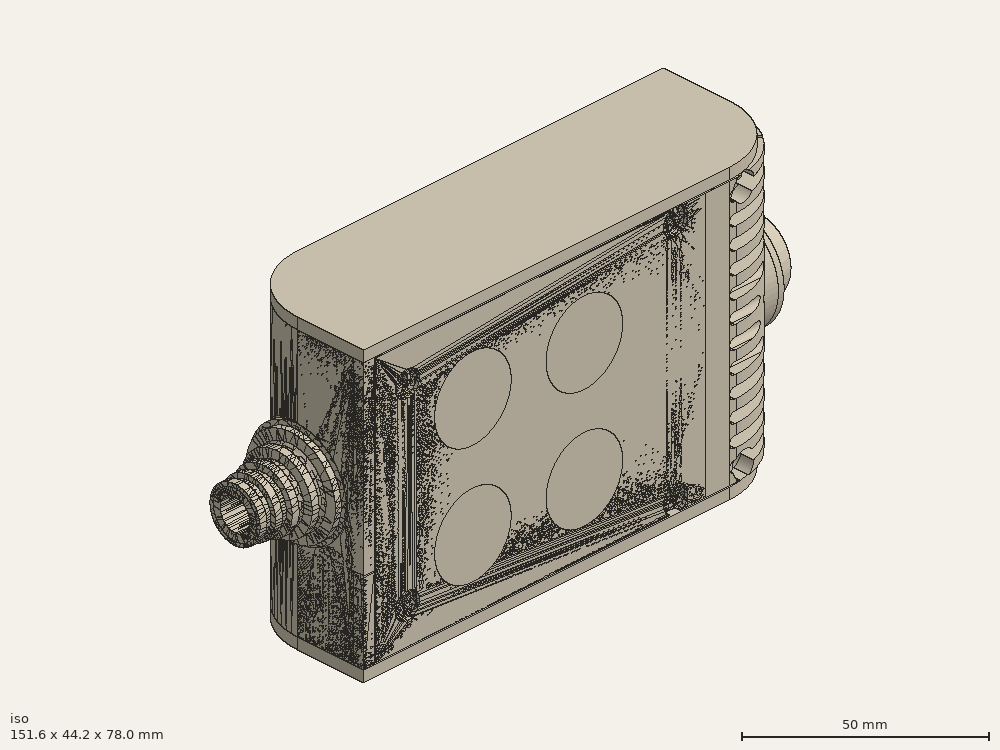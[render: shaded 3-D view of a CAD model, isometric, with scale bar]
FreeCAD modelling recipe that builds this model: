
FCSTD DOCUMENT  (FreeCAD 0.19R0.19.2)
Label: enclosure_170FCStd
License: All rights reserved
LicenseURL: http://en.wikipedia.org/wiki/All_rights_reserved
objects: Part::Revolution×146, Part::Feature×140, Part::MultiFuse×135, Sketcher::SketchObject×76, Part::Cut×63, Part::Cylinder×62, Part::Extrusion×61, Part::Fillet×54, Part::Box×36, App::MeasureDistance×4
note: 773 computed .brp shape members not serialized (recipe doc carries the construction recipe); baked Part::Feature solids carry a one-line shape summary decoded from their .brp

FEATURE [Sketcher::SketchObject] Sketch  label="topSketch"
  FullyConstrained = true
  sketch-geometry (20):
    g0: LineSegment StartX=5.21097e-06 StartY=3 StartZ=0 EndX=5.21097e-06 EndY=19 EndZ=0
    g1: ArcOfCircle CenterX=19 CenterY=19 CenterZ=0 NormalX=0 NormalY=0 NormalZ=1 AngleXU=0 Radius=19 StartAngle=1.5708 EndAngle=3.14159
    g2: ArcOfCircle CenterX=19 CenterY=19 CenterZ=0 NormalX=0 NormalY=0 NormalZ=1 AngleXU=0 Radius=16 StartAngle=1.5708 EndAngle=3.14159
    g3: LineSegment StartX=114 StartY=35 StartZ=0 EndX=19 EndY=35 EndZ=0
    g4: LineSegment StartX=5.21097e-06 StartY=3 StartZ=0 EndX=5.21097e-06 EndY=0 EndZ=0
    g5: LineSegment StartX=3 StartY=0 StartZ=0 EndX=5.21097e-06 EndY=0 EndZ=0
    g6: LineSegment StartX=3 StartY=19 StartZ=0 EndX=3 EndY=0 EndZ=0
    g7: LineSegment StartX=19 StartY=38 StartZ=0 EndX=124 EndY=38 EndZ=0
    g8: Circle CenterX=119 CenterY=35 CenterZ=0 NormalX=0 NormalY=0 NormalZ=1 AngleXU=0 Radius=1
    g9: Circle CenterX=121 CenterY=35 CenterZ=0 NormalX=0 NormalY=0 NormalZ=1 AngleXU=0 Radius=1
    g10: Circle CenterX=121 CenterY=33 CenterZ=0 NormalX=0 NormalY=0 NormalZ=1 AngleXU=0 Radius=1
    g11: BSplineCurve PolesCount=3 KnotsCount=2 Degree=2 IsPeriodic=0
    g12: GeomPoint X=119 Y=35 Z=0
    g13: GeomPoint X=121 Y=33 Z=0
    g14: LineSegment StartX=119 StartY=35 StartZ=0 EndX=114 EndY=35 EndZ=0
    g15: ArcOfCircle CenterX=105 CenterY=19 CenterZ=0 NormalX=0 NormalY=0 NormalZ=1 AngleXU=0 Radius=19 StartAngle=5.7297 EndAngle=6.28319
    g16: ArcOfCircle CenterX=105 CenterY=19 CenterZ=0 NormalX=0 NormalY=0 NormalZ=1 AngleXU=0 Radius=16 StartAngle=5.60905 EndAngle=6.28319
    g17: LineSegment StartX=121 StartY=33 StartZ=0 EndX=121 EndY=19 EndZ=0
    g18: LineSegment StartX=124 StartY=38 StartZ=0 EndX=124 EndY=19 EndZ=0
    g19: LineSegment StartX=117.5 StartY=9.01251 StartZ=0 EndX=121.163 EndY=9.0125 EndZ=0
  constraints (46):
    c: Vertical(g0)
    c: Block(g0)
    c: Coincident(g1,g0)
    c: Block(g1)
    c: Coincident(g2,g1)
    c: Block(g2)
    c: Coincident(g3,g2)
    c: Horizontal(g3)
    c: Tangent(g3,g2)
    c: Coincident(g4,g0)
    c: Distance(g4) = 3
    c: Vertical(g4)
    c: Coincident(g5,g4)
    c: Horizontal(g5)
    c: Coincident(g6,g2)
    c: Coincident(g6,g5)
    c: Vertical(g6)
    c: Horizontal(g7)
    c: Distance(g7) = 105
    c: Coincident(g7,g1)
    c: Block(g3)
    c: Weight(g8) = 1
    c: Equal(g8,g9)
    c: Equal(g8,g10)
    c: InternalAlignment(g8,g11)
    c: InternalAlignment(g9,g11)
    c: InternalAlignment(g10,g11)
    c: InternalAlignment(g12,g11)
    c: InternalAlignment(g13,g11)
    c: Block(g11)
    c: Coincident(g14,g11)
    c: Coincident(g14,g3)
    c: Horizontal(g14)
    c: Block(g15)
    c: Coincident(g16,g15)
    c: Block(g16)
    c: Coincident(g17,g11)
    c: Coincident(g17,g16)
    c: Vertical(g17)
    c: Distance(g17) = 14
    c: Coincident(g18,g7)
    c: Coincident(g18,g15)
    c: Vertical(g18)
    c: Distance(g18) = 19
    c: Coincident(g19,g16)
    c: Coincident(g19,g15)
FEATURE [Sketcher::SketchObject] Sketch001  label="bottomSketch"
  FullyConstrained = true
  sketch-geometry (32):
    g0: LineSegment StartX=3.3 StartY=-6.03275e-07 StartZ=0 EndX=98 EndY=-6.03275e-07 EndZ=0
    g1: ArcOfCircle CenterX=98 CenterY=19 CenterZ=0 NormalX=0 NormalY=0 NormalZ=1 AngleXU=0 Radius=19 StartAngle=4.71239 EndAngle=5.71103
    g2: LineSegment StartX=6.3 StartY=8 StartZ=0 EndX=3.3 EndY=8 EndZ=0
    g3: LineSegment StartX=3.3 StartY=8 StartZ=0 EndX=3.3 EndY=-6.03275e-07 EndZ=0
    g4: ArcOfCircle CenterX=8.3 CenterY=5 CenterZ=0 NormalX=0 NormalY=0 NormalZ=1 AngleXU=0 Radius=2 StartAngle=3.14159 EndAngle=4.71239
    g5: LineSegment StartX=6.3 StartY=8 StartZ=0 EndX=6.3 EndY=5 EndZ=0
    g6: ArcOfCircle CenterX=98 CenterY=19 CenterZ=0 NormalX=0 NormalY=0 NormalZ=1 AngleXU=0 Radius=12.7 StartAngle=4.71239 EndAngle=6.28319
    g7: LineSegment StartX=94.7 StartY=3 StartZ=0 EndX=8.3 EndY=3 EndZ=0
    g8-g12: Circle x5 (B-spline internal-alignment scaffolding for g13; pole/knot coordinates omitted)
    g13: BSplineCurve PolesCount=5 KnotsCount=3 Degree=3 IsPeriodic=0
    g14: GeomPoint X=98 Y=6.3 Z=0
    g15: GeomPoint X=96.3938 Y=4.71946 Z=0
    g16: GeomPoint X=94.7 Y=3 Z=0
    g17-g23: Circle x7 (B-spline internal-alignment scaffolding for g24; pole/knot coordinates omitted)
    g24: BSplineCurve PolesCount=7 KnotsCount=5 Degree=3 IsPeriodic=0
    g25-g29: GeomPoint x5 (B-spline internal-alignment scaffolding for g24; pole/knot coordinates omitted)
    g30: ArcOfCircle CenterX=98 CenterY=19 CenterZ=0 NormalX=0 NormalY=0 NormalZ=1 AngleXU=0 Radius=15.7 StartAngle=5.81226 EndAngle=6.28319
    g31: LineSegment StartX=110.7 StartY=19 StartZ=0 EndX=113.7 EndY=19 EndZ=0
  constraints (41):
    c: Horizontal(g0)
    c: Coincident(g1,g0)
    c: Block(g1)
    c: Horizontal(g2)
    c: Distance(g2) = 3
    c: Coincident(g3,g2)
    c: Vertical(g3)
    c: Coincident(g3,g0)
    c: Block(g4)
    c: Block(g2)
    c: Coincident(g5,g2)
    c: Coincident(g5,g4)
    c: Vertical(g5)
    c: Coincident(g6,g1)
    c: Block(g6)
    c: Coincident(g7,g4)
    c: Horizontal(g7)
    c: Block(g0)
    c: Block(g7)
    c: Block(g3)
    c: Coincident(g13,g6)
    c: Weight(g8) = 1
    c: Equal(g8, g9-g12) x4
    c: Coincident(g13,g7)
    c: InternalAlignment(g8-g12 -> g13) x5
    c: InternalAlignment(g14,g13)
    c: InternalAlignment(g15,g13)
    c: InternalAlignment(g16,g13)
    c: Block(g13)
    c: Weight(g17) = 1
    c: Equal(g17, g18-g23) x6
    c: Coincident(g24,g1)
    c: InternalAlignment(g17-g23 -> g24) x7
    c: InternalAlignment(g25-g29 -> g24) x5
    c: Block(g24)
    c: Coincident(g30,g24)
    c: Coincident(g31,g6)
    c: Coincident(g31,g30)
    c: Horizontal(g31)
    c: Block(g31)
    c: Block(g30)
FEATURE [Part::Extrusion] Extrude  label="top"
  Base = -> Sketch
  Dir = (0,0,1)
  DirMode = 2
  FaceMakerClass = Part::FaceMakerBullseye
  LengthFwd = 72
  LengthRev = 0
  Solid = true
  Symmetric = false
FEATURE [Part::Extrusion] Extrude001  label="bottom"
  Base = -> Sketch001
  Dir = (0,0,1)
  DirMode = 2
  FaceMakerClass = Part::FaceMakerBullseye
  LengthFwd = 71.4
  LengthRev = 0
  Placement = pos=(0,0,0.3) rot=(0,0,1;0rad)
  Solid = true
  Symmetric = false
FEATURE [Sketcher::SketchObject] Sketch002  label="topSketch001"
  FullyConstrained = true
  sketch-geometry (6):
    g0: ArcOfCircle CenterX=19 CenterY=19 CenterZ=0 NormalX=0 NormalY=0 NormalZ=1 AngleXU=0 Radius=19 StartAngle=1.5708 EndAngle=3.14159
    g1: LineSegment StartX=5.22862e-06 StartY=19 StartZ=0 EndX=5.22862e-06 EndY=1.19904e-11 EndZ=0
    g2: LineSegment StartX=19 StartY=38 StartZ=0 EndX=124 EndY=38 EndZ=0
    g3: LineSegment StartX=5.22862e-06 StartY=1.19904e-11 StartZ=0 EndX=105 EndY=1.19904e-11 EndZ=0
    g4: ArcOfCircle CenterX=105 CenterY=19 CenterZ=0 NormalX=0 NormalY=0 NormalZ=1 AngleXU=0 Radius=19 StartAngle=4.71239 EndAngle=6.28319
    g5: LineSegment StartX=124 StartY=38 StartZ=0 EndX=124 EndY=19 EndZ=0
  constraints (16):
    c: Block(g0)
    c: Coincident(g1,g0)
    c: Vertical(g1)
    c: Horizontal(g2)
    c: Distance(g2) = 105
    c: Coincident(g2,g0)
    c: Distance(g1) = 19
    c: Coincident(g3,g1)
    c: Horizontal(g3)
    c: Distance(g3) = 105
    c: Block(g4)
    c: Coincident(g4,g3)
    c: Coincident(g5,g2)
    c: Coincident(g5,g4)
    c: Vertical(g5)
    c: Distance(g5) = 19
FEATURE [Part::Extrusion] Extrude002  label="sideA"
  Base = -> Sketch002
  Dir = (0,0,1)
  DirMode = 2
  FaceMakerClass = Part::FaceMakerBullseye
  LengthFwd = 3
  LengthRev = 0
  Placement = pos=(0,0,-3) rot=(0,0,1;0rad)
  Solid = true
  Symmetric = false
FEATURE [Sketcher::SketchObject] Sketch003  label="topSketch002"
  FullyConstrained = true
  sketch-geometry (6):
    g0: LineSegment StartX=19 StartY=38 StartZ=0 EndX=117 EndY=38 EndZ=0
    g1: ArcOfCircle CenterX=19 CenterY=19 CenterZ=0 NormalX=0 NormalY=0 NormalZ=1 AngleXU=0 Radius=19 StartAngle=1.5708 EndAngle=3.14159
    g2: LineSegment StartX=117 StartY=38 StartZ=0 EndX=117 EndY=19 EndZ=0
    g3: LineSegment StartX=98 StartY=1.0161e-12 StartZ=0 EndX=5.22862e-06 EndY=1.0161e-12 EndZ=0
    g4: LineSegment StartX=5.22862e-06 StartY=19 StartZ=0 EndX=5.22862e-06 EndY=1.0161e-12 EndZ=0
    g5: ArcOfCircle CenterX=98 CenterY=19 CenterZ=0 NormalX=0 NormalY=0 NormalZ=1 AngleXU=0 Radius=19 StartAngle=4.71239 EndAngle=6.28319
  constraints (16):
    c: Horizontal(g0)
    c: Distance(g0) = 98
    c: Coincident(g1,g0)
    c: Block(g1)
    c: Coincident(g2,g0)
    c: Vertical(g2)
    c: Distance(g2) = 19
    c: Horizontal(g3)
    c: Coincident(g4,g1)
    c: Vertical(g4)
    c: Coincident(g3,g4)
    c: Block(g3)
    c: Coincident(g5,g2)
    c: Coincident(g5,g3)
    c: Block(g0)
    c: Block(g5)
FEATURE [Sketcher::SketchObject] Sketch004
  FullyConstrained = true
  MapMode = 3
  Placement = pos=(0,0,0) rot=(1,0,0;1.5708rad)
  Support = -> [Extrude]
  sketch-geometry (8):
    g0: Circle CenterX=80.351 CenterY=-67.6202 CenterZ=0 NormalX=0 NormalY=0 NormalZ=1 AngleXU=0 Radius=2
    g1: Circle CenterX=80.351 CenterY=-67.6202 CenterZ=0 NormalX=0 NormalY=0 NormalZ=1 AngleXU=0 Radius=3
    g2: Circle CenterX=80.351 CenterY=-4.92017 CenterZ=0 NormalX=0 NormalY=0 NormalZ=1 AngleXU=0 Radius=2
    g3: Circle CenterX=80.351 CenterY=-4.92017 CenterZ=0 NormalX=0 NormalY=0 NormalZ=1 AngleXU=0 Radius=3
    g4: Circle CenterX=23.851 CenterY=-4.92017 CenterZ=0 NormalX=0 NormalY=0 NormalZ=1 AngleXU=0 Radius=2
    g5: Circle CenterX=23.851 CenterY=-4.92017 CenterZ=0 NormalX=0 NormalY=0 NormalZ=1 AngleXU=0 Radius=3
    g6: Circle CenterX=23.851 CenterY=-67.6202 CenterZ=0 NormalX=0 NormalY=0 NormalZ=1 AngleXU=0 Radius=2
    g7: Circle CenterX=23.851 CenterY=-67.6202 CenterZ=0 NormalX=0 NormalY=0 NormalZ=1 AngleXU=0 Radius=3
  constraints (8):
    c: Block(g3)
    c: Block(g2)
    c: Block(g1)
    c: Block(g0)
    c: Block(g6)
    c: Block(g7)
    c: Block(g4)
    c: Block(g5)
FEATURE [Part::Extrusion] Extrude004
  Base = -> Sketch004
  Dir = (0,-1,2e-16)
  DirMode = 2
  FaceMakerClass = Part::FaceMakerBullseye
  LengthFwd = 6
  LengthRev = 0
  Placement = pos=(0,9,0) rot=(0,0,1;0rad)
  Solid = true
  Symmetric = false
FEATURE [Sketcher::SketchObject] Sketch005
  FullyConstrained = true
  MapMode = 3
  Placement = pos=(0,0,0) rot=(1,0,0;1.5708rad)
  Support = -> [Extrude]
  sketch-geometry (8):
    g0: Circle CenterX=80.351 CenterY=-67.6202 CenterZ=0 NormalX=0 NormalY=0 NormalZ=1 AngleXU=0 Radius=3
    g1: Circle CenterX=80.351 CenterY=-4.92017 CenterZ=0 NormalX=0 NormalY=0 NormalZ=1 AngleXU=0 Radius=3
    g2: Circle CenterX=23.851 CenterY=-4.92017 CenterZ=0 NormalX=0 NormalY=0 NormalZ=1 AngleXU=0 Radius=3
    g3: Circle CenterX=23.851 CenterY=-67.6202 CenterZ=0 NormalX=0 NormalY=0 NormalZ=1 AngleXU=0 Radius=3
    g4: Circle CenterX=23.851 CenterY=-67.6202 CenterZ=0 NormalX=0 NormalY=0 NormalZ=1 AngleXU=0 Radius=5
    g5: Circle CenterX=80.351 CenterY=-67.6202 CenterZ=0 NormalX=0 NormalY=0 NormalZ=1 AngleXU=0 Radius=5
    g6: Circle CenterX=23.851 CenterY=-4.92017 CenterZ=0 NormalX=0 NormalY=0 NormalZ=1 AngleXU=0 Radius=5
    g7: Circle CenterX=80.351 CenterY=-4.92017 CenterZ=0 NormalX=0 NormalY=0 NormalZ=1 AngleXU=0 Radius=5
  constraints (8):
    c: Block(g1)
    c: Block(g0)
    c: Block(g3)
    c: Block(g2)
    c: Block(g5)
    c: Block(g4)
    c: Block(g6)
    c: Block(g7)
FEATURE [Part::Extrusion] Extrude005
  Base = -> Sketch005
  Dir = (0,-1,2e-16)
  DirMode = 2
  FaceMakerClass = Part::FaceMakerBullseye
  LengthFwd = 2
  LengthRev = 0
  Solid = true
  Symmetric = false
FEATURE [Sketcher::SketchObject] Sketch006
  FullyConstrained = true
  MapMode = 3
  Placement = pos=(0,0,0) rot=(1,0,0;1.5708rad)
  sketch-geometry (8):
    g0: Circle CenterX=80.351 CenterY=-67.6202 CenterZ=0 NormalX=0 NormalY=0 NormalZ=1 AngleXU=0 Radius=3
    g1: Circle CenterX=80.351 CenterY=-4.92017 CenterZ=0 NormalX=0 NormalY=0 NormalZ=1 AngleXU=0 Radius=3
    g2: Circle CenterX=23.851 CenterY=-4.92017 CenterZ=0 NormalX=0 NormalY=0 NormalZ=1 AngleXU=0 Radius=3
    g3: Circle CenterX=23.851 CenterY=-67.6202 CenterZ=0 NormalX=0 NormalY=0 NormalZ=1 AngleXU=0 Radius=3
    g4: Circle CenterX=23.851 CenterY=-67.6202 CenterZ=0 NormalX=0 NormalY=0 NormalZ=1 AngleXU=0 Radius=5
    g5: Circle CenterX=80.351 CenterY=-67.6202 CenterZ=0 NormalX=0 NormalY=0 NormalZ=1 AngleXU=0 Radius=5
    g6: Circle CenterX=23.851 CenterY=-4.92017 CenterZ=0 NormalX=0 NormalY=0 NormalZ=1 AngleXU=0 Radius=5
    g7: Circle CenterX=80.351 CenterY=-4.92017 CenterZ=0 NormalX=0 NormalY=0 NormalZ=1 AngleXU=0 Radius=5
  constraints (8):
    c: Block(g1)
    c: Block(g0)
    c: Block(g3)
    c: Block(g2)
    c: Block(g5)
    c: Block(g4)
    c: Block(g6)
    c: Block(g7)
FEATURE [Part::Extrusion] Extrude007
  Base = -> Sketch006
  Dir = (0,-1,2e-16)
  DirMode = 2
  FaceMakerClass = Part::FaceMakerBullseye
  LengthFwd = 2
  LengthRev = 0
  Solid = true
  Symmetric = false
FEATURE [Part::Fillet] Fillet
  Base = -> Extrude007
  Edges = 4 edges r=1.99: [Edge6,Edge12,Edge18,Edge24]
FEATURE [Part::Cut] Cut
  Base = -> Extrude005
  Placement = pos=(0,5,0) rot=(0,0,1;0rad)
  Tool = -> Fillet
FEATURE [Part::MultiFuse] Fusion  label="pCBScrews"
  Placement = pos=(-2.5,0,72.3) rot=(0,0,1;0rad)
  Shapes = -> [Extrude004,Cut]
FEATURE [App::MeasureDistance] Distance  label="Distance: 0.69 mm"
  Distance = 0.685967
  P1 = (24.0138,2.9647,0.3)
  P2 = (23.8901,3,-0.373787)
FEATURE [App::MeasureDistance] Distance001  label="Distance: 0.53 mm"
  Distance = 0.533607
  P1 = (80.2939,3,72.2334)
  P2 = (80.281,2.99661,71.7)
FEATURE [Part::Fillet] Fillet001
  Base = -> Extrude001
  Edges = 1 edges r=2.4: [Edge17]
FEATURE [Part::Fillet] Fillet002  label="bottom001"
  Base = -> Fillet001
  Edges = 1 edges r=2.4: [Edge36]
FEATURE [Part::Fillet] Fillet003  label="top001"
  Base = -> Extrude
  Edges = 1 edges r=2: [Edge1]
FEATURE [Sketcher::SketchObject] Sketch007
  FullyConstrained = true
  sketch-geometry (16):
    g0: LineSegment StartX=4 StartY=0 StartZ=0 EndX=4 EndY=2.4 EndZ=0
    g1: LineSegment StartX=4 StartY=2.4 StartZ=0 EndX=7 EndY=2.4 EndZ=0
    g2: LineSegment StartX=4 StartY=0 StartZ=0 EndX=5.7 EndY=0 EndZ=0
    g3: LineSegment StartX=5.7 StartY=0 StartZ=0 EndX=5.7 EndY=-5.6 EndZ=0
    g4-g8: Circle x5 (B-spline internal-alignment scaffolding for g9; pole/knot coordinates omitted)
    g9: BSplineCurve PolesCount=5 KnotsCount=3 Degree=3 IsPeriodic=0
    g10: GeomPoint X=7 Y=2.4 Z=0
    g11: GeomPoint X=10.4582 Y=-1.55472 Z=0
    g12: GeomPoint X=14 Y=-5.6 Z=0
    g13: LineSegment StartX=14 StartY=-5.6 StartZ=0 EndX=14 EndY=-14.1 EndZ=0
    g14: LineSegment StartX=14 StartY=-14.1 StartZ=0 EndX=6.5 EndY=-14.1 EndZ=0
    g15: LineSegment StartX=5.7 StartY=-5.6 StartZ=0 EndX=6.5 EndY=-14.1 EndZ=0
  constraints (28):
    c: Distance(g0) = 2.4
    c: Vertical(g0)
    c: Block(g0)
    c: Coincident(g1,g0)
    c: Horizontal(g1)
    c: Distance(g1) = 3
    c: Coincident(g2,g0)
    c: Horizontal(g2)
    c: Distance(g2) = 1.7
    c: Coincident(g3,g2)
    c: Vertical(g3)
    c: Distance(g3) = 5.6
    c: Coincident(g9,g1)
    c: Weight(g4) = 1
    c: Equal(g4, g5-g8) x4
    c: InternalAlignment(g4-g8 -> g9) x5
    c: InternalAlignment(g10,g9)
    c: InternalAlignment(g11,g9)
    c: InternalAlignment(g12,g9)
    c: Block(g9)
    c: Coincident(g13,g9)
    c: Vertical(g13)
    c: Distance(g13) = 8.5
    c: Coincident(g14,g13)
    c: Horizontal(g14)
    c: Distance(g14) = 7.5
    c: Coincident(g15,g3)
    c: Coincident(g15,g14)
FEATURE [Part::Feature] Face
  shape: bbox 10 x 16.5 x 2e-07 mm, 1 faces, 0 solids (baked)
FEATURE [Part::Revolution] Revolve  label="plugHousing"
  Angle = 360
  Axis = (0,1,0)
  Base = (0,0,0)
  FaceMakerClass = Part::FaceMakerBullseye
  Placement = pos=(0,0,36.15) rot=(0,0,1;0rad)
  Solid = false
  Source = -> Face
  Symmetric = false
FEATURE [Part::Feature] Face001
  shape: bbox 10 x 16.5 x 2e-07 mm, 1 faces, 0 solids (baked)
FEATURE [Part::Revolution] Revolve001  label="plugHousing001"
  Angle = 360
  Axis = (0,1,0)
  Base = (0,0,0)
  FaceMakerClass = Part::FaceMakerBullseye
  Placement = pos=(0,0,36.15) rot=(0,0,1;0rad)
  Solid = false
  Source = -> Face001
  Symmetric = false
FEATURE [Part::MultiFuse] Fusion001  label="plugHousing002"
  Placement = pos=(0,0,0) rot=(0,0,1;1.5708rad)
  Shapes = -> [Revolve001,Revolve]
FEATURE [Part::Feature] Face002
  shape: bbox 10 x 16.5 x 2e-07 mm, 1 faces, 0 solids (baked)
FEATURE [Part::Revolution] Revolve003  label="plugHousing005"
  Angle = 360
  Axis = (0,1,0)
  Base = (0,0,0)
  FaceMakerClass = Part::FaceMakerBullseye
  Placement = pos=(0,0,36.15) rot=(0,0,1;0rad)
  Solid = false
  Source = -> Face002
  Symmetric = false
FEATURE [Part::Feature] Face003
  shape: bbox 10 x 16.5 x 2e-07 mm, 1 faces, 0 solids (baked)
FEATURE [Part::Revolution] Revolve002  label="plugHousing003"
  Angle = 360
  Axis = (0,1,0)
  Base = (0,0,0)
  FaceMakerClass = Part::FaceMakerBullseye
  Placement = pos=(0,0,36.15) rot=(0,0,1;0rad)
  Solid = false
  Source = -> Face003
  Symmetric = false
FEATURE [Part::MultiFuse] Fusion002  label="plugHousing004"
  Placement = pos=(0,0,0) rot=(0,0,1;1.5708rad)
  Shapes = -> [Revolve002,Revolve003]
FEATURE [Part::MultiFuse] Fusion003  label="plugHousing006"
  Placement = pos=(0,19,0) rot=(0,0,1;3.14159rad)
  Shapes = -> [Fusion002,Fusion001]
FEATURE [Part::Feature] Face004
  shape: bbox 10 x 16.5 x 2e-07 mm, 1 faces, 0 solids (baked)
FEATURE [Part::Revolution] Revolve006  label="plugHousing010"
  Angle = 360
  Axis = (0,1,0)
  Base = (0,0,0)
  FaceMakerClass = Part::FaceMakerBullseye
  Placement = pos=(0,0,36.15) rot=(0,0,1;0rad)
  Solid = false
  Source = -> Face004
  Symmetric = false
FEATURE [Part::Feature] Face005
  shape: bbox 10 x 16.5 x 2e-07 mm, 1 faces, 0 solids (baked)
FEATURE [Part::Revolution] Revolve007  label="plugHousing011"
  Angle = 360
  Axis = (0,1,0)
  Base = (0,0,0)
  FaceMakerClass = Part::FaceMakerBullseye
  Placement = pos=(0,0,36.15) rot=(0,0,1;0rad)
  Solid = false
  Source = -> Face005
  Symmetric = false
FEATURE [Part::Feature] Face006
  shape: bbox 10 x 16.5 x 2e-07 mm, 1 faces, 0 solids (baked)
FEATURE [Part::Revolution] Revolve004  label="plugHousing007"
  Angle = 360
  Axis = (0,1,0)
  Base = (0,0,0)
  FaceMakerClass = Part::FaceMakerBullseye
  Placement = pos=(0,0,36.15) rot=(0,0,1;0rad)
  Solid = false
  Source = -> Face006
  Symmetric = false
FEATURE [Part::MultiFuse] Fusion004  label="plugHousing009"
  Placement = pos=(0,0,0) rot=(0,0,1;1.5708rad)
  Shapes = -> [Revolve004,Revolve007]
FEATURE [Part::Feature] Face007
  shape: bbox 10 x 16.5 x 2e-07 mm, 1 faces, 0 solids (baked)
FEATURE [Part::Revolution] Revolve005  label="plugHousing008"
  Angle = 360
  Axis = (0,1,0)
  Base = (0,0,0)
  FaceMakerClass = Part::FaceMakerBullseye
  Placement = pos=(0,0,36.15) rot=(0,0,1;0rad)
  Solid = false
  Source = -> Face007
  Symmetric = false
FEATURE [Part::MultiFuse] Fusion005  label="plugHousing012"
  Placement = pos=(0,0,0) rot=(0,0,1;1.5708rad)
  Shapes = -> [Revolve006,Revolve005]
FEATURE [Part::MultiFuse] Fusion006  label="plugHousing013"
  Placement = pos=(0,19,0) rot=(0,0,1;3.14159rad)
  Shapes = -> [Fusion005,Fusion004]
FEATURE [Part::MultiFuse] Fusion007  label="plugHousing014"
  Placement = pos=(122.621,0,-0.15) rot=(0,0,1;0rad)
  Shapes = -> [Fusion003,Fusion006]
FEATURE [Part::Cylinder] Cylinder002
  Angle = 360
  AttacherType = Attacher::AttachEngine3D
  Height = 20
  Placement = pos=(0,0,36.15) rot=(0,0,1;0rad)
  Radius = 4
FEATURE [Part::Cylinder] Cylinder003
  Angle = 360
  AttacherType = Attacher::AttachEngine3D
  Height = 10
  Placement = pos=(0,0,36.15) rot=(0,0,1;0rad)
  Radius = 4
FEATURE [Part::MultiFuse] Fusion009  label="removeToCreateHoleForPlugHousing"
  Placement = pos=(70,19,36.15) rot=(0,1,0;1.5708rad)
  Shapes = -> [Cylinder002,Cylinder003]
FEATURE [Part::Cylinder] Cylinder004
  Angle = 360
  AttacherType = Attacher::AttachEngine3D
  Height = 20
  Placement = pos=(0,0,36.15) rot=(0,0,1;0rad)
  Radius = 4
FEATURE [Part::Cylinder] Cylinder005
  Angle = 360
  AttacherType = Attacher::AttachEngine3D
  Height = 10
  Placement = pos=(0,0,36.15) rot=(0,0,1;0rad)
  Radius = 4
FEATURE [Part::MultiFuse] Fusion010  label="removeToCreateHoleForPlugHousing001"
  Placement = pos=(70,19,36.15) rot=(0,1,0;1.5708rad)
  Shapes = -> [Cylinder004,Cylinder005]
FEATURE [Part::Cut] Cut001
  Base = -> Fillet003
  Tool = -> Fusion010
FEATURE [Part::Cut] Cut002  label="Bottom"
  Base = -> Fillet002
  Tool = -> Fusion009
FEATURE [Part::Feature] Face008
  shape: bbox 10 x 16.5 x 2e-07 mm, 1 faces, 0 solids (baked)
FEATURE [Part::Revolution] Revolve011  label="plugHousing021"
  Angle = 360
  Axis = (0,1,0)
  Base = (0,0,0)
  FaceMakerClass = Part::FaceMakerBullseye
  Placement = pos=(0,0,36.15) rot=(0,0,1;0rad)
  Solid = false
  Source = -> Face008
  Symmetric = false
FEATURE [Part::Feature] Face009
  shape: bbox 10 x 16.5 x 2e-07 mm, 1 faces, 0 solids (baked)
FEATURE [Part::Revolution] Revolve012  label="plugHousing022"
  Angle = 360
  Axis = (0,1,0)
  Base = (0,0,0)
  FaceMakerClass = Part::FaceMakerBullseye
  Placement = pos=(0,0,36.15) rot=(0,0,1;0rad)
  Solid = false
  Source = -> Face009
  Symmetric = false
FEATURE [Part::Feature] Face010 .. Face013  x4 (patterned run collapsed; names and placements below)
  shape: bbox 10 x 16.5 x 2e-07 mm, 1 faces, 0 solids (baked)
FEATURE [Part::Revolution] Revolve015  label="plugHousing027"
  Angle = 360
  Axis = (0,1,0)
  Base = (0,0,0)
  FaceMakerClass = Part::FaceMakerBullseye
  Placement = pos=(0,0,36.15) rot=(0,0,1;0rad)
  Solid = false
  Source = -> Face013
  Symmetric = false
FEATURE [Part::Feature] Face014
  shape: bbox 10 x 16.5 x 2e-07 mm, 1 faces, 0 solids (baked)
FEATURE [Part::Feature] Face015
  shape: bbox 10 x 16.5 x 2e-07 mm, 1 faces, 0 solids (baked)
FEATURE [Part::Feature] Face016
  shape: bbox 10 x 16.5 x 2e-07 mm, 1 faces, 0 solids (baked)
FEATURE [Part::Revolution] Revolve019  label="plugHousing033"
  Angle = 360
  Axis = (0,1,0)
  Base = (0,0,0)
  FaceMakerClass = Part::FaceMakerBullseye
  Placement = pos=(0,0,36.15) rot=(0,0,1;0rad)
  Solid = false
  Source = -> Face016
  Symmetric = false
FEATURE [Part::Feature] Face017
  shape: bbox 10 x 16.5 x 2e-07 mm, 1 faces, 0 solids (baked)
FEATURE [Part::Revolution] Revolve020  label="plugHousing034"
  Angle = 360
  Axis = (0,1,0)
  Base = (0,0,0)
  FaceMakerClass = Part::FaceMakerBullseye
  Placement = pos=(0,0,36.15) rot=(0,0,1;0rad)
  Solid = false
  Source = -> Face017
  Symmetric = false
FEATURE [Part::Feature] Face018
  shape: bbox 10 x 16.5 x 2e-07 mm, 1 faces, 0 solids (baked)
FEATURE [Part::Revolution] Revolve016  label="plugHousing030"
  Angle = 360
  Axis = (0,1,0)
  Base = (0,0,0)
  FaceMakerClass = Part::FaceMakerBullseye
  Placement = pos=(0,0,36.15) rot=(0,0,1;0rad)
  Solid = false
  Source = -> Face018
  Symmetric = false
FEATURE [Part::MultiFuse] Fusion020  label="plugHousing038"
  Placement = pos=(0,0,0) rot=(0,0,1;1.5708rad)
  Shapes = -> [Revolve016,Revolve020]
FEATURE [Part::Feature] Face019
  shape: bbox 10 x 16.5 x 2e-07 mm, 1 faces, 0 solids (baked)
FEATURE [Part::Feature] Face020
  shape: bbox 10 x 16.5 x 2e-07 mm, 1 faces, 0 solids (baked)
FEATURE [Part::Revolution] Revolve017  label="plugHousing031"
  Angle = 360
  Axis = (0,1,0)
  Base = (0,0,0)
  FaceMakerClass = Part::FaceMakerBullseye
  Placement = pos=(0,0,36.15) rot=(0,0,1;0rad)
  Solid = false
  Source = -> Face020
  Symmetric = false
FEATURE [Part::MultiFuse] Fusion021  label="plugHousing039"
  Placement = pos=(0,0,0) rot=(0,0,1;1.5708rad)
  Shapes = -> [Revolve019,Revolve017]
FEATURE [Part::MultiFuse] Fusion023  label="plugHousing041"
  Placement = pos=(0,19,0) rot=(0,0,1;3.14159rad)
  Shapes = -> [Fusion021,Fusion020]
FEATURE [Part::Revolution] Revolve022  label="plugHousing043"
  Angle = 360
  Axis = (0,1,0)
  Base = (0,0,0)
  FaceMakerClass = Part::FaceMakerBullseye
  Placement = pos=(0,0,36.15) rot=(0,0,1;0rad)
  Solid = false
  Source = -> Face019
  Symmetric = false
FEATURE [Part::Feature] Face021
  shape: bbox 10 x 16.5 x 2e-07 mm, 1 faces, 0 solids (baked)
FEATURE [Part::Revolution] Revolve023  label="plugHousing044"
  Angle = 360
  Axis = (0,1,0)
  Base = (0,0,0)
  FaceMakerClass = Part::FaceMakerBullseye
  Placement = pos=(0,0,36.15) rot=(0,0,1;0rad)
  Solid = false
  Source = -> Face021
  Symmetric = false
FEATURE [Part::Feature] Face022
  shape: bbox 10 x 16.5 x 2e-07 mm, 1 faces, 0 solids (baked)
FEATURE [Part::Revolution] Revolve018  label="plugHousing032"
  Angle = 360
  Axis = (0,1,0)
  Base = (0,0,0)
  FaceMakerClass = Part::FaceMakerBullseye
  Placement = pos=(0,0,36.15) rot=(0,0,1;0rad)
  Solid = false
  Source = -> Face022
  Symmetric = false
FEATURE [Part::MultiFuse] Fusion022  label="plugHousing040"
  Placement = pos=(0,0,0) rot=(0,0,1;1.5708rad)
  Shapes = -> [Revolve018,Revolve023]
FEATURE [Part::Feature] Face023
  shape: bbox 10 x 16.5 x 2e-07 mm, 1 faces, 0 solids (baked)
FEATURE [Part::Revolution] Revolve021  label="plugHousing035"
  Angle = 360
  Axis = (0,1,0)
  Base = (0,0,0)
  FaceMakerClass = Part::FaceMakerBullseye
  Placement = pos=(0,0,36.15) rot=(0,0,1;0rad)
  Solid = false
  Source = -> Face023
  Symmetric = false
FEATURE [Part::MultiFuse] Fusion018  label="plugHousing036"
  Placement = pos=(0,0,0) rot=(0,0,1;1.5708rad)
  Shapes = -> [Revolve022,Revolve021]
FEATURE [Part::MultiFuse] Fusion019  label="plugHousing037"
  Placement = pos=(0,19,0) rot=(0,0,1;3.14159rad)
  Shapes = -> [Fusion018,Fusion022]
FEATURE [Part::MultiFuse] Fusion024  label="plugHousing042"
  Placement = pos=(122.621,0,-0.15) rot=(0,0,1;0rad)
  Shapes = -> [Fusion023,Fusion019]
FEATURE [Part::Cylinder] Cylinder006
  Angle = 360
  AttacherType = Attacher::AttachEngine3D
  Height = 20
  Placement = pos=(0,0,36.15) rot=(0,0,1;0rad)
  Radius = 14.3
FEATURE [Part::Cylinder] Cylinder007
  Angle = 360
  AttacherType = Attacher::AttachEngine3D
  Height = 10
  Placement = pos=(0,0,36.15) rot=(0,0,1;0rad)
  Radius = 4
FEATURE [Part::MultiFuse] Fusion026  label="removeToCreteHoleForPlugHousing"
  Placement = pos=(70,19,36) rot=(0,1,0;1.5708rad)
  Shapes = -> [Cylinder006,Cylinder007]
FEATURE [Part::Box] Box001  label="Cube001"
  AttacherType = Attacher::AttachEngine3D
  Height = 28
  Length = 3
  Placement = pos=(110.7,19,22) rot=(0,0,1;0rad)
  Width = 15.7
FEATURE [Part::Cut] Cut003  label="top002"
  Base = -> Cut001
  Tool = -> Fusion007
FEATURE [Part::Revolution] Revolve008  label="plugHousing015"
  Angle = 360
  Axis = (0,1,0)
  Base = (0,0,0)
  FaceMakerClass = Part::FaceMakerBullseye
  Placement = pos=(0,0,36.15) rot=(0,0,1;0rad)
  Solid = false
  Source = -> Face010
  Symmetric = false
FEATURE [Part::MultiFuse] Fusion013  label="plugHousing020"
  Placement = pos=(0,0,0) rot=(0,0,1;1.5708rad)
  Shapes = -> [Revolve008,Revolve012]
FEATURE [Part::Cut] Cut004  label="top003"
  Base = -> Cut003
  Placement = pos=(1,0,0) rot=(0,0,1;0rad)
  Tool = -> Fusion026
FEATURE [Part::Cylinder] Cylinder008
  Angle = 360
  AttacherType = Attacher::AttachEngine3D
  Height = 20
  Placement = pos=(0,0,36.15) rot=(0,0,1;0rad)
  Radius = 10.3
FEATURE [Part::Cylinder] Cylinder009
  Angle = 360
  AttacherType = Attacher::AttachEngine3D
  Height = 10
  Placement = pos=(0,0,36.15) rot=(0,0,1;0rad)
  Radius = 4
FEATURE [Part::MultiFuse] Fusion027  label="removeToCreteHoleForPlugHousing001"
  Placement = pos=(70,19,36) rot=(0,1,0;1.5708rad)
  Shapes = -> [Cylinder008,Cylinder009]
FEATURE [Part::Cut] Cut005  label="plugHousingTab"
  Base = -> Box001
  Tool = -> Fusion027
FEATURE [Part::MultiFuse] Fusion028  label="plugHousing045"
  Shapes = -> [Fusion024,Cut005]
FEATURE [Part::Box] Box002  label="Cube002"
  AttacherType = Attacher::AttachEngine3D
  Height = 28.8
  Length = 3
  Placement = pos=(107.3,28,21.6) rot=(0,0,1;0rad)
  Width = 7
FEATURE [Part::Box] Box003  label="Cube003"
  AttacherType = Attacher::AttachEngine3D
  Height = 3
  Length = 6.4
  Placement = pos=(107.3,28,18.6) rot=(0,0,1;0rad)
  Width = 7
FEATURE [Part::Box] Box004  label="Cube004"
  AttacherType = Attacher::AttachEngine3D
  Height = 3
  Length = 6.4
  Placement = pos=(107.3,28,50.4) rot=(0,0,1;0rad)
  Width = 7
FEATURE [Part::MultiFuse] Fusion029  label="plugHousingBracketHolder"
  Shapes = -> [Box004,Box002,Box003]
FEATURE [Part::Cylinder] Cylinder010
  Angle = 360
  AttacherType = Attacher::AttachEngine3D
  Height = 20
  Placement = pos=(0,0,36.15) rot=(0,0,1;0rad)
  Radius = 14.3
FEATURE [Part::Cylinder] Cylinder011
  Angle = 360
  AttacherType = Attacher::AttachEngine3D
  Height = 10
  Placement = pos=(0,0,36.15) rot=(0,0,1;0rad)
  Radius = 4
FEATURE [Part::MultiFuse] Fusion030  label="removeToCreteHoleForPlugHousing002"
  Placement = pos=(70,19,36) rot=(0,1,0;1.5708rad)
  Shapes = -> [Cylinder010,Cylinder011]
FEATURE [Part::Cut] Cut006  label="plugHousingBracketHolder001"
  Base = -> Fusion029
  Tool = -> Fusion030
FEATURE [Part::Cylinder] Cylinder012
  Angle = 360
  AttacherType = Attacher::AttachEngine3D
  Height = 20
  Placement = pos=(0,0,36.15) rot=(0,0,1;0rad)
  Radius = 7
FEATURE [Part::Cylinder] Cylinder013
  Angle = 360
  AttacherType = Attacher::AttachEngine3D
  Height = 10
  Placement = pos=(0,0,36.15) rot=(0,0,1;0rad)
  Radius = 4
FEATURE [Part::MultiFuse] Fusion032  label="removeToCreteHoleForPlugHousing003"
  Placement = pos=(70,19,36) rot=(0,1,0;1.5708rad)
  Shapes = -> [Cylinder012,Cylinder013]
FEATURE [Part::Cut] Cut007  label="bottom002"
  Base = -> Cut002
  Tool = -> Fusion032
FEATURE [Sketcher::SketchObject] Sketch008
  FullyConstrained = true
  sketch-geometry (54):
    g0: LineSegment StartX=-4.2 StartY=0 StartZ=0 EndX=-6.2 EndY=0 EndZ=0
    g1: LineSegment StartX=-14 StartY=-18 StartZ=0 EndX=-14 EndY=-26.5 EndZ=0
    g2: LineSegment StartX=-4.2 StartY=0 StartZ=0 EndX=-4.2 EndY=-13.4877 EndZ=0
    g3: Circle CenterX=-4.2 CenterY=-13.4877 CenterZ=0 NormalX=0 NormalY=0 NormalZ=1 AngleXU=0 Radius=1
    g4: Circle CenterX=-4.2 CenterY=-26.5 CenterZ=0 NormalX=0 NormalY=0 NormalZ=1 AngleXU=0 Radius=1
    g5: Circle CenterX=-8.2 CenterY=-26.5 CenterZ=0 NormalX=0 NormalY=0 NormalZ=1 AngleXU=0 Radius=1
    g6: BSplineCurve PolesCount=3 KnotsCount=2 Degree=2 IsPeriodic=0
    g7: GeomPoint X=-4.2 Y=-13.4877 Z=0
    g8: GeomPoint X=-8.2 Y=-26.5 Z=0
    g9: LineSegment StartX=-14 StartY=-26.5 StartZ=0 EndX=-8.2 EndY=-26.5 EndZ=0
    g10: LineSegment StartX=-10.15 StartY=-12 StartZ=0 EndX=-10.15 EndY=-14 EndZ=0
    g11: LineSegment StartX=-12.8401 StartY=-16 StartZ=0 EndX=-10.1571 EndY=-16 EndZ=0
    g12: LineSegment StartX=-10.15 StartY=-14 StartZ=0 EndX=-8.70761 EndY=-14 EndZ=0
    g13: LineSegment StartX=-12.8401 StartY=-16 StartZ=0 EndX=-12.8401 EndY=-17.6958 EndZ=0
    g14: LineSegment StartX=-10.15 StartY=-12 StartZ=0 EndX=-7.79258 EndY=-12 EndZ=0
    g15: Circle CenterX=-6.2215 CenterY=-2 CenterZ=0 NormalX=0 NormalY=0 NormalZ=1 AngleXU=0 Radius=1
    g16: Circle CenterX=-6.22762 CenterY=-2.58724 CenterZ=0 NormalX=0 NormalY=0 NormalZ=1 AngleXU=0 Radius=1
    g17: Circle CenterX=-6.32538 CenterY=-4 CenterZ=0 NormalX=0 NormalY=0 NormalZ=1 AngleXU=0 Radius=1
    g18: BSplineCurve PolesCount=3 KnotsCount=2 Degree=2 IsPeriodic=0
    g19: GeomPoint X=-6.2215 Y=-2 Z=0
    g20: GeomPoint X=-6.32538 Y=-4 Z=0
    g21: Circle CenterX=-6.48644 CenterY=-5.99526 CenterZ=0 NormalX=0 NormalY=0 NormalZ=1 AngleXU=0 Radius=1
    g22: Circle CenterX=-6.58486 CenterY=-6.99526 CenterZ=0 NormalX=0 NormalY=0 NormalZ=1 AngleXU=0 Radius=1
    g23: Circle CenterX=-6.77343 CenterY=-8 CenterZ=0 NormalX=0 NormalY=0 NormalZ=1 AngleXU=0 Radius=1
    g24: BSplineCurve PolesCount=3 KnotsCount=2 Degree=2 IsPeriodic=0
    g25: GeomPoint X=-6.48644 Y=-5.99526 Z=0
    g26: GeomPoint X=-6.77343 Y=-8 Z=0
    g27: Circle CenterX=-7.19003 CenterY=-10 CenterZ=0 NormalX=0 NormalY=0 NormalZ=1 AngleXU=0 Radius=1
    g28: Circle CenterX=-7.44407 CenterY=-11.0915 CenterZ=0 NormalX=0 NormalY=0 NormalZ=1 AngleXU=0 Radius=1
    g29: Circle CenterX=-7.79258 CenterY=-12 CenterZ=0 NormalX=0 NormalY=0 NormalZ=1 AngleXU=0 Radius=1
    g30: BSplineCurve PolesCount=3 KnotsCount=2 Degree=2 IsPeriodic=0
    g31: GeomPoint X=-7.19003 Y=-10 Z=0
    g32: GeomPoint X=-7.79258 Y=-12 Z=0
    g33: Circle CenterX=-8.70761 CenterY=-14 CenterZ=0 NormalX=0 NormalY=0 NormalZ=1 AngleXU=0 Radius=1
    g34: Circle CenterX=-9.33087 CenterY=-15.1837 CenterZ=0 NormalX=0 NormalY=0 NormalZ=1 AngleXU=0 Radius=1
    g35: Circle CenterX=-10.1571 CenterY=-16 CenterZ=0 NormalX=0 NormalY=0 NormalZ=1 AngleXU=0 Radius=1
    g36: BSplineCurve PolesCount=3 KnotsCount=2 Degree=2 IsPeriodic=0
    g37: GeomPoint X=-8.70761 Y=-14 Z=0
    g38: GeomPoint X=-10.1571 Y=-16 Z=0
    g39: Circle CenterX=-12.8401 CenterY=-17.6958 CenterZ=0 NormalX=0 NormalY=0 NormalZ=1 AngleXU=0 Radius=1
    g40: Circle CenterX=-13.3521 CenterY=-17.9027 CenterZ=0 NormalX=0 NormalY=0 NormalZ=1 AngleXU=0 Radius=1
    g41: Circle CenterX=-14 CenterY=-18 CenterZ=0 NormalX=0 NormalY=0 NormalZ=1 AngleXU=0 Radius=1
    g42: BSplineCurve PolesCount=3 KnotsCount=2 Degree=2 IsPeriodic=0
    g43: GeomPoint X=-12.8401 Y=-17.6958 Z=0
    g44: GeomPoint X=-14 Y=-18 Z=0
    g45: LineSegment StartX=-6.2 StartY=0 StartZ=0 EndX=-7.2 EndY=0 EndZ=0
    g46: LineSegment StartX=-7.2 StartY=0 StartZ=0 EndX=-7.2 EndY=-2 EndZ=0
    g47: LineSegment StartX=-7.2 StartY=-2 StartZ=0 EndX=-6.2215 EndY=-2 EndZ=0
    g48: LineSegment StartX=-6.32538 StartY=-4 StartZ=0 EndX=-7.65538 EndY=-4 EndZ=0
    g49: LineSegment StartX=-7.65538 StartY=-4 StartZ=0 EndX=-7.65538 EndY=-5.99526 EndZ=0
    g50: LineSegment StartX=-7.65538 StartY=-5.99526 StartZ=0 EndX=-6.48644 EndY=-5.99526 EndZ=0
    g51: LineSegment StartX=-6.77343 StartY=-8 StartZ=0 EndX=-8.43343 EndY=-8 EndZ=0
    g52: LineSegment StartX=-8.43343 StartY=-8 StartZ=0 EndX=-8.43343 EndY=-10 EndZ=0
    g53: LineSegment StartX=-8.43343 StartY=-10 StartZ=0 EndX=-7.19003 EndY=-10 EndZ=0
  constraints (112):
    c: Horizontal(g0)
    c: Distance(g0) = 2
    c: Block(g0)
    c: Vertical(g1)
    c: Coincident(g2,g0)
    c: Vertical(g2)
    c: Block(g2)
    c: Coincident(g6,g2)
    c: Weight(g3) = 1
    c: Equal(g3,g4)
    c: Equal(g3,g5)
    c: InternalAlignment(g3,g6)
    c: InternalAlignment(g4,g6)
    c: InternalAlignment(g5,g6)
    c: InternalAlignment(g7,g6)
    c: InternalAlignment(g8,g6)
    c: Block(g6)
    c: Coincident(g9,g1)
    c: Coincident(g9,g6)
    c: Horizontal(g9)
    c: Vertical(g10)
    c: Block(g10)
    c: Horizontal(g11)
    c: Block(g11)
    c: Coincident(g12,g10)
    c: Horizontal(g12)
    c: Block(g12)
    c: Coincident(g13,g11)
    c: Vertical(g13)
    c: Block(g13)
    c: Coincident(g14,g10)
    c: Horizontal(g14)
    c: Block(g14)
    c: Block(g9)
    c: Block(g1)
    c: Weight(g15) = 1
    c: Equal(g15,g16)
    c: Equal(g15,g17)
    c: InternalAlignment(g15,g18)
    c: InternalAlignment(g16,g18)
    c: InternalAlignment(g17,g18)
    c: InternalAlignment(g19,g18)
    c: InternalAlignment(g20,g18)
    c: Weight(g21) = 1
    c: Equal(g21,g22)
    c: Equal(g21,g23)
    c: InternalAlignment(g21,g24)
    c: InternalAlignment(g22,g24)
    c: InternalAlignment(g23,g24)
    c: InternalAlignment(g25,g24)
    c: InternalAlignment(g26,g24)
    c: Weight(g27) = 1
    c: Equal(g27,g28)
    c: Equal(g27,g29)
    c: Coincident(g30,g14)
    c: InternalAlignment(g27,g30)
    c: InternalAlignment(g28,g30)
    c: InternalAlignment(g29,g30)
    c: InternalAlignment(g31,g30)
    c: InternalAlignment(g32,g30)
    c: Coincident(g36,g12)
    c: Weight(g33) = 1
    c: Equal(g33,g34)
    c: Equal(g33,g35)
    c: Coincident(g36,g11)
    c: InternalAlignment(g33,g36)
    c: InternalAlignment(g34,g36)
    c: InternalAlignment(g35,g36)
    c: InternalAlignment(g37,g36)
    c: InternalAlignment(g38,g36)
    c: Coincident(g42,g13)
    c: Weight(g39) = 1
    c: Equal(g39,g40)
    c: Equal(g39,g41)
    c: Coincident(g42,g1)
    c: InternalAlignment(g39,g42)
    c: InternalAlignment(g40,g42)
    c: InternalAlignment(g41,g42)
    c: InternalAlignment(g43,g42)
    c: InternalAlignment(g44,g42)
    c: Block(g18)
    c: Block(g24)
    c: Block(g30)
    c: Block(g36)
    c: Block(g42)
    c: Horizontal(g45)
    c: Coincident(g45,g0)
    c: Vertical(g46)
    c: Coincident(g46,g45)
    c: Coincident(g47,g46)
    c: Coincident(g47,g18)
    c: Horizontal(g47)
    c: Block(g46)
    c: Coincident(g48,g18)
    c: Horizontal(g48)
    c: Distance(g48) = 1.33
    c: Vertical(g49)
    c: Coincident(g49,g48)
    c: Coincident(g50,g49)
    c: Coincident(g50,g24)
    c: Horizontal(g50)
    c: Tangent(g50,g22)
    c: Horizontal(g51)
    c: Coincident(g51,g24)
    c: Block(g51)
    c: Vertical(g52)
    c: Block(g52)
    c: Coincident(g52,g51)
    c: Coincident(g53,g52)
    c: Coincident(g53,g30)
    c: Horizontal(g53)
    c: Distance(g1) = 8.5
FEATURE [Part::Feature] Face024
  shape: bbox 9.8 x 26.5 x 2e-07 mm, 1 faces, 0 solids (baked)
FEATURE [Part::Revolution] Revolve024
  Angle = 360
  Axis = (0,1,0)
  Base = (0,0,0)
  FaceMakerClass = Part::FaceMakerBullseye
  Placement = pos=(0,0,0) rot=(0,0,1;1.5708rad)
  Solid = false
  Source = -> Face024
  Symmetric = false
FEATURE [Part::Feature] Face025
  shape: bbox 9.8 x 26.5 x 2e-07 mm, 1 faces, 0 solids (baked)
FEATURE [Part::Revolution] Revolve025
  Angle = 360
  Axis = (0,1,0)
  Base = (0,0,0)
  FaceMakerClass = Part::FaceMakerBullseye
  Placement = pos=(0,0,0) rot=(0,0,1;1.5708rad)
  Solid = false
  Source = -> Face025
  Symmetric = false
FEATURE [Part::MultiFuse] Fusion033
  Placement = pos=(-18,19,36) rot=(0,0,1;0rad)
  Shapes = -> [Revolve025,Revolve024]
FEATURE [Part::Cylinder] Cylinder014
  Angle = 360
  AttacherType = Attacher::AttachEngine3D
  Height = 20
  Placement = pos=(0,0,36.15) rot=(0,0,1;0rad)
  Radius = 14.3
FEATURE [Part::Cylinder] Cylinder015
  Angle = 360
  AttacherType = Attacher::AttachEngine3D
  Height = 10
  Placement = pos=(0,0,36.15) rot=(0,0,1;0rad)
  Radius = 4
FEATURE [Part::MultiFuse] Fusion034  label="removeToCreteHoleForPlugHousing004"
  Placement = pos=(-42,19,36) rot=(0,1,0;1.5708rad)
  Shapes = -> [Cylinder014,Cylinder015]
FEATURE [Part::Cut] Cut008  label="top004"
  Base = -> Cut004
  Placement = pos=(-1,0,0) rot=(0,0,1;0rad)
  Tool = -> Fusion034
FEATURE [Part::Box] Box005  label="Cube005"
  AttacherType = Attacher::AttachEngine3D
  Height = 28
  Length = 3
  Placement = pos=(110.7,19,22) rot=(0,0,1;0rad)
  Width = 15.7
FEATURE [Part::Cylinder] Cylinder016
  Angle = 360
  AttacherType = Attacher::AttachEngine3D
  Height = 10
  Placement = pos=(0,0,36.15) rot=(0,0,1;0rad)
  Radius = 4
FEATURE [Part::Cylinder] Cylinder017
  Angle = 360
  AttacherType = Attacher::AttachEngine3D
  Height = 20
  Placement = pos=(0,0,36.15) rot=(0,0,1;0rad)
  Radius = 10.3
FEATURE [Part::MultiFuse] Fusion035  label="removeToCreteHoleForPlugHousing005"
  Placement = pos=(70,19,36) rot=(0,1,0;1.5708rad)
  Shapes = -> [Cylinder017,Cylinder016]
FEATURE [Part::Cut] Cut009  label="plugHousingTab001"
  Base = -> Box005
  Placement = pos=(-107.4,-14,0) rot=(0,0,1;0rad)
  Tool = -> Fusion035
FEATURE [Part::Box] Box006  label="Cube006"
  AttacherType = Attacher::AttachEngine3D
  Height = 28
  Length = 3
  Placement = pos=(110.7,19,22) rot=(0,0,1;0rad)
  Width = 15.7
FEATURE [Part::Cylinder] Cylinder018
  Angle = 360
  AttacherType = Attacher::AttachEngine3D
  Height = 10
  Placement = pos=(0,0,36.15) rot=(0,0,1;0rad)
  Radius = 4
FEATURE [Part::Cylinder] Cylinder019
  Angle = 360
  AttacherType = Attacher::AttachEngine3D
  Height = 20
  Placement = pos=(0,0,36.15) rot=(0,0,1;0rad)
  Radius = 10.3
FEATURE [Part::MultiFuse] Fusion036  label="removeToCreteHoleForPlugHousing006"
  Placement = pos=(70,19,36) rot=(0,1,0;1.5708rad)
  Shapes = -> [Cylinder019,Cylinder018]
FEATURE [Part::Cut] Cut010  label="plugHousingTab002"
  Base = -> Box006
  Placement = pos=(-107.4,-14,0) rot=(0,0,1;0rad)
  Tool = -> Fusion036
FEATURE [Part::MultiFuse] Fusion037
  Placement = pos=(9.6,23,0) rot=(0,0,1;3.14159rad)
  Shapes = -> [Cut009,Cut010]
FEATURE [Part::Box] Box  label="Cube"
  AttacherType = Attacher::AttachEngine3D
  Height = 10
  Length = 3
  Placement = pos=(3.3,4,12) rot=(0,0,1;0rad)
  Width = 10
FEATURE [Part::Fillet] Fillet004
  Base = -> Fusion028
  Edges = 1 edges r=2: [Edge25]
FEATURE [Part::Fillet] Fillet005  label="plugHousing046"
  Base = -> Fillet004
  Edges = 1 edges r=2: [Edge8]
FEATURE [Part::Fillet] Fillet006
  Base = -> Box
  Edges = 1 edges r=2: [Edge11]
FEATURE [Part::Box] Box007  label="Cube007"
  AttacherType = Attacher::AttachEngine3D
  Height = 10
  Length = 3
  Placement = pos=(3.3,4,50) rot=(0,0,1;0rad)
  Width = 10
FEATURE [Part::Fillet] Fillet007
  Base = -> Box007
  Edges = 1 edges r=2: [Edge12]
FEATURE [Part::Box] Box008  label="Cube008"
  AttacherType = Attacher::AttachEngine3D
  Height = 28
  Length = 4
  Placement = pos=(5,0,22) rot=(0,0,1;0rad)
  Width = 10
FEATURE [Part::Fillet] Fillet008
  Base = -> Box008
  Edges = 1 edges r=1: [Edge7]
FEATURE [Part::Fillet] Fillet009
  Base = -> Fillet008
  Edges = 1 edges r=2: [Edge5]
FEATURE [Part::Fillet] Fillet010
  Base = -> Fillet009
  Edges = 1 edges r=2: [Edge2]
FEATURE [Sketcher::SketchObject] Sketch009  label="topSketch003"
  FullyConstrained = true
  sketch-geometry (4):
    g0: LineSegment StartX=16.8446 StartY=31.512 StartZ=0 EndX=16.3251 EndY=34.4666 EndZ=0
    g1: ArcOfCircle CenterX=19 CenterY=19.2524 CenterZ=0 NormalX=0 NormalY=0 NormalZ=1 AngleXU=0 Radius=15.4476 StartAngle=1.74483 EndAngle=2.72717
    g2: ArcOfCircle CenterX=19 CenterY=19.2524 CenterZ=0 NormalX=0 NormalY=0 NormalZ=1 AngleXU=0 Radius=12.4476 StartAngle=1.74483 EndAngle=2.73189
    g3: LineSegment StartX=4.86004 StartY=25.4725 StartZ=0 EndX=7.58253 EndY=24.2107 EndZ=0
  constraints (7):
    c: Block(g0)
    c: Coincident(g1,g0)
    c: Coincident(g2,g0)
    c: Coincident(g3,g1)
    c: Coincident(g3,g2)
    c: Block(g1)
    c: Block(g2)
FEATURE [Part::Extrusion] Extrude008
  Base = -> Sketch009
  Dir = (0,0,1)
  DirMode = 2
  FaceMakerClass = Part::FaceMakerBullseye
  LengthFwd = 10
  LengthRev = 0
  Placement = pos=(0,0,31) rot=(0,0,1;0rad)
  Solid = true
  Symmetric = false
FEATURE [Part::Cylinder] Cylinder020
  Angle = 360
  AttacherType = Attacher::AttachEngine3D
  Height = 20
  Placement = pos=(0,0,36.15) rot=(0,0,1;0rad)
  Radius = 8.2
FEATURE [Part::Cylinder] Cylinder021
  Angle = 360
  AttacherType = Attacher::AttachEngine3D
  Height = 10
  Placement = pos=(0,0,36.15) rot=(0,0,1;0rad)
  Radius = 4
FEATURE [Part::MultiFuse] Fusion038  label="removeToCreteHoleForPlugHousing007"
  Placement = pos=(-42,19,36) rot=(0,1,0;1.5708rad)
  Shapes = -> [Cylinder020,Cylinder021]
FEATURE [Part::Cut] Cut011
  Base = -> Extrude008
  Tool = -> Fusion038
FEATURE [Part::Fillet] Fillet011
  Base = -> Cut011
  Edges = 1 edges r=2: [Edge1]
FEATURE [Part::Fillet] Fillet012
  Base = -> Fillet011
  Edges = 1 edges r=2.5: [Edge1]
FEATURE [Part::Fillet] Fillet013
  Base = -> Fillet012
  Edges = 1 edges r=2.5: [Edge2]
FEATURE [Part::Box] Box010  label="Cube010"
  AttacherType = Attacher::AttachEngine3D
  Height = 16
  Length = 8
  Placement = pos=(12.7,31.52,28) rot=(0,0,1;0rad)
  Width = 4
FEATURE [Sketcher::SketchObject] Sketch010  label="topSketch004"
  FullyConstrained = true
  sketch-geometry (4):
    g0: LineSegment StartX=16.8446 StartY=31.512 StartZ=0 EndX=16.3251 EndY=34.4666 EndZ=0
    g1: ArcOfCircle CenterX=19 CenterY=19.2524 CenterZ=0 NormalX=0 NormalY=0 NormalZ=1 AngleXU=0 Radius=15.4476 StartAngle=1.74483 EndAngle=2.72717
    g2: ArcOfCircle CenterX=19 CenterY=19.2524 CenterZ=0 NormalX=0 NormalY=0 NormalZ=1 AngleXU=0 Radius=12.4476 StartAngle=1.74483 EndAngle=2.73189
    g3: LineSegment StartX=4.86004 StartY=25.4725 StartZ=0 EndX=7.58253 EndY=24.2107 EndZ=0
  constraints (7):
    c: Block(g0)
    c: Coincident(g1,g0)
    c: Coincident(g2,g0)
    c: Coincident(g3,g1)
    c: Coincident(g3,g2)
    c: Block(g1)
    c: Block(g2)
FEATURE [Part::Cylinder] Cylinder022
  Angle = 360
  AttacherType = Attacher::AttachEngine3D
  Height = 10
  Placement = pos=(0,0,36.15) rot=(0,0,1;0rad)
  Radius = 4
FEATURE [Sketcher::SketchObject] Sketch011  label="topSketch005"
  FullyConstrained = true
  sketch-geometry (4):
    g0: LineSegment StartX=16.8446 StartY=31.512 StartZ=0 EndX=16.3251 EndY=34.4666 EndZ=0
    g1: ArcOfCircle CenterX=19 CenterY=19.2524 CenterZ=0 NormalX=0 NormalY=0 NormalZ=1 AngleXU=0 Radius=15.4476 StartAngle=1.74483 EndAngle=2.72717
    g2: ArcOfCircle CenterX=19 CenterY=19.2524 CenterZ=0 NormalX=0 NormalY=0 NormalZ=1 AngleXU=0 Radius=12.4476 StartAngle=1.74483 EndAngle=2.73189
    g3: LineSegment StartX=4.86004 StartY=25.4725 StartZ=0 EndX=7.58253 EndY=24.2107 EndZ=0
  constraints (7):
    c: Block(g0)
    c: Coincident(g1,g0)
    c: Coincident(g2,g0)
    c: Coincident(g3,g1)
    c: Coincident(g3,g2)
    c: Block(g1)
    c: Block(g2)
FEATURE [Part::Extrusion] Extrude010
  Base = -> Sketch011
  Dir = (0,0,1)
  DirMode = 2
  FaceMakerClass = Part::FaceMakerBullseye
  LengthFwd = 10.6
  LengthRev = 0
  Placement = pos=(0,0,31) rot=(0,0,1;0rad)
  Solid = true
  Symmetric = false
FEATURE [Part::Cylinder] Cylinder023
  Angle = 360
  AttacherType = Attacher::AttachEngine3D
  Height = 20
  Placement = pos=(0,0,36.15) rot=(0,0,1;0rad)
  Radius = 8.2
FEATURE [Part::MultiFuse] Fusion039  label="removeToCreteHoleForPlugHousing008"
  Placement = pos=(-42,19,36) rot=(0,1,0;1.5708rad)
  Shapes = -> [Cylinder023,Cylinder022]
FEATURE [Part::Cut] Cut012
  Base = -> Extrude010
  Placement = pos=(0,0,-0.3) rot=(0,0,1;0rad)
  Tool = -> Fusion039
FEATURE [Part::Cut] Cut013
  Base = -> Box010
  Tool = -> Cut012
FEATURE [Part::Fillet] Fillet014
  Base = -> Cut013
  Edges = 1 edges r=0.7: [Edge13]
FEATURE [Part::Fillet] Fillet015
  Base = -> Fillet014
  Edges = 1 edges r=0.7: [Edge13]
FEATURE [Part::Fillet] Fillet016
  Base = -> Fillet015
  Edges = 1 edges r=0.7: [Edge16]
FEATURE [Part::Fillet] Fillet017
  Base = -> Fillet016
  Edges = 1 edges r=0.7: [Edge11]
FEATURE [Part::Fillet] Fillet018
  Base = -> Fillet017
  Edges = 1 edges r=0.7: [Edge10]
FEATURE [Part::Fillet] Fillet019
  Base = -> Fillet018
  Edges = 1 edges r=1.2: [Edge5]
FEATURE [Part::Fillet] Fillet020
  Base = -> Fillet019
  Edges = 1 edges r=1.2: [Edge12]
FEATURE [Part::Fillet] Fillet021
  Base = -> Fillet020
  Edges = 1 edges r=2: [Edge1]
  Placement = pos=(0.3,0,0) rot=(0,0,1;0rad)
FEATURE [Part::MultiFuse] Fusion040  label="top005"
  Shapes = -> [Cut008,Fillet021]
FEATURE [Part::MultiFuse] Fusion041  label="wireHolder"
  Shapes = -> [Fusion033,Fillet013]
FEATURE [Part::MultiFuse] Fusion042
  Shapes = -> [Fillet007,Fusion041]
FEATURE [Part::MultiFuse] Fusion043  label="wireHolder001"
  Shapes = -> [Fusion042,Fillet010]
FEATURE [Part::MultiFuse] Fusion044  label="wireHolder002"
  Shapes = -> [Fillet006,Fusion037,Fusion043]
FEATURE [Part::Feature] Face026
  shape: bbox 11 x 6 x 2e-07 mm, 1 faces, 0 solids (baked)
FEATURE [Part::Revolution] Revolve026
  Angle = 360
  Axis = (0,1,0)
  Base = (0,0,0)
  FaceMakerClass = Part::FaceMakerBullseye
  Placement = pos=(30.3,-1,19.7) rot=(0,0,1;0rad)
  Solid = false
  Source = -> Face026
  Symmetric = false
FEATURE [Sketcher::SketchObject] Sketch013  label="topSketch006"
  FullyConstrained = true
  sketch-geometry (13):
    g0: LineSegment StartX=117 StartY=19 StartZ=0 EndX=117 EndY=38 EndZ=0
    g1: ArcOfCircle CenterX=98 CenterY=19 CenterZ=0 NormalX=0 NormalY=0 NormalZ=1 AngleXU=0 Radius=19 StartAngle=5.7297 EndAngle=6.28319
    g2: LineSegment StartX=0 StartY=3 StartZ=0 EndX=0 EndY=19 EndZ=0
    g3: LineSegment StartX=19 StartY=38 StartZ=0 EndX=117 EndY=38 EndZ=0
    g4: ArcOfCircle CenterX=19 CenterY=19 CenterZ=0 NormalX=0 NormalY=0 NormalZ=1 AngleXU=0 Radius=19 StartAngle=1.5708 EndAngle=3.14159
    g5: ArcOfCircle CenterX=19 CenterY=19 CenterZ=0 NormalX=0 NormalY=0 NormalZ=1 AngleXU=0 Radius=16 StartAngle=1.5708 EndAngle=3.14159
    g6: ArcOfCircle CenterX=98 CenterY=19 CenterZ=0 NormalX=0 NormalY=0 NormalZ=1 AngleXU=0 Radius=16 StartAngle=5.60905 EndAngle=6.28319
    g7: LineSegment StartX=114 StartY=19 StartZ=0 EndX=114 EndY=35 EndZ=0
    g8: LineSegment StartX=110.5 StartY=9.01251 StartZ=0 EndX=114.163 EndY=9.01251 EndZ=0
    g9: LineSegment StartX=114 StartY=35 StartZ=0 EndX=19 EndY=35 EndZ=0
    g10: LineSegment StartX=0 StartY=3 StartZ=0 EndX=0 EndY=0 EndZ=0
    g11: LineSegment StartX=3 StartY=0 StartZ=0 EndX=0 EndY=0 EndZ=0
    g12: LineSegment StartX=3 StartY=19 StartZ=0 EndX=3 EndY=0 EndZ=0
  constraints (33):
    c: Vertical(g0)
    c: Distance(g0) = 19
    c: Block(g0)
    c: Coincident(g1,g0)
    c: Block(g1)
    c: Vertical(g2)
    c: Block(g2)
    c: Coincident(g3,g0)
    c: Horizontal(g3)
    c: Distance(g3) = 98
    c: Coincident(g4,g3)
    c: Coincident(g4,g2)
    c: Block(g4)
    c: Coincident(g5,g4)
    c: Coincident(g6,g1)
    c: Block(g6)
    c: Block(g5)
    c: Coincident(g7,g6)
    c: Vertical(g7)
    c: Coincident(g8,g6)
    c: Coincident(g8,g1)
    c: Coincident(g9,g7)
    c: Coincident(g9,g5)
    c: Horizontal(g9)
    c: Tangent(g9,g5)
    c: Coincident(g10,g2)
    c: Distance(g10) = 3
    c: Vertical(g10)
    c: Coincident(g11,g10)
    c: Horizontal(g11)
    c: Coincident(g12,g5)
    c: Coincident(g12,g11)
    c: Vertical(g12)
FEATURE [Part::Extrusion] Extrude011  label="top006"
  Base = -> Sketch013
  Dir = (0,0,1)
  DirMode = 2
  FaceMakerClass = Part::FaceMakerBullseye
  LengthFwd = 72
  LengthRev = 0
  Solid = true
  Symmetric = false
FEATURE [Sketcher::SketchObject] Sketch014
  FullyConstrained = true
  MapMode = 3
  Placement = pos=(0,0,0) rot=(1,0,0;1.5708rad)
  Support = -> [Extrude011]
  sketch-geometry (8):
    g0: Circle CenterX=80.351 CenterY=-67.6202 CenterZ=0 NormalX=0 NormalY=0 NormalZ=1 AngleXU=0 Radius=2
    g1: Circle CenterX=80.351 CenterY=-67.6202 CenterZ=0 NormalX=0 NormalY=0 NormalZ=1 AngleXU=0 Radius=3
    g2: Circle CenterX=80.351 CenterY=-4.92017 CenterZ=0 NormalX=0 NormalY=0 NormalZ=1 AngleXU=0 Radius=2
    g3: Circle CenterX=80.351 CenterY=-4.92017 CenterZ=0 NormalX=0 NormalY=0 NormalZ=1 AngleXU=0 Radius=3
    g4: Circle CenterX=23.851 CenterY=-4.92017 CenterZ=0 NormalX=0 NormalY=0 NormalZ=1 AngleXU=0 Radius=2
    g5: Circle CenterX=23.851 CenterY=-4.92017 CenterZ=0 NormalX=0 NormalY=0 NormalZ=1 AngleXU=0 Radius=3
    g6: Circle CenterX=23.851 CenterY=-67.6202 CenterZ=0 NormalX=0 NormalY=0 NormalZ=1 AngleXU=0 Radius=2
    g7: Circle CenterX=23.851 CenterY=-67.6202 CenterZ=0 NormalX=0 NormalY=0 NormalZ=1 AngleXU=0 Radius=3
  constraints (8):
    c: Block(g3)
    c: Block(g2)
    c: Block(g1)
    c: Block(g0)
    c: Block(g6)
    c: Block(g7)
    c: Block(g4)
    c: Block(g5)
FEATURE [Part::Feature] Face027
  shape: bbox 11 x 6 x 2e-07 mm, 1 faces, 0 solids (baked)
FEATURE [Part::Revolution] Revolve027
  Angle = 360
  Axis = (0,1,0)
  Base = (0,0,0)
  FaceMakerClass = Part::FaceMakerBullseye
  Placement = pos=(30.3,-1,51.7) rot=(0,0,1;0rad)
  Solid = false
  Source = -> Face027
  Symmetric = false
FEATURE [Part::Feature] Face028
  shape: bbox 11 x 6 x 2e-07 mm, 1 faces, 0 solids (baked)
FEATURE [Part::Revolution] Revolve028
  Angle = 360
  Axis = (0,1,0)
  Base = (0,0,0)
  FaceMakerClass = Part::FaceMakerBullseye
  Placement = pos=(62.3,-1,19.7) rot=(0,0,1;0rad)
  Solid = false
  Source = -> Face028
  Symmetric = false
FEATURE [Part::Feature] Face029
  shape: bbox 11 x 6 x 2e-07 mm, 1 faces, 0 solids (baked)
FEATURE [Part::Revolution] Revolve029
  Angle = 360
  Axis = (0,1,0)
  Base = (0,0,0)
  FaceMakerClass = Part::FaceMakerBullseye
  Placement = pos=(62.3,-1,51.7) rot=(0,0,1;0rad)
  Solid = false
  Source = -> Face029
  Symmetric = false
FEATURE [Part::Feature] Wire
  shape: bbox 11 x 5.2 x 2e-07 mm, 0 faces, 0 solids (baked)
FEATURE [Part::Revolution] Revolve030
  Angle = 360
  Axis = (0,1,0)
  Base = (0,0,0)
  FaceMakerClass = Part::FaceMakerBullseye
  Placement = pos=(30.3,38,19.7) rot=(0,0,1;0rad)
  Solid = true
  Source = -> Wire
  Symmetric = false
FEATURE [Part::Feature] Wire001
  shape: bbox 11 x 5.2 x 2e-07 mm, 0 faces, 0 solids (baked)
FEATURE [Part::Revolution] Revolve031
  Angle = 360
  Axis = (0,1,0)
  Base = (0,0,0)
  FaceMakerClass = Part::FaceMakerBullseye
  Placement = pos=(30.3,38,51.7) rot=(0,0,1;0rad)
  Solid = true
  Source = -> Wire001
  Symmetric = false
FEATURE [Part::Feature] Wire002
  shape: bbox 11 x 5.2 x 2e-07 mm, 0 faces, 0 solids (baked)
FEATURE [Part::Revolution] Revolve032
  Angle = 360
  Axis = (0,1,0)
  Base = (0,0,0)
  FaceMakerClass = Part::FaceMakerBullseye
  Placement = pos=(62.3,38,51.7) rot=(0,0,1;0rad)
  Solid = true
  Source = -> Wire002
  Symmetric = false
FEATURE [Part::Feature] Wire003
  shape: bbox 11 x 5.2 x 2e-07 mm, 0 faces, 0 solids (baked)
FEATURE [Part::Revolution] Revolve033
  Angle = 360
  Axis = (0,1,0)
  Base = (0,0,0)
  FaceMakerClass = Part::FaceMakerBullseye
  Placement = pos=(62.3,38,19.7) rot=(0,0,1;0rad)
  Solid = true
  Source = -> Wire003
  Symmetric = false
FEATURE [Part::MultiFuse] Fusion045  label="altRandScrewHousing"
  Shapes = -> [Revolve029,Revolve027,Revolve028,Revolve026]
FEATURE [Part::MultiFuse] Fusion046  label="fanScrewHousing"
  Shapes = -> [Revolve033,Revolve032,Revolve031,Revolve030]
FEATURE [Sketcher::SketchObject] Sketch015
  FullyConstrained = true
  sketch-geometry (17):
    g0: Circle CenterX=-3.5 CenterY=23.5 CenterZ=0 NormalX=0 NormalY=0 NormalZ=1 AngleXU=0 Radius=1
    g1: Circle CenterX=-1 CenterY=15.25 CenterZ=0 NormalX=0 NormalY=0 NormalZ=1 AngleXU=0 Radius=1
    g2: Circle CenterX=-3.5 CenterY=7 CenterZ=0 NormalX=0 NormalY=0 NormalZ=1 AngleXU=0 Radius=1
    g3: BSplineCurve PolesCount=3 KnotsCount=2 Degree=2 IsPeriodic=0
    g4: GeomPoint X=-3.5 Y=23.5 Z=0
    g5: GeomPoint X=-3.5 Y=7 Z=0
    g6: Circle CenterX=-4.8 CenterY=30.5 CenterZ=0 NormalX=0 NormalY=0 NormalZ=1 AngleXU=0 Radius=1
    g7: Circle CenterX=-3.5 CenterY=30.5 CenterZ=0 NormalX=0 NormalY=0 NormalZ=1 AngleXU=0 Radius=1
    g8: Circle CenterX=-3.5 CenterY=29.2 CenterZ=0 NormalX=0 NormalY=0 NormalZ=1 AngleXU=0 Radius=1
    g9: BSplineCurve PolesCount=3 KnotsCount=2 Degree=2 IsPeriodic=0
    g10: GeomPoint X=-4.8 Y=30.5 Z=0
    g11: GeomPoint X=-3.5 Y=29.2 Z=0
    g12: LineSegment StartX=-3.5 StartY=29.2 StartZ=0 EndX=-3.5 EndY=23.5 EndZ=0
    g13: LineSegment StartX=-4.8 StartY=30.5 StartZ=0 EndX=0 EndY=30.5 EndZ=0
    g14: LineSegment StartX=-3.5 StartY=0.3 StartZ=0 EndX=0 EndY=0.3 EndZ=0
    g15: LineSegment StartX=-3.5 StartY=0.3 StartZ=0 EndX=-3.5 EndY=7 EndZ=0
    g16: LineSegment StartX=0 StartY=0.3 StartZ=0 EndX=0 EndY=30.5 EndZ=0
  constraints (33):
    c: Weight(g0) = 1
    c: Equal(g0,g1)
    c: Equal(g0,g2)
    c: InternalAlignment(g0,g3)
    c: InternalAlignment(g1,g3)
    c: InternalAlignment(g2,g3)
    c: InternalAlignment(g4,g3)
    c: InternalAlignment(g5,g3)
    c: Block(g3)
    c: Weight(g6) = 1
    c: Equal(g6,g7)
    c: Equal(g6,g8)
    c: InternalAlignment(g6,g9)
    c: InternalAlignment(g7,g9)
    c: InternalAlignment(g8,g9)
    c: InternalAlignment(g10,g9)
    c: InternalAlignment(g11,g9)
    c: Block(g9)
    c: Coincident(g12,g9)
    c: Coincident(g12,g3)
    c: Vertical(g12)
    c: Coincident(g13,g9)
    c: Horizontal(g13)
    c: Distance(g13) = 4.8
    c: Horizontal(g14)
    c: Block(g14)
    c: Coincident(g15,g14)
    c: Coincident(g15,g3)
    c: Vertical(g15)
    c: Coincident(g16,g14)
    c: Coincident(g16,g13)
    c: Vertical(g16)
    c: Tangent(g16,g1)
FEATURE [Sketcher::SketchObject] Sketch016
  FullyConstrained = true
  sketch-geometry (16):
    g0: Circle CenterX=-3.5 CenterY=23.5 CenterZ=0 NormalX=0 NormalY=0 NormalZ=1 AngleXU=0 Radius=1
    g1: Circle CenterX=-1 CenterY=15.25 CenterZ=0 NormalX=0 NormalY=0 NormalZ=1 AngleXU=0 Radius=1
    g2: Circle CenterX=-3.5 CenterY=7 CenterZ=0 NormalX=0 NormalY=0 NormalZ=1 AngleXU=0 Radius=1
    g3: BSplineCurve PolesCount=3 KnotsCount=2 Degree=2 IsPeriodic=0
    g4: GeomPoint X=-3.5 Y=23.5 Z=0
    g5: GeomPoint X=-3.5 Y=7 Z=0
    g6: LineSegment StartX=-3.5 StartY=28.2 StartZ=0 EndX=-3.5 EndY=23.5 EndZ=0
    g7: LineSegment StartX=0 StartY=29.5 StartZ=0 EndX=0 EndY=30 EndZ=0
    g8: LineSegment StartX=-3.5 StartY=28.2 StartZ=0 EndX=-3.5 EndY=30 EndZ=0
    g9: LineSegment StartX=0 StartY=30 StartZ=0 EndX=0 EndY=30.5 EndZ=0
    g10: LineSegment StartX=0 StartY=30.5 StartZ=0 EndX=-3.5 EndY=30.5 EndZ=0
    g11: LineSegment StartX=-3.5 StartY=30.5 StartZ=0 EndX=-3.5 EndY=30 EndZ=0
    g12: LineSegment StartX=0 StartY=29.5 StartZ=0 EndX=0 EndY=5 EndZ=0
    g13: LineSegment StartX=-3.5 StartY=0.3 StartZ=0 EndX=-3.5 EndY=7 EndZ=0
    g14: LineSegment StartX=-3.5 StartY=0.3 StartZ=0 EndX=0 EndY=0.3 EndZ=0
    g15: LineSegment StartX=0 StartY=5 StartZ=0 EndX=0 EndY=0.3 EndZ=0
  constraints (39):
    c: Weight(g0) = 1
    c: Equal(g0,g1)
    c: Equal(g0,g2)
    c: InternalAlignment(g0,g3)
    c: InternalAlignment(g1,g3)
    c: InternalAlignment(g2,g3)
    c: InternalAlignment(g4,g3)
    c: InternalAlignment(g5,g3)
    c: Block(g3)
    c: Coincident(g6,g3)
    c: Vertical(g6)
    c: Vertical(g7)
    c: Distance(g7) = 0.5
    c: Coincident(g8,g6)
    c: Vertical(g8)
    c: Block(g6)
    c: Block(g7)
    c: Vertical(g9)
    c: Equal(g7,g9) = 0.5
    c: Block(g9)
    c: Coincident(g9,g7)
    c: Horizontal(g10)
    c: Coincident(g10,g9)
    c: Coincident(g11,g10)
    c: Coincident(g11,g8)
    c: Vertical(g11)
    c: Block(g11)
    c: Coincident(g12,g7)
    c: Vertical(g12)
    c: Coincident(g13,g3)
    c: Vertical(g13)
    c: Distance(g13) = 6.7
    c: Coincident(g14,g13)
    c: Horizontal(g14)
    c: Block(g14)
    c: Coincident(g15,g12)
    c: Coincident(g15,g14)
    c: Vertical(g15)
    c: Block(g15)
FEATURE [Sketcher::SketchObject] Sketch017
  FullyConstrained = true
  sketch-geometry (11):
    g0: LineSegment StartX=-3.5 StartY=1e-16 StartZ=0 EndX=-1.6 EndY=1e-16 EndZ=0
    g1: LineSegment StartX=-1.6 StartY=1e-16 StartZ=0 EndX=-1.6 EndY=1.5 EndZ=0
    g2: LineSegment StartX=-3.5 StartY=1.5 StartZ=0 EndX=-1.6 EndY=1.5 EndZ=0
    g3: LineSegment StartX=-3.5 StartY=1e-16 StartZ=0 EndX=-4.8 EndY=1e-16 EndZ=0
    g4: Circle CenterX=-3.5 CenterY=1.3 CenterZ=0 NormalX=0 NormalY=0 NormalZ=1 AngleXU=0 Radius=1
    g5: Circle CenterX=-3.5 CenterY=1e-16 CenterZ=0 NormalX=0 NormalY=0 NormalZ=1 AngleXU=0 Radius=1
    g6: Circle CenterX=-4.8 CenterY=1e-16 CenterZ=0 NormalX=0 NormalY=0 NormalZ=1 AngleXU=0 Radius=1
    g7: BSplineCurve PolesCount=3 KnotsCount=2 Degree=2 IsPeriodic=0
    g8: GeomPoint X=-3.5 Y=1.3 Z=0
    g9: GeomPoint X=-4.8 Y=1e-16 Z=0
    g10: LineSegment StartX=-3.5 StartY=1.3 StartZ=0 EndX=-3.5 EndY=1.5 EndZ=0
  constraints (24):
    c: Horizontal(g0)
    c: Distance(g0) = 1.9
    c: Block(g0)
    c: Coincident(g1,g0)
    c: Vertical(g1)
    c: Coincident(g2,g1)
    c: Horizontal(g2)
    c: Coincident(g3,g0)
    c: Horizontal(g3)
    c: Distance(g3) = 1.3
    c: Weight(g4) = 1
    c: Equal(g4,g5)
    c: Coincident(g5,g0)
    c: Equal(g4,g6)
    c: Coincident(g7,g3)
    c: InternalAlignment(g4,g7)
    c: InternalAlignment(g5,g7)
    c: InternalAlignment(g6,g7)
    c: InternalAlignment(g8,g7)
    c: InternalAlignment(g9,g7)
    c: Coincident(g10,g7)
    c: Coincident(g10,g2)
    c: Vertical(g10)
    c: Block(g10)
FEATURE [Part::Feature] Face035
  shape: bbox 3.2 x 1.5 x 2e-07 mm, 1 faces, 0 solids (baked)
FEATURE [Part::Revolution] Revolve039  label="backCaseScrewRetainer"
  Angle = 360
  Axis = (0,1,0)
  Base = (0,0,0)
  FaceMakerClass = Part::FaceMakerBullseye
  Placement = pos=(12.5,3,62) rot=(0,0,1;0rad)
  Solid = false
  Source = -> Face035
  Symmetric = false
FEATURE [Part::Feature] Face036
  shape: bbox 3.2 x 1.5 x 2e-07 mm, 1 faces, 0 solids (baked)
FEATURE [Part::Feature] Face039
  shape: bbox 4.8 x 30.2 x 2e-07 mm, 1 faces, 0 solids (baked)
FEATURE [Part::Revolution] Revolve043  label="frontCaseScrewPost002"
  Angle = 360
  Axis = (0,1,0)
  Base = (0,0,0)
  FaceMakerClass = Part::FaceMakerBullseye
  Placement = pos=(89.5,4.5,3.5) rot=(0,0,1;0rad)
  Solid = false
  Source = -> Face039
  Symmetric = false
FEATURE [Part::Feature] Face042
  shape: bbox 4.8 x 30.2 x 2e-07 mm, 1 faces, 0 solids (baked)
FEATURE [Part::Revolution] Revolve046  label="frontCaseScrewPost003"
  Angle = 360
  Axis = (0,1,0)
  Base = (0,0,0)
  FaceMakerClass = Part::FaceMakerBullseye
  Placement = pos=(89.5,4.5,68.5) rot=(0,0,1;0rad)
  Solid = false
  Source = -> Face042
  Symmetric = false
FEATURE [Part::Feature] Face043
  shape: bbox 3.2 x 1.5 x 2e-07 mm, 1 faces, 0 solids (baked)
FEATURE [Part::Revolution] Revolve047  label="frontCaseScrewRetainer002"
  Angle = 360
  Axis = (0,1,0)
  Base = (0,0,0)
  FaceMakerClass = Part::FaceMakerBullseye
  Placement = pos=(89.5,3,68.5) rot=(0,0,1;0rad)
  Solid = false
  Source = -> Face043
  Symmetric = false
FEATURE [Part::Feature] Face044
  shape: bbox 3.2 x 1.5 x 2e-07 mm, 1 faces, 0 solids (baked)
FEATURE [Part::Revolution] Revolve048  label="frontCaseScrewRetainer003"
  Angle = 360
  Axis = (0,1,0)
  Base = (0,0,0)
  FaceMakerClass = Part::FaceMakerBullseye
  Placement = pos=(89.5,3,3.5) rot=(0,0,1;0rad)
  Solid = false
  Source = -> Face044
  Symmetric = false
FEATURE [App::MeasureDistance] Distance002  label="Distance: 1.67 mm"
  Distance = 1.66921
  P1 = (99.2361,4.7524,71.7)
  P2 = (99.2347,6.42161,71.7)
FEATURE [Sketcher::SketchObject] Sketch018
  FullyConstrained = true
  sketch-geometry (7):
    g0: LineSegment StartX=0 StartY=0 StartZ=0 EndX=0 EndY=6 EndZ=0
    g1: Circle CenterX=0 CenterY=0 CenterZ=0 NormalX=0 NormalY=0 NormalZ=1 AngleXU=0 Radius=1
    g2: Circle CenterX=8 CenterY=6 CenterZ=0 NormalX=0 NormalY=0 NormalZ=1 AngleXU=0 Radius=1
    g3: BSplineCurve PolesCount=3 KnotsCount=2 Degree=2 IsPeriodic=0
    g4: GeomPoint X=0 Y=0 Z=0
    g5: GeomPoint X=8 Y=6 Z=0
    g6: LineSegment StartX=0 StartY=6 StartZ=0 EndX=8 EndY=6 EndZ=0
  constraints (14):
    c: Coincident(g0,g-1)
    c: Distance(g0) = 6
    c: Vertical(g0)
    c: Coincident(g3,g0)
    c: Weight(g1) = 1
    c: Equal(g1,g2)
    c: InternalAlignment(g1,g3)
    c: InternalAlignment(g2,g3)
    c: InternalAlignment(g4,g3)
    c: InternalAlignment(g5,g3)
    c: Block(g3)
    c: Coincident(g6,g0)
    c: Coincident(g6,g3)
    c: Horizontal(g6)
FEATURE [Part::Extrusion] Extrude012  label="caseScrewPillarBracket"
  Base = -> Sketch018
  Dir = (0,0,1)
  DirMode = 2
  FaceMakerClass = Part::FaceMakerBullseye
  LengthFwd = 2.4
  LengthRev = 0
  Placement = pos=(15.76,29,8.8) rot=(0,1,0;0rad)
  Solid = true
  Symmetric = false
FEATURE [Sketcher::SketchObject] Sketch019
  FullyConstrained = true
  sketch-geometry (7):
    g0: LineSegment StartX=0 StartY=0 StartZ=0 EndX=0 EndY=6 EndZ=0
    g1: Circle CenterX=0 CenterY=0 CenterZ=0 NormalX=0 NormalY=0 NormalZ=1 AngleXU=0 Radius=1
    g2: Circle CenterX=8 CenterY=6 CenterZ=0 NormalX=0 NormalY=0 NormalZ=1 AngleXU=0 Radius=1
    g3: BSplineCurve PolesCount=3 KnotsCount=2 Degree=2 IsPeriodic=0
    g4: GeomPoint X=0 Y=0 Z=0
    g5: GeomPoint X=8 Y=6 Z=0
    g6: LineSegment StartX=0 StartY=6 StartZ=0 EndX=8 EndY=6 EndZ=0
  constraints (14):
    c: Coincident(g0,g-1)
    c: Distance(g0) = 6
    c: Vertical(g0)
    c: Coincident(g3,g0)
    c: Weight(g1) = 1
    c: Equal(g1,g2)
    c: InternalAlignment(g1,g3)
    c: InternalAlignment(g2,g3)
    c: InternalAlignment(g4,g3)
    c: InternalAlignment(g5,g3)
    c: Block(g3)
    c: Coincident(g6,g0)
    c: Coincident(g6,g3)
    c: Horizontal(g6)
FEATURE [Part::Extrusion] Extrude013  label="caseScrewPillarBracket001"
  Base = -> Sketch019
  Dir = (0,0,1)
  DirMode = 2
  FaceMakerClass = Part::FaceMakerBullseye
  LengthFwd = 2.4
  LengthRev = 0
  Placement = pos=(15.76,29,60.8) rot=(0,0,1;0rad)
  Solid = true
  Symmetric = false
FEATURE [Sketcher::SketchObject] Sketch020
  FullyConstrained = true
  sketch-geometry (7):
    g0: LineSegment StartX=0 StartY=0 StartZ=0 EndX=0 EndY=6 EndZ=0
    g1: Circle CenterX=0 CenterY=0 CenterZ=0 NormalX=0 NormalY=0 NormalZ=1 AngleXU=0 Radius=1
    g2: Circle CenterX=8 CenterY=6 CenterZ=0 NormalX=0 NormalY=0 NormalZ=1 AngleXU=0 Radius=1
    g3: BSplineCurve PolesCount=3 KnotsCount=2 Degree=2 IsPeriodic=0
    g4: GeomPoint X=0 Y=0 Z=0
    g5: GeomPoint X=8 Y=6 Z=0
    g6: LineSegment StartX=0 StartY=6 StartZ=0 EndX=8 EndY=6 EndZ=0
  constraints (14):
    c: Coincident(g0,g-1)
    c: Distance(g0) = 6
    c: Vertical(g0)
    c: Coincident(g3,g0)
    c: Weight(g1) = 1
    c: Equal(g1,g2)
    c: InternalAlignment(g1,g3)
    c: InternalAlignment(g2,g3)
    c: InternalAlignment(g4,g3)
    c: InternalAlignment(g5,g3)
    c: Block(g3)
    c: Coincident(g6,g0)
    c: Coincident(g6,g3)
    c: Horizontal(g6)
FEATURE [Part::Extrusion] Extrude014  label="caseScrewPillarBracket002"
  Base = -> Sketch020
  Dir = (0,0,1)
  DirMode = 2
  FaceMakerClass = Part::FaceMakerBullseye
  LengthFwd = 2.4
  LengthRev = 0
  Placement = pos=(13.7,29,13.26) rot=(0,-1,0;1.5708rad)
  Solid = true
  Symmetric = false
FEATURE [Sketcher::SketchObject] Sketch021
  FullyConstrained = true
  sketch-geometry (7):
    g0: LineSegment StartX=0 StartY=0 StartZ=0 EndX=0 EndY=6 EndZ=0
    g1: Circle CenterX=0 CenterY=0 CenterZ=0 NormalX=0 NormalY=0 NormalZ=1 AngleXU=0 Radius=1
    g2: Circle CenterX=8 CenterY=6 CenterZ=0 NormalX=0 NormalY=0 NormalZ=1 AngleXU=0 Radius=1
    g3: BSplineCurve PolesCount=3 KnotsCount=2 Degree=2 IsPeriodic=0
    g4: GeomPoint X=0 Y=0 Z=0
    g5: GeomPoint X=8 Y=6 Z=0
    g6: LineSegment StartX=0 StartY=6 StartZ=0 EndX=8 EndY=6 EndZ=0
  constraints (14):
    c: Coincident(g0,g-1)
    c: Distance(g0) = 6
    c: Vertical(g0)
    c: Coincident(g3,g0)
    c: Weight(g1) = 1
    c: Equal(g1,g2)
    c: InternalAlignment(g1,g3)
    c: InternalAlignment(g2,g3)
    c: InternalAlignment(g4,g3)
    c: InternalAlignment(g5,g3)
    c: Block(g3)
    c: Coincident(g6,g0)
    c: Coincident(g6,g3)
    c: Horizontal(g6)
FEATURE [Part::Extrusion] Extrude015  label="caseScrewPillarBracket003"
  Base = -> Sketch021
  Dir = (0,0,1)
  DirMode = 2
  FaceMakerClass = Part::FaceMakerBullseye
  LengthFwd = 2.4
  LengthRev = 0
  Placement = pos=(11.3,29,58.74) rot=(0,1,0;1.5708rad)
  Solid = true
  Symmetric = false
FEATURE [Sketcher::SketchObject] Sketch022
  FullyConstrained = true
  sketch-geometry (7):
    g0: LineSegment StartX=0 StartY=0 StartZ=0 EndX=0 EndY=6 EndZ=0
    g1: Circle CenterX=0 CenterY=0 CenterZ=0 NormalX=0 NormalY=0 NormalZ=1 AngleXU=0 Radius=1
    g2: Circle CenterX=8 CenterY=6 CenterZ=0 NormalX=0 NormalY=0 NormalZ=1 AngleXU=0 Radius=1
    g3: BSplineCurve PolesCount=3 KnotsCount=2 Degree=2 IsPeriodic=0
    g4: GeomPoint X=0 Y=0 Z=0
    g5: GeomPoint X=8 Y=6 Z=0
    g6: LineSegment StartX=0 StartY=6 StartZ=0 EndX=8 EndY=6 EndZ=0
  constraints (14):
    c: Coincident(g0,g-1)
    c: Distance(g0) = 6
    c: Vertical(g0)
    c: Coincident(g3,g0)
    c: Weight(g1) = 1
    c: Equal(g1,g2)
    c: InternalAlignment(g1,g3)
    c: InternalAlignment(g2,g3)
    c: InternalAlignment(g4,g3)
    c: InternalAlignment(g5,g3)
    c: Block(g3)
    c: Coincident(g6,g0)
    c: Coincident(g6,g3)
    c: Horizontal(g6)
FEATURE [Part::Extrusion] Extrude016  label="caseScrewPillarBracket004"
  Base = -> Sketch022
  Dir = (0,0,1)
  DirMode = 2
  FaceMakerClass = Part::FaceMakerBullseye
  LengthFwd = 2.4
  LengthRev = 0
  Placement = pos=(88.3,29,65.23) rot=(0,1,0;1.5708rad)
  Solid = true
  Symmetric = false
FEATURE [Sketcher::SketchObject] Sketch023
  FullyConstrained = true
  sketch-geometry (7):
    g0: LineSegment StartX=0 StartY=0 StartZ=0 EndX=0 EndY=6 EndZ=0
    g1: Circle CenterX=0 CenterY=0 CenterZ=0 NormalX=0 NormalY=0 NormalZ=1 AngleXU=0 Radius=1
    g2: Circle CenterX=8 CenterY=6 CenterZ=0 NormalX=0 NormalY=0 NormalZ=1 AngleXU=0 Radius=1
    g3: BSplineCurve PolesCount=3 KnotsCount=2 Degree=2 IsPeriodic=0
    g4: GeomPoint X=0 Y=0 Z=0
    g5: GeomPoint X=8 Y=6 Z=0
    g6: LineSegment StartX=0 StartY=6 StartZ=0 EndX=8 EndY=6 EndZ=0
  constraints (14):
    c: Coincident(g0,g-1)
    c: Distance(g0) = 6
    c: Vertical(g0)
    c: Coincident(g3,g0)
    c: Weight(g1) = 1
    c: Equal(g1,g2)
    c: InternalAlignment(g1,g3)
    c: InternalAlignment(g2,g3)
    c: InternalAlignment(g4,g3)
    c: InternalAlignment(g5,g3)
    c: Block(g3)
    c: Coincident(g6,g0)
    c: Coincident(g6,g3)
    c: Horizontal(g6)
FEATURE [Part::Extrusion] Extrude017  label="caseScrewPillarBracket005"
  Base = -> Sketch023
  Dir = (0,0,1)
  DirMode = 2
  FaceMakerClass = Part::FaceMakerBullseye
  LengthFwd = 2.4
  LengthRev = 0
  Placement = pos=(90.7,29,6.77) rot=(0,-1,0;1.5708rad)
  Solid = true
  Symmetric = false
FEATURE [Sketcher::SketchObject] Sketch024
  FullyConstrained = true
  sketch-geometry (7):
    g0: LineSegment StartX=0 StartY=0 StartZ=0 EndX=0 EndY=6 EndZ=0
    g1: Circle CenterX=0 CenterY=0 CenterZ=0 NormalX=0 NormalY=0 NormalZ=1 AngleXU=0 Radius=1
    g2: Circle CenterX=8 CenterY=6 CenterZ=0 NormalX=0 NormalY=0 NormalZ=1 AngleXU=0 Radius=1
    g3: BSplineCurve PolesCount=3 KnotsCount=2 Degree=2 IsPeriodic=0
    g4: GeomPoint X=0 Y=0 Z=0
    g5: GeomPoint X=8 Y=6 Z=0
    g6: LineSegment StartX=0 StartY=6 StartZ=0 EndX=8 EndY=6 EndZ=0
  constraints (14):
    c: Coincident(g0,g-1)
    c: Distance(g0) = 6
    c: Vertical(g0)
    c: Coincident(g3,g0)
    c: Weight(g1) = 1
    c: Equal(g1,g2)
    c: InternalAlignment(g1,g3)
    c: InternalAlignment(g2,g3)
    c: InternalAlignment(g4,g3)
    c: InternalAlignment(g5,g3)
    c: Block(g3)
    c: Coincident(g6,g0)
    c: Coincident(g6,g3)
    c: Horizontal(g6)
FEATURE [Part::Extrusion] Extrude018  label="caseScrewPillarBracket006"
  Base = -> Sketch024
  Dir = (0,0,1)
  DirMode = 2
  FaceMakerClass = Part::FaceMakerBullseye
  LengthFwd = 2.4
  LengthRev = 0
  Placement = pos=(103.7,29,6.77) rot=(0,-1,0;1.5708rad)
  Solid = true
  Symmetric = false
FEATURE [Sketcher::SketchObject] Sketch025
  FullyConstrained = true
  sketch-geometry (7):
    g0: LineSegment StartX=0 StartY=0 StartZ=0 EndX=0 EndY=6 EndZ=0
    g1: Circle CenterX=0 CenterY=0 CenterZ=0 NormalX=0 NormalY=0 NormalZ=1 AngleXU=0 Radius=1
    g2: Circle CenterX=8 CenterY=6 CenterZ=0 NormalX=0 NormalY=0 NormalZ=1 AngleXU=0 Radius=1
    g3: BSplineCurve PolesCount=3 KnotsCount=2 Degree=2 IsPeriodic=0
    g4: GeomPoint X=0 Y=0 Z=0
    g5: GeomPoint X=8 Y=6 Z=0
    g6: LineSegment StartX=0 StartY=6 StartZ=0 EndX=8 EndY=6 EndZ=0
  constraints (14):
    c: Coincident(g0,g-1)
    c: Distance(g0) = 6
    c: Vertical(g0)
    c: Coincident(g3,g0)
    c: Weight(g1) = 1
    c: Equal(g1,g2)
    c: InternalAlignment(g1,g3)
    c: InternalAlignment(g2,g3)
    c: InternalAlignment(g4,g3)
    c: InternalAlignment(g5,g3)
    c: Block(g3)
    c: Coincident(g6,g0)
    c: Coincident(g6,g3)
    c: Horizontal(g6)
FEATURE [Part::Extrusion] Extrude019  label="caseScrewPillarBracket007"
  Base = -> Sketch025
  Dir = (0,0,1)
  DirMode = 2
  FaceMakerClass = Part::FaceMakerBullseye
  LengthFwd = 2.4
  LengthRev = 0
  Placement = pos=(101.3,29,65.23) rot=(0,1,0;1.5708rad)
  Solid = true
  Symmetric = false
FEATURE [Part::Box] Box011  label="frontCaseScrewPillarBracket"
  AttacherType = Attacher::AttachEngine3D
  Height = 2.4
  Length = 16
  Placement = pos=(87,28,2.3) rot=(0,0,1;0rad)
  Width = 7
FEATURE [Part::Box] Box012  label="frontCaseScrewPillarBracket001"
  AttacherType = Attacher::AttachEngine3D
  Height = 2.4
  Length = 16
  Placement = pos=(87,28,67.3) rot=(0,0,1;0rad)
  Width = 7
FEATURE [Sketcher::SketchObject] Sketch026
  FullyConstrained = true
  sketch-geometry (17):
    g0: Circle CenterX=-3.5 CenterY=23.5 CenterZ=0 NormalX=0 NormalY=0 NormalZ=1 AngleXU=0 Radius=1
    g1: Circle CenterX=-1 CenterY=15.25 CenterZ=0 NormalX=0 NormalY=0 NormalZ=1 AngleXU=0 Radius=1
    g2: Circle CenterX=-3.5 CenterY=7 CenterZ=0 NormalX=0 NormalY=0 NormalZ=1 AngleXU=0 Radius=1
    g3: BSplineCurve PolesCount=3 KnotsCount=2 Degree=2 IsPeriodic=0
    g4: GeomPoint X=-3.5 Y=23.5 Z=0
    g5: GeomPoint X=-3.5 Y=7 Z=0
    g6: Circle CenterX=-4.8 CenterY=30.5 CenterZ=0 NormalX=0 NormalY=0 NormalZ=1 AngleXU=0 Radius=1
    g7: Circle CenterX=-3.5 CenterY=30.5 CenterZ=0 NormalX=0 NormalY=0 NormalZ=1 AngleXU=0 Radius=1
    g8: Circle CenterX=-3.5 CenterY=29.2 CenterZ=0 NormalX=0 NormalY=0 NormalZ=1 AngleXU=0 Radius=1
    g9: BSplineCurve PolesCount=3 KnotsCount=2 Degree=2 IsPeriodic=0
    g10: GeomPoint X=-4.8 Y=30.5 Z=0
    g11: GeomPoint X=-3.5 Y=29.2 Z=0
    g12: LineSegment StartX=-3.5 StartY=29.2 StartZ=0 EndX=-3.5 EndY=23.5 EndZ=0
    g13: LineSegment StartX=-4.8 StartY=30.5 StartZ=0 EndX=0 EndY=30.5 EndZ=0
    g14: LineSegment StartX=-3.5 StartY=5 StartZ=0 EndX=-3.5 EndY=7 EndZ=0
    g15: LineSegment StartX=0 StartY=5 StartZ=0 EndX=0 EndY=30.5 EndZ=0
    g16: LineSegment StartX=-3.5 StartY=5 StartZ=0 EndX=0 EndY=5 EndZ=0
  constraints (33):
    c: Weight(g0) = 1
    c: Equal(g0,g1)
    c: Equal(g0,g2)
    c: InternalAlignment(g0,g3)
    c: InternalAlignment(g1,g3)
    c: InternalAlignment(g2,g3)
    c: InternalAlignment(g4,g3)
    c: InternalAlignment(g5,g3)
    c: Block(g3)
    c: Weight(g6) = 1
    c: Equal(g6,g7)
    c: Equal(g6,g8)
    c: InternalAlignment(g6,g9)
    c: InternalAlignment(g7,g9)
    c: InternalAlignment(g8,g9)
    c: InternalAlignment(g10,g9)
    c: InternalAlignment(g11,g9)
    c: Block(g9)
    c: Coincident(g12,g9)
    c: Coincident(g12,g3)
    c: Vertical(g12)
    c: Coincident(g13,g9)
    c: Horizontal(g13)
    c: Distance(g13) = 4.8
    c: Coincident(g14,g3)
    c: Vertical(g14)
    c: Coincident(g15,g13)
    c: Vertical(g15)
    c: Tangent(g15,g1)
    c: Distance(g14) = 2
    c: Coincident(g16,g14)
    c: Horizontal(g16)
    c: Coincident(g15,g16)
FEATURE [Part::Feature] Face050
  shape: bbox 4.8 x 25.5 x 2e-07 mm, 1 faces, 0 solids (baked)
FEATURE [Part::Revolution] Revolve054  label="moreFrontCaseScrewPost001"
  Angle = 360
  Axis = (0,1,0)
  Base = (0,0,0)
  FaceMakerClass = Part::FaceMakerBullseye
  Placement = pos=(102.5,4.5,3.5) rot=(0,0,1;0rad)
  Solid = false
  Source = -> Face050
  Symmetric = false
FEATURE [Part::Feature] Face051
  shape: bbox 4.8 x 25.5 x 2e-07 mm, 1 faces, 0 solids (baked)
FEATURE [Part::Revolution] Revolve055  label="moreFrontCaseScrewPost002"
  Angle = 360
  Axis = (0,1,0)
  Base = (0,0,0)
  FaceMakerClass = Part::FaceMakerBullseye
  Placement = pos=(102.5,4.5,68.5) rot=(0,0,1;0rad)
  Solid = false
  Source = -> Face051
  Symmetric = false
FEATURE [Sketcher::SketchObject] Sketch027
  FullyConstrained = true
  sketch-geometry (10):
    g0: LineSegment StartX=-1.6 StartY=4.7 StartZ=0 EndX=-1.6 EndY=1.7 EndZ=0
    g1: LineSegment StartX=-3.5 StartY=4.7 StartZ=0 EndX=-1.6 EndY=4.7 EndZ=0
    g2: LineSegment StartX=-1.6 StartY=1.7 StartZ=0 EndX=-1.6 EndY=1.5 EndZ=0
    g3: LineSegment StartX=-1.6 StartY=1.5 StartZ=0 EndX=-5.2 EndY=1.5 EndZ=0
    g4: Circle CenterX=-3.5 CenterY=4.7 CenterZ=0 NormalX=0 NormalY=0 NormalZ=1 AngleXU=0 Radius=1
    g5: Circle CenterX=-3.59627 CenterY=2.99743 CenterZ=0 NormalX=0 NormalY=0 NormalZ=1 AngleXU=0 Radius=1
    g6: Circle CenterX=-5.2 CenterY=1.5 CenterZ=0 NormalX=0 NormalY=0 NormalZ=1 AngleXU=0 Radius=1
    g7: BSplineCurve PolesCount=3 KnotsCount=2 Degree=2 IsPeriodic=0
    g8: GeomPoint X=-3.5 Y=4.7 Z=0
    g9: GeomPoint X=-5.2 Y=1.5 Z=0
  constraints (23):
    c: Vertical(g0)
    c: Distance(g0) = 3
    c: Coincident(g1,g0)
    c: Horizontal(g1)
    c: Block(g0)
    c: Block(g1)
    c: Coincident(g2,g0)
    c: Vertical(g2)
    c: Distance(g2) = 0.2
    c: Coincident(g3,g2)
    c: Horizontal(g3)
    c: Block(g3)
    c: Coincident(g7,g1)
    c: Weight(g4) = 1
    c: Equal(g4,g5)
    c: Equal(g4,g6)
    c: Coincident(g7,g3)
    c: InternalAlignment(g4,g7)
    c: InternalAlignment(g5,g7)
    c: InternalAlignment(g6,g7)
    c: InternalAlignment(g8,g7)
    c: InternalAlignment(g9,g7)
    c: Block(g7)
FEATURE [Sketcher::SketchObject] Sketch028
  FullyConstrained = true
  sketch-geometry (18):
    g0: LineSegment StartX=0 StartY=3e-16 StartZ=0 EndX=0 EndY=1.7 EndZ=0
    g1: LineSegment StartX=-3.5 StartY=0 StartZ=0 EndX=-3.5 EndY=0.9 EndZ=0
    g2: Circle CenterX=-2.7 CenterY=1.7 CenterZ=0 NormalX=0 NormalY=0 NormalZ=1 AngleXU=0 Radius=1
    g3: Circle CenterX=-3.5 CenterY=1.7 CenterZ=0 NormalX=0 NormalY=0 NormalZ=1 AngleXU=0 Radius=1
    g4: Circle CenterX=-3.5 CenterY=0.9 CenterZ=0 NormalX=0 NormalY=0 NormalZ=1 AngleXU=0 Radius=1
    g5: BSplineCurve PolesCount=3 KnotsCount=2 Degree=2 IsPeriodic=0
    g6: GeomPoint X=-2.7 Y=1.7 Z=0
    g7: GeomPoint X=-3.5 Y=0.9 Z=0
    g8: LineSegment StartX=-3.5 StartY=0 StartZ=0 EndX=-3.5 EndY=-7 EndZ=0
    g9: LineSegment StartX=0 StartY=3e-16 StartZ=0 EndX=0 EndY=-7 EndZ=0
    g10: LineSegment StartX=-3.5 StartY=-7 StartZ=0 EndX=0 EndY=-7 EndZ=0
    g11: LineSegment StartX=-2.7 StartY=1.7 StartZ=0 EndX=-1.6 EndY=1.7 EndZ=0
    g12: LineSegment StartX=0 StartY=1.7 StartZ=0 EndX=0 EndY=4.5 EndZ=0
    g13: LineSegment StartX=0 StartY=4.5 StartZ=0 EndX=0 EndY=10.8 EndZ=0
    g14: LineSegment StartX=0 StartY=10.8 StartZ=0 EndX=-2 EndY=10.8 EndZ=0
    g15: LineSegment StartX=-1.6 StartY=4.7 StartZ=0 EndX=-1.6 EndY=1.7 EndZ=0
    g16: LineSegment StartX=-1.6 StartY=4.7 StartZ=0 EndX=-2 EndY=4.7 EndZ=0
    g17: LineSegment StartX=-2 StartY=4.7 StartZ=0 EndX=-2 EndY=10.8 EndZ=0
  constraints (44):
    c: Vertical(g0)
    c: Vertical(g1)
    c: Distance(g1) = 0.9
    c: Block(g0)
    c: Distance(g0) = 1.7
    c: Weight(g2) = 1
    c: Equal(g2,g3)
    c: Equal(g2,g4)
    c: Coincident(g5,g1)
    c: InternalAlignment(g2,g5)
    c: InternalAlignment(g3,g5)
    c: InternalAlignment(g4,g5)
    c: InternalAlignment(g6,g5)
    c: InternalAlignment(g7,g5)
    c: Block(g5)
    c: Coincident(g8,g1)
    c: Vertical(g8)
    c: Distance(g8) = 7
    c: Vertical(g9)
    c: Equal(g8,g9) = 7
    c: Coincident(g9,g0)
    c: Coincident(g10,g8)
    c: Coincident(g10,g9)
    c: Horizontal(g10)
    c: Coincident(g11,g5)
    c: Horizontal(g11)
    c: Coincident(g12,g0)
    c: Vertical(g12)
    c: Distance(g12) = 2.8
    c: Coincident(g13,g12)
    c: Vertical(g13)
    c: Distance(g13) = 6.3
    c: Coincident(g14,g13)
    c: Horizontal(g14)
    c: Distance(g14) = 2
    c: Vertical(g15)
    c: Distance(g15) = 3
    c: Block(g11)
    c: Coincident(g15,g11)
    c: Coincident(g16,g15)
    c: Horizontal(g16)
    c: Coincident(g17,g16)
    c: Coincident(g17,g14)
    c: Vertical(g17)
FEATURE [Part::Revolution] Revolve040  label="backCaseScrewRetainer001"
  Angle = 360
  Axis = (0,1,0)
  Base = (0,0,0)
  FaceMakerClass = Part::FaceMakerBullseye
  Placement = pos=(12.5,3,10) rot=(0,0,1;0rad)
  Solid = false
  Source = -> Face036
  Symmetric = false
FEATURE [Part::Feature] Face055
  shape: bbox 3.5 x 30.2 x 2e-07 mm, 1 faces, 0 solids (baked)
FEATURE [Part::Revolution] Revolve059  label="backCaseScrewPost"
  Angle = 360
  Axis = (0,1,0)
  Base = (0,0,0)
  FaceMakerClass = Part::FaceMakerBullseye
  Placement = pos=(12.5,4.5,10) rot=(0,0,1;0rad)
  Solid = false
  Source = -> Face055
  Symmetric = false
FEATURE [Part::Feature] Face056
  shape: bbox 3.5 x 30.2 x 2e-07 mm, 1 faces, 0 solids (baked)
FEATURE [Part::Revolution] Revolve060  label="backCaseScrewPost001"
  Angle = 360
  Axis = (0,1,0)
  Base = (0,0,0)
  FaceMakerClass = Part::FaceMakerBullseye
  Placement = pos=(12.5,4.5,62) rot=(0,0,1;0rad)
  Solid = false
  Source = -> Face056
  Symmetric = false
FEATURE [Part::Feature] Face057
  shape: bbox 3.5 x 17.8 x 2e-07 mm, 1 faces, 0 solids (baked)
FEATURE [Part::Revolution] Revolve061  label="removeToCreateScrewAndThreadedInsertHole"
  Angle = 360
  Axis = (0,1,0)
  Base = (0,0,0)
  FaceMakerClass = Part::FaceMakerBullseye
  Placement = pos=(12.5,0,10) rot=(0,0,1;0rad)
  Solid = false
  Source = -> Face057
  Symmetric = false
FEATURE [Part::Feature] Face058
  shape: bbox 3.5 x 17.8 x 2e-07 mm, 1 faces, 0 solids (baked)
FEATURE [Part::Revolution] Revolve062  label="removeToCreateScrewAndThreadedInsertHole001"
  Angle = 360
  Axis = (0,1,0)
  Base = (0,0,0)
  FaceMakerClass = Part::FaceMakerBullseye
  Placement = pos=(12.5,0,62) rot=(0,0,1;0rad)
  Solid = false
  Source = -> Face058
  Symmetric = false
FEATURE [Part::Feature] Face059
  shape: bbox 3.5 x 17.8 x 2e-07 mm, 1 faces, 0 solids (baked)
FEATURE [Part::Revolution] Revolve063  label="removeToCreateScrewAndThreadedInsertHole002"
  Angle = 360
  Axis = (0,1,0)
  Base = (0,0,0)
  FaceMakerClass = Part::FaceMakerBullseye
  Placement = pos=(89.5,0,68.5) rot=(0,0,1;0rad)
  Solid = false
  Source = -> Face059
  Symmetric = false
FEATURE [Part::Feature] Face060
  shape: bbox 3.5 x 17.8 x 2e-07 mm, 1 faces, 0 solids (baked)
FEATURE [Part::Revolution] Revolve064  label="removeToCreateScrewAndThreadedInsertHole003"
  Angle = 360
  Axis = (0,1,0)
  Base = (0,0,0)
  FaceMakerClass = Part::FaceMakerBullseye
  Placement = pos=(89.5,0,3.5) rot=(0,0,1;0rad)
  Solid = false
  Source = -> Face060
  Symmetric = false
FEATURE [Part::Feature] Face061
  shape: bbox 3.5 x 17.8 x 2e-07 mm, 1 faces, 0 solids (baked)
FEATURE [Part::Revolution] Revolve065  label="removeToCreateScrewAndThreadedInsertHole004"
  Angle = 360
  Axis = (0,1,0)
  Base = (0,0,0)
  FaceMakerClass = Part::FaceMakerBullseye
  Placement = pos=(102.5,4.7,3.5) rot=(0,0,1;0rad)
  Solid = false
  Source = -> Face061
  Symmetric = false
FEATURE [Part::Feature] Face062
  shape: bbox 3.5 x 17.8 x 2e-07 mm, 1 faces, 0 solids (baked)
FEATURE [Part::Revolution] Revolve066  label="removeToCreateScrewAndThreadedInsertHole005"
  Angle = 360
  Axis = (0,1,0)
  Base = (0,0,0)
  FaceMakerClass = Part::FaceMakerBullseye
  Placement = pos=(102.5,4.7,68.5) rot=(0,0,1;0rad)
  Solid = false
  Source = -> Face062
  Symmetric = false
FEATURE [Part::MultiFuse] Fusion047  label="makeHoles"
  Shapes = -> [Revolve066,Revolve065,Revolve064,Revolve063,Revolve062,Revolve061]
FEATURE [Part::Feature] Face063
  shape: bbox 3.6 x 3.2 x 2e-07 mm, 1 faces, 0 solids (baked)
FEATURE [Part::Revolution] Revolve067  label="moreFrontCaseScrewRetainer002"
  Angle = 360
  Axis = (0,1,0)
  Base = (0,0,0)
  FaceMakerClass = Part::FaceMakerBullseye
  Placement = pos=(102.5,4.5,68.5) rot=(0,0,1;0rad)
  Solid = false
  Source = -> Face063
  Symmetric = false
FEATURE [Part::Feature] Face064
  shape: bbox 3.6 x 3.2 x 2e-07 mm, 1 faces, 0 solids (baked)
FEATURE [Part::Revolution] Revolve068  label="moreFrontCaseScrewRetainer003"
  Angle = 360
  Axis = (0,1,0)
  Base = (0,0,0)
  FaceMakerClass = Part::FaceMakerBullseye
  Placement = pos=(102.5,4.5,3.5) rot=(0,0,1;0rad)
  Solid = false
  Source = -> Face064
  Symmetric = false
FEATURE [Part::Feature] Face065
  shape: bbox 3.5 x 17.8 x 2e-07 mm, 1 faces, 0 solids (baked)
FEATURE [Part::Revolution] Revolve069  label="removeToCreateScrewAndThreadedInsertHole006"
  Angle = 360
  Axis = (0,1,0)
  Base = (0,0,0)
  FaceMakerClass = Part::FaceMakerBullseye
  Placement = pos=(12.5,0,10) rot=(0,0,1;0rad)
  Solid = false
  Source = -> Face065
  Symmetric = false
FEATURE [Part::Feature] Face066
  shape: bbox 3.5 x 17.8 x 2e-07 mm, 1 faces, 0 solids (baked)
FEATURE [Part::Revolution] Revolve070  label="removeToCreateScrewAndThreadedInsertHole007"
  Angle = 360
  Axis = (0,1,0)
  Base = (0,0,0)
  FaceMakerClass = Part::FaceMakerBullseye
  Placement = pos=(12.5,0,62) rot=(0,0,1;0rad)
  Solid = false
  Source = -> Face066
  Symmetric = false
FEATURE [Part::Feature] Face067
  shape: bbox 3.5 x 17.8 x 2e-07 mm, 1 faces, 0 solids (baked)
FEATURE [Part::Revolution] Revolve071  label="removeToCreateScrewAndThreadedInsertHole008"
  Angle = 360
  Axis = (0,1,0)
  Base = (0,0,0)
  FaceMakerClass = Part::FaceMakerBullseye
  Placement = pos=(89.5,0,68.5) rot=(0,0,1;0rad)
  Solid = false
  Source = -> Face067
  Symmetric = false
FEATURE [Part::Feature] Face068
  shape: bbox 3.5 x 17.8 x 2e-07 mm, 1 faces, 0 solids (baked)
FEATURE [Part::Revolution] Revolve072  label="removeToCreateScrewAndThreadedInsertHole009"
  Angle = 360
  Axis = (0,1,0)
  Base = (0,0,0)
  FaceMakerClass = Part::FaceMakerBullseye
  Placement = pos=(89.5,0,3.5) rot=(0,0,1;0rad)
  Solid = false
  Source = -> Face068
  Symmetric = false
FEATURE [Part::Feature] Face069
  shape: bbox 3.5 x 17.8 x 2e-07 mm, 1 faces, 0 solids (baked)
FEATURE [Part::Feature] Face070
  shape: bbox 3.5 x 17.8 x 2e-07 mm, 1 faces, 0 solids (baked)
FEATURE [Part::Revolution] Revolve073  label="removeToCreateScrewAndThreadedInsertHole010"
  Angle = 360
  Axis = (0,1,0)
  Base = (0,0,0)
  FaceMakerClass = Part::FaceMakerBullseye
  Placement = pos=(102.5,4.7,3.5) rot=(0,0,1;0rad)
  Solid = false
  Source = -> Face069
  Symmetric = false
FEATURE [Part::Revolution] Revolve074  label="removeToCreateScrewAndThreadedInsertHole011"
  Angle = 360
  Axis = (0,1,0)
  Base = (0,0,0)
  FaceMakerClass = Part::FaceMakerBullseye
  Placement = pos=(102.5,4.7,68.5) rot=(0,0,1;0rad)
  Solid = false
  Source = -> Face070
  Symmetric = false
FEATURE [Part::MultiFuse] Fusion048  label="makeHoles001"
  Shapes = -> [Revolve074,Revolve073,Revolve072,Revolve071,Revolve070,Revolve069]
FEATURE [Part::MultiFuse] Fusion049  label="caseScrewRetainers"
  Shapes = -> [Revolve067,Revolve068,Revolve048,Revolve047,Revolve039,Revolve040]
FEATURE [Part::Cut] Cut015  label="caseScrewRetainers001"
  Base = -> Fusion049
  Tool = -> Fusion048
FEATURE [Part::MultiFuse] Fusion050  label="casePillars"
  Shapes = -> [Revolve055,Revolve054,Revolve043,Revolve046,Revolve059,Revolve060]
FEATURE [Part::Feature] Face071 .. Face076  x6 (patterned run collapsed; names and placements below)
  shape: bbox 3.5 x 17.8 x 2e-07 mm, 1 faces, 0 solids (baked)
FEATURE [Part::Revolution] Revolve075  label="removeToCreateScrewAndThreadedInsertHole012"
  Angle = 360
  Axis = (0,1,0)
  Base = (0,0,0)
  FaceMakerClass = Part::FaceMakerBullseye
  Placement = pos=(12.5,0,10) rot=(0,0,1;0rad)
  Solid = false
  Source = -> Face071
  Symmetric = false
FEATURE [Part::Revolution] Revolve076  label="removeToCreateScrewAndThreadedInsertHole013"
  Angle = 360
  Axis = (0,1,0)
  Base = (0,0,0)
  FaceMakerClass = Part::FaceMakerBullseye
  Placement = pos=(12.5,0,62) rot=(0,0,1;0rad)
  Solid = false
  Source = -> Face072
  Symmetric = false
FEATURE [Part::Revolution] Revolve077  label="removeToCreateScrewAndThreadedInsertHole014"
  Angle = 360
  Axis = (0,1,0)
  Base = (0,0,0)
  FaceMakerClass = Part::FaceMakerBullseye
  Placement = pos=(89.5,0,68.5) rot=(0,0,1;0rad)
  Solid = false
  Source = -> Face073
  Symmetric = false
FEATURE [Part::Revolution] Revolve078  label="removeToCreateScrewAndThreadedInsertHole015"
  Angle = 360
  Axis = (0,1,0)
  Base = (0,0,0)
  FaceMakerClass = Part::FaceMakerBullseye
  Placement = pos=(89.5,0,3.5) rot=(0,0,1;0rad)
  Solid = false
  Source = -> Face074
  Symmetric = false
FEATURE [Part::Revolution] Revolve079  label="removeToCreateScrewAndThreadedInsertHole016"
  Angle = 360
  Axis = (0,1,0)
  Base = (0,0,0)
  FaceMakerClass = Part::FaceMakerBullseye
  Placement = pos=(102.5,4.7,3.5) rot=(0,0,1;0rad)
  Solid = false
  Source = -> Face075
  Symmetric = false
FEATURE [Part::Revolution] Revolve080  label="removeToCreateScrewAndThreadedInsertHole017"
  Angle = 360
  Axis = (0,1,0)
  Base = (0,0,0)
  FaceMakerClass = Part::FaceMakerBullseye
  Placement = pos=(102.5,4.7,68.5) rot=(0,0,1;0rad)
  Solid = false
  Source = -> Face076
  Symmetric = false
FEATURE [Part::MultiFuse] Fusion051  label="makeHoles002"
  Shapes = -> [Revolve080,Revolve079,Revolve078,Revolve077,Revolve076,Revolve075]
FEATURE [Part::Cut] Cut016  label="caesPillars"
  Base = -> Fusion050
  Tool = -> Fusion051
FEATURE [Part::Revolution] Revolve009  label="plugHousing016"
  Angle = 360
  Axis = (0,1,0)
  Base = (0,0,0)
  FaceMakerClass = Part::FaceMakerBullseye
  Placement = pos=(0,0,36.15) rot=(0,0,1;0rad)
  Solid = false
  Source = -> Face012
  Symmetric = false
FEATURE [Part::MultiFuse] Fusion014  label="plugHousing023"
  Placement = pos=(0,0,0) rot=(0,0,1;1.5708rad)
  Shapes = -> [Revolve011,Revolve009]
FEATURE [Part::Revolution] Revolve010  label="plugHousing017"
  Angle = 360
  Axis = (0,1,0)
  Base = (0,0,0)
  FaceMakerClass = Part::FaceMakerBullseye
  Placement = pos=(0,0,36.15) rot=(0,0,1;0rad)
  Solid = false
  Source = -> Face014
  Symmetric = false
FEATURE [Part::MultiFuse] Fusion015  label="plugHousing024"
  Placement = pos=(0,0,0) rot=(0,0,1;1.5708rad)
  Shapes = -> [Revolve010,Revolve015]
FEATURE [Part::Revolution] Revolve014  label="plugHousing026"
  Angle = 360
  Axis = (0,1,0)
  Base = (0,0,0)
  FaceMakerClass = Part::FaceMakerBullseye
  Placement = pos=(0,0,36.15) rot=(0,0,1;0rad)
  Solid = false
  Source = -> Face011
  Symmetric = false
FEATURE [Part::Revolution] Revolve013  label="plugHousing025"
  Angle = 360
  Axis = (0,1,0)
  Base = (0,0,0)
  FaceMakerClass = Part::FaceMakerBullseye
  Placement = pos=(0,0,36.15) rot=(0,0,1;0rad)
  Solid = false
  Source = -> Face015
  Symmetric = false
FEATURE [Part::MultiFuse] Fusion016  label="plugHousing028"
  Placement = pos=(0,19,0) rot=(0,0,1;3.14159rad)
  Shapes = -> [Fusion014,Fusion013]
FEATURE [Part::MultiFuse] Fusion011  label="plugHousing018"
  Placement = pos=(0,0,0) rot=(0,0,1;1.5708rad)
  Shapes = -> [Revolve014,Revolve013]
FEATURE [Part::MultiFuse] Fusion012  label="plugHousing019"
  Placement = pos=(0,19,0) rot=(0,0,1;3.14159rad)
  Shapes = -> [Fusion011,Fusion015]
FEATURE [Part::MultiFuse] Fusion017  label="plugHousing029"
  Placement = pos=(122.621,0,-0.15) rot=(0,0,1;0rad)
  Shapes = -> [Fusion016,Fusion012]
FEATURE [Part::MultiFuse] Fusion052  label="casePillarRetainers"
  Shapes = -> [Extrude012,Extrude013,Extrude014,Extrude015,Extrude016,Extrude017,Extrude018,Extrude019,Box011,Box012]
FEATURE [Part::Feature] Face077
  shape: bbox 3.5 x 17.8 x 2e-07 mm, 1 faces, 0 solids (baked)
FEATURE [Part::Revolution] Revolve081  label="removeToCreateScrewAndThreadedInsertHole018"
  Angle = 360
  Axis = (0,1,0)
  Base = (0,0,0)
  FaceMakerClass = Part::FaceMakerBullseye
  Placement = pos=(62.3,30.3,19.7) rot=(0,0,1;0rad)
  Solid = false
  Source = -> Face077
  Symmetric = false
FEATURE [Part::Feature] Face078
  shape: bbox 3.5 x 17.8 x 2e-07 mm, 1 faces, 0 solids (baked)
FEATURE [Part::Revolution] Revolve082  label="removeToCreateScrewAndThreadedInsertHole019"
  Angle = 360
  Axis = (0,1,0)
  Base = (0,0,0)
  FaceMakerClass = Part::FaceMakerBullseye
  Placement = pos=(62.3,30.3,51.7) rot=(0,0,1;0rad)
  Solid = false
  Source = -> Face078
  Symmetric = false
FEATURE [Part::Feature] Face079
  shape: bbox 3.5 x 17.8 x 2e-07 mm, 1 faces, 0 solids (baked)
FEATURE [Part::Revolution] Revolve083  label="removeToCreateScrewAndThreadedInsertHole020"
  Angle = 360
  Axis = (0,1,0)
  Base = (0,0,0)
  FaceMakerClass = Part::FaceMakerBullseye
  Placement = pos=(30.3,30.3,19.7) rot=(0,0,1;0rad)
  Solid = false
  Source = -> Face079
  Symmetric = false
FEATURE [Part::Feature] Face080
  shape: bbox 3.5 x 17.8 x 2e-07 mm, 1 faces, 0 solids (baked)
FEATURE [Part::Revolution] Revolve084  label="removeToCreateScrewAndThreadedInsertHole021"
  Angle = 360
  Axis = (0,1,0)
  Base = (0,0,0)
  FaceMakerClass = Part::FaceMakerBullseye
  Placement = pos=(30.3,30.3,51.7) rot=(0,0,1;0rad)
  Solid = false
  Source = -> Face080
  Symmetric = false
FEATURE [Part::MultiFuse] Fusion053  label="createThreadedInsertHolesForFan"
  Shapes = -> [Revolve081,Revolve082,Revolve083,Revolve084]
FEATURE [Part::Cut] Cut017  label="fanScrewHousing001"
  Base = -> Fusion046
  Tool = -> Fusion053
FEATURE [Part::Feature] Face081
  shape: bbox 3.5 x 17.8 x 2e-07 mm, 1 faces, 0 solids (baked)
FEATURE [Part::Revolution] Revolve085  label="removeToCreateScrewAndThreadedInsertHole022"
  Angle = 360
  Axis = (0,1,0)
  Base = (0,0,0)
  FaceMakerClass = Part::FaceMakerBullseye
  Placement = pos=(62.3,30.3,19.7) rot=(0,0,1;0rad)
  Solid = false
  Source = -> Face081
  Symmetric = false
FEATURE [Part::Feature] Face082
  shape: bbox 3.5 x 17.8 x 2e-07 mm, 1 faces, 0 solids (baked)
FEATURE [Part::Revolution] Revolve086  label="removeToCreateScrewAndThreadedInsertHole023"
  Angle = 360
  Axis = (0,1,0)
  Base = (0,0,0)
  FaceMakerClass = Part::FaceMakerBullseye
  Placement = pos=(62.3,30.3,51.7) rot=(0,0,1;0rad)
  Solid = false
  Source = -> Face082
  Symmetric = false
FEATURE [Part::Feature] Face083
  shape: bbox 3.5 x 17.8 x 2e-07 mm, 1 faces, 0 solids (baked)
FEATURE [Part::Revolution] Revolve087  label="removeToCreateScrewAndThreadedInsertHole024"
  Angle = 360
  Axis = (0,1,0)
  Base = (0,0,0)
  FaceMakerClass = Part::FaceMakerBullseye
  Placement = pos=(30.3,30.3,19.7) rot=(0,0,1;0rad)
  Solid = false
  Source = -> Face083
  Symmetric = false
FEATURE [Part::Feature] Face084
  shape: bbox 3.5 x 17.8 x 2e-07 mm, 1 faces, 0 solids (baked)
FEATURE [Part::Revolution] Revolve088  label="removeToCreateScrewAndThreadedInsertHole025"
  Angle = 360
  Axis = (0,1,0)
  Base = (0,0,0)
  FaceMakerClass = Part::FaceMakerBullseye
  Placement = pos=(30.3,30.3,51.7) rot=(0,0,1;0rad)
  Solid = false
  Source = -> Face084
  Symmetric = false
FEATURE [Part::MultiFuse] Fusion054  label="createThreadedInsertHolesForFan001"
  Shapes = -> [Revolve085,Revolve086,Revolve087,Revolve088]
FEATURE [Part::Cut] Cut018  label="top007"
  Base = -> Fusion040
  Tool = -> Fusion054
FEATURE [Sketcher::SketchObject] Sketch029
  FullyConstrained = false
  Placement = pos=(0,0,0) rot=(1,0,0;1.5708rad)
  sketch-geometry (24):
    g0: ArcOfCircle CenterX=-4 CenterY=-10.5 CenterZ=0 NormalX=0 NormalY=0 NormalZ=1 AngleXU=0 Radius=1.5 StartAngle=6e-16 EndAngle=3.14159
    g1: ArcOfCircle CenterX=-34.2 CenterY=-10.5 CenterZ=0 NormalX=0 NormalY=0 NormalZ=1 AngleXU=0 Radius=1.5 StartAngle=0 EndAngle=3.14159
    g2: ArcOfCircle CenterX=-34.2 CenterY=-27.7 CenterZ=0 NormalX=0 NormalY=0 NormalZ=1 AngleXU=0 Radius=1.5 StartAngle=3.14159 EndAngle=6.28319
    g3: ArcOfCircle CenterX=-4 CenterY=-27.7 CenterZ=0 NormalX=0 NormalY=0 NormalZ=1 AngleXU=0 Radius=1.5 StartAngle=3.1416 EndAngle=6.28319
    g4: ArcOfCircle CenterX=-10 CenterY=-4.3 CenterZ=0 NormalX=0 NormalY=0 NormalZ=1 AngleXU=0 Radius=1.5 StartAngle=2e-16 EndAngle=3.14159
    g5: ArcOfCircle CenterX=-16.1 CenterY=-1.8 CenterZ=0 NormalX=0 NormalY=0 NormalZ=1 AngleXU=0 Radius=1.5 StartAngle=5e-16 EndAngle=3.14159
    g6: ArcOfCircle CenterX=-22.1 CenterY=-1.8 CenterZ=0 NormalX=0 NormalY=0 NormalZ=1 AngleXU=0 Radius=1.5 StartAngle=5e-16 EndAngle=3.14159
    g7: ArcOfCircle CenterX=-28.2 CenterY=-4.3 CenterZ=0 NormalX=0 NormalY=0 NormalZ=1 AngleXU=0 Radius=1.5 StartAngle=2e-16 EndAngle=3.14159
    g8: ArcOfCircle CenterX=-10 CenterY=-33.9 CenterZ=0 NormalX=0 NormalY=0 NormalZ=1 AngleXU=0 Radius=1.5 StartAngle=3.14159 EndAngle=6.28319
    g9: ArcOfCircle CenterX=-16.1 CenterY=-36.4 CenterZ=0 NormalX=0 NormalY=0 NormalZ=1 AngleXU=0 Radius=1.5 StartAngle=3.14159 EndAngle=6.28319
    g10: ArcOfCircle CenterX=-22.1 CenterY=-36.4 CenterZ=0 NormalX=0 NormalY=0 NormalZ=1 AngleXU=0 Radius=1.5 StartAngle=3.14159 EndAngle=6.28319
    g11: ArcOfCircle CenterX=-28.2 CenterY=-33.9 CenterZ=0 NormalX=0 NormalY=0 NormalZ=1 AngleXU=0 Radius=1.5 StartAngle=3.14159 EndAngle=6.28319
    g12: LineSegment StartX=-35.7 StartY=-10.5 StartZ=0 EndX=-35.7 EndY=-27.7 EndZ=0
    g13: LineSegment StartX=-32.7 StartY=-10.5 StartZ=0 EndX=-32.7 EndY=-27.7 EndZ=0
    g14: LineSegment StartX=-29.7 StartY=-33.9 StartZ=0 EndX=-29.7 EndY=-4.3 EndZ=0
    g15: LineSegment StartX=-26.7 StartY=-33.9 StartZ=0 EndX=-26.7 EndY=-4.3 EndZ=0
    g16: LineSegment StartX=-2.5 StartY=-10.5 StartZ=0 EndX=-2.5 EndY=-27.7 EndZ=0
    g17: LineSegment StartX=-8.5 StartY=-4.3 StartZ=0 EndX=-8.5 EndY=-33.9 EndZ=0
    g18: LineSegment StartX=-5.5 StartY=-10.5 StartZ=0 EndX=-5.5 EndY=-27.7 EndZ=0
    g19: LineSegment StartX=-11.5 StartY=-4.3 StartZ=0 EndX=-11.5 EndY=-33.9 EndZ=0
    g20: LineSegment StartX=-14.6 StartY=-1.8 StartZ=0 EndX=-14.6 EndY=-36.4 EndZ=0
    g21: LineSegment StartX=-17.6 StartY=-1.8 StartZ=0 EndX=-17.6 EndY=-36.4 EndZ=0
    g22: LineSegment StartX=-20.6 StartY=-36.4 StartZ=0 EndX=-20.6 EndY=-1.8 EndZ=0
    g23: LineSegment StartX=-23.6 StartY=-1.8 StartZ=0 EndX=-23.6 EndY=-36.4 EndZ=0
  constraints (48):
    c: Block(g0)
    c: Block(g1)
    c: Block(g2)
    c: Block(g3)
    c: Block(g4)
    c: Block(g5)
    c: Block(g6)
    c: Block(g7)
    c: Block(g8)
    c: Block(g9)
    c: Block(g10)
    c: Block(g11)
    c: Coincident(g12,g1)
    c: Coincident(g12,g2)
    c: Vertical(g12)
    c: Coincident(g13,g1)
    c: Coincident(g13,g2)
    c: Vertical(g13)
    c: Coincident(g14,g11)
    c: Coincident(g14,g7)
    c: Vertical(g14)
    c: Coincident(g15,g11)
    c: Coincident(g15,g7)
    c: Vertical(g15)
    c: Coincident(g16,g0)
    c: Coincident(g16,g3)
    c: Vertical(g16)
    c: Coincident(g17,g4)
    c: Coincident(g17,g8)
    c: Vertical(g17)
    c: Coincident(g18,g0)
    c: Coincident(g18,g3)
    c: Vertical(g18)
    c: Coincident(g19,g4)
    c: Coincident(g19,g8)
    c: Vertical(g19)
    c: Coincident(g20,g5)
    c: Coincident(g20,g9)
    c: Vertical(g20)
    c: Coincident(g21,g5)
    c: Coincident(g21,g9)
    c: Vertical(g21)
    c: Coincident(g22,g10)
    c: Coincident(g22,g6)
    c: Vertical(g22)
    c: Coincident(g23,g6)
    c: Coincident(g23,g10)
    c: Vertical(g23)
FEATURE [Part::Extrusion] Extrude020  label="removeToCreateFanGrillHoles"
  Base = -> Sketch029
  Dir = (0,-1,6e-16)
  DirMode = 2
  FaceMakerClass = Part::FaceMakerBullseye
  LengthFwd = 10
  LengthRev = 0
  Placement = pos=(65.4,44,54.82) rot=(0,0,1;0rad)
  Solid = true
  Symmetric = false
FEATURE [Part::MultiFuse] Fusion055  label="top008"
  Shapes = -> [Cut017,Cut018]
FEATURE [Part::Cut] Cut019  label="top009"
  Base = -> Fusion055
  Tool = -> Extrude020
FEATURE [App::MeasureDistance] Distance003  label="Distance: 71.95 mm"
  Distance = 71.9513
  P1 = (117,38,72)
  P2 = (117,38,0.0487319)
FEATURE [Sketcher::SketchObject] Sketch030
  FullyConstrained = true
  Placement = pos=(117,19,0) rot=(0.57735,0.57735,0.57735;2.0944rad)
  sketch-geometry (48):
    g0: LineSegment StartX=-49.19 StartY=69.25 StartZ=0 EndX=-49.19 EndY=66.25 EndZ=0
    g1: LineSegment StartX=-49.19 StartY=63.5 StartZ=0 EndX=-49.19 EndY=60.5 EndZ=0
    g2: LineSegment StartX=-49.19 StartY=57.75 StartZ=0 EndX=-49.19 EndY=54.75 EndZ=0
    g3: LineSegment StartX=-49.19 StartY=52 StartZ=0 EndX=-49.19 EndY=49 EndZ=0
    g4: LineSegment StartX=-49.19 StartY=46.25 StartZ=0 EndX=-49.19 EndY=43.25 EndZ=0
    g5: LineSegment StartX=-49.19 StartY=40.5 StartZ=0 EndX=-49.19 EndY=37.5 EndZ=0
    g6: LineSegment StartX=-49.19 StartY=34.5 StartZ=0 EndX=-49.19 EndY=31.5 EndZ=0
    g7: LineSegment StartX=-49.19 StartY=28.75 StartZ=0 EndX=-49.19 EndY=25.75 EndZ=0
    g8: LineSegment StartX=-49.19 StartY=23 StartZ=0 EndX=-49.19 EndY=20 EndZ=0
    g9: LineSegment StartX=-49.19 StartY=17.25 StartZ=0 EndX=-49.19 EndY=14.25 EndZ=0
    g10: LineSegment StartX=-49.19 StartY=11.5 StartZ=0 EndX=-49.19 EndY=8.5 EndZ=0
    g11: LineSegment StartX=-49.19 StartY=5.75 StartZ=0 EndX=-49.19 EndY=2.75 EndZ=0
    g12: ArcOfCircle CenterX=-1.5 CenterY=67.75 CenterZ=0 NormalX=0 NormalY=0 NormalZ=1 AngleXU=0 Radius=1.5 StartAngle=4.71239 EndAngle=7.85398
    g13: ArcOfCircle CenterX=-1.5 CenterY=62 CenterZ=0 NormalX=0 NormalY=0 NormalZ=1 AngleXU=0 Radius=1.5 StartAngle=4.71239 EndAngle=7.85398
    g14: ArcOfCircle CenterX=-1.5 CenterY=56.25 CenterZ=0 NormalX=0 NormalY=0 NormalZ=1 AngleXU=0 Radius=1.5 StartAngle=4.71239 EndAngle=7.85398
    g15: ArcOfCircle CenterX=-11.49 CenterY=50.5 CenterZ=0 NormalX=0 NormalY=0 NormalZ=1 AngleXU=0 Radius=1.5 StartAngle=4.71239 EndAngle=7.85398
    g16: ArcOfCircle CenterX=-16.28 CenterY=44.75 CenterZ=0 NormalX=0 NormalY=0 NormalZ=1 AngleXU=0 Radius=1.5 StartAngle=4.71239 EndAngle=7.85398
    g17: ArcOfCircle CenterX=-18.2337 CenterY=39 CenterZ=0 NormalX=0 NormalY=0 NormalZ=1 AngleXU=0 Radius=1.5 StartAngle=4.71485 EndAngle=7.85398
    g18: ArcOfCircle CenterX=-16.2837 CenterY=27.25 CenterZ=0 NormalX=0 NormalY=0 NormalZ=1 AngleXU=0 Radius=1.5 StartAngle=4.71485 EndAngle=7.85398
    g19: ArcOfCircle CenterX=-18.2337 CenterY=33 CenterZ=0 NormalX=0 NormalY=0 NormalZ=1 AngleXU=0 Radius=1.5 StartAngle=4.71485 EndAngle=7.85398
    g20: ArcOfCircle CenterX=-11.49 CenterY=21.5 CenterZ=0 NormalX=0 NormalY=0 NormalZ=1 AngleXU=0 Radius=1.5 StartAngle=4.71239 EndAngle=7.85398
    g21: ArcOfCircle CenterX=-1.5 CenterY=4.25 CenterZ=0 NormalX=0 NormalY=0 NormalZ=1 AngleXU=0 Radius=1.5 StartAngle=4.71239 EndAngle=7.85398
    g22: ArcOfCircle CenterX=-1.5 CenterY=10 CenterZ=0 NormalX=0 NormalY=0 NormalZ=1 AngleXU=0 Radius=1.5 StartAngle=4.71239 EndAngle=7.85398
    g23: ArcOfCircle CenterX=-1.5 CenterY=15.75 CenterZ=0 NormalX=0 NormalY=0 NormalZ=1 AngleXU=0 Radius=1.5 StartAngle=4.71239 EndAngle=7.85398
    g24: LineSegment StartX=-49.19 StartY=69.25 StartZ=0 EndX=-1.5 EndY=69.25 EndZ=0
    g25: LineSegment StartX=-49.19 StartY=66.25 StartZ=0 EndX=-1.5 EndY=66.25 EndZ=0
    g26: LineSegment StartX=-49.19 StartY=63.5 StartZ=0 EndX=-1.5 EndY=63.5 EndZ=0
    g27: LineSegment StartX=-49.19 StartY=60.5 StartZ=0 EndX=-1.5 EndY=60.5 EndZ=0
    g28: LineSegment StartX=-49.19 StartY=57.75 StartZ=0 EndX=-1.5 EndY=57.75 EndZ=0
    g29: LineSegment StartX=-49.19 StartY=54.75 StartZ=0 EndX=-1.5 EndY=54.75 EndZ=0
    g30: LineSegment StartX=-49.19 StartY=52 StartZ=0 EndX=-11.49 EndY=52 EndZ=0
    g31: LineSegment StartX=-49.19 StartY=49 StartZ=0 EndX=-11.49 EndY=49 EndZ=0
    g32: LineSegment StartX=-49.19 StartY=46.25 StartZ=0 EndX=-16.28 EndY=46.25 EndZ=0
    g33: LineSegment StartX=-49.19 StartY=43.25 StartZ=0 EndX=-16.28 EndY=43.25 EndZ=0
    g34: LineSegment StartX=-49.19 StartY=40.5 StartZ=0 EndX=-18.2337 EndY=40.5 EndZ=0
    g35: LineSegment StartX=-49.19 StartY=37.5 StartZ=0 EndX=-18.23 EndY=37.5 EndZ=0
    g36: LineSegment StartX=-49.19 StartY=34.5 StartZ=0 EndX=-18.2337 EndY=34.5 EndZ=0
    g37: LineSegment StartX=-49.19 StartY=31.5 StartZ=0 EndX=-18.23 EndY=31.5 EndZ=0
    g38: LineSegment StartX=-49.19 StartY=28.75 StartZ=0 EndX=-16.2837 EndY=28.75 EndZ=0
    g39: LineSegment StartX=-49.19 StartY=25.75 StartZ=0 EndX=-16.28 EndY=25.75 EndZ=0
    g40: LineSegment StartX=-49.19 StartY=23 StartZ=0 EndX=-11.49 EndY=23 EndZ=0
    g41: LineSegment StartX=-49.19 StartY=20 StartZ=0 EndX=-11.49 EndY=20 EndZ=0
    g42: LineSegment StartX=-49.19 StartY=17.25 StartZ=0 EndX=-1.5 EndY=17.25 EndZ=0
    g43: LineSegment StartX=-49.19 StartY=14.25 StartZ=0 EndX=-1.5 EndY=14.25 EndZ=0
    g44: LineSegment StartX=-49.19 StartY=11.5 StartZ=0 EndX=-1.5 EndY=11.5 EndZ=0
    g45: LineSegment StartX=-49.19 StartY=8.5 StartZ=0 EndX=-1.5 EndY=8.5 EndZ=0
    g46: LineSegment StartX=-49.19 StartY=5.75 StartZ=0 EndX=-1.5 EndY=5.75 EndZ=0
    g47: LineSegment StartX=-49.19 StartY=2.75 StartZ=0 EndX=-1.5 EndY=2.75 EndZ=0
  constraints (120):
    c: Vertical(g0)
    c: Distance(g0) = 3
    c: Block(g0)
    c: Vertical(g1)
    c: Distance(g1) = 3
    c: Vertical(g2)
    c: Equal(g0,g2) = 3
    c: Block(g2)
    c: Vertical(g3)
    c: Equal(g1,g3) = 3
    c: Vertical(g4)
    c: Equal(g0,g4) = 3
    c: Block(g4)
    c: Vertical(g5)
    c: Equal(g1,g5) = 3
    c: Vertical(g6)
    c: Equal(g0,g6) = 3
    c: Block(g6)
    c: Vertical(g7)
    c: Equal(g1,g7) = 3
    c: Vertical(g8)
    c: Equal(g0,g8) = 3
    c: Block(g8)
    c: Vertical(g9)
    c: Equal(g1,g9) = 3
    c: Vertical(g10)
    c: Equal(g0,g10) = 3
    c: Block(g10)
    c: Vertical(g11)
    c: Equal(g1,g11) = 3
    c: Block(g12)
    c: Block(g13)
    c: Block(g14)
    c: Block(g15)
    c: Block(g16)
    c: Block(g17)
    c: Block(g18)
    c: Block(g19)
    c: Block(g20)
    c: Block(g21)
    c: Block(g22)
    c: Block(g23)
    c: Block(g11)
    c: Block(g9)
    c: Block(g7)
    c: Block(g5)
    c: Block(g3)
    c: Block(g1)
    c: Coincident(g24,g0)
    c: Coincident(g24,g12)
    c: Horizontal(g24)
    c: Coincident(g25,g0)
    c: Coincident(g25,g12)
    c: Horizontal(g25)
    c: Coincident(g26,g1)
    c: Coincident(g26,g13)
    c: Horizontal(g26)
    c: Coincident(g27,g1)
    c: Coincident(g27,g13)
    c: Horizontal(g27)
    c: Coincident(g28,g2)
    c: Coincident(g28,g14)
    c: Horizontal(g28)
    c: Coincident(g29,g2)
    c: Coincident(g29,g14)
    c: Horizontal(g29)
    c: Coincident(g30,g3)
    c: Coincident(g30,g15)
    c: Horizontal(g30)
    c: Coincident(g31,g3)
    c: Coincident(g31,g15)
    c: Horizontal(g31)
    c: Coincident(g32,g4)
    c: Coincident(g32,g16)
    c: Horizontal(g32)
    c: Coincident(g33,g4)
    c: Coincident(g33,g16)
    c: Horizontal(g33)
    c: Coincident(g34,g5)
    c: Coincident(g34,g17)
    c: Horizontal(g34)
    c: Coincident(g35,g5)
    c: Coincident(g35,g17)
    c: Horizontal(g35)
    c: Coincident(g36,g6)
    c: Coincident(g36,g19)
    c: Horizontal(g36)
    c: Coincident(g37,g6)
    c: Coincident(g37,g19)
    c: Horizontal(g37)
    c: Coincident(g38,g7)
    c: Coincident(g38,g18)
    c: Horizontal(g38)
    c: Coincident(g39,g7)
    c: Coincident(g39,g18)
    c: Horizontal(g39)
    c: Coincident(g40,g8)
    c: Coincident(g40,g20)
    c: Horizontal(g40)
    c: Coincident(g41,g8)
    c: Coincident(g41,g20)
    c: Horizontal(g41)
    c: Coincident(g42,g9)
    c: Coincident(g42,g23)
    c: Horizontal(g42)
    c: Coincident(g43,g9)
    c: Coincident(g43,g23)
    c: Horizontal(g43)
    c: Coincident(g44,g10)
    c: Coincident(g44,g22)
    c: Horizontal(g44)
    c: Coincident(g45,g10)
    c: Coincident(g45,g22)
    c: Horizontal(g45)
    c: Coincident(g46,g11)
    c: Coincident(g46,g21)
    c: Horizontal(g46)
    c: Coincident(g47,g11)
    c: Coincident(g47,g21)
    c: Horizontal(g47)
FEATURE [Sketcher::SketchObject] Sketch031
  FullyConstrained = true
  Placement = pos=(117,19,0) rot=(0.57735,0.57735,0.57735;2.0944rad)
  sketch-geometry (24):
    g0: ArcOfCircle CenterX=-49.19 CenterY=67.75 CenterZ=0 NormalX=0 NormalY=0 NormalZ=1 AngleXU=0 Radius=1.5 StartAngle=1.5708 EndAngle=4.71239
    g1: ArcOfCircle CenterX=-49.19 CenterY=62 CenterZ=0 NormalX=0 NormalY=0 NormalZ=1 AngleXU=0 Radius=1.5 StartAngle=1.5708 EndAngle=4.71239
    g2: ArcOfCircle CenterX=-49.19 CenterY=56.25 CenterZ=0 NormalX=0 NormalY=0 NormalZ=1 AngleXU=0 Radius=1.5 StartAngle=1.5708 EndAngle=4.71239
    g3: ArcOfCircle CenterX=-49.19 CenterY=50.5 CenterZ=0 NormalX=0 NormalY=0 NormalZ=1 AngleXU=0 Radius=1.5 StartAngle=1.5708 EndAngle=4.71239
    g4: ArcOfCircle CenterX=-49.19 CenterY=44.75 CenterZ=0 NormalX=0 NormalY=0 NormalZ=1 AngleXU=0 Radius=1.5 StartAngle=1.5708 EndAngle=4.71239
    g5: ArcOfCircle CenterX=-49.19 CenterY=39 CenterZ=0 NormalX=0 NormalY=0 NormalZ=1 AngleXU=0 Radius=1.5 StartAngle=1.5708 EndAngle=4.71239
    g6: ArcOfCircle CenterX=-49.19 CenterY=33 CenterZ=0 NormalX=0 NormalY=0 NormalZ=1 AngleXU=0 Radius=1.5 StartAngle=1.5708 EndAngle=4.71239
    g7: ArcOfCircle CenterX=-49.19 CenterY=27.25 CenterZ=0 NormalX=0 NormalY=0 NormalZ=1 AngleXU=0 Radius=1.5 StartAngle=1.5708 EndAngle=4.71239
    g8: ArcOfCircle CenterX=-49.19 CenterY=21.5 CenterZ=0 NormalX=0 NormalY=0 NormalZ=1 AngleXU=0 Radius=1.5 StartAngle=1.5708 EndAngle=4.71239
    g9: ArcOfCircle CenterX=-49.19 CenterY=15.75 CenterZ=0 NormalX=0 NormalY=0 NormalZ=1 AngleXU=0 Radius=1.5 StartAngle=1.5708 EndAngle=4.71239
    g10: ArcOfCircle CenterX=-49.19 CenterY=10 CenterZ=0 NormalX=0 NormalY=0 NormalZ=1 AngleXU=0 Radius=1.5 StartAngle=1.5708 EndAngle=4.71239
    g11: ArcOfCircle CenterX=-49.19 CenterY=4.25 CenterZ=0 NormalX=0 NormalY=0 NormalZ=1 AngleXU=0 Radius=1.5 StartAngle=1.5708 EndAngle=4.71239
    g12: LineSegment StartX=-49.19 StartY=69.25 StartZ=0 EndX=-49.19 EndY=66.25 EndZ=0
    g13: LineSegment StartX=-49.19 StartY=63.5 StartZ=0 EndX=-49.19 EndY=60.5 EndZ=0
    g14: LineSegment StartX=-49.19 StartY=57.75 StartZ=0 EndX=-49.19 EndY=54.75 EndZ=0
    g15: LineSegment StartX=-49.19 StartY=52 StartZ=0 EndX=-49.19 EndY=49 EndZ=0
    g16: LineSegment StartX=-49.19 StartY=46.25 StartZ=0 EndX=-49.19 EndY=43.25 EndZ=0
    g17: LineSegment StartX=-49.19 StartY=40.5 StartZ=0 EndX=-49.19 EndY=37.5 EndZ=0
    g18: LineSegment StartX=-49.19 StartY=34.5 StartZ=0 EndX=-49.19 EndY=31.5 EndZ=0
    g19: LineSegment StartX=-49.19 StartY=28.75 StartZ=0 EndX=-49.19 EndY=25.75 EndZ=0
    g20: LineSegment StartX=-49.19 StartY=23 StartZ=0 EndX=-49.19 EndY=20 EndZ=0
    g21: LineSegment StartX=-49.19 StartY=17.25 StartZ=0 EndX=-49.19 EndY=14.25 EndZ=0
    g22: LineSegment StartX=-49.19 StartY=11.5 StartZ=0 EndX=-49.19 EndY=8.5 EndZ=0
    g23: LineSegment StartX=-49.19 StartY=5.75 StartZ=0 EndX=-49.19 EndY=2.75 EndZ=0
  constraints (48):
    c: Block(g0)
    c: Block(g1)
    c: Block(g2)
    c: Block(g3)
    c: Block(g4)
    c: Block(g5)
    c: Block(g6)
    c: Block(g7)
    c: Block(g8)
    c: Block(g9)
    c: Block(g10)
    c: Block(g11)
    c: Coincident(g12,g0)
    c: Coincident(g12,g0)
    c: Vertical(g12)
    c: Vertical(g13)
    c: Coincident(g13,g1)
    c: Vertical(g14)
    c: Coincident(g14,g2)
    c: Vertical(g15)
    c: Coincident(g15,g3)
    c: Vertical(g16)
    c: Coincident(g16,g4)
    c: Vertical(g17)
    c: Coincident(g17,g5)
    c: Vertical(g18)
    c: Coincident(g18,g6)
    c: Vertical(g19)
    c: Coincident(g19,g7)
    c: Vertical(g20)
    c: Coincident(g20,g8)
    c: Vertical(g21)
    c: Coincident(g21,g9)
    c: Vertical(g22)
    c: Coincident(g22,g10)
    c: Vertical(g23)
    c: Coincident(g23,g11)
    c: Block(g23)
    c: Block(g22)
    c: Block(g21)
    c: Block(g20)
    c: Block(g13)
    c: Block(g14)
    c: Block(g15)
    c: Block(g16)
    c: Block(g17)
    c: Block(g18)
    c: Block(g19)
FEATURE [Part::Extrusion] Extrude022
  Base = -> Sketch030
  Dir = (1,-2e-16,2e-16)
  DirMode = 2
  FaceMakerClass = Part::FaceMakerBullseye
  LengthFwd = 19
  LengthRev = 0
  Placement = pos=(-19,0,0) rot=(0,0,1;0rad)
  Solid = true
  Symmetric = false
FEATURE [Part::Fillet] Fillet022
  Base = -> Extrude022
  Edges = 24 edges r=1.49: [Edge6,Edge11,Edge18,Edge23,Edge30,Edge35,Edge42,Edge47,Edge54,Edge59,Edge66,Edge71,Edge78,Edge83,Edge90,Edge95,Edge102,Edge107,Edge114,Edge119,Edge126,Edge131,Edge138,Edge143]
FEATURE [Part::Cut] Cut020  label="top010"
  Base = -> Cut019
  Tool = -> Fillet022
FEATURE [Sketcher::SketchObject] Sketch032
  FullyConstrained = true
  Placement = pos=(117,19,0) rot=(0.57735,0.57735,0.57735;2.0944rad)
  sketch-geometry (48):
    g0: LineSegment StartX=-49.19 StartY=69.25 StartZ=0 EndX=-49.19 EndY=66.25 EndZ=0
    g1: LineSegment StartX=-49.19 StartY=63.5 StartZ=0 EndX=-49.19 EndY=60.5 EndZ=0
    g2: LineSegment StartX=-49.19 StartY=57.75 StartZ=0 EndX=-49.19 EndY=54.75 EndZ=0
    g3: LineSegment StartX=-49.19 StartY=52 StartZ=0 EndX=-49.19 EndY=49 EndZ=0
    g4: LineSegment StartX=-49.19 StartY=46.25 StartZ=0 EndX=-49.19 EndY=43.25 EndZ=0
    g5: LineSegment StartX=-49.19 StartY=40.5 StartZ=0 EndX=-49.19 EndY=37.5 EndZ=0
    g6: LineSegment StartX=-49.19 StartY=34.5 StartZ=0 EndX=-49.19 EndY=31.5 EndZ=0
    g7: LineSegment StartX=-49.19 StartY=28.75 StartZ=0 EndX=-49.19 EndY=25.75 EndZ=0
    g8: LineSegment StartX=-49.19 StartY=23 StartZ=0 EndX=-49.19 EndY=20 EndZ=0
    g9: LineSegment StartX=-49.19 StartY=17.25 StartZ=0 EndX=-49.19 EndY=14.25 EndZ=0
    g10: LineSegment StartX=-49.19 StartY=11.5 StartZ=0 EndX=-49.19 EndY=8.5 EndZ=0
    g11: LineSegment StartX=-49.19 StartY=5.75 StartZ=0 EndX=-49.19 EndY=2.75 EndZ=0
    g12: ArcOfCircle CenterX=-1.5 CenterY=67.75 CenterZ=0 NormalX=0 NormalY=0 NormalZ=1 AngleXU=0 Radius=1.5 StartAngle=4.71239 EndAngle=7.85398
    g13: ArcOfCircle CenterX=-1.5 CenterY=62 CenterZ=0 NormalX=0 NormalY=0 NormalZ=1 AngleXU=0 Radius=1.5 StartAngle=4.71239 EndAngle=7.85398
    g14: ArcOfCircle CenterX=-1.5 CenterY=56.25 CenterZ=0 NormalX=0 NormalY=0 NormalZ=1 AngleXU=0 Radius=1.5 StartAngle=4.71239 EndAngle=7.85398
    g15: ArcOfCircle CenterX=-11.49 CenterY=50.5 CenterZ=0 NormalX=0 NormalY=0 NormalZ=1 AngleXU=0 Radius=1.5 StartAngle=4.71239 EndAngle=7.85398
    g16: ArcOfCircle CenterX=-16.28 CenterY=44.75 CenterZ=0 NormalX=0 NormalY=0 NormalZ=1 AngleXU=0 Radius=1.5 StartAngle=4.71239 EndAngle=7.85398
    g17: ArcOfCircle CenterX=-18.2337 CenterY=39 CenterZ=0 NormalX=0 NormalY=0 NormalZ=1 AngleXU=0 Radius=1.5 StartAngle=4.71485 EndAngle=7.85398
    g18: ArcOfCircle CenterX=-16.2837 CenterY=27.25 CenterZ=0 NormalX=0 NormalY=0 NormalZ=1 AngleXU=0 Radius=1.5 StartAngle=4.71485 EndAngle=7.85398
    g19: ArcOfCircle CenterX=-18.2337 CenterY=33 CenterZ=0 NormalX=0 NormalY=0 NormalZ=1 AngleXU=0 Radius=1.5 StartAngle=4.71485 EndAngle=7.85398
    g20: ArcOfCircle CenterX=-11.49 CenterY=21.5 CenterZ=0 NormalX=0 NormalY=0 NormalZ=1 AngleXU=0 Radius=1.5 StartAngle=4.71239 EndAngle=7.85398
    g21: ArcOfCircle CenterX=-1.5 CenterY=4.25 CenterZ=0 NormalX=0 NormalY=0 NormalZ=1 AngleXU=0 Radius=1.5 StartAngle=4.71239 EndAngle=7.85398
    g22: ArcOfCircle CenterX=-1.5 CenterY=10 CenterZ=0 NormalX=0 NormalY=0 NormalZ=1 AngleXU=0 Radius=1.5 StartAngle=4.71239 EndAngle=7.85398
    g23: ArcOfCircle CenterX=-1.5 CenterY=15.75 CenterZ=0 NormalX=0 NormalY=0 NormalZ=1 AngleXU=0 Radius=1.5 StartAngle=4.71239 EndAngle=7.85398
    g24: LineSegment StartX=-49.19 StartY=69.25 StartZ=0 EndX=-1.5 EndY=69.25 EndZ=0
    g25: LineSegment StartX=-49.19 StartY=66.25 StartZ=0 EndX=-1.5 EndY=66.25 EndZ=0
    g26: LineSegment StartX=-49.19 StartY=63.5 StartZ=0 EndX=-1.5 EndY=63.5 EndZ=0
    g27: LineSegment StartX=-49.19 StartY=60.5 StartZ=0 EndX=-1.5 EndY=60.5 EndZ=0
    g28: LineSegment StartX=-49.19 StartY=57.75 StartZ=0 EndX=-1.5 EndY=57.75 EndZ=0
    g29: LineSegment StartX=-49.19 StartY=54.75 StartZ=0 EndX=-1.5 EndY=54.75 EndZ=0
    g30: LineSegment StartX=-49.19 StartY=52 StartZ=0 EndX=-11.49 EndY=52 EndZ=0
    g31: LineSegment StartX=-49.19 StartY=49 StartZ=0 EndX=-11.49 EndY=49 EndZ=0
    g32: LineSegment StartX=-49.19 StartY=46.25 StartZ=0 EndX=-16.28 EndY=46.25 EndZ=0
    g33: LineSegment StartX=-49.19 StartY=43.25 StartZ=0 EndX=-16.28 EndY=43.25 EndZ=0
    g34: LineSegment StartX=-49.19 StartY=40.5 StartZ=0 EndX=-18.2337 EndY=40.5 EndZ=0
    g35: LineSegment StartX=-49.19 StartY=37.5 StartZ=0 EndX=-18.23 EndY=37.5 EndZ=0
    g36: LineSegment StartX=-49.19 StartY=34.5 StartZ=0 EndX=-18.2337 EndY=34.5 EndZ=0
    g37: LineSegment StartX=-49.19 StartY=31.5 StartZ=0 EndX=-18.23 EndY=31.5 EndZ=0
    g38: LineSegment StartX=-49.19 StartY=28.75 StartZ=0 EndX=-16.2837 EndY=28.75 EndZ=0
    g39: LineSegment StartX=-49.19 StartY=25.75 StartZ=0 EndX=-16.28 EndY=25.75 EndZ=0
    g40: LineSegment StartX=-49.19 StartY=23 StartZ=0 EndX=-11.49 EndY=23 EndZ=0
    g41: LineSegment StartX=-49.19 StartY=20 StartZ=0 EndX=-11.49 EndY=20 EndZ=0
    g42: LineSegment StartX=-49.19 StartY=17.25 StartZ=0 EndX=-1.5 EndY=17.25 EndZ=0
    g43: LineSegment StartX=-49.19 StartY=14.25 StartZ=0 EndX=-1.5 EndY=14.25 EndZ=0
    g44: LineSegment StartX=-49.19 StartY=11.5 StartZ=0 EndX=-1.5 EndY=11.5 EndZ=0
    g45: LineSegment StartX=-49.19 StartY=8.5 StartZ=0 EndX=-1.5 EndY=8.5 EndZ=0
    g46: LineSegment StartX=-49.19 StartY=5.75 StartZ=0 EndX=-1.5 EndY=5.75 EndZ=0
    g47: LineSegment StartX=-49.19 StartY=2.75 StartZ=0 EndX=-1.5 EndY=2.75 EndZ=0
  constraints (120):
    c: Vertical(g0)
    c: Distance(g0) = 3
    c: Block(g0)
    c: Vertical(g1)
    c: Distance(g1) = 3
    c: Vertical(g2)
    c: Equal(g0,g2) = 3
    c: Block(g2)
    c: Vertical(g3)
    c: Equal(g1,g3) = 3
    c: Vertical(g4)
    c: Equal(g0,g4) = 3
    c: Block(g4)
    c: Vertical(g5)
    c: Equal(g1,g5) = 3
    c: Vertical(g6)
    c: Equal(g0,g6) = 3
    c: Block(g6)
    c: Vertical(g7)
    c: Equal(g1,g7) = 3
    c: Vertical(g8)
    c: Equal(g0,g8) = 3
    c: Block(g8)
    c: Vertical(g9)
    c: Equal(g1,g9) = 3
    c: Vertical(g10)
    c: Equal(g0,g10) = 3
    c: Block(g10)
    c: Vertical(g11)
    c: Equal(g1,g11) = 3
    c: Block(g12)
    c: Block(g13)
    c: Block(g14)
    c: Block(g15)
    c: Block(g16)
    c: Block(g17)
    c: Block(g18)
    c: Block(g19)
    c: Block(g20)
    c: Block(g21)
    c: Block(g22)
    c: Block(g23)
    c: Block(g11)
    c: Block(g9)
    c: Block(g7)
    c: Block(g5)
    c: Block(g3)
    c: Block(g1)
    c: Coincident(g24,g0)
    c: Coincident(g24,g12)
    c: Horizontal(g24)
    c: Coincident(g25,g0)
    c: Coincident(g25,g12)
    c: Horizontal(g25)
    c: Coincident(g26,g1)
    c: Coincident(g26,g13)
    c: Horizontal(g26)
    c: Coincident(g27,g1)
    c: Coincident(g27,g13)
    c: Horizontal(g27)
    c: Coincident(g28,g2)
    c: Coincident(g28,g14)
    c: Horizontal(g28)
    c: Coincident(g29,g2)
    c: Coincident(g29,g14)
    c: Horizontal(g29)
    c: Coincident(g30,g3)
    c: Coincident(g30,g15)
    c: Horizontal(g30)
    c: Coincident(g31,g3)
    c: Coincident(g31,g15)
    c: Horizontal(g31)
    c: Coincident(g32,g4)
    c: Coincident(g32,g16)
    c: Horizontal(g32)
    c: Coincident(g33,g4)
    c: Coincident(g33,g16)
    c: Horizontal(g33)
    c: Coincident(g34,g5)
    c: Coincident(g34,g17)
    c: Horizontal(g34)
    c: Coincident(g35,g5)
    c: Coincident(g35,g17)
    c: Horizontal(g35)
    c: Coincident(g36,g6)
    c: Coincident(g36,g19)
    c: Horizontal(g36)
    c: Coincident(g37,g6)
    c: Coincident(g37,g19)
    c: Horizontal(g37)
    c: Coincident(g38,g7)
    c: Coincident(g38,g18)
    c: Horizontal(g38)
    c: Coincident(g39,g7)
    c: Coincident(g39,g18)
    c: Horizontal(g39)
    c: Coincident(g40,g8)
    c: Coincident(g40,g20)
    c: Horizontal(g40)
    c: Coincident(g41,g8)
    c: Coincident(g41,g20)
    c: Horizontal(g41)
    c: Coincident(g42,g9)
    c: Coincident(g42,g23)
    c: Horizontal(g42)
    c: Coincident(g43,g9)
    c: Coincident(g43,g23)
    c: Horizontal(g43)
    c: Coincident(g44,g10)
    c: Coincident(g44,g22)
    c: Horizontal(g44)
    c: Coincident(g45,g10)
    c: Coincident(g45,g22)
    c: Horizontal(g45)
    c: Coincident(g46,g11)
    c: Coincident(g46,g21)
    c: Horizontal(g46)
    c: Coincident(g47,g11)
    c: Coincident(g47,g21)
    c: Horizontal(g47)
FEATURE [Part::Extrusion] Extrude023
  Base = -> Sketch032
  Dir = (1,-2e-16,2e-16)
  DirMode = 2
  FaceMakerClass = Part::FaceMakerBullseye
  LengthFwd = 19
  LengthRev = 0
  Placement = pos=(-19,0,0) rot=(0,0,1;0rad)
  Solid = true
  Symmetric = false
FEATURE [Part::Fillet] Fillet023
  Base = -> Extrude023
  Edges = <same value as first occurrence — deduplicated (x6 in doc)>
  Placement = pos=(0,0.05,0) rot=(0,0,1;0rad)
FEATURE [Part::Cut] Cut014  label="bottom003"
  Base = -> Cut007
  Tool = -> Fusion047
FEATURE [Part::Cut] Cut021  label="bottom004"
  Base = -> Cut014
  Tool = -> Fillet023
FEATURE [Sketcher::SketchObject] Sketch033
  FullyConstrained = true
  Placement = pos=(117,19,0) rot=(0.57735,0.57735,0.57735;2.0944rad)
  sketch-geometry (8):
    g0: LineSegment StartX=-49.19 StartY=69.25 StartZ=0 EndX=-49.19 EndY=66.25 EndZ=0
    g1: LineSegment StartX=-49.19 StartY=5.75 StartZ=0 EndX=-49.19 EndY=2.75 EndZ=0
    g2: ArcOfCircle CenterX=-1.5 CenterY=67.75 CenterZ=0 NormalX=0 NormalY=0 NormalZ=1 AngleXU=0 Radius=1.5 StartAngle=4.71239 EndAngle=7.85398
    g3: ArcOfCircle CenterX=-1.5 CenterY=4.25 CenterZ=0 NormalX=0 NormalY=0 NormalZ=1 AngleXU=0 Radius=1.5 StartAngle=4.71239 EndAngle=7.85398
    g4: LineSegment StartX=-49.19 StartY=69.25 StartZ=0 EndX=-1.5 EndY=69.25 EndZ=0
    g5: LineSegment StartX=-49.19 StartY=66.25 StartZ=0 EndX=-1.5 EndY=66.25 EndZ=0
    g6: LineSegment StartX=-49.19 StartY=5.75 StartZ=0 EndX=-1.5 EndY=5.75 EndZ=0
    g7: LineSegment StartX=-49.19 StartY=2.75 StartZ=0 EndX=-1.5 EndY=2.75 EndZ=0
  constraints (19):
    c: Vertical(g0)
    c: Distance(g0) = 3
    c: Block(g0)
    c: Vertical(g1)
    c: Block(g2)
    c: Block(g3)
    c: Block(g1)
    c: Coincident(g4,g0)
    c: Coincident(g4,g2)
    c: Horizontal(g4)
    c: Coincident(g5,g0)
    c: Coincident(g5,g2)
    c: Horizontal(g5)
    c: Coincident(g6,g1)
    c: Coincident(g6,g3)
    c: Horizontal(g6)
    c: Coincident(g7,g1)
    c: Coincident(g7,g3)
    c: Horizontal(g7)
FEATURE [Sketcher::SketchObject] Sketch034
  FullyConstrained = true
  Placement = pos=(117,19,0) rot=(0.57735,0.57735,0.57735;2.0944rad)
  sketch-geometry (8):
    g0: LineSegment StartX=-49.19 StartY=63.5 StartZ=0 EndX=-49.19 EndY=60.5 EndZ=0
    g1: LineSegment StartX=-49.19 StartY=11.5 StartZ=0 EndX=-49.19 EndY=8.5 EndZ=0
    g2: ArcOfCircle CenterX=-1.5 CenterY=62 CenterZ=0 NormalX=0 NormalY=0 NormalZ=1 AngleXU=0 Radius=1.5 StartAngle=4.71239 EndAngle=7.85398
    g3: ArcOfCircle CenterX=-1.5 CenterY=10 CenterZ=0 NormalX=0 NormalY=0 NormalZ=1 AngleXU=0 Radius=1.5 StartAngle=4.71239 EndAngle=7.85398
    g4: LineSegment StartX=-49.19 StartY=63.5 StartZ=0 EndX=-1.5 EndY=63.5 EndZ=0
    g5: LineSegment StartX=-49.19 StartY=60.5 StartZ=0 EndX=-1.5 EndY=60.5 EndZ=0
    g6: LineSegment StartX=-49.19 StartY=11.5 StartZ=0 EndX=-1.5 EndY=11.5 EndZ=0
    g7: LineSegment StartX=-49.19 StartY=8.5 StartZ=0 EndX=-1.5 EndY=8.5 EndZ=0
  constraints (19):
    c: Vertical(g0)
    c: Distance(g0) = 3
    c: Vertical(g1)
    c: Block(g1)
    c: Block(g2)
    c: Block(g3)
    c: Block(g0)
    c: Coincident(g4,g0)
    c: Coincident(g4,g2)
    c: Horizontal(g4)
    c: Coincident(g5,g0)
    c: Coincident(g5,g2)
    c: Horizontal(g5)
    c: Coincident(g6,g1)
    c: Coincident(g6,g3)
    c: Horizontal(g6)
    c: Coincident(g7,g1)
    c: Coincident(g7,g3)
    c: Horizontal(g7)
FEATURE [Part::Extrusion] Extrude024
  Base = -> Sketch033
  Dir = (1,0,0)
  DirMode = 2
  FaceMakerClass = Part::FaceMakerBullseye
  LengthFwd = 10
  LengthRev = 0
  Solid = true
  Symmetric = false
FEATURE [Part::Extrusion] Extrude025
  Base = -> Sketch034
  Dir = (1,0,0)
  DirMode = 2
  FaceMakerClass = Part::FaceMakerBullseye
  LengthFwd = 10
  LengthRev = 0
  Solid = true
  Symmetric = false
FEATURE [Part::Fillet] Fillet024  label="removeFromtMoreFrontCaseScrewRetainers"
  Base = -> Extrude024
  Edges = 4 edges r=1.49: [Edge6,Edge11,Edge18,Edge23]
  Placement = pos=(-11,0,0) rot=(0,0,1;0rad)
FEATURE [Part::Fillet] Fillet025  label="removeFromtMoreFrontCaseScrewRetainers001"
  Base = -> Extrude025
  Edges = 4 edges r=1.49: [Edge6,Edge11,Edge18,Edge23]
  Placement = pos=(-19,0,0) rot=(0,0,1;0rad)
FEATURE [Part::Cut] Cut022
  Base = -> Cut015
  Tool = -> Fillet025
FEATURE [Part::Cut] Cut023  label="screwRetainers"
  Base = -> Cut022
  Tool = -> Fillet024
FEATURE [Part::MultiFuse] Fusion056  label="bottom005"
  Shapes = -> [Fusion044,Cut021]
FEATURE [Part::MultiFuse] Fusion057  label="casePillars001"
  Shapes = -> [Cut016,Fusion052]
FEATURE [Part::MultiFuse] Fusion058  label="bottom006"
  Shapes = -> [Fusion056,Cut023]
FEATURE [Part::MultiFuse] Fusion059  label="bottom007"
  Shapes = -> [Fusion058,Fillet005]
FEATURE [Part::MultiFuse] Fusion060  label="bottom008"
  Shapes = -> [Fusion059,Fusion]
FEATURE [Part::MultiFuse] Fusion061  label="top011"
  Shapes = -> [Cut006,Cut020]
FEATURE [Part::MultiFuse] Fusion062  label="top012"
  Shapes = -> [Fusion057,Fusion061]
FEATURE [Sketcher::SketchObject] Sketch035  label="topSketch007"
  FullyConstrained = true
  sketch-geometry (6):
    g0: LineSegment StartX=19 StartY=38 StartZ=0 EndX=117 EndY=38 EndZ=0
    g1: ArcOfCircle CenterX=19 CenterY=19 CenterZ=0 NormalX=0 NormalY=0 NormalZ=1 AngleXU=0 Radius=19 StartAngle=1.5708 EndAngle=3.14159
    g2: LineSegment StartX=117 StartY=38 StartZ=0 EndX=117 EndY=19 EndZ=0
    g3: LineSegment StartX=98 StartY=1.0161e-12 StartZ=0 EndX=5.22862e-06 EndY=1.0161e-12 EndZ=0
    g4: LineSegment StartX=5.22862e-06 StartY=19 StartZ=0 EndX=5.22862e-06 EndY=1.0161e-12 EndZ=0
    g5: ArcOfCircle CenterX=98 CenterY=19 CenterZ=0 NormalX=0 NormalY=0 NormalZ=1 AngleXU=0 Radius=19 StartAngle=4.71239 EndAngle=6.28319
  constraints (16):
    c: Horizontal(g0)
    c: Distance(g0) = 98
    c: Coincident(g1,g0)
    c: Block(g1)
    c: Coincident(g2,g0)
    c: Vertical(g2)
    c: Distance(g2) = 19
    c: Horizontal(g3)
    c: Coincident(g4,g1)
    c: Vertical(g4)
    c: Coincident(g3,g4)
    c: Block(g3)
    c: Coincident(g5,g2)
    c: Coincident(g5,g3)
    c: Block(g0)
    c: Block(g5)
FEATURE [Part::Extrusion] Extrude026  label="sideA001"
  Base = -> Sketch035
  Dir = (0,0,1)
  DirMode = 2
  FaceMakerClass = Part::FaceMakerBullseye
  LengthFwd = 3
  LengthRev = 0
  Placement = pos=(0,0,-2.7) rot=(0,0,1;0rad)
  Solid = true
  Symmetric = false
FEATURE [Sketcher::SketchObject] Sketch036  label="topSketch008"
  FullyConstrained = true
  sketch-geometry (6):
    g0: LineSegment StartX=19 StartY=38 StartZ=0 EndX=117 EndY=38 EndZ=0
    g1: ArcOfCircle CenterX=19 CenterY=19 CenterZ=0 NormalX=0 NormalY=0 NormalZ=1 AngleXU=0 Radius=19 StartAngle=1.5708 EndAngle=3.14159
    g2: LineSegment StartX=117 StartY=38 StartZ=0 EndX=117 EndY=19 EndZ=0
    g3: LineSegment StartX=98 StartY=1.0161e-12 StartZ=0 EndX=5.22862e-06 EndY=1.0161e-12 EndZ=0
    g4: LineSegment StartX=5.22862e-06 StartY=19 StartZ=0 EndX=5.22862e-06 EndY=1.0161e-12 EndZ=0
    g5: ArcOfCircle CenterX=98 CenterY=19 CenterZ=0 NormalX=0 NormalY=0 NormalZ=1 AngleXU=0 Radius=19 StartAngle=4.71239 EndAngle=6.28319
  constraints (16):
    c: Horizontal(g0)
    c: Distance(g0) = 98
    c: Coincident(g1,g0)
    c: Block(g1)
    c: Coincident(g2,g0)
    c: Vertical(g2)
    c: Distance(g2) = 19
    c: Horizontal(g3)
    c: Coincident(g4,g1)
    c: Vertical(g4)
    c: Coincident(g3,g4)
    c: Block(g3)
    c: Coincident(g5,g2)
    c: Coincident(g5,g3)
    c: Block(g0)
    c: Block(g5)
FEATURE [Part::Extrusion] Extrude027  label="sideB001"
  Base = -> Sketch036
  Dir = (0,0,1)
  DirMode = 2
  FaceMakerClass = Part::FaceMakerBullseye
  LengthFwd = 3
  LengthRev = 0
  Placement = pos=(0,0,71.7) rot=(0,0,1;0rad)
  Solid = true
  Symmetric = false
FEATURE [Part::MultiFuse] Fusion064  label="removeFromBottom"
  Shapes = -> [Extrude026,Extrude027]
FEATURE [Part::Cut] Cut024  label="bottom009"
  Base = -> Fusion060
  Tool = -> Fusion064
FEATURE [Sketcher::SketchObject] Sketch037  label="topSketch009"
  FullyConstrained = true
  sketch-geometry (6):
    g0: ArcOfCircle CenterX=19 CenterY=19 CenterZ=0 NormalX=0 NormalY=0 NormalZ=1 AngleXU=0 Radius=19 StartAngle=1.5708 EndAngle=3.14159
    g1: LineSegment StartX=5.22862e-06 StartY=19 StartZ=0 EndX=5.22862e-06 EndY=1.19904e-11 EndZ=0
    g2: LineSegment StartX=19 StartY=38 StartZ=0 EndX=124 EndY=38 EndZ=0
    g3: LineSegment StartX=5.22862e-06 StartY=1.19904e-11 StartZ=0 EndX=105 EndY=1.19904e-11 EndZ=0
    g4: ArcOfCircle CenterX=105 CenterY=19 CenterZ=0 NormalX=0 NormalY=0 NormalZ=1 AngleXU=0 Radius=19 StartAngle=4.71239 EndAngle=6.28319
    g5: LineSegment StartX=124 StartY=38 StartZ=0 EndX=124 EndY=19 EndZ=0
  constraints (16):
    c: Block(g0)
    c: Coincident(g1,g0)
    c: Vertical(g1)
    c: Horizontal(g2)
    c: Distance(g2) = 105
    c: Coincident(g2,g0)
    c: Distance(g1) = 19
    c: Coincident(g3,g1)
    c: Horizontal(g3)
    c: Distance(g3) = 105
    c: Block(g4)
    c: Coincident(g4,g3)
    c: Coincident(g5,g2)
    c: Coincident(g5,g4)
    c: Vertical(g5)
    c: Distance(g5) = 19
FEATURE [Part::Extrusion] Extrude028  label="sideB"
  Base = -> Sketch037
  Dir = (0,0,1)
  DirMode = 2
  FaceMakerClass = Part::FaceMakerBullseye
  LengthFwd = 3
  LengthRev = 0
  Placement = pos=(0,0,72) rot=(0,0,1;0rad)
  Solid = true
  Symmetric = false
FEATURE [Sketcher::SketchObject] Sketch038  label="topSketch010"
  FullyConstrained = true
  sketch-geometry (22):
    g0: LineSegment StartX=5.21097e-06 StartY=3 StartZ=0 EndX=5.21097e-06 EndY=19 EndZ=0
    g1: ArcOfCircle CenterX=19 CenterY=19 CenterZ=0 NormalX=0 NormalY=0 NormalZ=1 AngleXU=0 Radius=19 StartAngle=1.5708 EndAngle=3.14159
    g2: ArcOfCircle CenterX=19 CenterY=19 CenterZ=0 NormalX=0 NormalY=0 NormalZ=1 AngleXU=0 Radius=16 StartAngle=1.5708 EndAngle=3.14159
    g3: LineSegment StartX=114 StartY=35 StartZ=0 EndX=19 EndY=35 EndZ=0
    g4: LineSegment StartX=5.21097e-06 StartY=3 StartZ=0 EndX=5.21097e-06 EndY=0 EndZ=0
    g5: LineSegment StartX=3 StartY=0 StartZ=0 EndX=5.21097e-06 EndY=0 EndZ=0
    g6: LineSegment StartX=3 StartY=19 StartZ=0 EndX=3 EndY=0 EndZ=0
    g7: LineSegment StartX=19 StartY=38 StartZ=0 EndX=124 EndY=38 EndZ=0
    g8: Circle CenterX=119 CenterY=35 CenterZ=0 NormalX=0 NormalY=0 NormalZ=1 AngleXU=0 Radius=1
    g9: Circle CenterX=121 CenterY=35 CenterZ=0 NormalX=0 NormalY=0 NormalZ=1 AngleXU=0 Radius=1
    g10: Circle CenterX=121 CenterY=33 CenterZ=0 NormalX=0 NormalY=0 NormalZ=1 AngleXU=0 Radius=1
    g11: BSplineCurve PolesCount=3 KnotsCount=2 Degree=2 IsPeriodic=0
    g12: GeomPoint X=119 Y=35 Z=0
    g13: GeomPoint X=121 Y=33 Z=0
    g14: LineSegment StartX=119 StartY=35 StartZ=0 EndX=114 EndY=35 EndZ=0
    g15: ArcOfCircle CenterX=105 CenterY=19 CenterZ=0 NormalX=0 NormalY=0 NormalZ=1 AngleXU=0 Radius=16 StartAngle=5.60905 EndAngle=6.28319
    g16: LineSegment StartX=121 StartY=33 StartZ=0 EndX=121 EndY=19 EndZ=0
    g17: LineSegment StartX=117.5 StartY=9.01251 StartZ=0 EndX=121.163 EndY=9.0125 EndZ=0
    g18: ArcOfCircle CenterX=105 CenterY=19 CenterZ=0 NormalX=0 NormalY=0 NormalZ=1 AngleXU=0 Radius=20.6155 StartAngle=5.7297 EndAngle=6.28319
    g19: LineSegment StartX=121.163 StartY=9.0125 StartZ=0 EndX=122.538 EndY=8.16329 EndZ=0
    g20: LineSegment StartX=124 StartY=38 StartZ=0 EndX=125.616 EndY=38 EndZ=0
    g21: LineSegment StartX=125.616 StartY=19 StartZ=0 EndX=125.616 EndY=38 EndZ=0
  constraints (49):
    c: Vertical(g0)
    c: Block(g0)
    c: Coincident(g1,g0)
    c: Block(g1)
    c: Coincident(g2,g1)
    c: Block(g2)
    c: Coincident(g3,g2)
    c: Horizontal(g3)
    c: Tangent(g3,g2)
    c: Coincident(g4,g0)
    c: Distance(g4) = 3
    c: Vertical(g4)
    c: Coincident(g5,g4)
    c: Horizontal(g5)
    c: Coincident(g6,g2)
    c: Coincident(g6,g5)
    c: Vertical(g6)
    c: Horizontal(g7)
    c: Distance(g7) = 105
    c: Coincident(g7,g1)
    c: Block(g3)
    c: Weight(g8) = 1
    c: Equal(g8,g9)
    c: Equal(g8,g10)
    c: InternalAlignment(g8,g11)
    c: InternalAlignment(g9,g11)
    c: InternalAlignment(g10,g11)
    c: InternalAlignment(g12,g11)
    c: InternalAlignment(g13,g11)
    c: Block(g11)
    c: Coincident(g14,g11)
    c: Coincident(g14,g3)
    c: Horizontal(g14)
    c: Block(g15)
    c: Coincident(g16,g11)
    c: Coincident(g16,g15)
    c: Vertical(g16)
    c: Distance(g16) = 14
    c: Coincident(g17,g15)
    c: Block(g18)
    c: Coincident(g19,g18)
    c: Coincident(g20,g7)
    c: Horizontal(g20)
    c: Vertical(g21)
    c: Coincident(g20,g21)
    c: Block(g20)
    c: Block(g21)
    c: Block(g19)
    c: Block(g17)
FEATURE [Part::Extrusion] Extrude029
  Base = -> Sketch038
  Dir = (0,0,1)
  DirMode = 2
  FaceMakerClass = Part::FaceMakerBullseye
  LengthFwd = 72
  LengthRev = 0
  Solid = true
  Symmetric = false
FEATURE [Part::Feature] Face085
  shape: bbox 4.8 x 25.5 x 2e-07 mm, 1 faces, 0 solids (baked)
FEATURE [Part::Revolution] Revolve089  label="moreFrontCaseScrewPost003"
  Angle = 360
  Axis = (0,1,0)
  Base = (0,0,0)
  FaceMakerClass = Part::FaceMakerBullseye
  Placement = pos=(109.5,4.5,3.5) rot=(0,0,1;0rad)
  Solid = false
  Source = -> Face085
  Symmetric = false
FEATURE [Part::Feature] Face086
  shape: bbox 4.8 x 25.5 x 2e-07 mm, 1 faces, 0 solids (baked)
FEATURE [Part::Revolution] Revolve090  label="moreFrontCaseScrewPost004"
  Angle = 360
  Axis = (0,1,0)
  Base = (0,0,0)
  FaceMakerClass = Part::FaceMakerBullseye
  Placement = pos=(109.5,4.5,68.5) rot=(0,0,1;0rad)
  Solid = false
  Source = -> Face086
  Symmetric = false
FEATURE [Part::Fillet] Fillet026  label="top013"
  Base = -> Extrude029
  Edges = 1 edges r=2: [Edge35]
FEATURE [Sketcher::SketchObject] Sketch039
  FullyConstrained = true
  sketch-geometry (7):
    g0: LineSegment StartX=0 StartY=0 StartZ=0 EndX=0 EndY=6 EndZ=0
    g1: Circle CenterX=0 CenterY=0 CenterZ=0 NormalX=0 NormalY=0 NormalZ=1 AngleXU=0 Radius=1
    g2: Circle CenterX=8 CenterY=6 CenterZ=0 NormalX=0 NormalY=0 NormalZ=1 AngleXU=0 Radius=1
    g3: BSplineCurve PolesCount=3 KnotsCount=2 Degree=2 IsPeriodic=0
    g4: GeomPoint X=0 Y=0 Z=0
    g5: GeomPoint X=8 Y=6 Z=0
    g6: LineSegment StartX=0 StartY=6 StartZ=0 EndX=8 EndY=6 EndZ=0
  constraints (14):
    c: Coincident(g0,g-1)
    c: Distance(g0) = 6
    c: Vertical(g0)
    c: Coincident(g3,g0)
    c: Weight(g1) = 1
    c: Equal(g1,g2)
    c: InternalAlignment(g1,g3)
    c: InternalAlignment(g2,g3)
    c: InternalAlignment(g4,g3)
    c: InternalAlignment(g5,g3)
    c: Block(g3)
    c: Coincident(g6,g0)
    c: Coincident(g6,g3)
    c: Horizontal(g6)
FEATURE [Sketcher::SketchObject] Sketch040
  FullyConstrained = true
  sketch-geometry (7):
    g0: LineSegment StartX=0 StartY=0 StartZ=0 EndX=0 EndY=6 EndZ=0
    g1: Circle CenterX=0 CenterY=0 CenterZ=0 NormalX=0 NormalY=0 NormalZ=1 AngleXU=0 Radius=1
    g2: Circle CenterX=8 CenterY=6 CenterZ=0 NormalX=0 NormalY=0 NormalZ=1 AngleXU=0 Radius=1
    g3: BSplineCurve PolesCount=3 KnotsCount=2 Degree=2 IsPeriodic=0
    g4: GeomPoint X=0 Y=0 Z=0
    g5: GeomPoint X=8 Y=6 Z=0
    g6: LineSegment StartX=0 StartY=6 StartZ=0 EndX=8 EndY=6 EndZ=0
  constraints (14):
    c: Coincident(g0,g-1)
    c: Distance(g0) = 6
    c: Vertical(g0)
    c: Coincident(g3,g0)
    c: Weight(g1) = 1
    c: Equal(g1,g2)
    c: InternalAlignment(g1,g3)
    c: InternalAlignment(g2,g3)
    c: InternalAlignment(g4,g3)
    c: InternalAlignment(g5,g3)
    c: Block(g3)
    c: Coincident(g6,g0)
    c: Coincident(g6,g3)
    c: Horizontal(g6)
FEATURE [Sketcher::SketchObject] Sketch041
  FullyConstrained = true
  sketch-geometry (7):
    g0: LineSegment StartX=0 StartY=0 StartZ=0 EndX=0 EndY=6 EndZ=0
    g1: Circle CenterX=0 CenterY=0 CenterZ=0 NormalX=0 NormalY=0 NormalZ=1 AngleXU=0 Radius=1
    g2: Circle CenterX=8 CenterY=6 CenterZ=0 NormalX=0 NormalY=0 NormalZ=1 AngleXU=0 Radius=1
    g3: BSplineCurve PolesCount=3 KnotsCount=2 Degree=2 IsPeriodic=0
    g4: GeomPoint X=0 Y=0 Z=0
    g5: GeomPoint X=8 Y=6 Z=0
    g6: LineSegment StartX=0 StartY=6 StartZ=0 EndX=8 EndY=6 EndZ=0
  constraints (14):
    c: Coincident(g0,g-1)
    c: Distance(g0) = 6
    c: Vertical(g0)
    c: Coincident(g3,g0)
    c: Weight(g1) = 1
    c: Equal(g1,g2)
    c: InternalAlignment(g1,g3)
    c: InternalAlignment(g2,g3)
    c: InternalAlignment(g4,g3)
    c: InternalAlignment(g5,g3)
    c: Block(g3)
    c: Coincident(g6,g0)
    c: Coincident(g6,g3)
    c: Horizontal(g6)
FEATURE [Sketcher::SketchObject] Sketch042
  FullyConstrained = true
  sketch-geometry (7):
    g0: LineSegment StartX=0 StartY=0 StartZ=0 EndX=0 EndY=6 EndZ=0
    g1: Circle CenterX=0 CenterY=0 CenterZ=0 NormalX=0 NormalY=0 NormalZ=1 AngleXU=0 Radius=1
    g2: Circle CenterX=8 CenterY=6 CenterZ=0 NormalX=0 NormalY=0 NormalZ=1 AngleXU=0 Radius=1
    g3: BSplineCurve PolesCount=3 KnotsCount=2 Degree=2 IsPeriodic=0
    g4: GeomPoint X=0 Y=0 Z=0
    g5: GeomPoint X=8 Y=6 Z=0
    g6: LineSegment StartX=0 StartY=6 StartZ=0 EndX=8 EndY=6 EndZ=0
  constraints (14):
    c: Coincident(g0,g-1)
    c: Distance(g0) = 6
    c: Vertical(g0)
    c: Coincident(g3,g0)
    c: Weight(g1) = 1
    c: Equal(g1,g2)
    c: InternalAlignment(g1,g3)
    c: InternalAlignment(g2,g3)
    c: InternalAlignment(g4,g3)
    c: InternalAlignment(g5,g3)
    c: Block(g3)
    c: Coincident(g6,g0)
    c: Coincident(g6,g3)
    c: Horizontal(g6)
FEATURE [Part::Extrusion] Extrude030  label="caseScrewPillarBracket008"
  Base = -> Sketch039
  Dir = (0,0,1)
  DirMode = 2
  FaceMakerClass = Part::FaceMakerBullseye
  LengthFwd = 2.4
  LengthRev = 0
  Placement = pos=(15.76,29,8.8) rot=(0,1,0;0rad)
  Solid = true
  Symmetric = false
FEATURE [Part::Extrusion] Extrude031  label="caseScrewPillarBracket009"
  Base = -> Sketch040
  Dir = (0,0,1)
  DirMode = 2
  FaceMakerClass = Part::FaceMakerBullseye
  LengthFwd = 2.4
  LengthRev = 0
  Placement = pos=(15.76,29,60.8) rot=(0,0,1;0rad)
  Solid = true
  Symmetric = false
FEATURE [Part::Extrusion] Extrude032  label="caseScrewPillarBracket010"
  Base = -> Sketch041
  Dir = (0,0,1)
  DirMode = 2
  FaceMakerClass = Part::FaceMakerBullseye
  LengthFwd = 2.4
  LengthRev = 0
  Placement = pos=(13.7,29,13.26) rot=(0,-1,0;1.5708rad)
  Solid = true
  Symmetric = false
FEATURE [Part::Extrusion] Extrude033  label="caseScrewPillarBracket011"
  Base = -> Sketch042
  Dir = (0,0,1)
  DirMode = 2
  FaceMakerClass = Part::FaceMakerBullseye
  LengthFwd = 2.4
  LengthRev = 0
  Placement = pos=(11.3,29,58.74) rot=(0,1,0;1.5708rad)
  Solid = true
  Symmetric = false
FEATURE [Sketcher::SketchObject] Sketch043
  FullyConstrained = true
  sketch-geometry (7):
    g0: LineSegment StartX=0 StartY=0 StartZ=0 EndX=0 EndY=6 EndZ=0
    g1: Circle CenterX=0 CenterY=0 CenterZ=0 NormalX=0 NormalY=0 NormalZ=1 AngleXU=0 Radius=1
    g2: Circle CenterX=8 CenterY=6 CenterZ=0 NormalX=0 NormalY=0 NormalZ=1 AngleXU=0 Radius=1
    g3: BSplineCurve PolesCount=3 KnotsCount=2 Degree=2 IsPeriodic=0
    g4: GeomPoint X=0 Y=0 Z=0
    g5: GeomPoint X=8 Y=6 Z=0
    g6: LineSegment StartX=0 StartY=6 StartZ=0 EndX=8 EndY=6 EndZ=0
  constraints (14):
    c: Coincident(g0,g-1)
    c: Distance(g0) = 6
    c: Vertical(g0)
    c: Coincident(g3,g0)
    c: Weight(g1) = 1
    c: Equal(g1,g2)
    c: InternalAlignment(g1,g3)
    c: InternalAlignment(g2,g3)
    c: InternalAlignment(g4,g3)
    c: InternalAlignment(g5,g3)
    c: Block(g3)
    c: Coincident(g6,g0)
    c: Coincident(g6,g3)
    c: Horizontal(g6)
FEATURE [Part::Extrusion] Extrude034  label="caseScrewPillarBracket012"
  Base = -> Sketch043
  Dir = (0,0,1)
  DirMode = 2
  FaceMakerClass = Part::FaceMakerBullseye
  LengthFwd = 2.4
  LengthRev = 0
  Placement = pos=(88.3,29,65.23) rot=(0,1,0;1.5708rad)
  Solid = true
  Symmetric = false
FEATURE [Sketcher::SketchObject] Sketch044
  FullyConstrained = true
  sketch-geometry (7):
    g0: LineSegment StartX=0 StartY=0 StartZ=0 EndX=0 EndY=6 EndZ=0
    g1: Circle CenterX=0 CenterY=0 CenterZ=0 NormalX=0 NormalY=0 NormalZ=1 AngleXU=0 Radius=1
    g2: Circle CenterX=8 CenterY=6 CenterZ=0 NormalX=0 NormalY=0 NormalZ=1 AngleXU=0 Radius=1
    g3: BSplineCurve PolesCount=3 KnotsCount=2 Degree=2 IsPeriodic=0
    g4: GeomPoint X=0 Y=0 Z=0
    g5: GeomPoint X=8 Y=6 Z=0
    g6: LineSegment StartX=0 StartY=6 StartZ=0 EndX=8 EndY=6 EndZ=0
  constraints (14):
    c: Coincident(g0,g-1)
    c: Distance(g0) = 6
    c: Vertical(g0)
    c: Coincident(g3,g0)
    c: Weight(g1) = 1
    c: Equal(g1,g2)
    c: InternalAlignment(g1,g3)
    c: InternalAlignment(g2,g3)
    c: InternalAlignment(g4,g3)
    c: InternalAlignment(g5,g3)
    c: Block(g3)
    c: Coincident(g6,g0)
    c: Coincident(g6,g3)
    c: Horizontal(g6)
FEATURE [Part::Extrusion] Extrude035  label="caseScrewPillarBracket013"
  Base = -> Sketch044
  Dir = (0,0,1)
  DirMode = 2
  FaceMakerClass = Part::FaceMakerBullseye
  LengthFwd = 2.4
  LengthRev = 0
  Placement = pos=(90.7,29,6.77) rot=(0,-1,0;1.5708rad)
  Solid = true
  Symmetric = false
FEATURE [Sketcher::SketchObject] Sketch045
  FullyConstrained = true
  sketch-geometry (7):
    g0: LineSegment StartX=0 StartY=0 StartZ=0 EndX=0 EndY=6 EndZ=0
    g1: Circle CenterX=0 CenterY=0 CenterZ=0 NormalX=0 NormalY=0 NormalZ=1 AngleXU=0 Radius=1
    g2: Circle CenterX=8 CenterY=6 CenterZ=0 NormalX=0 NormalY=0 NormalZ=1 AngleXU=0 Radius=1
    g3: BSplineCurve PolesCount=3 KnotsCount=2 Degree=2 IsPeriodic=0
    g4: GeomPoint X=0 Y=0 Z=0
    g5: GeomPoint X=8 Y=6 Z=0
    g6: LineSegment StartX=0 StartY=6 StartZ=0 EndX=8 EndY=6 EndZ=0
  constraints (14):
    c: Coincident(g0,g-1)
    c: Distance(g0) = 6
    c: Vertical(g0)
    c: Coincident(g3,g0)
    c: Weight(g1) = 1
    c: Equal(g1,g2)
    c: InternalAlignment(g1,g3)
    c: InternalAlignment(g2,g3)
    c: InternalAlignment(g4,g3)
    c: InternalAlignment(g5,g3)
    c: Block(g3)
    c: Coincident(g6,g0)
    c: Coincident(g6,g3)
    c: Horizontal(g6)
FEATURE [Sketcher::SketchObject] Sketch046
  FullyConstrained = true
  sketch-geometry (7):
    g0: LineSegment StartX=0 StartY=0 StartZ=0 EndX=0 EndY=6 EndZ=0
    g1: Circle CenterX=0 CenterY=0 CenterZ=0 NormalX=0 NormalY=0 NormalZ=1 AngleXU=0 Radius=1
    g2: Circle CenterX=8 CenterY=6 CenterZ=0 NormalX=0 NormalY=0 NormalZ=1 AngleXU=0 Radius=1
    g3: BSplineCurve PolesCount=3 KnotsCount=2 Degree=2 IsPeriodic=0
    g4: GeomPoint X=0 Y=0 Z=0
    g5: GeomPoint X=8 Y=6 Z=0
    g6: LineSegment StartX=0 StartY=6 StartZ=0 EndX=8 EndY=6 EndZ=0
  constraints (14):
    c: Coincident(g0,g-1)
    c: Distance(g0) = 6
    c: Vertical(g0)
    c: Coincident(g3,g0)
    c: Weight(g1) = 1
    c: Equal(g1,g2)
    c: InternalAlignment(g1,g3)
    c: InternalAlignment(g2,g3)
    c: InternalAlignment(g4,g3)
    c: InternalAlignment(g5,g3)
    c: Block(g3)
    c: Coincident(g6,g0)
    c: Coincident(g6,g3)
    c: Horizontal(g6)
FEATURE [Part::Extrusion] Extrude036  label="caseScrewPillarBracket014"
  Base = -> Sketch045
  Dir = (0,0,1)
  DirMode = 2
  FaceMakerClass = Part::FaceMakerBullseye
  LengthFwd = 2.4
  LengthRev = 0
  Placement = pos=(110.7,29,6.77) rot=(0,-1,0;1.5708rad)
  Solid = true
  Symmetric = false
FEATURE [Part::Extrusion] Extrude037  label="caseScrewPillarBracket015"
  Base = -> Sketch046
  Dir = (0,0,1)
  DirMode = 2
  FaceMakerClass = Part::FaceMakerBullseye
  LengthFwd = 2.4
  LengthRev = 0
  Placement = pos=(108.3,29,65.23) rot=(0,1,0;1.5708rad)
  Solid = true
  Symmetric = false
FEATURE [Part::Box] Box013  label="frontCaseScrewPillarBracket002"
  AttacherType = Attacher::AttachEngine3D
  Height = 2.4
  Length = 22
  Placement = pos=(87,28,2.3) rot=(0,0,1;0rad)
  Width = 7
FEATURE [Part::Box] Box014  label="frontCaseScrewPillarBracket003"
  AttacherType = Attacher::AttachEngine3D
  Height = 2.4
  Length = 22
  Placement = pos=(87,28,67.3) rot=(0,0,1;0rad)
  Width = 7
FEATURE [Part::Feature] Face087
  shape: bbox 4.8 x 30.2 x 2e-07 mm, 1 faces, 0 solids (baked)
FEATURE [Part::Revolution] Revolve091  label="frontCaseScrewPost004"
  Angle = 360
  Axis = (0,1,0)
  Base = (0,0,0)
  FaceMakerClass = Part::FaceMakerBullseye
  Placement = pos=(89.5,4.5,3.5) rot=(0,0,1;0rad)
  Solid = false
  Source = -> Face087
  Symmetric = false
FEATURE [Part::Feature] Face088
  shape: bbox 4.8 x 30.2 x 2e-07 mm, 1 faces, 0 solids (baked)
FEATURE [Part::Revolution] Revolve092  label="frontCaseScrewPost005"
  Angle = 360
  Axis = (0,1,0)
  Base = (0,0,0)
  FaceMakerClass = Part::FaceMakerBullseye
  Placement = pos=(89.5,4.5,68.5) rot=(0,0,1;0rad)
  Solid = false
  Source = -> Face088
  Symmetric = false
FEATURE [Part::Feature] Face089
  shape: bbox 3.5 x 30.2 x 2e-07 mm, 1 faces, 0 solids (baked)
FEATURE [Part::Revolution] Revolve093  label="backCaseScrewPost002"
  Angle = 360
  Axis = (0,1,0)
  Base = (0,0,0)
  FaceMakerClass = Part::FaceMakerBullseye
  Placement = pos=(12.5,4.5,10) rot=(0,0,1;0rad)
  Solid = false
  Source = -> Face089
  Symmetric = false
FEATURE [Part::Feature] Face090
  shape: bbox 3.5 x 30.2 x 2e-07 mm, 1 faces, 0 solids (baked)
FEATURE [Part::Revolution] Revolve094  label="backCaseScrewPost003"
  Angle = 360
  Axis = (0,1,0)
  Base = (0,0,0)
  FaceMakerClass = Part::FaceMakerBullseye
  Placement = pos=(12.5,4.5,62) rot=(0,0,1;0rad)
  Solid = false
  Source = -> Face090
  Symmetric = false
FEATURE [Part::Box] Box015  label="Cube011"
  AttacherType = Attacher::AttachEngine3D
  Height = 28.8
  Length = 3
  Placement = pos=(107.3,28,21.6) rot=(0,0,1;0rad)
  Width = 7
FEATURE [Part::Box] Box016  label="Cube012"
  AttacherType = Attacher::AttachEngine3D
  Height = 3
  Length = 7.4
  Placement = pos=(107.3,28,18.6) rot=(0,0,1;0rad)
  Width = 7
FEATURE [Part::Box] Box017  label="Cube013"
  AttacherType = Attacher::AttachEngine3D
  Height = 3
  Length = 7.4
  Placement = pos=(107.3,28,50.4) rot=(0,0,1;0rad)
  Width = 7
FEATURE [Part::Cylinder] Cylinder024
  Angle = 360
  AttacherType = Attacher::AttachEngine3D
  Height = 20
  Placement = pos=(0,0,36.15) rot=(0,0,1;0rad)
  Radius = 14.3
FEATURE [Part::Cylinder] Cylinder025
  Angle = 360
  AttacherType = Attacher::AttachEngine3D
  Height = 10
  Placement = pos=(0,0,36.15) rot=(0,0,1;0rad)
  Radius = 4
FEATURE [Part::MultiFuse] Fusion066  label="removeToCreteHoleForPlugHousing009"
  Placement = pos=(70,19,36) rot=(0,1,0;1.5708rad)
  Shapes = -> [Cylinder024,Cylinder025]
FEATURE [Part::MultiFuse] Fusion065  label="plugHousingBracketHolder002"
  Shapes = -> [Box017,Box015,Box016]
FEATURE [Part::Cut] Cut025  label="plugHousingBracketHolder003"
  Base = -> Fusion065
  Placement = pos=(7,0,0) rot=(0,0,1;0rad)
  Tool = -> Fusion066
FEATURE [Sketcher::SketchObject] Sketch047
  FullyConstrained = false
  Placement = pos=(0,0,0) rot=(1,0,0;1.5708rad)
  sketch-geometry (24):
    g0: ArcOfCircle CenterX=-4 CenterY=-10.5 CenterZ=0 NormalX=0 NormalY=0 NormalZ=1 AngleXU=0 Radius=1.5 StartAngle=6e-16 EndAngle=3.14159
    g1: ArcOfCircle CenterX=-34.2 CenterY=-10.5 CenterZ=0 NormalX=0 NormalY=0 NormalZ=1 AngleXU=0 Radius=1.5 StartAngle=0 EndAngle=3.14159
    g2: ArcOfCircle CenterX=-34.2 CenterY=-27.7 CenterZ=0 NormalX=0 NormalY=0 NormalZ=1 AngleXU=0 Radius=1.5 StartAngle=3.14159 EndAngle=6.28319
    g3: ArcOfCircle CenterX=-4 CenterY=-27.7 CenterZ=0 NormalX=0 NormalY=0 NormalZ=1 AngleXU=0 Radius=1.5 StartAngle=3.1416 EndAngle=6.28319
    g4: ArcOfCircle CenterX=-10 CenterY=-4.3 CenterZ=0 NormalX=0 NormalY=0 NormalZ=1 AngleXU=0 Radius=1.5 StartAngle=2e-16 EndAngle=3.14159
    g5: ArcOfCircle CenterX=-16.1 CenterY=-1.8 CenterZ=0 NormalX=0 NormalY=0 NormalZ=1 AngleXU=0 Radius=1.5 StartAngle=5e-16 EndAngle=3.14159
    g6: ArcOfCircle CenterX=-22.1 CenterY=-1.8 CenterZ=0 NormalX=0 NormalY=0 NormalZ=1 AngleXU=0 Radius=1.5 StartAngle=5e-16 EndAngle=3.14159
    g7: ArcOfCircle CenterX=-28.2 CenterY=-4.3 CenterZ=0 NormalX=0 NormalY=0 NormalZ=1 AngleXU=0 Radius=1.5 StartAngle=2e-16 EndAngle=3.14159
    g8: ArcOfCircle CenterX=-10 CenterY=-33.9 CenterZ=0 NormalX=0 NormalY=0 NormalZ=1 AngleXU=0 Radius=1.5 StartAngle=3.14159 EndAngle=6.28319
    g9: ArcOfCircle CenterX=-16.1 CenterY=-36.4 CenterZ=0 NormalX=0 NormalY=0 NormalZ=1 AngleXU=0 Radius=1.5 StartAngle=3.14159 EndAngle=6.28319
    g10: ArcOfCircle CenterX=-22.1 CenterY=-36.4 CenterZ=0 NormalX=0 NormalY=0 NormalZ=1 AngleXU=0 Radius=1.5 StartAngle=3.14159 EndAngle=6.28319
    g11: ArcOfCircle CenterX=-28.2 CenterY=-33.9 CenterZ=0 NormalX=0 NormalY=0 NormalZ=1 AngleXU=0 Radius=1.5 StartAngle=3.14159 EndAngle=6.28319
    g12: LineSegment StartX=-35.7 StartY=-10.5 StartZ=0 EndX=-35.7 EndY=-27.7 EndZ=0
    g13: LineSegment StartX=-32.7 StartY=-10.5 StartZ=0 EndX=-32.7 EndY=-27.7 EndZ=0
    g14: LineSegment StartX=-29.7 StartY=-33.9 StartZ=0 EndX=-29.7 EndY=-4.3 EndZ=0
    g15: LineSegment StartX=-26.7 StartY=-33.9 StartZ=0 EndX=-26.7 EndY=-4.3 EndZ=0
    g16: LineSegment StartX=-2.5 StartY=-10.5 StartZ=0 EndX=-2.5 EndY=-27.7 EndZ=0
    g17: LineSegment StartX=-8.5 StartY=-4.3 StartZ=0 EndX=-8.5 EndY=-33.9 EndZ=0
    g18: LineSegment StartX=-5.5 StartY=-10.5 StartZ=0 EndX=-5.5 EndY=-27.7 EndZ=0
    g19: LineSegment StartX=-11.5 StartY=-4.3 StartZ=0 EndX=-11.5 EndY=-33.9 EndZ=0
    g20: LineSegment StartX=-14.6 StartY=-1.8 StartZ=0 EndX=-14.6 EndY=-36.4 EndZ=0
    g21: LineSegment StartX=-17.6 StartY=-1.8 StartZ=0 EndX=-17.6 EndY=-36.4 EndZ=0
    g22: LineSegment StartX=-20.6 StartY=-36.4 StartZ=0 EndX=-20.6 EndY=-1.8 EndZ=0
    g23: LineSegment StartX=-23.6 StartY=-1.8 StartZ=0 EndX=-23.6 EndY=-36.4 EndZ=0
  constraints (48):
    c: Block(g0)
    c: Block(g1)
    c: Block(g2)
    c: Block(g3)
    c: Block(g4)
    c: Block(g5)
    c: Block(g6)
    c: Block(g7)
    c: Block(g8)
    c: Block(g9)
    c: Block(g10)
    c: Block(g11)
    c: Coincident(g12,g1)
    c: Coincident(g12,g2)
    c: Vertical(g12)
    c: Coincident(g13,g1)
    c: Coincident(g13,g2)
    c: Vertical(g13)
    c: Coincident(g14,g11)
    c: Coincident(g14,g7)
    c: Vertical(g14)
    c: Coincident(g15,g11)
    c: Coincident(g15,g7)
    c: Vertical(g15)
    c: Coincident(g16,g0)
    c: Coincident(g16,g3)
    c: Vertical(g16)
    c: Coincident(g17,g4)
    c: Coincident(g17,g8)
    c: Vertical(g17)
    c: Coincident(g18,g0)
    c: Coincident(g18,g3)
    c: Vertical(g18)
    c: Coincident(g19,g4)
    c: Coincident(g19,g8)
    c: Vertical(g19)
    c: Coincident(g20,g5)
    c: Coincident(g20,g9)
    c: Vertical(g20)
    c: Coincident(g21,g5)
    c: Coincident(g21,g9)
    c: Vertical(g21)
    c: Coincident(g22,g10)
    c: Coincident(g22,g6)
    c: Vertical(g22)
    c: Coincident(g23,g6)
    c: Coincident(g23,g10)
    c: Vertical(g23)
FEATURE [Part::Extrusion] Extrude038  label="removeToCreateFanGrillHoles001"
  Base = -> Sketch047
  Dir = (0,-1,6e-16)
  DirMode = 2
  FaceMakerClass = Part::FaceMakerBullseye
  LengthFwd = 10
  LengthRev = 0
  Placement = pos=(65.4,44,54.82) rot=(0,0,1;0rad)
  Solid = true
  Symmetric = false
FEATURE [Part::Feature] Wire004
  shape: bbox 11 x 5.2 x 2e-07 mm, 0 faces, 0 solids (baked)
FEATURE [Part::Revolution] Revolve095
  Angle = 360
  Axis = (0,1,0)
  Base = (0,0,0)
  FaceMakerClass = Part::FaceMakerBullseye
  Placement = pos=(30.3,38,19.7) rot=(0,0,1;0rad)
  Solid = true
  Source = -> Wire004
  Symmetric = false
FEATURE [Part::Feature] Wire005
  shape: bbox 11 x 5.2 x 2e-07 mm, 0 faces, 0 solids (baked)
FEATURE [Part::Revolution] Revolve096
  Angle = 360
  Axis = (0,1,0)
  Base = (0,0,0)
  FaceMakerClass = Part::FaceMakerBullseye
  Placement = pos=(30.3,38,51.7) rot=(0,0,1;0rad)
  Solid = true
  Source = -> Wire005
  Symmetric = false
FEATURE [Part::Feature] Wire006
  shape: bbox 11 x 5.2 x 2e-07 mm, 0 faces, 0 solids (baked)
FEATURE [Part::Revolution] Revolve097
  Angle = 360
  Axis = (0,1,0)
  Base = (0,0,0)
  FaceMakerClass = Part::FaceMakerBullseye
  Placement = pos=(62.3,38,51.7) rot=(0,0,1;0rad)
  Solid = true
  Source = -> Wire006
  Symmetric = false
FEATURE [Part::Feature] Wire007
  shape: bbox 11 x 5.2 x 2e-07 mm, 0 faces, 0 solids (baked)
FEATURE [Part::Revolution] Revolve098
  Angle = 360
  Axis = (0,1,0)
  Base = (0,0,0)
  FaceMakerClass = Part::FaceMakerBullseye
  Placement = pos=(62.3,38,19.7) rot=(0,0,1;0rad)
  Solid = true
  Source = -> Wire007
  Symmetric = false
FEATURE [Part::MultiFuse] Fusion067  label="fanScrewHousing002"
  Shapes = -> [Revolve098,Revolve097,Revolve096,Revolve095]
FEATURE [Part::Feature] Face091 .. Face094  x4 (patterned run collapsed; names and placements below)
  shape: bbox 3.5 x 17.8 x 2e-07 mm, 1 faces, 0 solids (baked)
FEATURE [Part::Revolution] Revolve099  label="removeToCreateScrewAndThreadedInsertHole026"
  Angle = 360
  Axis = (0,1,0)
  Base = (0,0,0)
  FaceMakerClass = Part::FaceMakerBullseye
  Placement = pos=(62.3,30.3,19.7) rot=(0,0,1;0rad)
  Solid = false
  Source = -> Face091
  Symmetric = false
FEATURE [Part::Revolution] Revolve100  label="removeToCreateScrewAndThreadedInsertHole027"
  Angle = 360
  Axis = (0,1,0)
  Base = (0,0,0)
  FaceMakerClass = Part::FaceMakerBullseye
  Placement = pos=(62.3,30.3,51.7) rot=(0,0,1;0rad)
  Solid = false
  Source = -> Face092
  Symmetric = false
FEATURE [Part::Revolution] Revolve101  label="removeToCreateScrewAndThreadedInsertHole028"
  Angle = 360
  Axis = (0,1,0)
  Base = (0,0,0)
  FaceMakerClass = Part::FaceMakerBullseye
  Placement = pos=(30.3,30.3,19.7) rot=(0,0,1;0rad)
  Solid = false
  Source = -> Face093
  Symmetric = false
FEATURE [Part::Revolution] Revolve102  label="removeToCreateScrewAndThreadedInsertHole029"
  Angle = 360
  Axis = (0,1,0)
  Base = (0,0,0)
  FaceMakerClass = Part::FaceMakerBullseye
  Placement = pos=(30.3,30.3,51.7) rot=(0,0,1;0rad)
  Solid = false
  Source = -> Face094
  Symmetric = false
FEATURE [Part::MultiFuse] Fusion068  label="createThreadedInsertHolesForFan002"
  Shapes = -> [Revolve099,Revolve100,Revolve101,Revolve102]
FEATURE [Part::Cut] Cut026  label="fanScrewHousing003"
  Base = -> Fusion067
  Tool = -> Fusion068
FEATURE [Sketcher::SketchObject] Sketch048
  FullyConstrained = false
  Placement = pos=(0,0,0) rot=(1,0,0;1.5708rad)
  sketch-geometry (24):
    g0: ArcOfCircle CenterX=-4 CenterY=-10.5 CenterZ=0 NormalX=0 NormalY=0 NormalZ=1 AngleXU=0 Radius=1.5 StartAngle=6e-16 EndAngle=3.14159
    g1: ArcOfCircle CenterX=-34.2 CenterY=-10.5 CenterZ=0 NormalX=0 NormalY=0 NormalZ=1 AngleXU=0 Radius=1.5 StartAngle=0 EndAngle=3.14159
    g2: ArcOfCircle CenterX=-34.2 CenterY=-27.7 CenterZ=0 NormalX=0 NormalY=0 NormalZ=1 AngleXU=0 Radius=1.5 StartAngle=3.14159 EndAngle=6.28319
    g3: ArcOfCircle CenterX=-4 CenterY=-27.7 CenterZ=0 NormalX=0 NormalY=0 NormalZ=1 AngleXU=0 Radius=1.5 StartAngle=3.1416 EndAngle=6.28319
    g4: ArcOfCircle CenterX=-10 CenterY=-4.3 CenterZ=0 NormalX=0 NormalY=0 NormalZ=1 AngleXU=0 Radius=1.5 StartAngle=2e-16 EndAngle=3.14159
    g5: ArcOfCircle CenterX=-16.1 CenterY=-1.8 CenterZ=0 NormalX=0 NormalY=0 NormalZ=1 AngleXU=0 Radius=1.5 StartAngle=5e-16 EndAngle=3.14159
    g6: ArcOfCircle CenterX=-22.1 CenterY=-1.8 CenterZ=0 NormalX=0 NormalY=0 NormalZ=1 AngleXU=0 Radius=1.5 StartAngle=5e-16 EndAngle=3.14159
    g7: ArcOfCircle CenterX=-28.2 CenterY=-4.3 CenterZ=0 NormalX=0 NormalY=0 NormalZ=1 AngleXU=0 Radius=1.5 StartAngle=2e-16 EndAngle=3.14159
    g8: ArcOfCircle CenterX=-10 CenterY=-33.9 CenterZ=0 NormalX=0 NormalY=0 NormalZ=1 AngleXU=0 Radius=1.5 StartAngle=3.14159 EndAngle=6.28319
    g9: ArcOfCircle CenterX=-16.1 CenterY=-36.4 CenterZ=0 NormalX=0 NormalY=0 NormalZ=1 AngleXU=0 Radius=1.5 StartAngle=3.14159 EndAngle=6.28319
    g10: ArcOfCircle CenterX=-22.1 CenterY=-36.4 CenterZ=0 NormalX=0 NormalY=0 NormalZ=1 AngleXU=0 Radius=1.5 StartAngle=3.14159 EndAngle=6.28319
    g11: ArcOfCircle CenterX=-28.2 CenterY=-33.9 CenterZ=0 NormalX=0 NormalY=0 NormalZ=1 AngleXU=0 Radius=1.5 StartAngle=3.14159 EndAngle=6.28319
    g12: LineSegment StartX=-35.7 StartY=-10.5 StartZ=0 EndX=-35.7 EndY=-27.7 EndZ=0
    g13: LineSegment StartX=-32.7 StartY=-10.5 StartZ=0 EndX=-32.7 EndY=-27.7 EndZ=0
    g14: LineSegment StartX=-29.7 StartY=-33.9 StartZ=0 EndX=-29.7 EndY=-4.3 EndZ=0
    g15: LineSegment StartX=-26.7 StartY=-33.9 StartZ=0 EndX=-26.7 EndY=-4.3 EndZ=0
    g16: LineSegment StartX=-2.5 StartY=-10.5 StartZ=0 EndX=-2.5 EndY=-27.7 EndZ=0
    g17: LineSegment StartX=-8.5 StartY=-4.3 StartZ=0 EndX=-8.5 EndY=-33.9 EndZ=0
    g18: LineSegment StartX=-5.5 StartY=-10.5 StartZ=0 EndX=-5.5 EndY=-27.7 EndZ=0
    g19: LineSegment StartX=-11.5 StartY=-4.3 StartZ=0 EndX=-11.5 EndY=-33.9 EndZ=0
    g20: LineSegment StartX=-14.6 StartY=-1.8 StartZ=0 EndX=-14.6 EndY=-36.4 EndZ=0
    g21: LineSegment StartX=-17.6 StartY=-1.8 StartZ=0 EndX=-17.6 EndY=-36.4 EndZ=0
    g22: LineSegment StartX=-20.6 StartY=-36.4 StartZ=0 EndX=-20.6 EndY=-1.8 EndZ=0
    g23: LineSegment StartX=-23.6 StartY=-1.8 StartZ=0 EndX=-23.6 EndY=-36.4 EndZ=0
  constraints (48):
    c: Block(g0)
    c: Block(g1)
    c: Block(g2)
    c: Block(g3)
    c: Block(g4)
    c: Block(g5)
    c: Block(g6)
    c: Block(g7)
    c: Block(g8)
    c: Block(g9)
    c: Block(g10)
    c: Block(g11)
    c: Coincident(g12,g1)
    c: Coincident(g12,g2)
    c: Vertical(g12)
    c: Coincident(g13,g1)
    c: Coincident(g13,g2)
    c: Vertical(g13)
    c: Coincident(g14,g11)
    c: Coincident(g14,g7)
    c: Vertical(g14)
    c: Coincident(g15,g11)
    c: Coincident(g15,g7)
    c: Vertical(g15)
    c: Coincident(g16,g0)
    c: Coincident(g16,g3)
    c: Vertical(g16)
    c: Coincident(g17,g4)
    c: Coincident(g17,g8)
    c: Vertical(g17)
    c: Coincident(g18,g0)
    c: Coincident(g18,g3)
    c: Vertical(g18)
    c: Coincident(g19,g4)
    c: Coincident(g19,g8)
    c: Vertical(g19)
    c: Coincident(g20,g5)
    c: Coincident(g20,g9)
    c: Vertical(g20)
    c: Coincident(g21,g5)
    c: Coincident(g21,g9)
    c: Vertical(g21)
    c: Coincident(g22,g10)
    c: Coincident(g22,g6)
    c: Vertical(g22)
    c: Coincident(g23,g6)
    c: Coincident(g23,g10)
    c: Vertical(g23)
FEATURE [Part::Extrusion] Extrude039  label="removeToCreateFanGrillHoles002"
  Base = -> Sketch048
  Dir = (0,-1,6e-16)
  DirMode = 2
  FaceMakerClass = Part::FaceMakerBullseye
  LengthFwd = 10
  LengthRev = 0
  Placement = pos=(65.4,44,54.82) rot=(0,0,1;0rad)
  Solid = true
  Symmetric = false
FEATURE [Part::Cut] Cut027  label="fanScrewHousing004"
  Base = -> Cut026
  Tool = -> Extrude038
FEATURE [Part::Cut] Cut028  label="top014"
  Base = -> Fillet026
  Tool = -> Extrude039
FEATURE [Part::Feature] Face095 .. Face098  x4 (patterned run collapsed; names and placements below)
  shape: bbox 3.5 x 17.8 x 2e-07 mm, 1 faces, 0 solids (baked)
FEATURE [Part::Revolution] Revolve103  label="removeToCreateScrewAndThreadedInsertHole030"
  Angle = 360
  Axis = (0,1,0)
  Base = (0,0,0)
  FaceMakerClass = Part::FaceMakerBullseye
  Placement = pos=(62.3,30.3,19.7) rot=(0,0,1;0rad)
  Solid = false
  Source = -> Face095
  Symmetric = false
FEATURE [Part::Revolution] Revolve104  label="removeToCreateScrewAndThreadedInsertHole031"
  Angle = 360
  Axis = (0,1,0)
  Base = (0,0,0)
  FaceMakerClass = Part::FaceMakerBullseye
  Placement = pos=(62.3,30.3,51.7) rot=(0,0,1;0rad)
  Solid = false
  Source = -> Face096
  Symmetric = false
FEATURE [Part::Revolution] Revolve105  label="removeToCreateScrewAndThreadedInsertHole032"
  Angle = 360
  Axis = (0,1,0)
  Base = (0,0,0)
  FaceMakerClass = Part::FaceMakerBullseye
  Placement = pos=(30.3,30.3,19.7) rot=(0,0,1;0rad)
  Solid = false
  Source = -> Face097
  Symmetric = false
FEATURE [Part::Revolution] Revolve106  label="removeToCreateScrewAndThreadedInsertHole033"
  Angle = 360
  Axis = (0,1,0)
  Base = (0,0,0)
  FaceMakerClass = Part::FaceMakerBullseye
  Placement = pos=(30.3,30.3,51.7) rot=(0,0,1;0rad)
  Solid = false
  Source = -> Face098
  Symmetric = false
FEATURE [Part::MultiFuse] Fusion069  label="createThreadedInsertHolesForFan003"
  Shapes = -> [Revolve103,Revolve104,Revolve105,Revolve106]
FEATURE [Part::Cut] Cut029  label="top015"
  Base = -> Cut028
  Tool = -> Fusion054
FEATURE [Part::Cut] Cut030  label="fanScrewHousing005"
  Base = -> Cut027
  Tool = -> Fusion069
FEATURE [Part::Cylinder] Cylinder026  label="removeToCreteHoleForPlugHousing010"
  Angle = 360
  AttacherType = Attacher::AttachEngine3D
  Height = 20
  Placement = pos=(-2,19,36) rot=(0,1,0;1.5708rad)
  Radius = 14.3
FEATURE [Part::Box] Box018  label="removeToCreteHoleForPlugHousing011"
  AttacherType = Attacher::AttachEngine3D
  Height = 28.6
  Length = 10
  Placement = pos=(-2,0,21.7) rot=(0,0,1;0rad)
  Width = 19
FEATURE [Part::Box] Box019  label="wireHolderBottomCaseBit"
  AttacherType = Attacher::AttachEngine3D
  Height = 28
  Length = 3
  Placement = pos=(0,0,22) rot=(0,0,1;0rad)
  Width = 21
FEATURE [Part::Cylinder] Cylinder027  label="removeToCreteHoleForPlugHousing012"
  Angle = 360
  AttacherType = Attacher::AttachEngine3D
  Height = 20
  Placement = pos=(-2,19,36) rot=(0,1,0;1.5708rad)
  Radius = 14.3
FEATURE [Part::Cut] Cut031  label="wireHolderBottomCaseBit001"
  Base = -> Box019
  Tool = -> Cylinder027
FEATURE [Part::MultiFuse] Fusion070  label="removeToCreteHoleForPlugHousing013"
  Shapes = -> [Box018,Cylinder026]
FEATURE [Part::Cut] Cut032  label="top016"
  Base = -> Cut029
  Tool = -> Fusion070
FEATURE [Part::Cylinder] Cylinder028
  Angle = 360
  AttacherType = Attacher::AttachEngine3D
  Height = 20
  Placement = pos=(0,0,36.15) rot=(0,0,1;0rad)
  Radius = 14.3
FEATURE [Part::Cylinder] Cylinder029
  Angle = 360
  AttacherType = Attacher::AttachEngine3D
  Height = 10
  Placement = pos=(0,0,36.15) rot=(0,0,1;0rad)
  Radius = 4
FEATURE [Part::MultiFuse] Fusion071  label="removeToCreteHoleForPlugHousing014"
  Placement = pos=(70,19,36) rot=(0,1,0;1.5708rad)
  Shapes = -> [Cylinder028,Cylinder029]
FEATURE [Sketcher::SketchObject] Sketch049  label="topSketch011"
  FullyConstrained = true
  sketch-geometry (4):
    g0: ArcOfCircle CenterX=105 CenterY=19 CenterZ=0 NormalX=0 NormalY=0 NormalZ=1 AngleXU=0 Radius=20.6155 StartAngle=5.54125 EndAngle=6.28319
    g1: ArcOfCircle CenterX=105 CenterY=19 CenterZ=0 NormalX=0 NormalY=0 NormalZ=1 AngleXU=0 Radius=13 StartAngle=5.54125 EndAngle=6.28319
    g2: LineSegment StartX=118 StartY=19 StartZ=0 EndX=125.616 EndY=19 EndZ=0
    g3: LineSegment StartX=114.583 StartY=10.2157 StartZ=0 EndX=120.197 EndY=5.06982 EndZ=0
  constraints (7):
    c: Block(g0)
    c: Block(g1)
    c: Coincident(g2,g1)
    c: Coincident(g2,g0)
    c: Horizontal(g2)
    c: Coincident(g3,g1)
    c: Coincident(g3,g0)
FEATURE [Part::Box] Box020  label="removeToCreteHoleForPlugHousing015"
  AttacherType = Attacher::AttachEngine3D
  Height = 28.6
  Length = 20
  Placement = pos=(106.15,0,21.7) rot=(0,0,1;0rad)
  Width = 19
FEATURE [Part::MultiFuse] Fusion072  label="removeToCreteHoleForPlugHousing016"
  Shapes = -> [Box020,Fusion071]
FEATURE [Part::Cut] Cut033  label="removeToCreteHoleForPlugHousing017"
  Base = -> Cut032
  Tool = -> Fusion072
FEATURE [Part::Cylinder] Cylinder030
  Angle = 360
  AttacherType = Attacher::AttachEngine3D
  Height = 20
  Placement = pos=(0,0,36.15) rot=(0,0,1;0rad)
  Radius = 14.3
FEATURE [Part::Cylinder] Cylinder031
  Angle = 360
  AttacherType = Attacher::AttachEngine3D
  Height = 10
  Placement = pos=(0,0,36.15) rot=(0,0,1;0rad)
  Radius = 4
FEATURE [Part::Box] Box021  label="removeToCreteHoleForPlugHousing019"
  AttacherType = Attacher::AttachEngine3D
  Height = 28.6
  Length = 20
  Placement = pos=(106.15,0,21.7) rot=(0,0,1;0rad)
  Width = 19
FEATURE [Part::MultiFuse] Fusion074  label="removeToCreteHoleForPlugHousing020"
  Placement = pos=(70,19,36) rot=(0,1,0;1.5708rad)
  Shapes = -> [Cylinder030,Cylinder031]
FEATURE [Part::MultiFuse] Fusion073  label="removeToCreteHoleForPlugHousing018"
  Placement = pos=(0,0,28.3) rot=(0,0,1;0rad)
  Shapes = -> [Box021,Fusion074]
FEATURE [Part::Cylinder] Cylinder032
  Angle = 360
  AttacherType = Attacher::AttachEngine3D
  Height = 20
  Placement = pos=(0,0,36.15) rot=(0,0,1;0rad)
  Radius = 14.3
FEATURE [Part::Cylinder] Cylinder033
  Angle = 360
  AttacherType = Attacher::AttachEngine3D
  Height = 10
  Placement = pos=(0,0,36.15) rot=(0,0,1;0rad)
  Radius = 4
FEATURE [Part::Box] Box022  label="removeToCreteHoleForPlugHousing021"
  AttacherType = Attacher::AttachEngine3D
  Height = 28.6
  Length = 20
  Placement = pos=(106.15,0,21.7) rot=(0,0,1;0rad)
  Width = 19
FEATURE [Part::MultiFuse] Fusion076  label="removeToCreteHoleForPlugHousing023"
  Placement = pos=(70,19,36) rot=(0,1,0;1.5708rad)
  Shapes = -> [Cylinder032,Cylinder033]
FEATURE [Part::MultiFuse] Fusion075  label="removeToCreteHoleForPlugHousing022"
  Placement = pos=(0,0,-28.3) rot=(0,0,1;0rad)
  Shapes = -> [Box022,Fusion076]
FEATURE [Part::MultiFuse] Fusion077  label="removeToCreatePlugHousingBottomBit"
  Shapes = -> [Fusion075,Fusion073]
FEATURE [Part::Cylinder] Cylinder034
  Angle = 360
  AttacherType = Attacher::AttachEngine3D
  Height = 20
  Placement = pos=(0,0,36.15) rot=(0,0,1;0rad)
  Radius = 14
FEATURE [Part::Cylinder] Cylinder035
  Angle = 360
  AttacherType = Attacher::AttachEngine3D
  Height = 10
  Placement = pos=(0,0,36.15) rot=(0,0,1;0rad)
  Radius = 4
FEATURE [Part::MultiFuse] Fusion078  label="removeToCreteHoleForPlugHousing024"
  Placement = pos=(70,19,36) rot=(0,1,0;1.5708rad)
  Shapes = -> [Cylinder034,Cylinder035]
FEATURE [Part::MultiFuse] Fusion079  label="removeToCreatePlugHousingBottomBit001"
  Shapes = -> [Fusion078,Fusion077]
FEATURE [Part::Extrusion] Extrude040  label="bottomPlugHousingBit"
  Base = -> Sketch049
  Dir = (0,0,1)
  DirMode = 2
  FaceMakerClass = Part::FaceMakerBullseye
  LengthFwd = 72
  LengthRev = 0
  Solid = true
  Symmetric = false
FEATURE [Part::Cut] Cut034  label="bottomPlugHousingBit001"
  Base = -> Extrude040
  Placement = pos=(-0.09,0,0) rot=(0,0,1;0rad)
  Tool = -> Fusion079
FEATURE [Part::Box] Box023  label="Cube014"
  AttacherType = Attacher::AttachEngine3D
  Height = 16
  Length = 8
  Placement = pos=(12.7,31.52,28) rot=(0,0,1;0rad)
  Width = 4
FEATURE [Part::Cylinder] Cylinder036
  Angle = 360
  AttacherType = Attacher::AttachEngine3D
  Height = 10
  Placement = pos=(0,0,36.15) rot=(0,0,1;0rad)
  Radius = 4
FEATURE [Part::Cylinder] Cylinder037
  Angle = 360
  AttacherType = Attacher::AttachEngine3D
  Height = 20
  Placement = pos=(0,0,36.15) rot=(0,0,1;0rad)
  Radius = 8.2
FEATURE [Part::MultiFuse] Fusion080  label="removeToCreteHoleForPlugHousing025"
  Placement = pos=(-42,19,36) rot=(0,1,0;1.5708rad)
  Shapes = -> [Cylinder037,Cylinder036]
FEATURE [Sketcher::SketchObject] Sketch050  label="topSketch012"
  FullyConstrained = true
  sketch-geometry (4):
    g0: LineSegment StartX=16.8446 StartY=31.512 StartZ=0 EndX=16.3251 EndY=34.4666 EndZ=0
    g1: ArcOfCircle CenterX=19 CenterY=19.2524 CenterZ=0 NormalX=0 NormalY=0 NormalZ=1 AngleXU=0 Radius=15.4476 StartAngle=1.74483 EndAngle=2.72717
    g2: ArcOfCircle CenterX=19 CenterY=19.2524 CenterZ=0 NormalX=0 NormalY=0 NormalZ=1 AngleXU=0 Radius=12.4476 StartAngle=1.74483 EndAngle=2.73189
    g3: LineSegment StartX=4.86004 StartY=25.4725 StartZ=0 EndX=7.58253 EndY=24.2107 EndZ=0
  constraints (7):
    c: Block(g0)
    c: Coincident(g1,g0)
    c: Coincident(g2,g0)
    c: Coincident(g3,g1)
    c: Coincident(g3,g2)
    c: Block(g1)
    c: Block(g2)
FEATURE [Part::Extrusion] Extrude041
  Base = -> Sketch050
  Dir = (0,0,1)
  DirMode = 2
  FaceMakerClass = Part::FaceMakerBullseye
  LengthFwd = 10.6
  LengthRev = 0
  Placement = pos=(0,0,31) rot=(0,0,1;0rad)
  Solid = true
  Symmetric = false
FEATURE [Part::Cut] Cut035
  Base = -> Extrude041
  Placement = pos=(0,0,-0.3) rot=(0,0,1;0rad)
  Tool = -> Fusion080
FEATURE [Part::Cut] Cut036
  Base = -> Box023
  Tool = -> Cut035
FEATURE [Part::Fillet] Fillet027
  Base = -> Cut036
  Edges = 1 edges r=0.7: [Edge13]
FEATURE [Part::Fillet] Fillet028
  Base = -> Fillet027
  Edges = 1 edges r=0.7: [Edge13]
FEATURE [Part::Fillet] Fillet029
  Base = -> Fillet028
  Edges = 1 edges r=0.7: [Edge16]
FEATURE [Part::Fillet] Fillet030
  Base = -> Fillet029
  Edges = 1 edges r=0.7: [Edge11]
FEATURE [Part::Fillet] Fillet031
  Base = -> Fillet030
  Edges = 1 edges r=0.7: [Edge10]
FEATURE [Part::Fillet] Fillet032
  Base = -> Fillet031
  Edges = 1 edges r=1.2: [Edge5]
FEATURE [Part::Fillet] Fillet033
  Base = -> Fillet032
  Edges = 1 edges r=1.2: [Edge12]
FEATURE [Part::Fillet] Fillet034  label="wireHousingRetainer"
  Base = -> Fillet033
  Edges = 1 edges r=2: [Edge1]
  Placement = pos=(0.3,0,0) rot=(0,0,1;0rad)
FEATURE [Part::Feature] Face099
  shape: bbox 3.5 x 17.8 x 2e-07 mm, 1 faces, 0 solids (baked)
FEATURE [Part::Revolution] Revolve107  label="removeToCreateScrewAndThreadedInsertHole034"
  Angle = 360
  Axis = (0,1,0)
  Base = (0,0,0)
  FaceMakerClass = Part::FaceMakerBullseye
  Placement = pos=(12.5,0,10) rot=(0,0,1;0rad)
  Solid = false
  Source = -> Face099
  Symmetric = false
FEATURE [Part::Feature] Face100
  shape: bbox 3.5 x 17.8 x 2e-07 mm, 1 faces, 0 solids (baked)
FEATURE [Part::Revolution] Revolve108  label="removeToCreateScrewAndThreadedInsertHole035"
  Angle = 360
  Axis = (0,1,0)
  Base = (0,0,0)
  FaceMakerClass = Part::FaceMakerBullseye
  Placement = pos=(12.5,0,62) rot=(0,0,1;0rad)
  Solid = false
  Source = -> Face100
  Symmetric = false
FEATURE [Part::Feature] Face101
  shape: bbox 3.5 x 17.8 x 2e-07 mm, 1 faces, 0 solids (baked)
FEATURE [Part::Revolution] Revolve109  label="removeToCreateScrewAndThreadedInsertHole036"
  Angle = 360
  Axis = (0,1,0)
  Base = (0,0,0)
  FaceMakerClass = Part::FaceMakerBullseye
  Placement = pos=(89.5,0,68.5) rot=(0,0,1;0rad)
  Solid = false
  Source = -> Face101
  Symmetric = false
FEATURE [Part::Feature] Face102
  shape: bbox 3.5 x 17.8 x 2e-07 mm, 1 faces, 0 solids (baked)
FEATURE [Part::Revolution] Revolve110  label="removeToCreateScrewAndThreadedInsertHole037"
  Angle = 360
  Axis = (0,1,0)
  Base = (0,0,0)
  FaceMakerClass = Part::FaceMakerBullseye
  Placement = pos=(89.5,0,3.5) rot=(0,0,1;0rad)
  Solid = false
  Source = -> Face102
  Symmetric = false
FEATURE [Part::Feature] Face103
  shape: bbox 3.5 x 17.8 x 2e-07 mm, 1 faces, 0 solids (baked)
FEATURE [Part::Revolution] Revolve111  label="removeToCreateScrewAndThreadedInsertHole038"
  Angle = 360
  Axis = (0,1,0)
  Base = (0,0,0)
  FaceMakerClass = Part::FaceMakerBullseye
  Placement = pos=(109.5,4.7,3.5) rot=(0,0,1;0rad)
  Solid = false
  Source = -> Face103
  Symmetric = false
FEATURE [Part::Feature] Face104
  shape: bbox 3.5 x 17.8 x 2e-07 mm, 1 faces, 0 solids (baked)
FEATURE [Part::Revolution] Revolve112  label="removeToCreateScrewAndThreadedInsertHole039"
  Angle = 360
  Axis = (0,1,0)
  Base = (0,0,0)
  FaceMakerClass = Part::FaceMakerBullseye
  Placement = pos=(109.5,4.7,68.5) rot=(0,0,1;0rad)
  Solid = false
  Source = -> Face104
  Symmetric = false
FEATURE [Part::MultiFuse] Fusion081  label="removeToCreateScrewAndThreadedInsertHole040"
  Shapes = -> [Revolve107,Revolve108,Revolve109,Revolve110,Revolve111,Revolve112]
FEATURE [Part::MultiFuse] Fusion082  label="casePillars002"
  Shapes = -> [Revolve094,Revolve092,Revolve090,Revolve089,Revolve091,Revolve093]
FEATURE [Part::Cut] Cut037  label="casePillars003"
  Base = -> Fusion082
  Tool = -> Fusion081
FEATURE [Sketcher::SketchObject] Sketch051
  FullyConstrained = true
  Placement = pos=(117,19,0) rot=(0.57735,0.57735,0.57735;2.0944rad)
  sketch-geometry (48):
    g0: LineSegment StartX=-49.19 StartY=69.25 StartZ=0 EndX=-49.19 EndY=66.25 EndZ=0
    g1: LineSegment StartX=-49.19 StartY=63.5 StartZ=0 EndX=-49.19 EndY=60.5 EndZ=0
    g2: LineSegment StartX=-49.19 StartY=57.75 StartZ=0 EndX=-49.19 EndY=54.75 EndZ=0
    g3: LineSegment StartX=-49.19 StartY=52 StartZ=0 EndX=-49.19 EndY=49 EndZ=0
    g4: LineSegment StartX=-49.19 StartY=46.25 StartZ=0 EndX=-49.19 EndY=43.25 EndZ=0
    g5: LineSegment StartX=-49.19 StartY=40.5 StartZ=0 EndX=-49.19 EndY=37.5 EndZ=0
    g6: LineSegment StartX=-49.19 StartY=34.5 StartZ=0 EndX=-49.19 EndY=31.5 EndZ=0
    g7: LineSegment StartX=-49.19 StartY=28.75 StartZ=0 EndX=-49.19 EndY=25.75 EndZ=0
    g8: LineSegment StartX=-49.19 StartY=23 StartZ=0 EndX=-49.19 EndY=20 EndZ=0
    g9: LineSegment StartX=-49.19 StartY=17.25 StartZ=0 EndX=-49.19 EndY=14.25 EndZ=0
    g10: LineSegment StartX=-49.19 StartY=11.5 StartZ=0 EndX=-49.19 EndY=8.5 EndZ=0
    g11: LineSegment StartX=-49.19 StartY=5.75 StartZ=0 EndX=-49.19 EndY=2.75 EndZ=0
    g12: ArcOfCircle CenterX=-1.5 CenterY=67.75 CenterZ=0 NormalX=0 NormalY=0 NormalZ=1 AngleXU=0 Radius=1.5 StartAngle=4.71239 EndAngle=7.85398
    g13: ArcOfCircle CenterX=-1.5 CenterY=62 CenterZ=0 NormalX=0 NormalY=0 NormalZ=1 AngleXU=0 Radius=1.5 StartAngle=4.71239 EndAngle=7.85398
    g14: ArcOfCircle CenterX=-1.5 CenterY=56.25 CenterZ=0 NormalX=0 NormalY=0 NormalZ=1 AngleXU=0 Radius=1.5 StartAngle=4.71239 EndAngle=7.85398
    g15: ArcOfCircle CenterX=-11.49 CenterY=50.5 CenterZ=0 NormalX=0 NormalY=0 NormalZ=1 AngleXU=0 Radius=1.5 StartAngle=4.71239 EndAngle=7.85398
    g16: ArcOfCircle CenterX=-16.28 CenterY=44.75 CenterZ=0 NormalX=0 NormalY=0 NormalZ=1 AngleXU=0 Radius=1.5 StartAngle=4.71239 EndAngle=7.85398
    g17: ArcOfCircle CenterX=-18.2337 CenterY=39 CenterZ=0 NormalX=0 NormalY=0 NormalZ=1 AngleXU=0 Radius=1.5 StartAngle=4.71485 EndAngle=7.85398
    g18: ArcOfCircle CenterX=-16.2837 CenterY=27.25 CenterZ=0 NormalX=0 NormalY=0 NormalZ=1 AngleXU=0 Radius=1.5 StartAngle=4.71485 EndAngle=7.85398
    g19: ArcOfCircle CenterX=-18.2337 CenterY=33 CenterZ=0 NormalX=0 NormalY=0 NormalZ=1 AngleXU=0 Radius=1.5 StartAngle=4.71485 EndAngle=7.85398
    g20: ArcOfCircle CenterX=-11.49 CenterY=21.5 CenterZ=0 NormalX=0 NormalY=0 NormalZ=1 AngleXU=0 Radius=1.5 StartAngle=4.71239 EndAngle=7.85398
    g21: ArcOfCircle CenterX=-1.5 CenterY=4.25 CenterZ=0 NormalX=0 NormalY=0 NormalZ=1 AngleXU=0 Radius=1.5 StartAngle=4.71239 EndAngle=7.85398
    g22: ArcOfCircle CenterX=-1.5 CenterY=10 CenterZ=0 NormalX=0 NormalY=0 NormalZ=1 AngleXU=0 Radius=1.5 StartAngle=4.71239 EndAngle=7.85398
    g23: ArcOfCircle CenterX=-1.5 CenterY=15.75 CenterZ=0 NormalX=0 NormalY=0 NormalZ=1 AngleXU=0 Radius=1.5 StartAngle=4.71239 EndAngle=7.85398
    g24: LineSegment StartX=-49.19 StartY=69.25 StartZ=0 EndX=-1.5 EndY=69.25 EndZ=0
    g25: LineSegment StartX=-49.19 StartY=66.25 StartZ=0 EndX=-1.5 EndY=66.25 EndZ=0
    g26: LineSegment StartX=-49.19 StartY=63.5 StartZ=0 EndX=-1.5 EndY=63.5 EndZ=0
    g27: LineSegment StartX=-49.19 StartY=60.5 StartZ=0 EndX=-1.5 EndY=60.5 EndZ=0
    g28: LineSegment StartX=-49.19 StartY=57.75 StartZ=0 EndX=-1.5 EndY=57.75 EndZ=0
    g29: LineSegment StartX=-49.19 StartY=54.75 StartZ=0 EndX=-1.5 EndY=54.75 EndZ=0
    g30: LineSegment StartX=-49.19 StartY=52 StartZ=0 EndX=-11.49 EndY=52 EndZ=0
    g31: LineSegment StartX=-49.19 StartY=49 StartZ=0 EndX=-11.49 EndY=49 EndZ=0
    g32: LineSegment StartX=-49.19 StartY=46.25 StartZ=0 EndX=-16.28 EndY=46.25 EndZ=0
    g33: LineSegment StartX=-49.19 StartY=43.25 StartZ=0 EndX=-16.28 EndY=43.25 EndZ=0
    g34: LineSegment StartX=-49.19 StartY=40.5 StartZ=0 EndX=-18.2337 EndY=40.5 EndZ=0
    g35: LineSegment StartX=-49.19 StartY=37.5 StartZ=0 EndX=-18.23 EndY=37.5 EndZ=0
    g36: LineSegment StartX=-49.19 StartY=34.5 StartZ=0 EndX=-18.2337 EndY=34.5 EndZ=0
    g37: LineSegment StartX=-49.19 StartY=31.5 StartZ=0 EndX=-18.23 EndY=31.5 EndZ=0
    g38: LineSegment StartX=-49.19 StartY=28.75 StartZ=0 EndX=-16.2837 EndY=28.75 EndZ=0
    g39: LineSegment StartX=-49.19 StartY=25.75 StartZ=0 EndX=-16.28 EndY=25.75 EndZ=0
    g40: LineSegment StartX=-49.19 StartY=23 StartZ=0 EndX=-11.49 EndY=23 EndZ=0
    g41: LineSegment StartX=-49.19 StartY=20 StartZ=0 EndX=-11.49 EndY=20 EndZ=0
    g42: LineSegment StartX=-49.19 StartY=17.25 StartZ=0 EndX=-1.5 EndY=17.25 EndZ=0
    g43: LineSegment StartX=-49.19 StartY=14.25 StartZ=0 EndX=-1.5 EndY=14.25 EndZ=0
    g44: LineSegment StartX=-49.19 StartY=11.5 StartZ=0 EndX=-1.5 EndY=11.5 EndZ=0
    g45: LineSegment StartX=-49.19 StartY=8.5 StartZ=0 EndX=-1.5 EndY=8.5 EndZ=0
    g46: LineSegment StartX=-49.19 StartY=5.75 StartZ=0 EndX=-1.5 EndY=5.75 EndZ=0
    g47: LineSegment StartX=-49.19 StartY=2.75 StartZ=0 EndX=-1.5 EndY=2.75 EndZ=0
  constraints (120):
    c: Vertical(g0)
    c: Distance(g0) = 3
    c: Block(g0)
    c: Vertical(g1)
    c: Distance(g1) = 3
    c: Vertical(g2)
    c: Equal(g0,g2) = 3
    c: Block(g2)
    c: Vertical(g3)
    c: Equal(g1,g3) = 3
    c: Vertical(g4)
    c: Equal(g0,g4) = 3
    c: Block(g4)
    c: Vertical(g5)
    c: Equal(g1,g5) = 3
    c: Vertical(g6)
    c: Equal(g0,g6) = 3
    c: Block(g6)
    c: Vertical(g7)
    c: Equal(g1,g7) = 3
    c: Vertical(g8)
    c: Equal(g0,g8) = 3
    c: Block(g8)
    c: Vertical(g9)
    c: Equal(g1,g9) = 3
    c: Vertical(g10)
    c: Equal(g0,g10) = 3
    c: Block(g10)
    c: Vertical(g11)
    c: Equal(g1,g11) = 3
    c: Block(g12)
    c: Block(g13)
    c: Block(g14)
    c: Block(g15)
    c: Block(g16)
    c: Block(g17)
    c: Block(g18)
    c: Block(g19)
    c: Block(g20)
    c: Block(g21)
    c: Block(g22)
    c: Block(g23)
    c: Block(g11)
    c: Block(g9)
    c: Block(g7)
    c: Block(g5)
    c: Block(g3)
    c: Block(g1)
    c: Coincident(g24,g0)
    c: Coincident(g24,g12)
    c: Horizontal(g24)
    c: Coincident(g25,g0)
    c: Coincident(g25,g12)
    c: Horizontal(g25)
    c: Coincident(g26,g1)
    c: Coincident(g26,g13)
    c: Horizontal(g26)
    c: Coincident(g27,g1)
    c: Coincident(g27,g13)
    c: Horizontal(g27)
    c: Coincident(g28,g2)
    c: Coincident(g28,g14)
    c: Horizontal(g28)
    c: Coincident(g29,g2)
    c: Coincident(g29,g14)
    c: Horizontal(g29)
    c: Coincident(g30,g3)
    c: Coincident(g30,g15)
    c: Horizontal(g30)
    c: Coincident(g31,g3)
    c: Coincident(g31,g15)
    c: Horizontal(g31)
    c: Coincident(g32,g4)
    c: Coincident(g32,g16)
    c: Horizontal(g32)
    c: Coincident(g33,g4)
    c: Coincident(g33,g16)
    c: Horizontal(g33)
    c: Coincident(g34,g5)
    c: Coincident(g34,g17)
    c: Horizontal(g34)
    c: Coincident(g35,g5)
    c: Coincident(g35,g17)
    c: Horizontal(g35)
    c: Coincident(g36,g6)
    c: Coincident(g36,g19)
    c: Horizontal(g36)
    c: Coincident(g37,g6)
    c: Coincident(g37,g19)
    c: Horizontal(g37)
    c: Coincident(g38,g7)
    c: Coincident(g38,g18)
    c: Horizontal(g38)
    c: Coincident(g39,g7)
    c: Coincident(g39,g18)
    c: Horizontal(g39)
    c: Coincident(g40,g8)
    c: Coincident(g40,g20)
    c: Horizontal(g40)
    c: Coincident(g41,g8)
    c: Coincident(g41,g20)
    c: Horizontal(g41)
    c: Coincident(g42,g9)
    c: Coincident(g42,g23)
    c: Horizontal(g42)
    c: Coincident(g43,g9)
    c: Coincident(g43,g23)
    c: Horizontal(g43)
    c: Coincident(g44,g10)
    c: Coincident(g44,g22)
    c: Horizontal(g44)
    c: Coincident(g45,g10)
    c: Coincident(g45,g22)
    c: Horizontal(g45)
    c: Coincident(g46,g11)
    c: Coincident(g46,g21)
    c: Horizontal(g46)
    c: Coincident(g47,g11)
    c: Coincident(g47,g21)
    c: Horizontal(g47)
FEATURE [Part::Extrusion] Extrude042
  Base = -> Sketch051
  Dir = (1,-2e-16,2e-16)
  DirMode = 2
  FaceMakerClass = Part::FaceMakerBullseye
  LengthFwd = 19
  LengthRev = 0
  Placement = pos=(-19,0,0) rot=(0,0,1;0rad)
  Solid = true
  Symmetric = false
FEATURE [Part::Fillet] Fillet035  label="removeToCreateVentalationHoles"
  Base = -> Extrude042
  Edges = <same value as first occurrence — deduplicated (x6 in doc)>
  Placement = pos=(7,0,0) rot=(0,0,1;0rad)
FEATURE [Part::Cut] Cut038  label="top017"
  Base = -> Cut033
  Tool = -> Fillet035
FEATURE [Sketcher::SketchObject] Sketch052  label="bottomSketch001"
  FullyConstrained = true
  sketch-geometry (45):
    g0: LineSegment StartX=6.29999 StartY=8 StartZ=0 EndX=3.29999 EndY=8 EndZ=0
    g1: LineSegment StartX=3.29999 StartY=8 StartZ=0 EndX=3.29999 EndY=-6.03275e-07 EndZ=0
    g2: ArcOfCircle CenterX=8.29999 CenterY=5 CenterZ=0 NormalX=0 NormalY=0 NormalZ=1 AngleXU=0 Radius=2 StartAngle=3.14159 EndAngle=4.71239
    g3: LineSegment StartX=6.29999 StartY=8 StartZ=0 EndX=6.29999 EndY=5 EndZ=0
    g4: ArcOfCircle CenterX=105 CenterY=19 CenterZ=0 NormalX=0 NormalY=0 NormalZ=1 AngleXU=0 Radius=12.7 StartAngle=4.71239 EndAngle=5.94289
    g5-g11: Circle x7 (B-spline internal-alignment scaffolding for g12; pole/knot coordinates omitted)
    g12: BSplineCurve PolesCount=7 KnotsCount=5 Degree=3 IsPeriodic=0
    g13-g17: GeomPoint x5 (B-spline internal-alignment scaffolding for g12; pole/knot coordinates omitted)
    g18: ArcOfCircle CenterX=105 CenterY=19 CenterZ=0 NormalX=0 NormalY=0 NormalZ=1 AngleXU=0 Radius=15.7 StartAngle=5.81226 EndAngle=6.28319
    g19: BSplineCurve PolesCount=5 KnotsCount=3 Degree=3 IsPeriodic=0
    g20: LineSegment StartX=8.29999 StartY=3 StartZ=0 EndX=101.7 EndY=3 EndZ=0
    g21: LineSegment StartX=3.29999 StartY=-6.03275e-07 StartZ=0 EndX=105 EndY=-6.03275e-07 EndZ=0
    g22: LineSegment StartX=120.974 StartY=8.71251 StartZ=0 EndX=122.332 EndY=7.83778 EndZ=0
    g23: LineSegment StartX=105 StartY=-6.03274e-07 StartZ=0 EndX=113 EndY=-6.03274e-07 EndZ=0
    g24: ArcOfCircle CenterX=105 CenterY=19 CenterZ=0 NormalX=0 NormalY=0 NormalZ=1 AngleXU=0 Radius=20.6155 StartAngle=5.11091 EndAngle=5.71103
    g25: ArcOfCircle CenterX=117.7 CenterY=19 CenterZ=0 NormalX=0 NormalY=0 NormalZ=1 AngleXU=0 Radius=3 StartAngle=1.2e-15 EndAngle=2.10468
    g26: Circle CenterX=116.345 CenterY=16.3232 CenterZ=0 NormalX=0 NormalY=0 NormalZ=1 AngleXU=0 Radius=1
    g27: Circle CenterX=117.24 CenterY=15.7584 CenterZ=0 NormalX=0 NormalY=0 NormalZ=1 AngleXU=0 Radius=1
    g28: Circle CenterX=116.972 CenterY=14.7612 CenterZ=0 NormalX=0 NormalY=0 NormalZ=1 AngleXU=0 Radius=1
    g29: BSplineCurve PolesCount=3 KnotsCount=2 Degree=2 IsPeriodic=0
    g30: GeomPoint X=116.345 Y=16.3232 Z=0
    g31: GeomPoint X=116.972 Y=14.7612 Z=0
    g32: Circle CenterX=115.828 CenterY=17.157 CenterZ=0 NormalX=0 NormalY=0 NormalZ=1 AngleXU=0 Radius=1
    g33: Circle CenterX=115.841 CenterY=16.639 CenterZ=0 NormalX=0 NormalY=0 NormalZ=1 AngleXU=0 Radius=1
    g34: Circle CenterX=116.345 CenterY=16.3232 CenterZ=0 NormalX=0 NormalY=0 NormalZ=1 AngleXU=0 Radius=1
    g35: BSplineCurve PolesCount=3 KnotsCount=2 Degree=2 IsPeriodic=0
    g36: GeomPoint X=115.828 Y=17.157 Z=0
    g37: GeomPoint X=116.345 Y=16.3232 Z=0
    g38: LineSegment StartX=115.828 StartY=17.157 StartZ=0 EndX=115.828 EndY=20.8307 EndZ=0
    g39: Circle CenterX=115.828 CenterY=20.8307 CenterZ=0 NormalX=0 NormalY=0 NormalZ=1 AngleXU=0 Radius=1
    g40: Circle CenterX=115.831 CenterY=21.3396 CenterZ=0 NormalX=0 NormalY=0 NormalZ=1 AngleXU=0 Radius=1
    g41: Circle CenterX=116.173 CenterY=21.5825 CenterZ=0 NormalX=0 NormalY=0 NormalZ=1 AngleXU=0 Radius=1
    g42: BSplineCurve PolesCount=3 KnotsCount=2 Degree=2 IsPeriodic=0
    g43: GeomPoint X=115.828 Y=20.8307 Z=0
    g44: GeomPoint X=116.173 Y=21.5825 Z=0
  constraints (70):
    c: Horizontal(g0)
    c: Distance(g0) = 3
    c: Coincident(g1,g0)
    c: Vertical(g1)
    c: Block(g2)
    c: Block(g0)
    c: Coincident(g3,g0)
    c: Coincident(g3,g2)
    c: Vertical(g3)
    c: Block(g1)
    c: Block(g4)
    c: Coincident(g19,g4)
    c: Block(g19)
    c: Equal(g5, g6-g11) x6
    c: InternalAlignment(g5-g11 -> g12) x7
    c: InternalAlignment(g13-g17 -> g12) x5
    c: Block(g12)
    c: Coincident(g18,g12)
    c: Block(g18)
    c: Coincident(g20,g2)
    c: Coincident(g20,g19)
    c: Horizontal(g20)
    c: Distance(g20) = 93.4
    c: Coincident(g21,g1)
    c: Horizontal(g21)
    c: Distance(g21) = 101.7
    c: Horizontal(g23)
    c: Distance(g23) = 8
    c: Coincident(g24,g23)
    c: Block(g23)
    c: Coincident(g22,g24)
    c: Block(g24)
    c: Block(g22)
    c: Distance(g22) = 1.61553
    c: Coincident(g25,g18)
    c: Block(g25)
    c: Weight(g26) = 1
    c: Equal(g26,g27)
    c: Equal(g26,g28)
    c: Coincident(g29,g4)
    c: InternalAlignment(g26,g29)
    c: InternalAlignment(g27,g29)
    c: InternalAlignment(g28,g29)
    c: InternalAlignment(g30,g29)
    c: InternalAlignment(g31,g29)
    c: Block(g29)
    c: Weight(g32) = 1
    c: Equal(g32,g33)
    c: Equal(g32,g34)
    c: Coincident(g35,g29)
    c: InternalAlignment(g32,g35)
    c: InternalAlignment(g33,g35)
    c: InternalAlignment(g34,g35)
    c: InternalAlignment(g36,g35)
    c: InternalAlignment(g37,g35)
    c: Block(g35)
    c: Coincident(g38,g35)
    c: Vertical(g38)
    c: Block(g38)
    c: Coincident(g42,g38)
    c: Weight(g39) = 1
    c: Equal(g39,g40)
    c: Equal(g39,g41)
    c: Coincident(g42,g25)
    c: InternalAlignment(g39,g42)
    c: InternalAlignment(g40,g42)
    c: InternalAlignment(g41,g42)
    c: InternalAlignment(g43,g42)
    c: InternalAlignment(g44,g42)
    c: Block(g42)
FEATURE [Part::Extrusion] Extrude043  label="bottom010"
  Base = -> Sketch052
  Dir = (0,0,1)
  DirMode = 2
  FaceMakerClass = Part::FaceMakerBullseye
  LengthFwd = 71.4
  LengthRev = 0
  Placement = pos=(0,0,0.3) rot=(0,0,1;0rad)
  Solid = true
  Symmetric = false
FEATURE [Sketcher::SketchObject] Sketch053  label="topSketch013"
  FullyConstrained = true
  sketch-geometry (22):
    g0: LineSegment StartX=5.21097e-06 StartY=3 StartZ=0 EndX=5.21097e-06 EndY=19 EndZ=0
    g1: ArcOfCircle CenterX=19 CenterY=19 CenterZ=0 NormalX=0 NormalY=0 NormalZ=1 AngleXU=0 Radius=19 StartAngle=1.5708 EndAngle=3.14159
    g2: ArcOfCircle CenterX=19 CenterY=19 CenterZ=0 NormalX=0 NormalY=0 NormalZ=1 AngleXU=0 Radius=16 StartAngle=1.5708 EndAngle=3.14159
    g3: LineSegment StartX=114 StartY=35 StartZ=0 EndX=19 EndY=35 EndZ=0
    g4: LineSegment StartX=5.21097e-06 StartY=3 StartZ=0 EndX=5.21097e-06 EndY=0 EndZ=0
    g5: LineSegment StartX=3 StartY=0 StartZ=0 EndX=5.21097e-06 EndY=0 EndZ=0
    g6: LineSegment StartX=3 StartY=19 StartZ=0 EndX=3 EndY=0 EndZ=0
    g7: LineSegment StartX=19 StartY=38 StartZ=0 EndX=124 EndY=38 EndZ=0
    g8: Circle CenterX=119 CenterY=35 CenterZ=0 NormalX=0 NormalY=0 NormalZ=1 AngleXU=0 Radius=1
    g9: Circle CenterX=121 CenterY=35 CenterZ=0 NormalX=0 NormalY=0 NormalZ=1 AngleXU=0 Radius=1
    g10: Circle CenterX=121 CenterY=33 CenterZ=0 NormalX=0 NormalY=0 NormalZ=1 AngleXU=0 Radius=1
    g11: BSplineCurve PolesCount=3 KnotsCount=2 Degree=2 IsPeriodic=0
    g12: GeomPoint X=119 Y=35 Z=0
    g13: GeomPoint X=121 Y=33 Z=0
    g14: LineSegment StartX=119 StartY=35 StartZ=0 EndX=114 EndY=35 EndZ=0
    g15: ArcOfCircle CenterX=105 CenterY=19 CenterZ=0 NormalX=0 NormalY=0 NormalZ=1 AngleXU=0 Radius=16 StartAngle=5.60905 EndAngle=6.28319
    g16: LineSegment StartX=121 StartY=33 StartZ=0 EndX=121 EndY=19 EndZ=0
    g17: LineSegment StartX=117.5 StartY=9.01251 StartZ=0 EndX=121.163 EndY=9.0125 EndZ=0
    g18: ArcOfCircle CenterX=105 CenterY=19 CenterZ=0 NormalX=0 NormalY=0 NormalZ=1 AngleXU=0 Radius=20.6155 StartAngle=5.7297 EndAngle=6.28319
    g19: LineSegment StartX=121.163 StartY=9.0125 StartZ=0 EndX=122.538 EndY=8.16329 EndZ=0
    g20: LineSegment StartX=124 StartY=38 StartZ=0 EndX=125.616 EndY=38 EndZ=0
    g21: LineSegment StartX=125.616 StartY=19 StartZ=0 EndX=125.616 EndY=38 EndZ=0
  constraints (50):
    c: Vertical(g0)
    c: Block(g0)
    c: Coincident(g1,g0)
    c: Block(g1)
    c: Coincident(g2,g1)
    c: Block(g2)
    c: Coincident(g3,g2)
    c: Horizontal(g3)
    c: Tangent(g3,g2)
    c: Coincident(g4,g0)
    c: Distance(g4) = 3
    c: Vertical(g4)
    c: Coincident(g5,g4)
    c: Horizontal(g5)
    c: Coincident(g6,g2)
    c: Coincident(g6,g5)
    c: Vertical(g6)
    c: Horizontal(g7)
    c: Distance(g7) = 105
    c: Coincident(g7,g1)
    c: Block(g3)
    c: Weight(g8) = 1
    c: Equal(g8,g9)
    c: Equal(g8,g10)
    c: InternalAlignment(g8,g11)
    c: InternalAlignment(g9,g11)
    c: InternalAlignment(g10,g11)
    c: InternalAlignment(g12,g11)
    c: InternalAlignment(g13,g11)
    c: Block(g11)
    c: Coincident(g14,g11)
    c: Coincident(g14,g3)
    c: Horizontal(g14)
    c: Block(g15)
    c: Coincident(g16,g11)
    c: Coincident(g16,g15)
    c: Vertical(g16)
    c: Distance(g16) = 14
    c: Coincident(g17,g15)
    c: Block(g18)
    c: Coincident(g19,g18)
    c: Coincident(g20,g7)
    c: Horizontal(g20)
    c: Vertical(g21)
    c: Coincident(g20,g21)
    c: Block(g20)
    c: Block(g21)
    c: Block(g19)
    c: Block(g17)
    c: Distance(g20) = 1.61553
FEATURE [Part::Extrusion] Extrude044
  Base = -> Sketch053
  Dir = (0,0,1)
  DirMode = 2
  FaceMakerClass = Part::FaceMakerBullseye
  LengthFwd = 72
  LengthRev = 0
  Solid = true
  Symmetric = false
FEATURE [Part::Fillet] Fillet036  label="top018"
  Base = -> Extrude044
  Edges = 1 edges r=2: [Edge41]
FEATURE [Sketcher::SketchObject] Sketch054
  FullyConstrained = false
  Placement = pos=(0,0,0) rot=(1,0,0;1.5708rad)
  sketch-geometry (24):
    g0: ArcOfCircle CenterX=-4 CenterY=-10.5 CenterZ=0 NormalX=0 NormalY=0 NormalZ=1 AngleXU=0 Radius=1.5 StartAngle=6e-16 EndAngle=3.14159
    g1: ArcOfCircle CenterX=-34.2 CenterY=-10.5 CenterZ=0 NormalX=0 NormalY=0 NormalZ=1 AngleXU=0 Radius=1.5 StartAngle=0 EndAngle=3.14159
    g2: ArcOfCircle CenterX=-34.2 CenterY=-27.7 CenterZ=0 NormalX=0 NormalY=0 NormalZ=1 AngleXU=0 Radius=1.5 StartAngle=3.14159 EndAngle=6.28319
    g3: ArcOfCircle CenterX=-4 CenterY=-27.7 CenterZ=0 NormalX=0 NormalY=0 NormalZ=1 AngleXU=0 Radius=1.5 StartAngle=3.1416 EndAngle=6.28319
    g4: ArcOfCircle CenterX=-10 CenterY=-4.3 CenterZ=0 NormalX=0 NormalY=0 NormalZ=1 AngleXU=0 Radius=1.5 StartAngle=2e-16 EndAngle=3.14159
    g5: ArcOfCircle CenterX=-16.1 CenterY=-1.8 CenterZ=0 NormalX=0 NormalY=0 NormalZ=1 AngleXU=0 Radius=1.5 StartAngle=5e-16 EndAngle=3.14159
    g6: ArcOfCircle CenterX=-22.1 CenterY=-1.8 CenterZ=0 NormalX=0 NormalY=0 NormalZ=1 AngleXU=0 Radius=1.5 StartAngle=5e-16 EndAngle=3.14159
    g7: ArcOfCircle CenterX=-28.2 CenterY=-4.3 CenterZ=0 NormalX=0 NormalY=0 NormalZ=1 AngleXU=0 Radius=1.5 StartAngle=2e-16 EndAngle=3.14159
    g8: ArcOfCircle CenterX=-10 CenterY=-33.9 CenterZ=0 NormalX=0 NormalY=0 NormalZ=1 AngleXU=0 Radius=1.5 StartAngle=3.14159 EndAngle=6.28319
    g9: ArcOfCircle CenterX=-16.1 CenterY=-36.4 CenterZ=0 NormalX=0 NormalY=0 NormalZ=1 AngleXU=0 Radius=1.5 StartAngle=3.14159 EndAngle=6.28319
    g10: ArcOfCircle CenterX=-22.1 CenterY=-36.4 CenterZ=0 NormalX=0 NormalY=0 NormalZ=1 AngleXU=0 Radius=1.5 StartAngle=3.14159 EndAngle=6.28319
    g11: ArcOfCircle CenterX=-28.2 CenterY=-33.9 CenterZ=0 NormalX=0 NormalY=0 NormalZ=1 AngleXU=0 Radius=1.5 StartAngle=3.14159 EndAngle=6.28319
    g12: LineSegment StartX=-35.7 StartY=-10.5 StartZ=0 EndX=-35.7 EndY=-27.7 EndZ=0
    g13: LineSegment StartX=-32.7 StartY=-10.5 StartZ=0 EndX=-32.7 EndY=-27.7 EndZ=0
    g14: LineSegment StartX=-29.7 StartY=-33.9 StartZ=0 EndX=-29.7 EndY=-4.3 EndZ=0
    g15: LineSegment StartX=-26.7 StartY=-33.9 StartZ=0 EndX=-26.7 EndY=-4.3 EndZ=0
    g16: LineSegment StartX=-2.5 StartY=-10.5 StartZ=0 EndX=-2.5 EndY=-27.7 EndZ=0
    g17: LineSegment StartX=-8.5 StartY=-4.3 StartZ=0 EndX=-8.5 EndY=-33.9 EndZ=0
    g18: LineSegment StartX=-5.5 StartY=-10.5 StartZ=0 EndX=-5.5 EndY=-27.7 EndZ=0
    g19: LineSegment StartX=-11.5 StartY=-4.3 StartZ=0 EndX=-11.5 EndY=-33.9 EndZ=0
    g20: LineSegment StartX=-14.6 StartY=-1.8 StartZ=0 EndX=-14.6 EndY=-36.4 EndZ=0
    g21: LineSegment StartX=-17.6 StartY=-1.8 StartZ=0 EndX=-17.6 EndY=-36.4 EndZ=0
    g22: LineSegment StartX=-20.6 StartY=-36.4 StartZ=0 EndX=-20.6 EndY=-1.8 EndZ=0
    g23: LineSegment StartX=-23.6 StartY=-1.8 StartZ=0 EndX=-23.6 EndY=-36.4 EndZ=0
  constraints (48):
    c: Block(g0)
    c: Block(g1)
    c: Block(g2)
    c: Block(g3)
    c: Block(g4)
    c: Block(g5)
    c: Block(g6)
    c: Block(g7)
    c: Block(g8)
    c: Block(g9)
    c: Block(g10)
    c: Block(g11)
    c: Coincident(g12,g1)
    c: Coincident(g12,g2)
    c: Vertical(g12)
    c: Coincident(g13,g1)
    c: Coincident(g13,g2)
    c: Vertical(g13)
    c: Coincident(g14,g11)
    c: Coincident(g14,g7)
    c: Vertical(g14)
    c: Coincident(g15,g11)
    c: Coincident(g15,g7)
    c: Vertical(g15)
    c: Coincident(g16,g0)
    c: Coincident(g16,g3)
    c: Vertical(g16)
    c: Coincident(g17,g4)
    c: Coincident(g17,g8)
    c: Vertical(g17)
    c: Coincident(g18,g0)
    c: Coincident(g18,g3)
    c: Vertical(g18)
    c: Coincident(g19,g4)
    c: Coincident(g19,g8)
    c: Vertical(g19)
    c: Coincident(g20,g5)
    c: Coincident(g20,g9)
    c: Vertical(g20)
    c: Coincident(g21,g5)
    c: Coincident(g21,g9)
    c: Vertical(g21)
    c: Coincident(g22,g10)
    c: Coincident(g22,g6)
    c: Vertical(g22)
    c: Coincident(g23,g6)
    c: Coincident(g23,g10)
    c: Vertical(g23)
FEATURE [Part::Extrusion] Extrude045  label="removeToCreateFanGrillHoles003"
  Base = -> Sketch054
  Dir = (0,-1,6e-16)
  DirMode = 2
  FaceMakerClass = Part::FaceMakerBullseye
  LengthFwd = 10
  LengthRev = 0
  Placement = pos=(65.4,44,54.82) rot=(0,0,1;0rad)
  Solid = true
  Symmetric = false
FEATURE [Part::Feature] Face105 .. Face108  x4 (patterned run collapsed; names and placements below)
  shape: bbox 3.5 x 17.8 x 2e-07 mm, 1 faces, 0 solids (baked)
FEATURE [Part::Revolution] Revolve113  label="removeToCreateScrewAndThreadedInsertHole041"
  Angle = 360
  Axis = (0,1,0)
  Base = (0,0,0)
  FaceMakerClass = Part::FaceMakerBullseye
  Placement = pos=(62.3,30.3,19.7) rot=(0,0,1;0rad)
  Solid = false
  Source = -> Face105
  Symmetric = false
FEATURE [Part::Revolution] Revolve114  label="removeToCreateScrewAndThreadedInsertHole042"
  Angle = 360
  Axis = (0,1,0)
  Base = (0,0,0)
  FaceMakerClass = Part::FaceMakerBullseye
  Placement = pos=(62.3,30.3,51.7) rot=(0,0,1;0rad)
  Solid = false
  Source = -> Face106
  Symmetric = false
FEATURE [Part::Revolution] Revolve115  label="removeToCreateScrewAndThreadedInsertHole043"
  Angle = 360
  Axis = (0,1,0)
  Base = (0,0,0)
  FaceMakerClass = Part::FaceMakerBullseye
  Placement = pos=(30.3,30.3,19.7) rot=(0,0,1;0rad)
  Solid = false
  Source = -> Face107
  Symmetric = false
FEATURE [Part::Revolution] Revolve116  label="removeToCreateScrewAndThreadedInsertHole044"
  Angle = 360
  Axis = (0,1,0)
  Base = (0,0,0)
  FaceMakerClass = Part::FaceMakerBullseye
  Placement = pos=(30.3,30.3,51.7) rot=(0,0,1;0rad)
  Solid = false
  Source = -> Face108
  Symmetric = false
FEATURE [Part::MultiFuse] Fusion083  label="createThreadedInsertHolesForFan004"
  Shapes = -> [Revolve113,Revolve114,Revolve115,Revolve116]
FEATURE [Part::Box] Box024  label="removeToCreteHoleForPlugHousing026"
  AttacherType = Attacher::AttachEngine3D
  Height = 28.6
  Length = 10
  Placement = pos=(-2,0,21.7) rot=(0,0,1;0rad)
  Width = 19
FEATURE [Part::Cylinder] Cylinder038  label="removeToCreteHoleForPlugHousing027"
  Angle = 360
  AttacherType = Attacher::AttachEngine3D
  Height = 20
  Placement = pos=(-2,19,36) rot=(0,1,0;1.5708rad)
  Radius = 14.3
FEATURE [Part::MultiFuse] Fusion084  label="removeToCreteHoleForPlugHousing028"
  Shapes = -> [Box024,Cylinder038]
FEATURE [Part::Cylinder] Cylinder039
  Angle = 360
  AttacherType = Attacher::AttachEngine3D
  Height = 20
  Placement = pos=(0,0,36.15) rot=(0,0,1;0rad)
  Radius = 14.3
FEATURE [Part::Cylinder] Cylinder040
  Angle = 360
  AttacherType = Attacher::AttachEngine3D
  Height = 10
  Placement = pos=(0,0,36.15) rot=(0,0,1;0rad)
  Radius = 4
FEATURE [Part::Box] Box025  label="removeToCreteHoleForPlugHousing030"
  AttacherType = Attacher::AttachEngine3D
  Height = 28.6
  Length = 20
  Placement = pos=(106.15,0,21.7) rot=(0,0,1;0rad)
  Width = 19
FEATURE [Part::MultiFuse] Fusion086  label="removeToCreteHoleForPlugHousing031"
  Placement = pos=(70,19,36) rot=(0,1,0;1.5708rad)
  Shapes = -> [Cylinder039,Cylinder040]
FEATURE [Part::MultiFuse] Fusion085  label="removeToCreteHoleForPlugHousing029"
  Shapes = -> [Box025,Fusion086]
FEATURE [Sketcher::SketchObject] Sketch055
  FullyConstrained = true
  Placement = pos=(117,19,0) rot=(0.57735,0.57735,0.57735;2.0944rad)
  sketch-geometry (48):
    g0: LineSegment StartX=-49.19 StartY=69.25 StartZ=0 EndX=-49.19 EndY=66.25 EndZ=0
    g1: LineSegment StartX=-49.19 StartY=63.5 StartZ=0 EndX=-49.19 EndY=60.5 EndZ=0
    g2: LineSegment StartX=-49.19 StartY=57.75 StartZ=0 EndX=-49.19 EndY=54.75 EndZ=0
    g3: LineSegment StartX=-49.19 StartY=52 StartZ=0 EndX=-49.19 EndY=49 EndZ=0
    g4: LineSegment StartX=-49.19 StartY=46.25 StartZ=0 EndX=-49.19 EndY=43.25 EndZ=0
    g5: LineSegment StartX=-49.19 StartY=40.5 StartZ=0 EndX=-49.19 EndY=37.5 EndZ=0
    g6: LineSegment StartX=-49.19 StartY=34.5 StartZ=0 EndX=-49.19 EndY=31.5 EndZ=0
    g7: LineSegment StartX=-49.19 StartY=28.75 StartZ=0 EndX=-49.19 EndY=25.75 EndZ=0
    g8: LineSegment StartX=-49.19 StartY=23 StartZ=0 EndX=-49.19 EndY=20 EndZ=0
    g9: LineSegment StartX=-49.19 StartY=17.25 StartZ=0 EndX=-49.19 EndY=14.25 EndZ=0
    g10: LineSegment StartX=-49.19 StartY=11.5 StartZ=0 EndX=-49.19 EndY=8.5 EndZ=0
    g11: LineSegment StartX=-49.19 StartY=5.75 StartZ=0 EndX=-49.19 EndY=2.75 EndZ=0
    g12: ArcOfCircle CenterX=-1.5 CenterY=67.75 CenterZ=0 NormalX=0 NormalY=0 NormalZ=1 AngleXU=0 Radius=1.5 StartAngle=4.71239 EndAngle=7.85398
    g13: ArcOfCircle CenterX=-1.5 CenterY=62 CenterZ=0 NormalX=0 NormalY=0 NormalZ=1 AngleXU=0 Radius=1.5 StartAngle=4.71239 EndAngle=7.85398
    g14: ArcOfCircle CenterX=-1.5 CenterY=56.25 CenterZ=0 NormalX=0 NormalY=0 NormalZ=1 AngleXU=0 Radius=1.5 StartAngle=4.71239 EndAngle=7.85398
    g15: ArcOfCircle CenterX=-11.49 CenterY=50.5 CenterZ=0 NormalX=0 NormalY=0 NormalZ=1 AngleXU=0 Radius=1.5 StartAngle=4.71239 EndAngle=7.85398
    g16: ArcOfCircle CenterX=-16.28 CenterY=44.75 CenterZ=0 NormalX=0 NormalY=0 NormalZ=1 AngleXU=0 Radius=1.5 StartAngle=4.71239 EndAngle=7.85398
    g17: ArcOfCircle CenterX=-18.2337 CenterY=39 CenterZ=0 NormalX=0 NormalY=0 NormalZ=1 AngleXU=0 Radius=1.5 StartAngle=4.71485 EndAngle=7.85398
    g18: ArcOfCircle CenterX=-16.2837 CenterY=27.25 CenterZ=0 NormalX=0 NormalY=0 NormalZ=1 AngleXU=0 Radius=1.5 StartAngle=4.71485 EndAngle=7.85398
    g19: ArcOfCircle CenterX=-18.2337 CenterY=33 CenterZ=0 NormalX=0 NormalY=0 NormalZ=1 AngleXU=0 Radius=1.5 StartAngle=4.71485 EndAngle=7.85398
    g20: ArcOfCircle CenterX=-11.49 CenterY=21.5 CenterZ=0 NormalX=0 NormalY=0 NormalZ=1 AngleXU=0 Radius=1.5 StartAngle=4.71239 EndAngle=7.85398
    g21: ArcOfCircle CenterX=-1.5 CenterY=4.25 CenterZ=0 NormalX=0 NormalY=0 NormalZ=1 AngleXU=0 Radius=1.5 StartAngle=4.71239 EndAngle=7.85398
    g22: ArcOfCircle CenterX=-1.5 CenterY=10 CenterZ=0 NormalX=0 NormalY=0 NormalZ=1 AngleXU=0 Radius=1.5 StartAngle=4.71239 EndAngle=7.85398
    g23: ArcOfCircle CenterX=-1.5 CenterY=15.75 CenterZ=0 NormalX=0 NormalY=0 NormalZ=1 AngleXU=0 Radius=1.5 StartAngle=4.71239 EndAngle=7.85398
    g24: LineSegment StartX=-49.19 StartY=69.25 StartZ=0 EndX=-1.5 EndY=69.25 EndZ=0
    g25: LineSegment StartX=-49.19 StartY=66.25 StartZ=0 EndX=-1.5 EndY=66.25 EndZ=0
    g26: LineSegment StartX=-49.19 StartY=63.5 StartZ=0 EndX=-1.5 EndY=63.5 EndZ=0
    g27: LineSegment StartX=-49.19 StartY=60.5 StartZ=0 EndX=-1.5 EndY=60.5 EndZ=0
    g28: LineSegment StartX=-49.19 StartY=57.75 StartZ=0 EndX=-1.5 EndY=57.75 EndZ=0
    g29: LineSegment StartX=-49.19 StartY=54.75 StartZ=0 EndX=-1.5 EndY=54.75 EndZ=0
    g30: LineSegment StartX=-49.19 StartY=52 StartZ=0 EndX=-11.49 EndY=52 EndZ=0
    g31: LineSegment StartX=-49.19 StartY=49 StartZ=0 EndX=-11.49 EndY=49 EndZ=0
    g32: LineSegment StartX=-49.19 StartY=46.25 StartZ=0 EndX=-16.28 EndY=46.25 EndZ=0
    g33: LineSegment StartX=-49.19 StartY=43.25 StartZ=0 EndX=-16.28 EndY=43.25 EndZ=0
    g34: LineSegment StartX=-49.19 StartY=40.5 StartZ=0 EndX=-18.2337 EndY=40.5 EndZ=0
    g35: LineSegment StartX=-49.19 StartY=37.5 StartZ=0 EndX=-18.23 EndY=37.5 EndZ=0
    g36: LineSegment StartX=-49.19 StartY=34.5 StartZ=0 EndX=-18.2337 EndY=34.5 EndZ=0
    g37: LineSegment StartX=-49.19 StartY=31.5 StartZ=0 EndX=-18.23 EndY=31.5 EndZ=0
    g38: LineSegment StartX=-49.19 StartY=28.75 StartZ=0 EndX=-16.2837 EndY=28.75 EndZ=0
    g39: LineSegment StartX=-49.19 StartY=25.75 StartZ=0 EndX=-16.28 EndY=25.75 EndZ=0
    g40: LineSegment StartX=-49.19 StartY=23 StartZ=0 EndX=-11.49 EndY=23 EndZ=0
    g41: LineSegment StartX=-49.19 StartY=20 StartZ=0 EndX=-11.49 EndY=20 EndZ=0
    g42: LineSegment StartX=-49.19 StartY=17.25 StartZ=0 EndX=-1.5 EndY=17.25 EndZ=0
    g43: LineSegment StartX=-49.19 StartY=14.25 StartZ=0 EndX=-1.5 EndY=14.25 EndZ=0
    g44: LineSegment StartX=-49.19 StartY=11.5 StartZ=0 EndX=-1.5 EndY=11.5 EndZ=0
    g45: LineSegment StartX=-49.19 StartY=8.5 StartZ=0 EndX=-1.5 EndY=8.5 EndZ=0
    g46: LineSegment StartX=-49.19 StartY=5.75 StartZ=0 EndX=-1.5 EndY=5.75 EndZ=0
    g47: LineSegment StartX=-49.19 StartY=2.75 StartZ=0 EndX=-1.5 EndY=2.75 EndZ=0
  constraints (120):
    c: Vertical(g0)
    c: Distance(g0) = 3
    c: Block(g0)
    c: Vertical(g1)
    c: Distance(g1) = 3
    c: Vertical(g2)
    c: Equal(g0,g2) = 3
    c: Block(g2)
    c: Vertical(g3)
    c: Equal(g1,g3) = 3
    c: Vertical(g4)
    c: Equal(g0,g4) = 3
    c: Block(g4)
    c: Vertical(g5)
    c: Equal(g1,g5) = 3
    c: Vertical(g6)
    c: Equal(g0,g6) = 3
    c: Block(g6)
    c: Vertical(g7)
    c: Equal(g1,g7) = 3
    c: Vertical(g8)
    c: Equal(g0,g8) = 3
    c: Block(g8)
    c: Vertical(g9)
    c: Equal(g1,g9) = 3
    c: Vertical(g10)
    c: Equal(g0,g10) = 3
    c: Block(g10)
    c: Vertical(g11)
    c: Equal(g1,g11) = 3
    c: Block(g12)
    c: Block(g13)
    c: Block(g14)
    c: Block(g15)
    c: Block(g16)
    c: Block(g17)
    c: Block(g18)
    c: Block(g19)
    c: Block(g20)
    c: Block(g21)
    c: Block(g22)
    c: Block(g23)
    c: Block(g11)
    c: Block(g9)
    c: Block(g7)
    c: Block(g5)
    c: Block(g3)
    c: Block(g1)
    c: Coincident(g24,g0)
    c: Coincident(g24,g12)
    c: Horizontal(g24)
    c: Coincident(g25,g0)
    c: Coincident(g25,g12)
    c: Horizontal(g25)
    c: Coincident(g26,g1)
    c: Coincident(g26,g13)
    c: Horizontal(g26)
    c: Coincident(g27,g1)
    c: Coincident(g27,g13)
    c: Horizontal(g27)
    c: Coincident(g28,g2)
    c: Coincident(g28,g14)
    c: Horizontal(g28)
    c: Coincident(g29,g2)
    c: Coincident(g29,g14)
    c: Horizontal(g29)
    c: Coincident(g30,g3)
    c: Coincident(g30,g15)
    c: Horizontal(g30)
    c: Coincident(g31,g3)
    c: Coincident(g31,g15)
    c: Horizontal(g31)
    c: Coincident(g32,g4)
    c: Coincident(g32,g16)
    c: Horizontal(g32)
    c: Coincident(g33,g4)
    c: Coincident(g33,g16)
    c: Horizontal(g33)
    c: Coincident(g34,g5)
    c: Coincident(g34,g17)
    c: Horizontal(g34)
    c: Coincident(g35,g5)
    c: Coincident(g35,g17)
    c: Horizontal(g35)
    c: Coincident(g36,g6)
    c: Coincident(g36,g19)
    c: Horizontal(g36)
    c: Coincident(g37,g6)
    c: Coincident(g37,g19)
    c: Horizontal(g37)
    c: Coincident(g38,g7)
    c: Coincident(g38,g18)
    c: Horizontal(g38)
    c: Coincident(g39,g7)
    c: Coincident(g39,g18)
    c: Horizontal(g39)
    c: Coincident(g40,g8)
    c: Coincident(g40,g20)
    c: Horizontal(g40)
    c: Coincident(g41,g8)
    c: Coincident(g41,g20)
    c: Horizontal(g41)
    c: Coincident(g42,g9)
    c: Coincident(g42,g23)
    c: Horizontal(g42)
    c: Coincident(g43,g9)
    c: Coincident(g43,g23)
    c: Horizontal(g43)
    c: Coincident(g44,g10)
    c: Coincident(g44,g22)
    c: Horizontal(g44)
    c: Coincident(g45,g10)
    c: Coincident(g45,g22)
    c: Horizontal(g45)
    c: Coincident(g46,g11)
    c: Coincident(g46,g21)
    c: Horizontal(g46)
    c: Coincident(g47,g11)
    c: Coincident(g47,g21)
    c: Horizontal(g47)
FEATURE [Part::Extrusion] Extrude046
  Base = -> Sketch055
  Dir = (1,0,0)
  DirMode = 2
  FaceMakerClass = Part::FaceMakerBullseye
  LengthFwd = 23
  LengthRev = 0
  Placement = pos=(-19,0,0) rot=(0,0,1;0rad)
  Solid = true
  Symmetric = false
FEATURE [Part::Fillet] Fillet038  label="removeToCreateVentalationHoles001"
  Base = -> Extrude046
  Edges = <same value as first occurrence — deduplicated (x6 in doc)>
  Placement = pos=(7,0,0) rot=(0,0,1;0rad)
FEATURE [Sketcher::SketchObject] Sketch056  label="topSketch014"
  FullyConstrained = true
  sketch-geometry (22):
    g0: LineSegment StartX=5.21097e-06 StartY=3 StartZ=0 EndX=5.21097e-06 EndY=19 EndZ=0
    g1: ArcOfCircle CenterX=19 CenterY=19 CenterZ=0 NormalX=0 NormalY=0 NormalZ=1 AngleXU=0 Radius=19 StartAngle=1.5708 EndAngle=3.14159
    g2: ArcOfCircle CenterX=19 CenterY=19 CenterZ=0 NormalX=0 NormalY=0 NormalZ=1 AngleXU=0 Radius=16 StartAngle=1.5708 EndAngle=3.14159
    g3: LineSegment StartX=114 StartY=35 StartZ=0 EndX=19 EndY=35 EndZ=0
    g4: LineSegment StartX=5.21097e-06 StartY=3 StartZ=0 EndX=5.21097e-06 EndY=0 EndZ=0
    g5: LineSegment StartX=3 StartY=0 StartZ=0 EndX=5.21097e-06 EndY=0 EndZ=0
    g6: LineSegment StartX=3 StartY=19 StartZ=0 EndX=3 EndY=0 EndZ=0
    g7: LineSegment StartX=19 StartY=38 StartZ=0 EndX=124 EndY=38 EndZ=0
    g8: Circle CenterX=119 CenterY=35 CenterZ=0 NormalX=0 NormalY=0 NormalZ=1 AngleXU=0 Radius=1
    g9: Circle CenterX=121 CenterY=35 CenterZ=0 NormalX=0 NormalY=0 NormalZ=1 AngleXU=0 Radius=1
    g10: Circle CenterX=121 CenterY=33 CenterZ=0 NormalX=0 NormalY=0 NormalZ=1 AngleXU=0 Radius=1
    g11: BSplineCurve PolesCount=3 KnotsCount=2 Degree=2 IsPeriodic=0
    g12: GeomPoint X=119 Y=35 Z=0
    g13: GeomPoint X=121 Y=33 Z=0
    g14: LineSegment StartX=119 StartY=35 StartZ=0 EndX=114 EndY=35 EndZ=0
    g15: ArcOfCircle CenterX=105 CenterY=19 CenterZ=0 NormalX=0 NormalY=0 NormalZ=1 AngleXU=0 Radius=16 StartAngle=5.60905 EndAngle=6.28319
    g16: LineSegment StartX=121 StartY=33 StartZ=0 EndX=121 EndY=19 EndZ=0
    g17: LineSegment StartX=117.5 StartY=9.01251 StartZ=0 EndX=121.163 EndY=9.0125 EndZ=0
    g18: ArcOfCircle CenterX=105 CenterY=19 CenterZ=0 NormalX=0 NormalY=0 NormalZ=1 AngleXU=0 Radius=20.6155 StartAngle=5.7297 EndAngle=6.28319
    g19: LineSegment StartX=121.163 StartY=9.0125 StartZ=0 EndX=122.538 EndY=8.16329 EndZ=0
    g20: LineSegment StartX=124 StartY=38 StartZ=0 EndX=125.616 EndY=38 EndZ=0
    g21: LineSegment StartX=125.616 StartY=19 StartZ=0 EndX=125.616 EndY=38 EndZ=0
  constraints (49):
    c: Vertical(g0)
    c: Block(g0)
    c: Coincident(g1,g0)
    c: Block(g1)
    c: Coincident(g2,g1)
    c: Block(g2)
    c: Coincident(g3,g2)
    c: Horizontal(g3)
    c: Tangent(g3,g2)
    c: Coincident(g4,g0)
    c: Distance(g4) = 3
    c: Vertical(g4)
    c: Coincident(g5,g4)
    c: Horizontal(g5)
    c: Coincident(g6,g2)
    c: Coincident(g6,g5)
    c: Vertical(g6)
    c: Horizontal(g7)
    c: Distance(g7) = 105
    c: Coincident(g7,g1)
    c: Block(g3)
    c: Weight(g8) = 1
    c: Equal(g8,g9)
    c: Equal(g8,g10)
    c: InternalAlignment(g8,g11)
    c: InternalAlignment(g9,g11)
    c: InternalAlignment(g10,g11)
    c: InternalAlignment(g12,g11)
    c: InternalAlignment(g13,g11)
    c: Block(g11)
    c: Coincident(g14,g11)
    c: Coincident(g14,g3)
    c: Horizontal(g14)
    c: Block(g15)
    c: Coincident(g16,g11)
    c: Coincident(g16,g15)
    c: Vertical(g16)
    c: Distance(g16) = 14
    c: Coincident(g17,g15)
    c: Block(g18)
    c: Coincident(g19,g18)
    c: Coincident(g20,g7)
    c: Horizontal(g20)
    c: Vertical(g21)
    c: Coincident(g20,g21)
    c: Block(g20)
    c: Block(g21)
    c: Block(g19)
    c: Block(g17)
FEATURE [Part::Box] Box026  label="removeToCreteHoleForPlugHousing032"
  AttacherType = Attacher::AttachEngine3D
  Height = 28.6
  Length = 10
  Placement = pos=(-2,0,21.7) rot=(0,0,1;0rad)
  Width = 19
FEATURE [Part::Feature] Face109 .. Face112  x4 (patterned run collapsed; names and placements below)
  shape: bbox 3.5 x 17.8 x 2e-07 mm, 1 faces, 0 solids (baked)
FEATURE [Part::Revolution] Revolve117  label="removeToCreateScrewAndThreadedInsertHole045"
  Angle = 360
  Axis = (0,1,0)
  Base = (0,0,0)
  FaceMakerClass = Part::FaceMakerBullseye
  Placement = pos=(62.3,30.3,19.7) rot=(0,0,1;0rad)
  Solid = false
  Source = -> Face109
  Symmetric = false
FEATURE [Part::Revolution] Revolve118  label="removeToCreateScrewAndThreadedInsertHole046"
  Angle = 360
  Axis = (0,1,0)
  Base = (0,0,0)
  FaceMakerClass = Part::FaceMakerBullseye
  Placement = pos=(62.3,30.3,51.7) rot=(0,0,1;0rad)
  Solid = false
  Source = -> Face110
  Symmetric = false
FEATURE [Part::Revolution] Revolve119  label="removeToCreateScrewAndThreadedInsertHole047"
  Angle = 360
  Axis = (0,1,0)
  Base = (0,0,0)
  FaceMakerClass = Part::FaceMakerBullseye
  Placement = pos=(30.3,30.3,19.7) rot=(0,0,1;0rad)
  Solid = false
  Source = -> Face111
  Symmetric = false
FEATURE [Part::Revolution] Revolve120  label="removeToCreateScrewAndThreadedInsertHole048"
  Angle = 360
  Axis = (0,1,0)
  Base = (0,0,0)
  FaceMakerClass = Part::FaceMakerBullseye
  Placement = pos=(30.3,30.3,51.7) rot=(0,0,1;0rad)
  Solid = false
  Source = -> Face112
  Symmetric = false
FEATURE [Part::MultiFuse] Fusion087  label="createThreadedInsertHolesForFan005"
  Shapes = -> [Revolve117,Revolve118,Revolve119,Revolve120]
FEATURE [Part::Extrusion] Extrude047
  Base = -> Sketch056
  Dir = (0,0,1)
  DirMode = 2
  FaceMakerClass = Part::FaceMakerBullseye
  LengthFwd = 72
  LengthRev = 0
  Solid = true
  Symmetric = false
FEATURE [Part::Fillet] Fillet039  label="top019"
  Base = -> Extrude047
  Edges = 1 edges r=2: [Edge35]
FEATURE [Sketcher::SketchObject] Sketch057
  FullyConstrained = false
  Placement = pos=(0,0,0) rot=(1,0,0;1.5708rad)
  sketch-geometry (24):
    g0: ArcOfCircle CenterX=-4 CenterY=-10.5 CenterZ=0 NormalX=0 NormalY=0 NormalZ=1 AngleXU=0 Radius=1.5 StartAngle=6e-16 EndAngle=3.14159
    g1: ArcOfCircle CenterX=-34.2 CenterY=-10.5 CenterZ=0 NormalX=0 NormalY=0 NormalZ=1 AngleXU=0 Radius=1.5 StartAngle=0 EndAngle=3.14159
    g2: ArcOfCircle CenterX=-34.2 CenterY=-27.7 CenterZ=0 NormalX=0 NormalY=0 NormalZ=1 AngleXU=0 Radius=1.5 StartAngle=3.14159 EndAngle=6.28319
    g3: ArcOfCircle CenterX=-4 CenterY=-27.7 CenterZ=0 NormalX=0 NormalY=0 NormalZ=1 AngleXU=0 Radius=1.5 StartAngle=3.1416 EndAngle=6.28319
    g4: ArcOfCircle CenterX=-10 CenterY=-4.3 CenterZ=0 NormalX=0 NormalY=0 NormalZ=1 AngleXU=0 Radius=1.5 StartAngle=2e-16 EndAngle=3.14159
    g5: ArcOfCircle CenterX=-16.1 CenterY=-1.8 CenterZ=0 NormalX=0 NormalY=0 NormalZ=1 AngleXU=0 Radius=1.5 StartAngle=5e-16 EndAngle=3.14159
    g6: ArcOfCircle CenterX=-22.1 CenterY=-1.8 CenterZ=0 NormalX=0 NormalY=0 NormalZ=1 AngleXU=0 Radius=1.5 StartAngle=5e-16 EndAngle=3.14159
    g7: ArcOfCircle CenterX=-28.2 CenterY=-4.3 CenterZ=0 NormalX=0 NormalY=0 NormalZ=1 AngleXU=0 Radius=1.5 StartAngle=2e-16 EndAngle=3.14159
    g8: ArcOfCircle CenterX=-10 CenterY=-33.9 CenterZ=0 NormalX=0 NormalY=0 NormalZ=1 AngleXU=0 Radius=1.5 StartAngle=3.14159 EndAngle=6.28319
    g9: ArcOfCircle CenterX=-16.1 CenterY=-36.4 CenterZ=0 NormalX=0 NormalY=0 NormalZ=1 AngleXU=0 Radius=1.5 StartAngle=3.14159 EndAngle=6.28319
    g10: ArcOfCircle CenterX=-22.1 CenterY=-36.4 CenterZ=0 NormalX=0 NormalY=0 NormalZ=1 AngleXU=0 Radius=1.5 StartAngle=3.14159 EndAngle=6.28319
    g11: ArcOfCircle CenterX=-28.2 CenterY=-33.9 CenterZ=0 NormalX=0 NormalY=0 NormalZ=1 AngleXU=0 Radius=1.5 StartAngle=3.14159 EndAngle=6.28319
    g12: LineSegment StartX=-35.7 StartY=-10.5 StartZ=0 EndX=-35.7 EndY=-27.7 EndZ=0
    g13: LineSegment StartX=-32.7 StartY=-10.5 StartZ=0 EndX=-32.7 EndY=-27.7 EndZ=0
    g14: LineSegment StartX=-29.7 StartY=-33.9 StartZ=0 EndX=-29.7 EndY=-4.3 EndZ=0
    g15: LineSegment StartX=-26.7 StartY=-33.9 StartZ=0 EndX=-26.7 EndY=-4.3 EndZ=0
    g16: LineSegment StartX=-2.5 StartY=-10.5 StartZ=0 EndX=-2.5 EndY=-27.7 EndZ=0
    g17: LineSegment StartX=-8.5 StartY=-4.3 StartZ=0 EndX=-8.5 EndY=-33.9 EndZ=0
    g18: LineSegment StartX=-5.5 StartY=-10.5 StartZ=0 EndX=-5.5 EndY=-27.7 EndZ=0
    g19: LineSegment StartX=-11.5 StartY=-4.3 StartZ=0 EndX=-11.5 EndY=-33.9 EndZ=0
    g20: LineSegment StartX=-14.6 StartY=-1.8 StartZ=0 EndX=-14.6 EndY=-36.4 EndZ=0
    g21: LineSegment StartX=-17.6 StartY=-1.8 StartZ=0 EndX=-17.6 EndY=-36.4 EndZ=0
    g22: LineSegment StartX=-20.6 StartY=-36.4 StartZ=0 EndX=-20.6 EndY=-1.8 EndZ=0
    g23: LineSegment StartX=-23.6 StartY=-1.8 StartZ=0 EndX=-23.6 EndY=-36.4 EndZ=0
  constraints (48):
    c: Block(g0)
    c: Block(g1)
    c: Block(g2)
    c: Block(g3)
    c: Block(g4)
    c: Block(g5)
    c: Block(g6)
    c: Block(g7)
    c: Block(g8)
    c: Block(g9)
    c: Block(g10)
    c: Block(g11)
    c: Coincident(g12,g1)
    c: Coincident(g12,g2)
    c: Vertical(g12)
    c: Coincident(g13,g1)
    c: Coincident(g13,g2)
    c: Vertical(g13)
    c: Coincident(g14,g11)
    c: Coincident(g14,g7)
    c: Vertical(g14)
    c: Coincident(g15,g11)
    c: Coincident(g15,g7)
    c: Vertical(g15)
    c: Coincident(g16,g0)
    c: Coincident(g16,g3)
    c: Vertical(g16)
    c: Coincident(g17,g4)
    c: Coincident(g17,g8)
    c: Vertical(g17)
    c: Coincident(g18,g0)
    c: Coincident(g18,g3)
    c: Vertical(g18)
    c: Coincident(g19,g4)
    c: Coincident(g19,g8)
    c: Vertical(g19)
    c: Coincident(g20,g5)
    c: Coincident(g20,g9)
    c: Vertical(g20)
    c: Coincident(g21,g5)
    c: Coincident(g21,g9)
    c: Vertical(g21)
    c: Coincident(g22,g10)
    c: Coincident(g22,g6)
    c: Vertical(g22)
    c: Coincident(g23,g6)
    c: Coincident(g23,g10)
    c: Vertical(g23)
FEATURE [Part::Extrusion] Extrude048  label="removeToCreateFanGrillHoles004"
  Base = -> Sketch057
  Dir = (0,-1,6e-16)
  DirMode = 2
  FaceMakerClass = Part::FaceMakerBullseye
  LengthFwd = 10
  LengthRev = 0
  Placement = pos=(65.4,44,54.82) rot=(0,0,1;0rad)
  Solid = true
  Symmetric = false
FEATURE [Part::Cut] Cut040  label="top021"
  Base = -> Fillet039
  Tool = -> Extrude048
FEATURE [Part::Cylinder] Cylinder041  label="removeToCreteHoleForPlugHousing034"
  Angle = 360
  AttacherType = Attacher::AttachEngine3D
  Height = 20
  Placement = pos=(-2,19,36) rot=(0,1,0;1.5708rad)
  Radius = 14.3
FEATURE [Part::MultiFuse] Fusion089  label="removeToCreteHoleForPlugHousing035"
  Shapes = -> [Box026,Cylinder041]
FEATURE [Part::Cylinder] Cylinder042
  Angle = 360
  AttacherType = Attacher::AttachEngine3D
  Height = 20
  Placement = pos=(0,0,36.15) rot=(0,0,1;0rad)
  Radius = 14.3
FEATURE [Part::Cylinder] Cylinder043
  Angle = 360
  AttacherType = Attacher::AttachEngine3D
  Height = 10
  Placement = pos=(0,0,36.15) rot=(0,0,1;0rad)
  Radius = 4
FEATURE [Part::Box] Box027  label="removeToCreteHoleForPlugHousing036"
  AttacherType = Attacher::AttachEngine3D
  Height = 28.6
  Length = 20
  Placement = pos=(106.15,0,21.7) rot=(0,0,1;0rad)
  Width = 19
FEATURE [Part::Cut] Cut041  label="top022"
  Base = -> Cut040
  Tool = -> Fusion087
FEATURE [Part::Cut] Cut039  label="top020"
  Base = -> Cut041
  Tool = -> Fusion089
FEATURE [Part::MultiFuse] Fusion090  label="removeToCreteHoleForPlugHousing037"
  Placement = pos=(70,19,36) rot=(0,1,0;1.5708rad)
  Shapes = -> [Cylinder042,Cylinder043]
FEATURE [Part::MultiFuse] Fusion088  label="removeToCreteHoleForPlugHousing033"
  Shapes = -> [Box027,Fusion090]
FEATURE [Part::Cut] Cut042  label="removeToCreteHoleForPlugHousing038"
  Base = -> Cut039
  Tool = -> Fusion088
FEATURE [Part::MultiFuse] Fusion091  label="removeFromTop"
  Shapes = -> [Fillet038,Fusion085,Fusion084,Fusion083,Extrude045]
FEATURE [Part::Cut] Cut043  label="REAL TOP ====="
  Base = -> Fillet036
  Tool = -> Fusion091
FEATURE [Part::MultiFuse] Fusion092  label="caseScrewPillarBracket016"
  Shapes = -> [Extrude030,Extrude031,Extrude032,Extrude033,Extrude034,Extrude035,Extrude036,Extrude037,Box013,Box014]
FEATURE [Sketcher::SketchObject] Sketch058  label="topSketch015"
  FullyConstrained = true
  sketch-geometry (20):
    g0: LineSegment StartX=5.21097e-06 StartY=3 StartZ=0 EndX=5.21097e-06 EndY=19 EndZ=0
    g1: ArcOfCircle CenterX=19 CenterY=19 CenterZ=0 NormalX=0 NormalY=0 NormalZ=1 AngleXU=0 Radius=19 StartAngle=1.5708 EndAngle=3.14159
    g2: ArcOfCircle CenterX=19 CenterY=19 CenterZ=0 NormalX=0 NormalY=0 NormalZ=1 AngleXU=0 Radius=16 StartAngle=1.5708 EndAngle=3.14159
    g3: LineSegment StartX=114 StartY=35 StartZ=0 EndX=19 EndY=35 EndZ=0
    g4: LineSegment StartX=5.21097e-06 StartY=3 StartZ=0 EndX=5.21097e-06 EndY=0 EndZ=0
    g5: LineSegment StartX=3 StartY=0 StartZ=0 EndX=5.21097e-06 EndY=0 EndZ=0
    g6: LineSegment StartX=3 StartY=19 StartZ=0 EndX=3 EndY=0 EndZ=0
    g7: LineSegment StartX=19 StartY=38 StartZ=0 EndX=124 EndY=38 EndZ=0
    g8: Circle CenterX=119 CenterY=35 CenterZ=0 NormalX=0 NormalY=0 NormalZ=1 AngleXU=0 Radius=1
    g9: Circle CenterX=121 CenterY=35 CenterZ=0 NormalX=0 NormalY=0 NormalZ=1 AngleXU=0 Radius=1
    g10: Circle CenterX=121 CenterY=33 CenterZ=0 NormalX=0 NormalY=0 NormalZ=1 AngleXU=0 Radius=1
    g11: BSplineCurve PolesCount=3 KnotsCount=2 Degree=2 IsPeriodic=0
    g12: GeomPoint X=119 Y=35 Z=0
    g13: GeomPoint X=121 Y=33 Z=0
    g14: LineSegment StartX=119 StartY=35 StartZ=0 EndX=114 EndY=35 EndZ=0
    g15: ArcOfCircle CenterX=105 CenterY=19 CenterZ=0 NormalX=0 NormalY=0 NormalZ=1 AngleXU=0 Radius=19 StartAngle=5.7297 EndAngle=6.28319
    g16: ArcOfCircle CenterX=105 CenterY=19 CenterZ=0 NormalX=0 NormalY=0 NormalZ=1 AngleXU=0 Radius=16 StartAngle=5.60905 EndAngle=6.28319
    g17: LineSegment StartX=121 StartY=33 StartZ=0 EndX=121 EndY=19 EndZ=0
    g18: LineSegment StartX=124 StartY=38 StartZ=0 EndX=124 EndY=19 EndZ=0
    g19: LineSegment StartX=117.5 StartY=9.01251 StartZ=0 EndX=121.163 EndY=9.0125 EndZ=0
  constraints (46):
    c: Vertical(g0)
    c: Block(g0)
    c: Coincident(g1,g0)
    c: Block(g1)
    c: Coincident(g2,g1)
    c: Block(g2)
    c: Coincident(g3,g2)
    c: Horizontal(g3)
    c: Tangent(g3,g2)
    c: Coincident(g4,g0)
    c: Distance(g4) = 3
    c: Vertical(g4)
    c: Coincident(g5,g4)
    c: Horizontal(g5)
    c: Coincident(g6,g2)
    c: Coincident(g6,g5)
    c: Vertical(g6)
    c: Horizontal(g7)
    c: Distance(g7) = 105
    c: Coincident(g7,g1)
    c: Block(g3)
    c: Weight(g8) = 1
    c: Equal(g8,g9)
    c: Equal(g8,g10)
    c: InternalAlignment(g8,g11)
    c: InternalAlignment(g9,g11)
    c: InternalAlignment(g10,g11)
    c: InternalAlignment(g12,g11)
    c: InternalAlignment(g13,g11)
    c: Block(g11)
    c: Coincident(g14,g11)
    c: Coincident(g14,g3)
    c: Horizontal(g14)
    c: Block(g15)
    c: Coincident(g16,g15)
    c: Block(g16)
    c: Coincident(g17,g11)
    c: Coincident(g17,g16)
    c: Vertical(g17)
    c: Distance(g17) = 14
    c: Coincident(g18,g7)
    c: Coincident(g18,g15)
    c: Vertical(g18)
    c: Distance(g18) = 19
    c: Coincident(g19,g16)
    c: Coincident(g19,g15)
FEATURE [Part::Extrusion] Extrude049  label="top023"
  Base = -> Sketch058
  Dir = (0,0,1)
  DirMode = 2
  FaceMakerClass = Part::FaceMakerBullseye
  LengthFwd = 72
  LengthRev = 0
  Solid = true
  Symmetric = false
FEATURE [Sketcher::SketchObject] Sketch059
  FullyConstrained = true
  MapMode = 3
  Placement = pos=(0,0,0) rot=(1,0,0;1.5708rad)
  Support = -> [Extrude049]
  sketch-geometry (8):
    g0: Circle CenterX=80.351 CenterY=-67.6202 CenterZ=0 NormalX=0 NormalY=0 NormalZ=1 AngleXU=0 Radius=2
    g1: Circle CenterX=80.351 CenterY=-67.6202 CenterZ=0 NormalX=0 NormalY=0 NormalZ=1 AngleXU=0 Radius=3
    g2: Circle CenterX=80.351 CenterY=-4.92017 CenterZ=0 NormalX=0 NormalY=0 NormalZ=1 AngleXU=0 Radius=2
    g3: Circle CenterX=80.351 CenterY=-4.92017 CenterZ=0 NormalX=0 NormalY=0 NormalZ=1 AngleXU=0 Radius=3
    g4: Circle CenterX=23.851 CenterY=-4.92017 CenterZ=0 NormalX=0 NormalY=0 NormalZ=1 AngleXU=0 Radius=2
    g5: Circle CenterX=23.851 CenterY=-4.92017 CenterZ=0 NormalX=0 NormalY=0 NormalZ=1 AngleXU=0 Radius=3
    g6: Circle CenterX=23.851 CenterY=-67.6202 CenterZ=0 NormalX=0 NormalY=0 NormalZ=1 AngleXU=0 Radius=2
    g7: Circle CenterX=23.851 CenterY=-67.6202 CenterZ=0 NormalX=0 NormalY=0 NormalZ=1 AngleXU=0 Radius=3
  constraints (8):
    c: Block(g3)
    c: Block(g2)
    c: Block(g1)
    c: Block(g0)
    c: Block(g6)
    c: Block(g7)
    c: Block(g4)
    c: Block(g5)
FEATURE [Sketcher::SketchObject] Sketch060
  FullyConstrained = true
  MapMode = 3
  Placement = pos=(0,0,0) rot=(1,0,0;1.5708rad)
  Support = -> [Extrude049]
  sketch-geometry (8):
    g0: Circle CenterX=80.351 CenterY=-67.6202 CenterZ=0 NormalX=0 NormalY=0 NormalZ=1 AngleXU=0 Radius=3
    g1: Circle CenterX=80.351 CenterY=-4.92017 CenterZ=0 NormalX=0 NormalY=0 NormalZ=1 AngleXU=0 Radius=3
    g2: Circle CenterX=23.851 CenterY=-4.92017 CenterZ=0 NormalX=0 NormalY=0 NormalZ=1 AngleXU=0 Radius=3
    g3: Circle CenterX=23.851 CenterY=-67.6202 CenterZ=0 NormalX=0 NormalY=0 NormalZ=1 AngleXU=0 Radius=3
    g4: Circle CenterX=23.851 CenterY=-67.6202 CenterZ=0 NormalX=0 NormalY=0 NormalZ=1 AngleXU=0 Radius=5
    g5: Circle CenterX=80.351 CenterY=-67.6202 CenterZ=0 NormalX=0 NormalY=0 NormalZ=1 AngleXU=0 Radius=5
    g6: Circle CenterX=23.851 CenterY=-4.92017 CenterZ=0 NormalX=0 NormalY=0 NormalZ=1 AngleXU=0 Radius=5
    g7: Circle CenterX=80.351 CenterY=-4.92017 CenterZ=0 NormalX=0 NormalY=0 NormalZ=1 AngleXU=0 Radius=5
  constraints (8):
    c: Block(g1)
    c: Block(g0)
    c: Block(g3)
    c: Block(g2)
    c: Block(g5)
    c: Block(g4)
    c: Block(g6)
    c: Block(g7)
FEATURE [Sketcher::SketchObject] Sketch061
  FullyConstrained = true
  MapMode = 3
  Placement = pos=(0,0,0) rot=(1,0,0;1.5708rad)
  sketch-geometry (8):
    g0: Circle CenterX=80.351 CenterY=-67.6202 CenterZ=0 NormalX=0 NormalY=0 NormalZ=1 AngleXU=0 Radius=3
    g1: Circle CenterX=80.351 CenterY=-4.92017 CenterZ=0 NormalX=0 NormalY=0 NormalZ=1 AngleXU=0 Radius=3
    g2: Circle CenterX=23.851 CenterY=-4.92017 CenterZ=0 NormalX=0 NormalY=0 NormalZ=1 AngleXU=0 Radius=3
    g3: Circle CenterX=23.851 CenterY=-67.6202 CenterZ=0 NormalX=0 NormalY=0 NormalZ=1 AngleXU=0 Radius=3
    g4: Circle CenterX=23.851 CenterY=-67.6202 CenterZ=0 NormalX=0 NormalY=0 NormalZ=1 AngleXU=0 Radius=5
    g5: Circle CenterX=80.351 CenterY=-67.6202 CenterZ=0 NormalX=0 NormalY=0 NormalZ=1 AngleXU=0 Radius=5
    g6: Circle CenterX=23.851 CenterY=-4.92017 CenterZ=0 NormalX=0 NormalY=0 NormalZ=1 AngleXU=0 Radius=5
    g7: Circle CenterX=80.351 CenterY=-4.92017 CenterZ=0 NormalX=0 NormalY=0 NormalZ=1 AngleXU=0 Radius=5
  constraints (8):
    c: Block(g1)
    c: Block(g0)
    c: Block(g3)
    c: Block(g2)
    c: Block(g5)
    c: Block(g4)
    c: Block(g6)
    c: Block(g7)
FEATURE [Sketcher::SketchObject] Sketch062  label="topSketch016"
  FullyConstrained = true
  sketch-geometry (20):
    g0: LineSegment StartX=5.21097e-06 StartY=3 StartZ=0 EndX=5.21097e-06 EndY=19 EndZ=0
    g1: ArcOfCircle CenterX=19 CenterY=19 CenterZ=0 NormalX=0 NormalY=0 NormalZ=1 AngleXU=0 Radius=19 StartAngle=1.5708 EndAngle=3.14159
    g2: ArcOfCircle CenterX=19 CenterY=19 CenterZ=0 NormalX=0 NormalY=0 NormalZ=1 AngleXU=0 Radius=16 StartAngle=1.5708 EndAngle=3.14159
    g3: LineSegment StartX=114 StartY=35 StartZ=0 EndX=19 EndY=35 EndZ=0
    g4: LineSegment StartX=5.21097e-06 StartY=3 StartZ=0 EndX=5.21097e-06 EndY=0 EndZ=0
    g5: LineSegment StartX=3 StartY=0 StartZ=0 EndX=5.21097e-06 EndY=0 EndZ=0
    g6: LineSegment StartX=3 StartY=19 StartZ=0 EndX=3 EndY=0 EndZ=0
    g7: LineSegment StartX=19 StartY=38 StartZ=0 EndX=124 EndY=38 EndZ=0
    g8: Circle CenterX=119 CenterY=35 CenterZ=0 NormalX=0 NormalY=0 NormalZ=1 AngleXU=0 Radius=1
    g9: Circle CenterX=121 CenterY=35 CenterZ=0 NormalX=0 NormalY=0 NormalZ=1 AngleXU=0 Radius=1
    g10: Circle CenterX=121 CenterY=33 CenterZ=0 NormalX=0 NormalY=0 NormalZ=1 AngleXU=0 Radius=1
    g11: BSplineCurve PolesCount=3 KnotsCount=2 Degree=2 IsPeriodic=0
    g12: GeomPoint X=119 Y=35 Z=0
    g13: GeomPoint X=121 Y=33 Z=0
    g14: LineSegment StartX=119 StartY=35 StartZ=0 EndX=114 EndY=35 EndZ=0
    g15: ArcOfCircle CenterX=105 CenterY=19 CenterZ=0 NormalX=0 NormalY=0 NormalZ=1 AngleXU=0 Radius=19 StartAngle=5.7297 EndAngle=6.28319
    g16: ArcOfCircle CenterX=105 CenterY=19 CenterZ=0 NormalX=0 NormalY=0 NormalZ=1 AngleXU=0 Radius=16 StartAngle=5.60905 EndAngle=6.28319
    g17: LineSegment StartX=121 StartY=33 StartZ=0 EndX=121 EndY=19 EndZ=0
    g18: LineSegment StartX=124 StartY=38 StartZ=0 EndX=124 EndY=19 EndZ=0
    g19: LineSegment StartX=117.5 StartY=9.01251 StartZ=0 EndX=121.163 EndY=9.0125 EndZ=0
  constraints (46):
    c: Vertical(g0)
    c: Block(g0)
    c: Coincident(g1,g0)
    c: Block(g1)
    c: Coincident(g2,g1)
    c: Block(g2)
    c: Coincident(g3,g2)
    c: Horizontal(g3)
    c: Tangent(g3,g2)
    c: Coincident(g4,g0)
    c: Distance(g4) = 3
    c: Vertical(g4)
    c: Coincident(g5,g4)
    c: Horizontal(g5)
    c: Coincident(g6,g2)
    c: Coincident(g6,g5)
    c: Vertical(g6)
    c: Horizontal(g7)
    c: Distance(g7) = 105
    c: Coincident(g7,g1)
    c: Block(g3)
    c: Weight(g8) = 1
    c: Equal(g8,g9)
    c: Equal(g8,g10)
    c: InternalAlignment(g8,g11)
    c: InternalAlignment(g9,g11)
    c: InternalAlignment(g10,g11)
    c: InternalAlignment(g12,g11)
    c: InternalAlignment(g13,g11)
    c: Block(g11)
    c: Coincident(g14,g11)
    c: Coincident(g14,g3)
    c: Horizontal(g14)
    c: Block(g15)
    c: Coincident(g16,g15)
    c: Block(g16)
    c: Coincident(g17,g11)
    c: Coincident(g17,g16)
    c: Vertical(g17)
    c: Distance(g17) = 14
    c: Coincident(g18,g7)
    c: Coincident(g18,g15)
    c: Vertical(g18)
    c: Distance(g18) = 19
    c: Coincident(g19,g16)
    c: Coincident(g19,g15)
FEATURE [Part::Extrusion] Extrude053  label="top024"
  Base = -> Sketch062
  Dir = (0,0,1)
  DirMode = 2
  FaceMakerClass = Part::FaceMakerBullseye
  LengthFwd = 72
  LengthRev = 0
  Solid = true
  Symmetric = false
FEATURE [Sketcher::SketchObject] Sketch063
  FullyConstrained = true
  MapMode = 3
  Placement = pos=(0,0,0) rot=(1,0,0;1.5708rad)
  Support = -> [Extrude053]
  sketch-geometry (8):
    g0: Circle CenterX=80.351 CenterY=-67.6202 CenterZ=0 NormalX=0 NormalY=0 NormalZ=1 AngleXU=0 Radius=2
    g1: Circle CenterX=80.351 CenterY=-67.6202 CenterZ=0 NormalX=0 NormalY=0 NormalZ=1 AngleXU=0 Radius=3
    g2: Circle CenterX=80.351 CenterY=-4.92017 CenterZ=0 NormalX=0 NormalY=0 NormalZ=1 AngleXU=0 Radius=2
    g3: Circle CenterX=80.351 CenterY=-4.92017 CenterZ=0 NormalX=0 NormalY=0 NormalZ=1 AngleXU=0 Radius=3
    g4: Circle CenterX=23.851 CenterY=-4.92017 CenterZ=0 NormalX=0 NormalY=0 NormalZ=1 AngleXU=0 Radius=2
    g5: Circle CenterX=23.851 CenterY=-4.92017 CenterZ=0 NormalX=0 NormalY=0 NormalZ=1 AngleXU=0 Radius=3
    g6: Circle CenterX=23.851 CenterY=-67.6202 CenterZ=0 NormalX=0 NormalY=0 NormalZ=1 AngleXU=0 Radius=2
    g7: Circle CenterX=23.851 CenterY=-67.6202 CenterZ=0 NormalX=0 NormalY=0 NormalZ=1 AngleXU=0 Radius=3
  constraints (8):
    c: Block(g3)
    c: Block(g2)
    c: Block(g1)
    c: Block(g0)
    c: Block(g6)
    c: Block(g7)
    c: Block(g4)
    c: Block(g5)
FEATURE [Part::Extrusion] Extrude054
  Base = -> Sketch063
  Dir = (0,-1,2e-16)
  DirMode = 2
  FaceMakerClass = Part::FaceMakerBullseye
  LengthFwd = 6
  LengthRev = 0
  Placement = pos=(0,9,0) rot=(0,0,1;0rad)
  Solid = true
  Symmetric = false
FEATURE [Sketcher::SketchObject] Sketch064  label="topSketch017"
  FullyConstrained = true
  sketch-geometry (20):
    g0: LineSegment StartX=5.21097e-06 StartY=3 StartZ=0 EndX=5.21097e-06 EndY=19 EndZ=0
    g1: ArcOfCircle CenterX=19 CenterY=19 CenterZ=0 NormalX=0 NormalY=0 NormalZ=1 AngleXU=0 Radius=19 StartAngle=1.5708 EndAngle=3.14159
    g2: ArcOfCircle CenterX=19 CenterY=19 CenterZ=0 NormalX=0 NormalY=0 NormalZ=1 AngleXU=0 Radius=16 StartAngle=1.5708 EndAngle=3.14159
    g3: LineSegment StartX=114 StartY=35 StartZ=0 EndX=19 EndY=35 EndZ=0
    g4: LineSegment StartX=5.21097e-06 StartY=3 StartZ=0 EndX=5.21097e-06 EndY=0 EndZ=0
    g5: LineSegment StartX=3 StartY=0 StartZ=0 EndX=5.21097e-06 EndY=0 EndZ=0
    g6: LineSegment StartX=3 StartY=19 StartZ=0 EndX=3 EndY=0 EndZ=0
    g7: LineSegment StartX=19 StartY=38 StartZ=0 EndX=124 EndY=38 EndZ=0
    g8: Circle CenterX=119 CenterY=35 CenterZ=0 NormalX=0 NormalY=0 NormalZ=1 AngleXU=0 Radius=1
    g9: Circle CenterX=121 CenterY=35 CenterZ=0 NormalX=0 NormalY=0 NormalZ=1 AngleXU=0 Radius=1
    g10: Circle CenterX=121 CenterY=33 CenterZ=0 NormalX=0 NormalY=0 NormalZ=1 AngleXU=0 Radius=1
    g11: BSplineCurve PolesCount=3 KnotsCount=2 Degree=2 IsPeriodic=0
    g12: GeomPoint X=119 Y=35 Z=0
    g13: GeomPoint X=121 Y=33 Z=0
    g14: LineSegment StartX=119 StartY=35 StartZ=0 EndX=114 EndY=35 EndZ=0
    g15: ArcOfCircle CenterX=105 CenterY=19 CenterZ=0 NormalX=0 NormalY=0 NormalZ=1 AngleXU=0 Radius=19 StartAngle=5.7297 EndAngle=6.28319
    g16: ArcOfCircle CenterX=105 CenterY=19 CenterZ=0 NormalX=0 NormalY=0 NormalZ=1 AngleXU=0 Radius=16 StartAngle=5.60905 EndAngle=6.28319
    g17: LineSegment StartX=121 StartY=33 StartZ=0 EndX=121 EndY=19 EndZ=0
    g18: LineSegment StartX=124 StartY=38 StartZ=0 EndX=124 EndY=19 EndZ=0
    g19: LineSegment StartX=117.5 StartY=9.01251 StartZ=0 EndX=121.163 EndY=9.0125 EndZ=0
  constraints (46):
    c: Vertical(g0)
    c: Block(g0)
    c: Coincident(g1,g0)
    c: Block(g1)
    c: Coincident(g2,g1)
    c: Block(g2)
    c: Coincident(g3,g2)
    c: Horizontal(g3)
    c: Tangent(g3,g2)
    c: Coincident(g4,g0)
    c: Distance(g4) = 3
    c: Vertical(g4)
    c: Coincident(g5,g4)
    c: Horizontal(g5)
    c: Coincident(g6,g2)
    c: Coincident(g6,g5)
    c: Vertical(g6)
    c: Horizontal(g7)
    c: Distance(g7) = 105
    c: Coincident(g7,g1)
    c: Block(g3)
    c: Weight(g8) = 1
    c: Equal(g8,g9)
    c: Equal(g8,g10)
    c: InternalAlignment(g8,g11)
    c: InternalAlignment(g9,g11)
    c: InternalAlignment(g10,g11)
    c: InternalAlignment(g12,g11)
    c: InternalAlignment(g13,g11)
    c: Block(g11)
    c: Coincident(g14,g11)
    c: Coincident(g14,g3)
    c: Horizontal(g14)
    c: Block(g15)
    c: Coincident(g16,g15)
    c: Block(g16)
    c: Coincident(g17,g11)
    c: Coincident(g17,g16)
    c: Vertical(g17)
    c: Distance(g17) = 14
    c: Coincident(g18,g7)
    c: Coincident(g18,g15)
    c: Vertical(g18)
    c: Distance(g18) = 19
    c: Coincident(g19,g16)
    c: Coincident(g19,g15)
FEATURE [Sketcher::SketchObject] Sketch065
  FullyConstrained = true
  MapMode = 3
  Placement = pos=(0,0,0) rot=(1,0,0;1.5708rad)
  sketch-geometry (8):
    g0: Circle CenterX=80.351 CenterY=-67.6202 CenterZ=0 NormalX=0 NormalY=0 NormalZ=1 AngleXU=0 Radius=3
    g1: Circle CenterX=80.351 CenterY=-4.92017 CenterZ=0 NormalX=0 NormalY=0 NormalZ=1 AngleXU=0 Radius=3
    g2: Circle CenterX=23.851 CenterY=-4.92017 CenterZ=0 NormalX=0 NormalY=0 NormalZ=1 AngleXU=0 Radius=3
    g3: Circle CenterX=23.851 CenterY=-67.6202 CenterZ=0 NormalX=0 NormalY=0 NormalZ=1 AngleXU=0 Radius=3
    g4: Circle CenterX=23.851 CenterY=-67.6202 CenterZ=0 NormalX=0 NormalY=0 NormalZ=1 AngleXU=0 Radius=5
    g5: Circle CenterX=80.351 CenterY=-67.6202 CenterZ=0 NormalX=0 NormalY=0 NormalZ=1 AngleXU=0 Radius=5
    g6: Circle CenterX=23.851 CenterY=-4.92017 CenterZ=0 NormalX=0 NormalY=0 NormalZ=1 AngleXU=0 Radius=5
    g7: Circle CenterX=80.351 CenterY=-4.92017 CenterZ=0 NormalX=0 NormalY=0 NormalZ=1 AngleXU=0 Radius=5
  constraints (8):
    c: Block(g1)
    c: Block(g0)
    c: Block(g3)
    c: Block(g2)
    c: Block(g5)
    c: Block(g4)
    c: Block(g6)
    c: Block(g7)
FEATURE [Part::Extrusion] Extrude056
  Base = -> Sketch065
  Dir = (0,-1,2e-16)
  DirMode = 2
  FaceMakerClass = Part::FaceMakerBullseye
  LengthFwd = 2
  LengthRev = 0
  Solid = true
  Symmetric = false
FEATURE [Part::Extrusion] Extrude057  label="top025"
  Base = -> Sketch064
  Dir = (0,0,1)
  DirMode = 2
  FaceMakerClass = Part::FaceMakerBullseye
  LengthFwd = 72
  LengthRev = 0
  Solid = true
  Symmetric = false
FEATURE [Sketcher::SketchObject] Sketch066
  FullyConstrained = true
  MapMode = 3
  Placement = pos=(0,0,0) rot=(1,0,0;1.5708rad)
  Support = -> [Extrude057]
  sketch-geometry (8):
    g0: Circle CenterX=80.351 CenterY=-67.6202 CenterZ=0 NormalX=0 NormalY=0 NormalZ=1 AngleXU=0 Radius=3
    g1: Circle CenterX=80.351 CenterY=-4.92017 CenterZ=0 NormalX=0 NormalY=0 NormalZ=1 AngleXU=0 Radius=3
    g2: Circle CenterX=23.851 CenterY=-4.92017 CenterZ=0 NormalX=0 NormalY=0 NormalZ=1 AngleXU=0 Radius=3
    g3: Circle CenterX=23.851 CenterY=-67.6202 CenterZ=0 NormalX=0 NormalY=0 NormalZ=1 AngleXU=0 Radius=3
    g4: Circle CenterX=23.851 CenterY=-67.6202 CenterZ=0 NormalX=0 NormalY=0 NormalZ=1 AngleXU=0 Radius=5
    g5: Circle CenterX=80.351 CenterY=-67.6202 CenterZ=0 NormalX=0 NormalY=0 NormalZ=1 AngleXU=0 Radius=5
    g6: Circle CenterX=23.851 CenterY=-4.92017 CenterZ=0 NormalX=0 NormalY=0 NormalZ=1 AngleXU=0 Radius=5
    g7: Circle CenterX=80.351 CenterY=-4.92017 CenterZ=0 NormalX=0 NormalY=0 NormalZ=1 AngleXU=0 Radius=5
  constraints (8):
    c: Block(g1)
    c: Block(g0)
    c: Block(g3)
    c: Block(g2)
    c: Block(g5)
    c: Block(g4)
    c: Block(g6)
    c: Block(g7)
FEATURE [Part::Extrusion] Extrude055
  Base = -> Sketch066
  Dir = (0,-1,2e-16)
  DirMode = 2
  FaceMakerClass = Part::FaceMakerBullseye
  LengthFwd = 2
  LengthRev = 0
  Solid = true
  Symmetric = false
FEATURE [Part::Fillet] Fillet041
  Base = -> Extrude056
  Edges = 4 edges r=1.99: [Edge6,Edge12,Edge18,Edge24]
FEATURE [Part::Cut] Cut045
  Base = -> Extrude055
  Placement = pos=(0,6,0) rot=(0,0,1;0rad)
  Tool = -> Fillet041
FEATURE [Part::MultiFuse] Fusion095  label="pcbScrewPillars"
  Placement = pos=(-3.2,-1,72.3) rot=(0,0,1;0rad)
  Shapes = -> [Cut045,Extrude054]
FEATURE [Part::Feature] Face113
  shape: bbox 3.2 x 1.5 x 2e-07 mm, 1 faces, 0 solids (baked)
FEATURE [Part::Revolution] Revolve121  label="backCaseScrewRetainer002"
  Angle = 360
  Axis = (0,1,0)
  Base = (0,0,0)
  FaceMakerClass = Part::FaceMakerBullseye
  Placement = pos=(12.5,3,62) rot=(0,0,1;0rad)
  Solid = false
  Source = -> Face113
  Symmetric = false
FEATURE [Part::Feature] Face114
  shape: bbox 3.2 x 1.5 x 2e-07 mm, 1 faces, 0 solids (baked)
FEATURE [Part::Feature] Face115
  shape: bbox 3.2 x 1.5 x 2e-07 mm, 1 faces, 0 solids (baked)
FEATURE [Part::Feature] Face116
  shape: bbox 3.2 x 1.5 x 2e-07 mm, 1 faces, 0 solids (baked)
FEATURE [Part::Revolution] Revolve122  label="frontCaseScrewRetainer004"
  Angle = 360
  Axis = (0,1,0)
  Base = (0,0,0)
  FaceMakerClass = Part::FaceMakerBullseye
  Placement = pos=(89.5,3,68.5) rot=(0,0,1;0rad)
  Solid = false
  Source = -> Face115
  Symmetric = false
FEATURE [Part::Revolution] Revolve123  label="frontCaseScrewRetainer005"
  Angle = 360
  Axis = (0,1,0)
  Base = (0,0,0)
  FaceMakerClass = Part::FaceMakerBullseye
  Placement = pos=(89.5,3,3.5) rot=(0,0,1;0rad)
  Solid = false
  Source = -> Face116
  Symmetric = false
FEATURE [Part::Revolution] Revolve124  label="backCaseScrewRetainer003"
  Angle = 360
  Axis = (0,1,0)
  Base = (0,0,0)
  FaceMakerClass = Part::FaceMakerBullseye
  Placement = pos=(12.5,3,10) rot=(0,0,1;0rad)
  Solid = false
  Source = -> Face114
  Symmetric = false
FEATURE [Part::Feature] Face117
  shape: bbox 3.6 x 3.2 x 2e-07 mm, 1 faces, 0 solids (baked)
FEATURE [Part::Revolution] Revolve125  label="moreFrontCaseScrewRetainer004"
  Angle = 360
  Axis = (0,1,0)
  Base = (0,0,0)
  FaceMakerClass = Part::FaceMakerBullseye
  Placement = pos=(109.5,4.5,68.5) rot=(0,0,1;0rad)
  Solid = false
  Source = -> Face117
  Symmetric = false
FEATURE [Part::Feature] Face118
  shape: bbox 3.6 x 3.2 x 2e-07 mm, 1 faces, 0 solids (baked)
FEATURE [Part::Revolution] Revolve126  label="moreFrontCaseScrewRetainer005"
  Angle = 360
  Axis = (0,1,0)
  Base = (0,0,0)
  FaceMakerClass = Part::FaceMakerBullseye
  Placement = pos=(109.5,4.5,3.5) rot=(0,0,1;0rad)
  Solid = false
  Source = -> Face118
  Symmetric = false
FEATURE [Part::MultiFuse] Fusion096  label="screwRetainers001"
  Shapes = -> [Revolve126,Revolve125,Revolve124,Revolve123,Revolve122,Revolve121]
FEATURE [Part::Feature] Face119
  shape: bbox 10 x 16.5 x 2e-07 mm, 1 faces, 0 solids (baked)
FEATURE [Part::Revolution] Revolve130  label="plugHousing050"
  Angle = 360
  Axis = (0,1,0)
  Base = (0,0,0)
  FaceMakerClass = Part::FaceMakerBullseye
  Placement = pos=(0,0,36.15) rot=(0,0,1;0rad)
  Solid = false
  Source = -> Face119
  Symmetric = false
FEATURE [Part::Feature] Face120
  shape: bbox 10 x 16.5 x 2e-07 mm, 1 faces, 0 solids (baked)
FEATURE [Part::Feature] Face121
  shape: bbox 10 x 16.5 x 2e-07 mm, 1 faces, 0 solids (baked)
FEATURE [Part::Revolution] Revolve127  label="plugHousing047"
  Angle = 360
  Axis = (0,1,0)
  Base = (0,0,0)
  FaceMakerClass = Part::FaceMakerBullseye
  Placement = pos=(0,0,36.15) rot=(0,0,1;0rad)
  Solid = false
  Source = -> Face121
  Symmetric = false
FEATURE [Part::Feature] Face122
  shape: bbox 10 x 16.5 x 2e-07 mm, 1 faces, 0 solids (baked)
FEATURE [Part::Feature] Face123
  shape: bbox 10 x 16.5 x 2e-07 mm, 1 faces, 0 solids (baked)
FEATURE [Part::Revolution] Revolve128  label="plugHousing048"
  Angle = 360
  Axis = (0,1,0)
  Base = (0,0,0)
  FaceMakerClass = Part::FaceMakerBullseye
  Placement = pos=(0,0,36.15) rot=(0,0,1;0rad)
  Solid = false
  Source = -> Face123
  Symmetric = false
FEATURE [Part::MultiFuse] Fusion100  label="plugHousing054"
  Placement = pos=(0,0,0) rot=(0,0,1;1.5708rad)
  Shapes = -> [Revolve130,Revolve128]
FEATURE [Part::Feature] Face124
  shape: bbox 10 x 16.5 x 2e-07 mm, 1 faces, 0 solids (baked)
FEATURE [Part::Feature] Face125
  shape: bbox 10 x 16.5 x 2e-07 mm, 1 faces, 0 solids (baked)
FEATURE [Part::Revolution] Revolve129  label="plugHousing049"
  Angle = 360
  Axis = (0,1,0)
  Base = (0,0,0)
  FaceMakerClass = Part::FaceMakerBullseye
  Placement = pos=(0,0,36.15) rot=(0,0,1;0rad)
  Solid = false
  Source = -> Face125
  Symmetric = false
FEATURE [Part::Feature] Face126
  shape: bbox 10 x 16.5 x 2e-07 mm, 1 faces, 0 solids (baked)
FEATURE [Part::Revolution] Revolve131  label="plugHousing058"
  Angle = 360
  Axis = (0,1,0)
  Base = (0,0,0)
  FaceMakerClass = Part::FaceMakerBullseye
  Placement = pos=(0,0,36.15) rot=(0,0,1;0rad)
  Solid = false
  Source = -> Face120
  Symmetric = false
FEATURE [Part::MultiFuse] Fusion099  label="plugHousing053"
  Placement = pos=(0,0,0) rot=(0,0,1;1.5708rad)
  Shapes = -> [Revolve127,Revolve131]
FEATURE [Part::MultiFuse] Fusion102  label="plugHousing056"
  Placement = pos=(0,19,0) rot=(0,0,1;3.14159rad)
  Shapes = -> [Fusion100,Fusion099]
FEATURE [Part::Revolution] Revolve132  label="plugHousing059"
  Angle = 360
  Axis = (0,1,0)
  Base = (0,0,0)
  FaceMakerClass = Part::FaceMakerBullseye
  Placement = pos=(0,0,36.15) rot=(0,0,1;0rad)
  Solid = false
  Source = -> Face126
  Symmetric = false
FEATURE [Part::Revolution] Revolve133  label="plugHousing060"
  Angle = 360
  Axis = (0,1,0)
  Base = (0,0,0)
  FaceMakerClass = Part::FaceMakerBullseye
  Placement = pos=(0,0,36.15) rot=(0,0,1;0rad)
  Solid = false
  Source = -> Face122
  Symmetric = false
FEATURE [Part::MultiFuse] Fusion097  label="plugHousing051"
  Placement = pos=(0,0,0) rot=(0,0,1;1.5708rad)
  Shapes = -> [Revolve133,Revolve132]
FEATURE [Part::Revolution] Revolve134  label="plugHousing061"
  Angle = 360
  Axis = (0,1,0)
  Base = (0,0,0)
  FaceMakerClass = Part::FaceMakerBullseye
  Placement = pos=(0,0,36.15) rot=(0,0,1;0rad)
  Solid = false
  Source = -> Face124
  Symmetric = false
FEATURE [Part::MultiFuse] Fusion101  label="plugHousing055"
  Placement = pos=(0,0,0) rot=(0,0,1;1.5708rad)
  Shapes = -> [Revolve129,Revolve134]
FEATURE [Part::MultiFuse] Fusion098  label="plugHousing052"
  Placement = pos=(0,19,0) rot=(0,0,1;3.14159rad)
  Shapes = -> [Fusion097,Fusion101]
FEATURE [Part::MultiFuse] Fusion103  label="plugHousing057"
  Placement = pos=(122.621,0,-0.15) rot=(0,0,1;0rad)
  Shapes = -> [Fusion102,Fusion098]
FEATURE [Part::Box] Box028  label="Cube015"
  AttacherType = Attacher::AttachEngine3D
  Height = 28
  Length = 3
  Placement = pos=(110.7,19,22) rot=(0,0,1;0rad)
  Width = 15.7
FEATURE [Part::Cylinder] Cylinder044
  Angle = 360
  AttacherType = Attacher::AttachEngine3D
  Height = 20
  Placement = pos=(0,0,36.15) rot=(0,0,1;0rad)
  Radius = 10.3
FEATURE [Part::Cylinder] Cylinder045
  Angle = 360
  AttacherType = Attacher::AttachEngine3D
  Height = 10
  Placement = pos=(0,0,36.15) rot=(0,0,1;0rad)
  Radius = 4
FEATURE [Part::MultiFuse] Fusion104  label="removeToCreteHoleForPlugHousing040"
  Placement = pos=(70,19,36) rot=(0,1,0;1.5708rad)
  Shapes = -> [Cylinder044,Cylinder045]
FEATURE [Part::Cut] Cut046  label="plugHousingTab003"
  Base = -> Box028
  Tool = -> Fusion104
FEATURE [Part::MultiFuse] Fusion105  label="plugHousing062"
  Shapes = -> [Fusion103,Cut046]
FEATURE [Part::Fillet] Fillet042
  Base = -> Fusion105
  Edges = 1 edges r=2: [Edge25]
FEATURE [Part::Fillet] Fillet043  label="plugHousing063"
  Base = -> Fillet042
  Edges = 1 edges r=2: [Edge8]
  Placement = pos=(7,0,0) rot=(0,0,1;0rad)
FEATURE [Part::Feature] Face127
  shape: bbox 10 x 16.5 x 2e-07 mm, 1 faces, 0 solids (baked)
FEATURE [Part::Feature] Face128
  shape: bbox 10 x 16.5 x 2e-07 mm, 1 faces, 0 solids (baked)
FEATURE [Part::Revolution] Revolve137  label="plugHousing070"
  Angle = 360
  Axis = (0,1,0)
  Base = (0,0,0)
  FaceMakerClass = Part::FaceMakerBullseye
  Placement = pos=(0,0,36.15) rot=(0,0,1;0rad)
  Solid = false
  Source = -> Face127
  Symmetric = false
FEATURE [Part::Revolution] Revolve140  label="plugHousing073"
  Angle = 360
  Axis = (0,1,0)
  Base = (0,0,0)
  FaceMakerClass = Part::FaceMakerBullseye
  Placement = pos=(0,0,36.15) rot=(0,0,1;0rad)
  Solid = false
  Source = -> Face128
  Symmetric = false
FEATURE [Part::Feature] Face129
  shape: bbox 10 x 16.5 x 2e-07 mm, 1 faces, 0 solids (baked)
FEATURE [Part::Revolution] Revolve138  label="plugHousing071"
  Angle = 360
  Axis = (0,1,0)
  Base = (0,0,0)
  FaceMakerClass = Part::FaceMakerBullseye
  Placement = pos=(0,0,36.15) rot=(0,0,1;0rad)
  Solid = false
  Source = -> Face129
  Symmetric = false
FEATURE [Part::Feature] Face130
  shape: bbox 10 x 16.5 x 2e-07 mm, 1 faces, 0 solids (baked)
FEATURE [Part::Revolution] Revolve139  label="plugHousing072"
  Angle = 360
  Axis = (0,1,0)
  Base = (0,0,0)
  FaceMakerClass = Part::FaceMakerBullseye
  Placement = pos=(0,0,36.15) rot=(0,0,1;0rad)
  Solid = false
  Source = -> Face130
  Symmetric = false
FEATURE [Part::Feature] Face131
  shape: bbox 10 x 16.5 x 2e-07 mm, 1 faces, 0 solids (baked)
FEATURE [Part::Revolution] Revolve135  label="plugHousing068"
  Angle = 360
  Axis = (0,1,0)
  Base = (0,0,0)
  FaceMakerClass = Part::FaceMakerBullseye
  Placement = pos=(0,0,36.15) rot=(0,0,1;0rad)
  Solid = false
  Source = -> Face131
  Symmetric = false
FEATURE [Part::MultiFuse] Fusion112  label="plugHousing078"
  Placement = pos=(0,0,0) rot=(0,0,1;1.5708rad)
  Shapes = -> [Revolve135,Revolve139]
FEATURE [Part::Feature] Face132
  shape: bbox 10 x 16.5 x 2e-07 mm, 1 faces, 0 solids (baked)
FEATURE [Part::Revolution] Revolve141  label="plugHousing074"
  Angle = 360
  Axis = (0,1,0)
  Base = (0,0,0)
  FaceMakerClass = Part::FaceMakerBullseye
  Placement = pos=(0,0,36.15) rot=(0,0,1;0rad)
  Solid = false
  Source = -> Face132
  Symmetric = false
FEATURE [Part::MultiFuse] Fusion110  label="plugHousing076"
  Placement = pos=(0,0,0) rot=(0,0,1;1.5708rad)
  Shapes = -> [Revolve141,Revolve140]
FEATURE [Part::Feature] Face133
  shape: bbox 10 x 16.5 x 2e-07 mm, 1 faces, 0 solids (baked)
FEATURE [Part::Revolution] Revolve136  label="plugHousing069"
  Angle = 360
  Axis = (0,1,0)
  Base = (0,0,0)
  FaceMakerClass = Part::FaceMakerBullseye
  Placement = pos=(0,0,36.15) rot=(0,0,1;0rad)
  Solid = false
  Source = -> Face133
  Symmetric = false
FEATURE [Part::MultiFuse] Fusion106  label="plugHousing064"
  Placement = pos=(0,0,0) rot=(0,0,1;1.5708rad)
  Shapes = -> [Revolve138,Revolve136]
FEATURE [Part::MultiFuse] Fusion108  label="plugHousing066"
  Placement = pos=(0,19,0) rot=(0,0,1;3.14159rad)
  Shapes = -> [Fusion106,Fusion112]
FEATURE [Part::Feature] Face134
  shape: bbox 10 x 16.5 x 2e-07 mm, 1 faces, 0 solids (baked)
FEATURE [Part::Revolution] Revolve142  label="plugHousing075"
  Angle = 360
  Axis = (0,1,0)
  Base = (0,0,0)
  FaceMakerClass = Part::FaceMakerBullseye
  Placement = pos=(0,0,36.15) rot=(0,0,1;0rad)
  Solid = false
  Source = -> Face134
  Symmetric = false
FEATURE [Part::MultiFuse] Fusion107  label="plugHousing065"
  Placement = pos=(0,0,0) rot=(0,0,1;1.5708rad)
  Shapes = -> [Revolve137,Revolve142]
FEATURE [Part::MultiFuse] Fusion111  label="plugHousing077"
  Placement = pos=(0,19,0) rot=(0,0,1;3.14159rad)
  Shapes = -> [Fusion110,Fusion107]
FEATURE [Part::MultiFuse] Fusion109  label="plugHousing067"
  Placement = pos=(131.236,0,-0.15) rot=(0,0,1;0rad)
  Shapes = -> [Fusion108,Fusion111]
FEATURE [Part::MultiFuse] Fusion113  label="plugHousing079"
  Shapes = -> [Fillet043,Fusion109]
FEATURE [Part::Feature] Face135
  shape: bbox 3.5 x 17.8 x 2e-07 mm, 1 faces, 0 solids (baked)
FEATURE [Part::Revolution] Revolve143  label="removeToCreateScrewAndThreadedInsertHole049"
  Angle = 360
  Axis = (0,1,0)
  Base = (0,0,0)
  FaceMakerClass = Part::FaceMakerBullseye
  Placement = pos=(12.5,0,10) rot=(0,0,1;0rad)
  Solid = false
  Source = -> Face135
  Symmetric = false
FEATURE [Part::Feature] Face136
  shape: bbox 3.5 x 17.8 x 2e-07 mm, 1 faces, 0 solids (baked)
FEATURE [Part::Revolution] Revolve144  label="removeToCreateScrewAndThreadedInsertHole050"
  Angle = 360
  Axis = (0,1,0)
  Base = (0,0,0)
  FaceMakerClass = Part::FaceMakerBullseye
  Placement = pos=(12.5,0,62) rot=(0,0,1;0rad)
  Solid = false
  Source = -> Face136
  Symmetric = false
FEATURE [Part::Feature] Face137
  shape: bbox 3.5 x 17.8 x 2e-07 mm, 1 faces, 0 solids (baked)
FEATURE [Part::Revolution] Revolve145  label="removeToCreateScrewAndThreadedInsertHole051"
  Angle = 360
  Axis = (0,1,0)
  Base = (0,0,0)
  FaceMakerClass = Part::FaceMakerBullseye
  Placement = pos=(89.5,0,68.5) rot=(0,0,1;0rad)
  Solid = false
  Source = -> Face137
  Symmetric = false
FEATURE [Part::Feature] Face138
  shape: bbox 3.5 x 17.8 x 2e-07 mm, 1 faces, 0 solids (baked)
FEATURE [Part::Revolution] Revolve146  label="removeToCreateScrewAndThreadedInsertHole052"
  Angle = 360
  Axis = (0,1,0)
  Base = (0,0,0)
  FaceMakerClass = Part::FaceMakerBullseye
  Placement = pos=(89.5,0,3.5) rot=(0,0,1;0rad)
  Solid = false
  Source = -> Face138
  Symmetric = false
FEATURE [Part::Feature] Face139
  shape: bbox 3.5 x 17.8 x 2e-07 mm, 1 faces, 0 solids (baked)
FEATURE [Part::Revolution] Revolve147  label="removeToCreateScrewAndThreadedInsertHole053"
  Angle = 360
  Axis = (0,1,0)
  Base = (0,0,0)
  FaceMakerClass = Part::FaceMakerBullseye
  Placement = pos=(109.5,4.7,3.5) rot=(0,0,1;0rad)
  Solid = false
  Source = -> Face139
  Symmetric = false
FEATURE [Part::Feature] Face140
  shape: bbox 3.5 x 17.8 x 2e-07 mm, 1 faces, 0 solids (baked)
FEATURE [Part::Revolution] Revolve148  label="removeToCreateScrewAndThreadedInsertHole054"
  Angle = 360
  Axis = (0,1,0)
  Base = (0,0,0)
  FaceMakerClass = Part::FaceMakerBullseye
  Placement = pos=(109.5,4.7,68.5) rot=(0,0,1;0rad)
  Solid = false
  Source = -> Face140
  Symmetric = false
FEATURE [Part::MultiFuse] Fusion114  label="removeToCreateScrewAndThreadedInsertHole055"
  Shapes = -> [Revolve148,Revolve147,Revolve146,Revolve145,Revolve144,Revolve143]
FEATURE [Part::Cut] Cut047  label="casePillars004"
  Base = -> Cut037
  Tool = -> Fusion114
FEATURE [Part::Feature] Face141
  shape: bbox 3.5 x 17.8 x 2e-07 mm, 1 faces, 0 solids (baked)
FEATURE [Part::Feature] Face142
  shape: bbox 3.5 x 17.8 x 2e-07 mm, 1 faces, 0 solids (baked)
FEATURE [Part::Feature] Face143
  shape: bbox 3.5 x 17.8 x 2e-07 mm, 1 faces, 0 solids (baked)
FEATURE [Part::Revolution] Revolve149  label="removeToCreateScrewAndThreadedInsertHole057"
  Angle = 360
  Axis = (0,1,0)
  Base = (0,0,0)
  FaceMakerClass = Part::FaceMakerBullseye
  Placement = pos=(12.5,0,10) rot=(0,0,1;0rad)
  Solid = false
  Source = -> Face141
  Symmetric = false
FEATURE [Part::Feature] Face144
  shape: bbox 3.5 x 17.8 x 2e-07 mm, 1 faces, 0 solids (baked)
FEATURE [Part::Feature] Face145
  shape: bbox 3.5 x 17.8 x 2e-07 mm, 1 faces, 0 solids (baked)
FEATURE [Part::Feature] Face146
  shape: bbox 3.5 x 17.8 x 2e-07 mm, 1 faces, 0 solids (baked)
FEATURE [Part::Revolution] Revolve150  label="removeToCreateScrewAndThreadedInsertHole058"
  Angle = 360
  Axis = (0,1,0)
  Base = (0,0,0)
  FaceMakerClass = Part::FaceMakerBullseye
  Placement = pos=(12.5,0,62) rot=(0,0,1;0rad)
  Solid = false
  Source = -> Face146
  Symmetric = false
FEATURE [Part::Revolution] Revolve151  label="removeToCreateScrewAndThreadedInsertHole059"
  Angle = 360
  Axis = (0,1,0)
  Base = (0,0,0)
  FaceMakerClass = Part::FaceMakerBullseye
  Placement = pos=(89.5,0,68.5) rot=(0,0,1;0rad)
  Solid = false
  Source = -> Face143
  Symmetric = false
FEATURE [Part::Revolution] Revolve152  label="removeToCreateScrewAndThreadedInsertHole060"
  Angle = 360
  Axis = (0,1,0)
  Base = (0,0,0)
  FaceMakerClass = Part::FaceMakerBullseye
  Placement = pos=(89.5,0,3.5) rot=(0,0,1;0rad)
  Solid = false
  Source = -> Face142
  Symmetric = false
FEATURE [Part::Revolution] Revolve153  label="removeToCreateScrewAndThreadedInsertHole061"
  Angle = 360
  Axis = (0,1,0)
  Base = (0,0,0)
  FaceMakerClass = Part::FaceMakerBullseye
  Placement = pos=(109.5,4.7,3.5) rot=(0,0,1;0rad)
  Solid = false
  Source = -> Face145
  Symmetric = false
FEATURE [Part::Revolution] Revolve154  label="removeToCreateScrewAndThreadedInsertHole062"
  Angle = 360
  Axis = (0,1,0)
  Base = (0,0,0)
  FaceMakerClass = Part::FaceMakerBullseye
  Placement = pos=(109.5,4.7,68.5) rot=(0,0,1;0rad)
  Solid = false
  Source = -> Face144
  Symmetric = false
FEATURE [Part::MultiFuse] Fusion115  label="removeToCreateScrewAndThreadedInsertHole056"
  Shapes = -> [Revolve154,Revolve153,Revolve152,Revolve151,Revolve150,Revolve149]
FEATURE [Part::Feature] Face147
  shape: bbox 9.8 x 26.5 x 2e-07 mm, 1 faces, 0 solids (baked)
FEATURE [Part::Revolution] Revolve155
  Angle = 360
  Axis = (0,1,0)
  Base = (0,0,0)
  FaceMakerClass = Part::FaceMakerBullseye
  Placement = pos=(0,0,0) rot=(0,0,1;1.5708rad)
  Solid = false
  Source = -> Face147
  Symmetric = false
FEATURE [Part::Feature] Face148
  shape: bbox 9.8 x 26.5 x 2e-07 mm, 1 faces, 0 solids (baked)
FEATURE [Part::Revolution] Revolve156
  Angle = 360
  Axis = (0,1,0)
  Base = (0,0,0)
  FaceMakerClass = Part::FaceMakerBullseye
  Placement = pos=(0,0,0) rot=(0,0,1;1.5708rad)
  Solid = false
  Source = -> Face148
  Symmetric = false
FEATURE [Part::MultiFuse] Fusion116
  Placement = pos=(-18,19,36) rot=(0,0,1;0rad)
  Shapes = -> [Revolve156,Revolve155]
FEATURE [Part::Box] Box029  label="Cube016"
  AttacherType = Attacher::AttachEngine3D
  Height = 28
  Length = 3
  Placement = pos=(110.7,19,22) rot=(0,0,1;0rad)
  Width = 15.7
FEATURE [Part::Cylinder] Cylinder046
  Angle = 360
  AttacherType = Attacher::AttachEngine3D
  Height = 10
  Placement = pos=(0,0,36.15) rot=(0,0,1;0rad)
  Radius = 4
FEATURE [Part::Cylinder] Cylinder047
  Angle = 360
  AttacherType = Attacher::AttachEngine3D
  Height = 20
  Placement = pos=(0,0,36.15) rot=(0,0,1;0rad)
  Radius = 10.3
FEATURE [Part::MultiFuse] Fusion117  label="removeToCreteHoleForPlugHousing041"
  Placement = pos=(70,19,36) rot=(0,1,0;1.5708rad)
  Shapes = -> [Cylinder047,Cylinder046]
FEATURE [Part::Cut] Cut049  label="plugHousingTab004"
  Base = -> Box029
  Placement = pos=(-107.4,-14,0) rot=(0,0,1;0rad)
  Tool = -> Fusion117
FEATURE [Part::Box] Box030  label="Cube017"
  AttacherType = Attacher::AttachEngine3D
  Height = 28
  Length = 3
  Placement = pos=(110.7,19,22) rot=(0,0,1;0rad)
  Width = 15.7
FEATURE [Part::Cylinder] Cylinder048
  Angle = 360
  AttacherType = Attacher::AttachEngine3D
  Height = 10
  Placement = pos=(0,0,36.15) rot=(0,0,1;0rad)
  Radius = 4
FEATURE [Part::Cylinder] Cylinder049
  Angle = 360
  AttacherType = Attacher::AttachEngine3D
  Height = 20
  Placement = pos=(0,0,36.15) rot=(0,0,1;0rad)
  Radius = 10.3
FEATURE [Part::MultiFuse] Fusion118  label="removeToCreteHoleForPlugHousing042"
  Placement = pos=(70,19,36) rot=(0,1,0;1.5708rad)
  Shapes = -> [Cylinder049,Cylinder048]
FEATURE [Part::Cut] Cut050  label="plugHousingTab005"
  Base = -> Box030
  Placement = pos=(-107.4,-14,0) rot=(0,0,1;0rad)
  Tool = -> Fusion118
FEATURE [Part::MultiFuse] Fusion119
  Placement = pos=(9.6,23,0) rot=(0,0,1;3.14159rad)
  Shapes = -> [Cut049,Cut050]
FEATURE [Part::Box] Box031  label="Cube018"
  AttacherType = Attacher::AttachEngine3D
  Height = 10
  Length = 3
  Placement = pos=(3.3,4,12) rot=(0,0,1;0rad)
  Width = 10
FEATURE [Part::Fillet] Fillet044
  Base = -> Box031
  Edges = 1 edges r=2: [Edge11]
FEATURE [Part::Box] Box032  label="Cube019"
  AttacherType = Attacher::AttachEngine3D
  Height = 10
  Length = 3
  Placement = pos=(3.3,4,50) rot=(0,0,1;0rad)
  Width = 10
FEATURE [Part::Fillet] Fillet045
  Base = -> Box032
  Edges = 1 edges r=2: [Edge12]
FEATURE [Part::Box] Box033  label="Cube020"
  AttacherType = Attacher::AttachEngine3D
  Height = 28
  Length = 4
  Placement = pos=(5,0,22) rot=(0,0,1;0rad)
  Width = 10
FEATURE [Part::Fillet] Fillet046
  Base = -> Box033
  Edges = 1 edges r=1: [Edge7]
FEATURE [Part::Fillet] Fillet047
  Base = -> Fillet046
  Edges = 1 edges r=2: [Edge5]
FEATURE [Part::Fillet] Fillet048
  Base = -> Fillet047
  Edges = 1 edges r=2: [Edge2]
FEATURE [Part::Cylinder] Cylinder050
  Angle = 360
  AttacherType = Attacher::AttachEngine3D
  Height = 20
  Placement = pos=(0,0,36.15) rot=(0,0,1;0rad)
  Radius = 8.2
FEATURE [Part::Cylinder] Cylinder051
  Angle = 360
  AttacherType = Attacher::AttachEngine3D
  Height = 10
  Placement = pos=(0,0,36.15) rot=(0,0,1;0rad)
  Radius = 4
FEATURE [Part::MultiFuse] Fusion120  label="removeToCreteHoleForPlugHousing043"
  Placement = pos=(-42,19,36) rot=(0,1,0;1.5708rad)
  Shapes = -> [Cylinder050,Cylinder051]
FEATURE [Sketcher::SketchObject] Sketch067  label="topSketch018"
  FullyConstrained = true
  sketch-geometry (4):
    g0: LineSegment StartX=16.8446 StartY=31.512 StartZ=0 EndX=16.3251 EndY=34.4666 EndZ=0
    g1: ArcOfCircle CenterX=19 CenterY=19.2524 CenterZ=0 NormalX=0 NormalY=0 NormalZ=1 AngleXU=0 Radius=15.4476 StartAngle=1.74483 EndAngle=2.72717
    g2: ArcOfCircle CenterX=19 CenterY=19.2524 CenterZ=0 NormalX=0 NormalY=0 NormalZ=1 AngleXU=0 Radius=12.4476 StartAngle=1.74483 EndAngle=2.73189
    g3: LineSegment StartX=4.86004 StartY=25.4725 StartZ=0 EndX=7.58253 EndY=24.2107 EndZ=0
  constraints (7):
    c: Block(g0)
    c: Coincident(g1,g0)
    c: Coincident(g2,g0)
    c: Coincident(g3,g1)
    c: Coincident(g3,g2)
    c: Block(g1)
    c: Block(g2)
FEATURE [Part::Extrusion] Extrude058
  Base = -> Sketch067
  Dir = (0,0,1)
  DirMode = 2
  FaceMakerClass = Part::FaceMakerBullseye
  LengthFwd = 10
  LengthRev = 0
  Placement = pos=(0,0,31) rot=(0,0,1;0rad)
  Solid = true
  Symmetric = false
FEATURE [Part::Cut] Cut051
  Base = -> Extrude058
  Tool = -> Fusion120
FEATURE [Part::Fillet] Fillet049
  Base = -> Cut051
  Edges = 1 edges r=2: [Edge1]
FEATURE [Part::Fillet] Fillet050
  Base = -> Fillet049
  Edges = 1 edges r=2.5: [Edge1]
FEATURE [Part::Fillet] Fillet051
  Base = -> Fillet050
  Edges = 1 edges r=2.5: [Edge2]
FEATURE [Part::MultiFuse] Fusion121  label="wireHolder003"
  Shapes = -> [Fusion116,Fillet051]
FEATURE [Part::MultiFuse] Fusion122
  Shapes = -> [Fillet045,Fusion121]
FEATURE [Part::MultiFuse] Fusion123  label="wireHolder004"
  Shapes = -> [Fusion122,Fillet048]
FEATURE [Part::MultiFuse] Fusion124  label="wireHolder005"
  Shapes = -> [Fillet044,Fusion119,Fusion123]
FEATURE [Part::MultiFuse] Fusion126  label="casePillars005"
  Shapes = -> [Fusion092,Cut047]
FEATURE [Sketcher::SketchObject] Sketch068  label="topSketch019"
  FullyConstrained = true
  sketch-geometry (6):
    g0: LineSegment StartX=19 StartY=38 StartZ=0 EndX=117 EndY=38 EndZ=0
    g1: ArcOfCircle CenterX=19 CenterY=19 CenterZ=0 NormalX=0 NormalY=0 NormalZ=1 AngleXU=0 Radius=19 StartAngle=1.5708 EndAngle=3.14159
    g2: LineSegment StartX=117 StartY=38 StartZ=0 EndX=117 EndY=19 EndZ=0
    g3: LineSegment StartX=98 StartY=1.0161e-12 StartZ=0 EndX=5.22862e-06 EndY=1.0161e-12 EndZ=0
    g4: LineSegment StartX=5.22862e-06 StartY=19 StartZ=0 EndX=5.22862e-06 EndY=1.0161e-12 EndZ=0
    g5: ArcOfCircle CenterX=98 CenterY=19 CenterZ=0 NormalX=0 NormalY=0 NormalZ=1 AngleXU=0 Radius=19 StartAngle=4.71239 EndAngle=6.28319
  constraints (16):
    c: Horizontal(g0)
    c: Distance(g0) = 98
    c: Coincident(g1,g0)
    c: Block(g1)
    c: Coincident(g2,g0)
    c: Vertical(g2)
    c: Distance(g2) = 19
    c: Horizontal(g3)
    c: Coincident(g4,g1)
    c: Vertical(g4)
    c: Coincident(g3,g4)
    c: Block(g3)
    c: Coincident(g5,g2)
    c: Coincident(g5,g3)
    c: Block(g0)
    c: Block(g5)
FEATURE [Part::Extrusion] Extrude059  label="sideA002"
  Base = -> Sketch068
  Dir = (0,0,1)
  DirMode = 2
  FaceMakerClass = Part::FaceMakerBullseye
  LengthFwd = 3
  LengthRev = 0
  Placement = pos=(0,0,-2.7) rot=(0,0,1;0rad)
  Solid = true
  Symmetric = false
FEATURE [Sketcher::SketchObject] Sketch069  label="topSketch020"
  FullyConstrained = true
  sketch-geometry (6):
    g0: LineSegment StartX=19 StartY=38 StartZ=0 EndX=117 EndY=38 EndZ=0
    g1: ArcOfCircle CenterX=19 CenterY=19 CenterZ=0 NormalX=0 NormalY=0 NormalZ=1 AngleXU=0 Radius=19 StartAngle=1.5708 EndAngle=3.14159
    g2: LineSegment StartX=117 StartY=38 StartZ=0 EndX=117 EndY=19 EndZ=0
    g3: LineSegment StartX=98 StartY=1.0161e-12 StartZ=0 EndX=5.22862e-06 EndY=1.0161e-12 EndZ=0
    g4: LineSegment StartX=5.22862e-06 StartY=19 StartZ=0 EndX=5.22862e-06 EndY=1.0161e-12 EndZ=0
    g5: ArcOfCircle CenterX=98 CenterY=19 CenterZ=0 NormalX=0 NormalY=0 NormalZ=1 AngleXU=0 Radius=19 StartAngle=4.71239 EndAngle=6.28319
  constraints (16):
    c: Horizontal(g0)
    c: Distance(g0) = 98
    c: Coincident(g1,g0)
    c: Block(g1)
    c: Coincident(g2,g0)
    c: Vertical(g2)
    c: Distance(g2) = 19
    c: Horizontal(g3)
    c: Coincident(g4,g1)
    c: Vertical(g4)
    c: Coincident(g3,g4)
    c: Block(g3)
    c: Coincident(g5,g2)
    c: Coincident(g5,g3)
    c: Block(g0)
    c: Block(g5)
FEATURE [Part::Extrusion] Extrude060  label="sideB002"
  Base = -> Sketch069
  Dir = (0,0,1)
  DirMode = 2
  FaceMakerClass = Part::FaceMakerBullseye
  LengthFwd = 3
  LengthRev = 0
  Placement = pos=(0,0,71.7) rot=(0,0,1;0rad)
  Solid = true
  Symmetric = false
FEATURE [Part::MultiFuse] Fusion127  label="removeFromBottom001"
  Placement = pos=(2,0,0) rot=(0,0,1;0rad)
  Shapes = -> [Extrude059,Extrude060]
FEATURE [Part::Cylinder] Cylinder052
  Angle = 360
  AttacherType = Attacher::AttachEngine3D
  Height = 20
  Placement = pos=(0,0,36.15) rot=(0,0,1;0rad)
  Radius = 14
FEATURE [Part::Cylinder] Cylinder053
  Angle = 360
  AttacherType = Attacher::AttachEngine3D
  Height = 10
  Placement = pos=(0,0,36.15) rot=(0,0,1;0rad)
  Radius = 4
FEATURE [Part::MultiFuse] Fusion128  label="removeToCreteHoleForPlugHousing044"
  Placement = pos=(70,19,36) rot=(0,1,0;1.5708rad)
  Shapes = -> [Cylinder052,Cylinder053]
FEATURE [Part::Cut] Cut052  label="bottom011"
  Base = -> Extrude043
  Tool = -> Fusion128
FEATURE [Part::Cut] Cut054  label="bottom012"
  Base = -> Cut052
  Tool = -> Fusion115
FEATURE [Sketcher::SketchObject] Sketch070
  FullyConstrained = true
  Placement = pos=(117,19,0) rot=(0.57735,0.57735,0.57735;2.0944rad)
  sketch-geometry (48):
    g0: LineSegment StartX=-49.19 StartY=69.25 StartZ=0 EndX=-49.19 EndY=66.25 EndZ=0
    g1: LineSegment StartX=-49.19 StartY=63.5 StartZ=0 EndX=-49.19 EndY=60.5 EndZ=0
    g2: LineSegment StartX=-49.19 StartY=57.75 StartZ=0 EndX=-49.19 EndY=54.75 EndZ=0
    g3: LineSegment StartX=-49.19 StartY=52 StartZ=0 EndX=-49.19 EndY=49 EndZ=0
    g4: LineSegment StartX=-49.19 StartY=46.25 StartZ=0 EndX=-49.19 EndY=43.25 EndZ=0
    g5: LineSegment StartX=-49.19 StartY=40.5 StartZ=0 EndX=-49.19 EndY=37.5 EndZ=0
    g6: LineSegment StartX=-49.19 StartY=34.5 StartZ=0 EndX=-49.19 EndY=31.5 EndZ=0
    g7: LineSegment StartX=-49.19 StartY=28.75 StartZ=0 EndX=-49.19 EndY=25.75 EndZ=0
    g8: LineSegment StartX=-49.19 StartY=23 StartZ=0 EndX=-49.19 EndY=20 EndZ=0
    g9: LineSegment StartX=-49.19 StartY=17.25 StartZ=0 EndX=-49.19 EndY=14.25 EndZ=0
    g10: LineSegment StartX=-49.19 StartY=11.5 StartZ=0 EndX=-49.19 EndY=8.5 EndZ=0
    g11: LineSegment StartX=-49.19 StartY=5.75 StartZ=0 EndX=-49.19 EndY=2.75 EndZ=0
    g12: ArcOfCircle CenterX=-1.5 CenterY=67.75 CenterZ=0 NormalX=0 NormalY=0 NormalZ=1 AngleXU=0 Radius=1.5 StartAngle=4.71239 EndAngle=7.85398
    g13: ArcOfCircle CenterX=-1.5 CenterY=62 CenterZ=0 NormalX=0 NormalY=0 NormalZ=1 AngleXU=0 Radius=1.5 StartAngle=4.71239 EndAngle=7.85398
    g14: ArcOfCircle CenterX=-1.5 CenterY=56.25 CenterZ=0 NormalX=0 NormalY=0 NormalZ=1 AngleXU=0 Radius=1.5 StartAngle=4.71239 EndAngle=7.85398
    g15: ArcOfCircle CenterX=-11.49 CenterY=50.5 CenterZ=0 NormalX=0 NormalY=0 NormalZ=1 AngleXU=0 Radius=1.5 StartAngle=4.71239 EndAngle=7.85398
    g16: ArcOfCircle CenterX=-16.28 CenterY=44.75 CenterZ=0 NormalX=0 NormalY=0 NormalZ=1 AngleXU=0 Radius=1.5 StartAngle=4.71239 EndAngle=7.85398
    g17: ArcOfCircle CenterX=-18.2337 CenterY=39 CenterZ=0 NormalX=0 NormalY=0 NormalZ=1 AngleXU=0 Radius=1.5 StartAngle=4.71485 EndAngle=7.85398
    g18: ArcOfCircle CenterX=-16.2837 CenterY=27.25 CenterZ=0 NormalX=0 NormalY=0 NormalZ=1 AngleXU=0 Radius=1.5 StartAngle=4.71485 EndAngle=7.85398
    g19: ArcOfCircle CenterX=-18.2337 CenterY=33 CenterZ=0 NormalX=0 NormalY=0 NormalZ=1 AngleXU=0 Radius=1.5 StartAngle=4.71485 EndAngle=7.85398
    g20: ArcOfCircle CenterX=-11.49 CenterY=21.5 CenterZ=0 NormalX=0 NormalY=0 NormalZ=1 AngleXU=0 Radius=1.5 StartAngle=4.71239 EndAngle=7.85398
    g21: ArcOfCircle CenterX=-1.5 CenterY=4.25 CenterZ=0 NormalX=0 NormalY=0 NormalZ=1 AngleXU=0 Radius=1.5 StartAngle=4.71239 EndAngle=7.85398
    g22: ArcOfCircle CenterX=-1.5 CenterY=10 CenterZ=0 NormalX=0 NormalY=0 NormalZ=1 AngleXU=0 Radius=1.5 StartAngle=4.71239 EndAngle=7.85398
    g23: ArcOfCircle CenterX=-1.5 CenterY=15.75 CenterZ=0 NormalX=0 NormalY=0 NormalZ=1 AngleXU=0 Radius=1.5 StartAngle=4.71239 EndAngle=7.85398
    g24: LineSegment StartX=-49.19 StartY=69.25 StartZ=0 EndX=-1.5 EndY=69.25 EndZ=0
    g25: LineSegment StartX=-49.19 StartY=66.25 StartZ=0 EndX=-1.5 EndY=66.25 EndZ=0
    g26: LineSegment StartX=-49.19 StartY=63.5 StartZ=0 EndX=-1.5 EndY=63.5 EndZ=0
    g27: LineSegment StartX=-49.19 StartY=60.5 StartZ=0 EndX=-1.5 EndY=60.5 EndZ=0
    g28: LineSegment StartX=-49.19 StartY=57.75 StartZ=0 EndX=-1.5 EndY=57.75 EndZ=0
    g29: LineSegment StartX=-49.19 StartY=54.75 StartZ=0 EndX=-1.5 EndY=54.75 EndZ=0
    g30: LineSegment StartX=-49.19 StartY=52 StartZ=0 EndX=-11.49 EndY=52 EndZ=0
    g31: LineSegment StartX=-49.19 StartY=49 StartZ=0 EndX=-11.49 EndY=49 EndZ=0
    g32: LineSegment StartX=-49.19 StartY=46.25 StartZ=0 EndX=-16.28 EndY=46.25 EndZ=0
    g33: LineSegment StartX=-49.19 StartY=43.25 StartZ=0 EndX=-16.28 EndY=43.25 EndZ=0
    g34: LineSegment StartX=-49.19 StartY=40.5 StartZ=0 EndX=-18.2337 EndY=40.5 EndZ=0
    g35: LineSegment StartX=-49.19 StartY=37.5 StartZ=0 EndX=-18.23 EndY=37.5 EndZ=0
    g36: LineSegment StartX=-49.19 StartY=34.5 StartZ=0 EndX=-18.2337 EndY=34.5 EndZ=0
    g37: LineSegment StartX=-49.19 StartY=31.5 StartZ=0 EndX=-18.23 EndY=31.5 EndZ=0
    g38: LineSegment StartX=-49.19 StartY=28.75 StartZ=0 EndX=-16.2837 EndY=28.75 EndZ=0
    g39: LineSegment StartX=-49.19 StartY=25.75 StartZ=0 EndX=-16.28 EndY=25.75 EndZ=0
    g40: LineSegment StartX=-49.19 StartY=23 StartZ=0 EndX=-11.49 EndY=23 EndZ=0
    g41: LineSegment StartX=-49.19 StartY=20 StartZ=0 EndX=-11.49 EndY=20 EndZ=0
    g42: LineSegment StartX=-49.19 StartY=17.25 StartZ=0 EndX=-1.5 EndY=17.25 EndZ=0
    g43: LineSegment StartX=-49.19 StartY=14.25 StartZ=0 EndX=-1.5 EndY=14.25 EndZ=0
    g44: LineSegment StartX=-49.19 StartY=11.5 StartZ=0 EndX=-1.5 EndY=11.5 EndZ=0
    g45: LineSegment StartX=-49.19 StartY=8.5 StartZ=0 EndX=-1.5 EndY=8.5 EndZ=0
    g46: LineSegment StartX=-49.19 StartY=5.75 StartZ=0 EndX=-1.5 EndY=5.75 EndZ=0
    g47: LineSegment StartX=-49.19 StartY=2.75 StartZ=0 EndX=-1.5 EndY=2.75 EndZ=0
  constraints (120):
    c: Vertical(g0)
    c: Distance(g0) = 3
    c: Block(g0)
    c: Vertical(g1)
    c: Distance(g1) = 3
    c: Vertical(g2)
    c: Equal(g0,g2) = 3
    c: Block(g2)
    c: Vertical(g3)
    c: Equal(g1,g3) = 3
    c: Vertical(g4)
    c: Equal(g0,g4) = 3
    c: Block(g4)
    c: Vertical(g5)
    c: Equal(g1,g5) = 3
    c: Vertical(g6)
    c: Equal(g0,g6) = 3
    c: Block(g6)
    c: Vertical(g7)
    c: Equal(g1,g7) = 3
    c: Vertical(g8)
    c: Equal(g0,g8) = 3
    c: Block(g8)
    c: Vertical(g9)
    c: Equal(g1,g9) = 3
    c: Vertical(g10)
    c: Equal(g0,g10) = 3
    c: Block(g10)
    c: Vertical(g11)
    c: Equal(g1,g11) = 3
    c: Block(g12)
    c: Block(g13)
    c: Block(g14)
    c: Block(g15)
    c: Block(g16)
    c: Block(g17)
    c: Block(g18)
    c: Block(g19)
    c: Block(g20)
    c: Block(g21)
    c: Block(g22)
    c: Block(g23)
    c: Block(g11)
    c: Block(g9)
    c: Block(g7)
    c: Block(g5)
    c: Block(g3)
    c: Block(g1)
    c: Coincident(g24,g0)
    c: Coincident(g24,g12)
    c: Horizontal(g24)
    c: Coincident(g25,g0)
    c: Coincident(g25,g12)
    c: Horizontal(g25)
    c: Coincident(g26,g1)
    c: Coincident(g26,g13)
    c: Horizontal(g26)
    c: Coincident(g27,g1)
    c: Coincident(g27,g13)
    c: Horizontal(g27)
    c: Coincident(g28,g2)
    c: Coincident(g28,g14)
    c: Horizontal(g28)
    c: Coincident(g29,g2)
    c: Coincident(g29,g14)
    c: Horizontal(g29)
    c: Coincident(g30,g3)
    c: Coincident(g30,g15)
    c: Horizontal(g30)
    c: Coincident(g31,g3)
    c: Coincident(g31,g15)
    c: Horizontal(g31)
    c: Coincident(g32,g4)
    c: Coincident(g32,g16)
    c: Horizontal(g32)
    c: Coincident(g33,g4)
    c: Coincident(g33,g16)
    c: Horizontal(g33)
    c: Coincident(g34,g5)
    c: Coincident(g34,g17)
    c: Horizontal(g34)
    c: Coincident(g35,g5)
    c: Coincident(g35,g17)
    c: Horizontal(g35)
    c: Coincident(g36,g6)
    c: Coincident(g36,g19)
    c: Horizontal(g36)
    c: Coincident(g37,g6)
    c: Coincident(g37,g19)
    c: Horizontal(g37)
    c: Coincident(g38,g7)
    c: Coincident(g38,g18)
    c: Horizontal(g38)
    c: Coincident(g39,g7)
    c: Coincident(g39,g18)
    c: Horizontal(g39)
    c: Coincident(g40,g8)
    c: Coincident(g40,g20)
    c: Horizontal(g40)
    c: Coincident(g41,g8)
    c: Coincident(g41,g20)
    c: Horizontal(g41)
    c: Coincident(g42,g9)
    c: Coincident(g42,g23)
    c: Horizontal(g42)
    c: Coincident(g43,g9)
    c: Coincident(g43,g23)
    c: Horizontal(g43)
    c: Coincident(g44,g10)
    c: Coincident(g44,g22)
    c: Horizontal(g44)
    c: Coincident(g45,g10)
    c: Coincident(g45,g22)
    c: Horizontal(g45)
    c: Coincident(g46,g11)
    c: Coincident(g46,g21)
    c: Horizontal(g46)
    c: Coincident(g47,g11)
    c: Coincident(g47,g21)
    c: Horizontal(g47)
FEATURE [Part::Extrusion] Extrude061
  Base = -> Sketch070
  Dir = (1,0,0)
  DirMode = 2
  FaceMakerClass = Part::FaceMakerBullseye
  LengthFwd = 23
  LengthRev = 0
  Placement = pos=(-19,0,0) rot=(0,0,1;0rad)
  Solid = true
  Symmetric = false
FEATURE [Part::Fillet] Fillet052  label="removeToCreateVentalationHoles002"
  Base = -> Extrude061
  Edges = <same value as first occurrence — deduplicated (x6 in doc)>
  Placement = pos=(7,0.02,0) rot=(0,0,1;0rad)
FEATURE [Part::MultiFuse] Fusion130  label="bottom013"
  Shapes = -> [Cut054,Cut034]
FEATURE [Part::Cut] Cut055
  Base = -> Fusion130
  Tool = -> Fillet052
FEATURE [Part::Cylinder] Cylinder054
  Angle = 360
  AttacherType = Attacher::AttachEngine3D
  Height = 20
  Placement = pos=(0,0,36.15) rot=(0,0,1;0rad)
  Radius = 4
FEATURE [Sketcher::SketchObject] Sketch071  label="bottomSketch002"
  FullyConstrained = true
  sketch-geometry (32):
    g0: LineSegment StartX=3.3 StartY=-6.03275e-07 StartZ=0 EndX=98 EndY=-6.03275e-07 EndZ=0
    g1: ArcOfCircle CenterX=98 CenterY=19 CenterZ=0 NormalX=0 NormalY=0 NormalZ=1 AngleXU=0 Radius=19 StartAngle=4.71239 EndAngle=5.71103
    g2: LineSegment StartX=6.3 StartY=8 StartZ=0 EndX=3.3 EndY=8 EndZ=0
    g3: LineSegment StartX=3.3 StartY=8 StartZ=0 EndX=3.3 EndY=-6.03275e-07 EndZ=0
    g4: ArcOfCircle CenterX=8.3 CenterY=5 CenterZ=0 NormalX=0 NormalY=0 NormalZ=1 AngleXU=0 Radius=2 StartAngle=3.14159 EndAngle=4.71239
    g5: LineSegment StartX=6.3 StartY=8 StartZ=0 EndX=6.3 EndY=5 EndZ=0
    g6: ArcOfCircle CenterX=98 CenterY=19 CenterZ=0 NormalX=0 NormalY=0 NormalZ=1 AngleXU=0 Radius=12.7 StartAngle=4.71239 EndAngle=6.28319
    g7: LineSegment StartX=94.7 StartY=3 StartZ=0 EndX=8.3 EndY=3 EndZ=0
    g8-g12: Circle x5 (B-spline internal-alignment scaffolding for g13; pole/knot coordinates omitted)
    g13: BSplineCurve PolesCount=5 KnotsCount=3 Degree=3 IsPeriodic=0
    g14: GeomPoint X=98 Y=6.3 Z=0
    g15: GeomPoint X=96.3938 Y=4.71946 Z=0
    g16: GeomPoint X=94.7 Y=3 Z=0
    g17-g23: Circle x7 (B-spline internal-alignment scaffolding for g24; pole/knot coordinates omitted)
    g24: BSplineCurve PolesCount=7 KnotsCount=5 Degree=3 IsPeriodic=0
    g25-g29: GeomPoint x5 (B-spline internal-alignment scaffolding for g24; pole/knot coordinates omitted)
    g30: ArcOfCircle CenterX=98 CenterY=19 CenterZ=0 NormalX=0 NormalY=0 NormalZ=1 AngleXU=0 Radius=15.7 StartAngle=5.81226 EndAngle=6.28319
    g31: LineSegment StartX=110.7 StartY=19 StartZ=0 EndX=113.7 EndY=19 EndZ=0
  constraints (41):
    c: Horizontal(g0)
    c: Coincident(g1,g0)
    c: Block(g1)
    c: Horizontal(g2)
    c: Distance(g2) = 3
    c: Coincident(g3,g2)
    c: Vertical(g3)
    c: Coincident(g3,g0)
    c: Block(g4)
    c: Block(g2)
    c: Coincident(g5,g2)
    c: Coincident(g5,g4)
    c: Vertical(g5)
    c: Coincident(g6,g1)
    c: Block(g6)
    c: Coincident(g7,g4)
    c: Horizontal(g7)
    c: Block(g0)
    c: Block(g7)
    c: Block(g3)
    c: Coincident(g13,g6)
    c: Weight(g8) = 1
    c: Equal(g8, g9-g12) x4
    c: Coincident(g13,g7)
    c: InternalAlignment(g8-g12 -> g13) x5
    c: InternalAlignment(g14,g13)
    c: InternalAlignment(g15,g13)
    c: InternalAlignment(g16,g13)
    c: Block(g13)
    c: Weight(g17) = 1
    c: Equal(g17, g18-g23) x6
    c: Coincident(g24,g1)
    c: InternalAlignment(g17-g23 -> g24) x7
    c: InternalAlignment(g25-g29 -> g24) x5
    c: Block(g24)
    c: Coincident(g30,g24)
    c: Coincident(g31,g6)
    c: Coincident(g31,g30)
    c: Horizontal(g31)
    c: Block(g31)
    c: Block(g30)
FEATURE [Part::Extrusion] Extrude062  label="bottom014"
  Base = -> Sketch071
  Dir = (0,0,1)
  DirMode = 2
  FaceMakerClass = Part::FaceMakerBullseye
  LengthFwd = 71.4
  LengthRev = 0
  Placement = pos=(0,0,0.3) rot=(0,0,1;0rad)
  Solid = true
  Symmetric = false
FEATURE [Part::Fillet] Fillet054
  Base = -> Extrude062
  Edges = 1 edges r=2.4: [Edge17]
FEATURE [Part::Fillet] Fillet055  label="bottom015"
  Base = -> Fillet054
  Edges = 1 edges r=2.4: [Edge36]
FEATURE [Part::Cylinder] Cylinder055
  Angle = 360
  AttacherType = Attacher::AttachEngine3D
  Height = 10
  Placement = pos=(0,0,36.15) rot=(0,0,1;0rad)
  Radius = 4
FEATURE [Part::MultiFuse] Fusion131  label="removeToCreateHoleForPlugHousing002"
  Placement = pos=(70,19,36.15) rot=(0,1,0;1.5708rad)
  Shapes = -> [Cylinder054,Cylinder055]
FEATURE [Part::Cut] Cut056  label="Bottom001"
  Base = -> Fillet055
  Placement = pos=(9,0,0) rot=(0,0,1;0rad)
  Tool = -> Fusion131
FEATURE [Part::Cut] Cut057
  Base = -> Cut055
  Tool = -> Cut056
FEATURE [Sketcher::SketchObject] Sketch072  label="topSketch021"
  FullyConstrained = true
  sketch-geometry (4):
    g0: ArcOfCircle CenterX=105 CenterY=19 CenterZ=0 NormalX=0 NormalY=0 NormalZ=1 AngleXU=0 Radius=20.6155 StartAngle=5.54125 EndAngle=6.28319
    g1: ArcOfCircle CenterX=105 CenterY=19 CenterZ=0 NormalX=0 NormalY=0 NormalZ=1 AngleXU=0 Radius=13 StartAngle=5.54125 EndAngle=6.28319
    g2: LineSegment StartX=118 StartY=19 StartZ=0 EndX=125.616 EndY=19 EndZ=0
    g3: LineSegment StartX=114.583 StartY=10.2157 StartZ=0 EndX=120.197 EndY=5.06982 EndZ=0
  constraints (7):
    c: Block(g0)
    c: Block(g1)
    c: Coincident(g2,g1)
    c: Coincident(g2,g0)
    c: Horizontal(g2)
    c: Coincident(g3,g1)
    c: Coincident(g3,g0)
FEATURE [Part::Extrusion] Extrude063  label="bottomPlugHousingBit003"
  Base = -> Sketch072
  Dir = (0,0,1)
  DirMode = 2
  FaceMakerClass = Part::FaceMakerBullseye
  LengthFwd = 72
  LengthRev = 0
  Solid = true
  Symmetric = false
FEATURE [Part::Cylinder] Cylinder056
  Angle = 360
  AttacherType = Attacher::AttachEngine3D
  Height = 20
  Placement = pos=(0,0,36.15) rot=(0,0,1;0rad)
  Radius = 14.3
FEATURE [Part::Cylinder] Cylinder057
  Angle = 360
  AttacherType = Attacher::AttachEngine3D
  Height = 10
  Placement = pos=(0,0,36.15) rot=(0,0,1;0rad)
  Radius = 4
FEATURE [Part::Box] Box034  label="removeToCreteHoleForPlugHousing047"
  AttacherType = Attacher::AttachEngine3D
  Height = 28.6
  Length = 20
  Placement = pos=(106.15,0,21.7) rot=(0,0,1;0rad)
  Width = 19
FEATURE [Part::Cylinder] Cylinder058
  Angle = 360
  AttacherType = Attacher::AttachEngine3D
  Height = 20
  Placement = pos=(0,0,36.15) rot=(0,0,1;0rad)
  Radius = 14.3
FEATURE [Part::Cylinder] Cylinder059
  Angle = 360
  AttacherType = Attacher::AttachEngine3D
  Height = 10
  Placement = pos=(0,0,36.15) rot=(0,0,1;0rad)
  Radius = 4
FEATURE [Part::MultiFuse] Fusion134  label="removeToCreteHoleForPlugHousing046"
  Placement = pos=(70,19,36) rot=(0,1,0;1.5708rad)
  Shapes = -> [Cylinder058,Cylinder059]
FEATURE [Part::Cylinder] Cylinder060
  Angle = 360
  AttacherType = Attacher::AttachEngine3D
  Height = 20
  Placement = pos=(0,0,36.15) rot=(0,0,1;0rad)
  Radius = 14
FEATURE [Part::Cylinder] Cylinder061
  Angle = 360
  AttacherType = Attacher::AttachEngine3D
  Height = 10
  Placement = pos=(0,0,36.15) rot=(0,0,1;0rad)
  Radius = 4
FEATURE [Part::MultiFuse] Fusion135  label="removeToCreteHoleForPlugHousing048"
  Placement = pos=(70,19,36) rot=(0,1,0;1.5708rad)
  Shapes = -> [Cylinder060,Cylinder061]
FEATURE [Part::Box] Box035  label="removeToCreteHoleForPlugHousing049"
  AttacherType = Attacher::AttachEngine3D
  Height = 28.6
  Length = 20
  Placement = pos=(106.15,0,21.7) rot=(0,0,1;0rad)
  Width = 19
FEATURE [Part::MultiFuse] Fusion133  label="removeToCreteHoleForPlugHousing045"
  Placement = pos=(0,0,-28.3) rot=(0,0,1;0rad)
  Shapes = -> [Box035,Fusion134]
FEATURE [Part::MultiFuse] Fusion138  label="removeToCreteHoleForPlugHousing051"
  Placement = pos=(70,19,36) rot=(0,1,0;1.5708rad)
  Shapes = -> [Cylinder056,Cylinder057]
FEATURE [Part::MultiFuse] Fusion137  label="removeToCreteHoleForPlugHousing050"
  Placement = pos=(0,0,28.3) rot=(0,0,1;0rad)
  Shapes = -> [Box034,Fusion138]
FEATURE [Part::MultiFuse] Fusion132  label="removeToCreatePlugHousingBottomBit002"
  Shapes = -> [Fusion133,Fusion137]
FEATURE [Part::MultiFuse] Fusion136  label="removeToCreatePlugHousingBottomBit003"
  Shapes = -> [Fusion135,Fusion132]
FEATURE [Part::Cut] Cut058  label="bottomPlugHousingBit002"
  Base = -> Extrude063
  Placement = pos=(-0.09,0,0) rot=(0,0,1;0rad)
  Tool = -> Fusion136
FEATURE [Sketcher::SketchObject] Sketch073  label="bottomSketch003"
  FullyConstrained = true
  sketch-geometry (45):
    g0: LineSegment StartX=6.29999 StartY=8 StartZ=0 EndX=3.29999 EndY=8 EndZ=0
    g1: LineSegment StartX=3.29999 StartY=8 StartZ=0 EndX=3.29999 EndY=-6.03275e-07 EndZ=0
    g2: ArcOfCircle CenterX=8.29999 CenterY=5 CenterZ=0 NormalX=0 NormalY=0 NormalZ=1 AngleXU=0 Radius=2 StartAngle=3.14159 EndAngle=4.71239
    g3: LineSegment StartX=6.29999 StartY=8 StartZ=0 EndX=6.29999 EndY=5 EndZ=0
    g4: ArcOfCircle CenterX=105 CenterY=19 CenterZ=0 NormalX=0 NormalY=0 NormalZ=1 AngleXU=0 Radius=12.7 StartAngle=4.71239 EndAngle=5.94289
    g5-g11: Circle x7 (B-spline internal-alignment scaffolding for g12; pole/knot coordinates omitted)
    g12: BSplineCurve PolesCount=7 KnotsCount=5 Degree=3 IsPeriodic=0
    g13-g17: GeomPoint x5 (B-spline internal-alignment scaffolding for g12; pole/knot coordinates omitted)
    g18: ArcOfCircle CenterX=105 CenterY=19 CenterZ=0 NormalX=0 NormalY=0 NormalZ=1 AngleXU=0 Radius=15.7 StartAngle=5.81226 EndAngle=6.28319
    g19: BSplineCurve PolesCount=5 KnotsCount=3 Degree=3 IsPeriodic=0
    g20: LineSegment StartX=8.29999 StartY=3 StartZ=0 EndX=101.7 EndY=3 EndZ=0
    g21: LineSegment StartX=3.29999 StartY=-6.03275e-07 StartZ=0 EndX=105 EndY=-6.03275e-07 EndZ=0
    g22: LineSegment StartX=120.974 StartY=8.71251 StartZ=0 EndX=122.332 EndY=7.83778 EndZ=0
    g23: LineSegment StartX=105 StartY=-6.03274e-07 StartZ=0 EndX=113 EndY=-6.03274e-07 EndZ=0
    g24: ArcOfCircle CenterX=105 CenterY=19 CenterZ=0 NormalX=0 NormalY=0 NormalZ=1 AngleXU=0 Radius=20.6155 StartAngle=5.11091 EndAngle=5.71103
    g25: ArcOfCircle CenterX=117.7 CenterY=19 CenterZ=0 NormalX=0 NormalY=0 NormalZ=1 AngleXU=0 Radius=3 StartAngle=1.2e-15 EndAngle=2.10468
    g26: Circle CenterX=116.345 CenterY=16.3232 CenterZ=0 NormalX=0 NormalY=0 NormalZ=1 AngleXU=0 Radius=1
    g27: Circle CenterX=117.24 CenterY=15.7584 CenterZ=0 NormalX=0 NormalY=0 NormalZ=1 AngleXU=0 Radius=1
    g28: Circle CenterX=116.972 CenterY=14.7612 CenterZ=0 NormalX=0 NormalY=0 NormalZ=1 AngleXU=0 Radius=1
    g29: BSplineCurve PolesCount=3 KnotsCount=2 Degree=2 IsPeriodic=0
    g30: GeomPoint X=116.345 Y=16.3232 Z=0
    g31: GeomPoint X=116.972 Y=14.7612 Z=0
    g32: Circle CenterX=115.828 CenterY=17.157 CenterZ=0 NormalX=0 NormalY=0 NormalZ=1 AngleXU=0 Radius=1
    g33: Circle CenterX=115.841 CenterY=16.639 CenterZ=0 NormalX=0 NormalY=0 NormalZ=1 AngleXU=0 Radius=1
    g34: Circle CenterX=116.345 CenterY=16.3232 CenterZ=0 NormalX=0 NormalY=0 NormalZ=1 AngleXU=0 Radius=1
    g35: BSplineCurve PolesCount=3 KnotsCount=2 Degree=2 IsPeriodic=0
    g36: GeomPoint X=115.828 Y=17.157 Z=0
    g37: GeomPoint X=116.345 Y=16.3232 Z=0
    g38: LineSegment StartX=115.828 StartY=17.157 StartZ=0 EndX=115.828 EndY=20.8307 EndZ=0
    g39: Circle CenterX=115.828 CenterY=20.8307 CenterZ=0 NormalX=0 NormalY=0 NormalZ=1 AngleXU=0 Radius=1
    g40: Circle CenterX=115.831 CenterY=21.3396 CenterZ=0 NormalX=0 NormalY=0 NormalZ=1 AngleXU=0 Radius=1
    g41: Circle CenterX=116.173 CenterY=21.5825 CenterZ=0 NormalX=0 NormalY=0 NormalZ=1 AngleXU=0 Radius=1
    g42: BSplineCurve PolesCount=3 KnotsCount=2 Degree=2 IsPeriodic=0
    g43: GeomPoint X=115.828 Y=20.8307 Z=0
    g44: GeomPoint X=116.173 Y=21.5825 Z=0
  constraints (70):
    c: Horizontal(g0)
    c: Distance(g0) = 3
    c: Coincident(g1,g0)
    c: Vertical(g1)
    c: Block(g2)
    c: Block(g0)
    c: Coincident(g3,g0)
    c: Coincident(g3,g2)
    c: Vertical(g3)
    c: Block(g1)
    c: Block(g4)
    c: Coincident(g19,g4)
    c: Block(g19)
    c: Equal(g5, g6-g11) x6
    c: InternalAlignment(g5-g11 -> g12) x7
    c: InternalAlignment(g13-g17 -> g12) x5
    c: Block(g12)
    c: Coincident(g18,g12)
    c: Block(g18)
    c: Coincident(g20,g2)
    c: Coincident(g20,g19)
    c: Horizontal(g20)
    c: Distance(g20) = 93.4
    c: Coincident(g21,g1)
    c: Horizontal(g21)
    c: Distance(g21) = 101.7
    c: Horizontal(g23)
    c: Distance(g23) = 8
    c: Coincident(g24,g23)
    c: Block(g23)
    c: Coincident(g22,g24)
    c: Block(g24)
    c: Block(g22)
    c: Distance(g22) = 1.61553
    c: Coincident(g25,g18)
    c: Block(g25)
    c: Weight(g26) = 1
    c: Equal(g26,g27)
    c: Equal(g26,g28)
    c: Coincident(g29,g4)
    c: InternalAlignment(g26,g29)
    c: InternalAlignment(g27,g29)
    c: InternalAlignment(g28,g29)
    c: InternalAlignment(g30,g29)
    c: InternalAlignment(g31,g29)
    c: Block(g29)
    c: Weight(g32) = 1
    c: Equal(g32,g33)
    c: Equal(g32,g34)
    c: Coincident(g35,g29)
    c: InternalAlignment(g32,g35)
    c: InternalAlignment(g33,g35)
    c: InternalAlignment(g34,g35)
    c: InternalAlignment(g36,g35)
    c: InternalAlignment(g37,g35)
    c: Block(g35)
    c: Coincident(g38,g35)
    c: Vertical(g38)
    c: Block(g38)
    c: Coincident(g42,g38)
    c: Weight(g39) = 1
    c: Equal(g39,g40)
    c: Equal(g39,g41)
    c: Coincident(g42,g25)
    c: InternalAlignment(g39,g42)
    c: InternalAlignment(g40,g42)
    c: InternalAlignment(g41,g42)
    c: InternalAlignment(g43,g42)
    c: InternalAlignment(g44,g42)
    c: Block(g42)
FEATURE [Part::Extrusion] Extrude064  label="bottom016"
  Base = -> Sketch073
  Dir = (0,0,1)
  DirMode = 2
  FaceMakerClass = Part::FaceMakerBullseye
  LengthFwd = 71.4
  LengthRev = 0
  Placement = pos=(0,0,0.3) rot=(0,0,1;0rad)
  Solid = true
  Symmetric = false
FEATURE [Part::Revolution] Revolve157  label="removeToCreateScrewAndThreadedInsertHole063"
  Angle = 360
  Axis = (0,1,0)
  Base = (0,0,0)
  FaceMakerClass = Part::FaceMakerBullseye
  Placement = pos=(12.5,0,10) rot=(0,0,1;0rad)
  Solid = false
  Source = -> Face141
  Symmetric = false
FEATURE [Sketcher::SketchObject] Sketch074
  FullyConstrained = true
  Placement = pos=(117,19,0) rot=(0.57735,0.57735,0.57735;2.0944rad)
  sketch-geometry (48):
    g0: LineSegment StartX=-49.19 StartY=69.25 StartZ=0 EndX=-49.19 EndY=66.25 EndZ=0
    g1: LineSegment StartX=-49.19 StartY=63.5 StartZ=0 EndX=-49.19 EndY=60.5 EndZ=0
    g2: LineSegment StartX=-49.19 StartY=57.75 StartZ=0 EndX=-49.19 EndY=54.75 EndZ=0
    g3: LineSegment StartX=-49.19 StartY=52 StartZ=0 EndX=-49.19 EndY=49 EndZ=0
    g4: LineSegment StartX=-49.19 StartY=46.25 StartZ=0 EndX=-49.19 EndY=43.25 EndZ=0
    g5: LineSegment StartX=-49.19 StartY=40.5 StartZ=0 EndX=-49.19 EndY=37.5 EndZ=0
    g6: LineSegment StartX=-49.19 StartY=34.5 StartZ=0 EndX=-49.19 EndY=31.5 EndZ=0
    g7: LineSegment StartX=-49.19 StartY=28.75 StartZ=0 EndX=-49.19 EndY=25.75 EndZ=0
    g8: LineSegment StartX=-49.19 StartY=23 StartZ=0 EndX=-49.19 EndY=20 EndZ=0
    g9: LineSegment StartX=-49.19 StartY=17.25 StartZ=0 EndX=-49.19 EndY=14.25 EndZ=0
    g10: LineSegment StartX=-49.19 StartY=11.5 StartZ=0 EndX=-49.19 EndY=8.5 EndZ=0
    g11: LineSegment StartX=-49.19 StartY=5.75 StartZ=0 EndX=-49.19 EndY=2.75 EndZ=0
    g12: ArcOfCircle CenterX=-1.5 CenterY=67.75 CenterZ=0 NormalX=0 NormalY=0 NormalZ=1 AngleXU=0 Radius=1.5 StartAngle=4.71239 EndAngle=7.85398
    g13: ArcOfCircle CenterX=-1.5 CenterY=62 CenterZ=0 NormalX=0 NormalY=0 NormalZ=1 AngleXU=0 Radius=1.5 StartAngle=4.71239 EndAngle=7.85398
    g14: ArcOfCircle CenterX=-1.5 CenterY=56.25 CenterZ=0 NormalX=0 NormalY=0 NormalZ=1 AngleXU=0 Radius=1.5 StartAngle=4.71239 EndAngle=7.85398
    g15: ArcOfCircle CenterX=-11.49 CenterY=50.5 CenterZ=0 NormalX=0 NormalY=0 NormalZ=1 AngleXU=0 Radius=1.5 StartAngle=4.71239 EndAngle=7.85398
    g16: ArcOfCircle CenterX=-16.28 CenterY=44.75 CenterZ=0 NormalX=0 NormalY=0 NormalZ=1 AngleXU=0 Radius=1.5 StartAngle=4.71239 EndAngle=7.85398
    g17: ArcOfCircle CenterX=-18.2337 CenterY=39 CenterZ=0 NormalX=0 NormalY=0 NormalZ=1 AngleXU=0 Radius=1.5 StartAngle=4.71485 EndAngle=7.85398
    g18: ArcOfCircle CenterX=-16.2837 CenterY=27.25 CenterZ=0 NormalX=0 NormalY=0 NormalZ=1 AngleXU=0 Radius=1.5 StartAngle=4.71485 EndAngle=7.85398
    g19: ArcOfCircle CenterX=-18.2337 CenterY=33 CenterZ=0 NormalX=0 NormalY=0 NormalZ=1 AngleXU=0 Radius=1.5 StartAngle=4.71485 EndAngle=7.85398
    g20: ArcOfCircle CenterX=-11.49 CenterY=21.5 CenterZ=0 NormalX=0 NormalY=0 NormalZ=1 AngleXU=0 Radius=1.5 StartAngle=4.71239 EndAngle=7.85398
    g21: ArcOfCircle CenterX=-1.5 CenterY=4.25 CenterZ=0 NormalX=0 NormalY=0 NormalZ=1 AngleXU=0 Radius=1.5 StartAngle=4.71239 EndAngle=7.85398
    g22: ArcOfCircle CenterX=-1.5 CenterY=10 CenterZ=0 NormalX=0 NormalY=0 NormalZ=1 AngleXU=0 Radius=1.5 StartAngle=4.71239 EndAngle=7.85398
    g23: ArcOfCircle CenterX=-1.5 CenterY=15.75 CenterZ=0 NormalX=0 NormalY=0 NormalZ=1 AngleXU=0 Radius=1.5 StartAngle=4.71239 EndAngle=7.85398
    g24: LineSegment StartX=-49.19 StartY=69.25 StartZ=0 EndX=-1.5 EndY=69.25 EndZ=0
    g25: LineSegment StartX=-49.19 StartY=66.25 StartZ=0 EndX=-1.5 EndY=66.25 EndZ=0
    g26: LineSegment StartX=-49.19 StartY=63.5 StartZ=0 EndX=-1.5 EndY=63.5 EndZ=0
    g27: LineSegment StartX=-49.19 StartY=60.5 StartZ=0 EndX=-1.5 EndY=60.5 EndZ=0
    g28: LineSegment StartX=-49.19 StartY=57.75 StartZ=0 EndX=-1.5 EndY=57.75 EndZ=0
    g29: LineSegment StartX=-49.19 StartY=54.75 StartZ=0 EndX=-1.5 EndY=54.75 EndZ=0
    g30: LineSegment StartX=-49.19 StartY=52 StartZ=0 EndX=-11.49 EndY=52 EndZ=0
    g31: LineSegment StartX=-49.19 StartY=49 StartZ=0 EndX=-11.49 EndY=49 EndZ=0
    g32: LineSegment StartX=-49.19 StartY=46.25 StartZ=0 EndX=-16.28 EndY=46.25 EndZ=0
    g33: LineSegment StartX=-49.19 StartY=43.25 StartZ=0 EndX=-16.28 EndY=43.25 EndZ=0
    g34: LineSegment StartX=-49.19 StartY=40.5 StartZ=0 EndX=-18.2337 EndY=40.5 EndZ=0
    g35: LineSegment StartX=-49.19 StartY=37.5 StartZ=0 EndX=-18.23 EndY=37.5 EndZ=0
    g36: LineSegment StartX=-49.19 StartY=34.5 StartZ=0 EndX=-18.2337 EndY=34.5 EndZ=0
    g37: LineSegment StartX=-49.19 StartY=31.5 StartZ=0 EndX=-18.23 EndY=31.5 EndZ=0
    g38: LineSegment StartX=-49.19 StartY=28.75 StartZ=0 EndX=-16.2837 EndY=28.75 EndZ=0
    g39: LineSegment StartX=-49.19 StartY=25.75 StartZ=0 EndX=-16.28 EndY=25.75 EndZ=0
    g40: LineSegment StartX=-49.19 StartY=23 StartZ=0 EndX=-11.49 EndY=23 EndZ=0
    g41: LineSegment StartX=-49.19 StartY=20 StartZ=0 EndX=-11.49 EndY=20 EndZ=0
    g42: LineSegment StartX=-49.19 StartY=17.25 StartZ=0 EndX=-1.5 EndY=17.25 EndZ=0
    g43: LineSegment StartX=-49.19 StartY=14.25 StartZ=0 EndX=-1.5 EndY=14.25 EndZ=0
    g44: LineSegment StartX=-49.19 StartY=11.5 StartZ=0 EndX=-1.5 EndY=11.5 EndZ=0
    g45: LineSegment StartX=-49.19 StartY=8.5 StartZ=0 EndX=-1.5 EndY=8.5 EndZ=0
    g46: LineSegment StartX=-49.19 StartY=5.75 StartZ=0 EndX=-1.5 EndY=5.75 EndZ=0
    g47: LineSegment StartX=-49.19 StartY=2.75 StartZ=0 EndX=-1.5 EndY=2.75 EndZ=0
  constraints (120):
    c: Vertical(g0)
    c: Distance(g0) = 3
    c: Block(g0)
    c: Vertical(g1)
    c: Distance(g1) = 3
    c: Vertical(g2)
    c: Equal(g0,g2) = 3
    c: Block(g2)
    c: Vertical(g3)
    c: Equal(g1,g3) = 3
    c: Vertical(g4)
    c: Equal(g0,g4) = 3
    c: Block(g4)
    c: Vertical(g5)
    c: Equal(g1,g5) = 3
    c: Vertical(g6)
    c: Equal(g0,g6) = 3
    c: Block(g6)
    c: Vertical(g7)
    c: Equal(g1,g7) = 3
    c: Vertical(g8)
    c: Equal(g0,g8) = 3
    c: Block(g8)
    c: Vertical(g9)
    c: Equal(g1,g9) = 3
    c: Vertical(g10)
    c: Equal(g0,g10) = 3
    c: Block(g10)
    c: Vertical(g11)
    c: Equal(g1,g11) = 3
    c: Block(g12)
    c: Block(g13)
    c: Block(g14)
    c: Block(g15)
    c: Block(g16)
    c: Block(g17)
    c: Block(g18)
    c: Block(g19)
    c: Block(g20)
    c: Block(g21)
    c: Block(g22)
    c: Block(g23)
    c: Block(g11)
    c: Block(g9)
    c: Block(g7)
    c: Block(g5)
    c: Block(g3)
    c: Block(g1)
    c: Coincident(g24,g0)
    c: Coincident(g24,g12)
    c: Horizontal(g24)
    c: Coincident(g25,g0)
    c: Coincident(g25,g12)
    c: Horizontal(g25)
    c: Coincident(g26,g1)
    c: Coincident(g26,g13)
    c: Horizontal(g26)
    c: Coincident(g27,g1)
    c: Coincident(g27,g13)
    c: Horizontal(g27)
    c: Coincident(g28,g2)
    c: Coincident(g28,g14)
    c: Horizontal(g28)
    c: Coincident(g29,g2)
    c: Coincident(g29,g14)
    c: Horizontal(g29)
    c: Coincident(g30,g3)
    c: Coincident(g30,g15)
    c: Horizontal(g30)
    c: Coincident(g31,g3)
    c: Coincident(g31,g15)
    c: Horizontal(g31)
    c: Coincident(g32,g4)
    c: Coincident(g32,g16)
    c: Horizontal(g32)
    c: Coincident(g33,g4)
    c: Coincident(g33,g16)
    c: Horizontal(g33)
    c: Coincident(g34,g5)
    c: Coincident(g34,g17)
    c: Horizontal(g34)
    c: Coincident(g35,g5)
    c: Coincident(g35,g17)
    c: Horizontal(g35)
    c: Coincident(g36,g6)
    c: Coincident(g36,g19)
    c: Horizontal(g36)
    c: Coincident(g37,g6)
    c: Coincident(g37,g19)
    c: Horizontal(g37)
    c: Coincident(g38,g7)
    c: Coincident(g38,g18)
    c: Horizontal(g38)
    c: Coincident(g39,g7)
    c: Coincident(g39,g18)
    c: Horizontal(g39)
    c: Coincident(g40,g8)
    c: Coincident(g40,g20)
    c: Horizontal(g40)
    c: Coincident(g41,g8)
    c: Coincident(g41,g20)
    c: Horizontal(g41)
    c: Coincident(g42,g9)
    c: Coincident(g42,g23)
    c: Horizontal(g42)
    c: Coincident(g43,g9)
    c: Coincident(g43,g23)
    c: Horizontal(g43)
    c: Coincident(g44,g10)
    c: Coincident(g44,g22)
    c: Horizontal(g44)
    c: Coincident(g45,g10)
    c: Coincident(g45,g22)
    c: Horizontal(g45)
    c: Coincident(g46,g11)
    c: Coincident(g46,g21)
    c: Horizontal(g46)
    c: Coincident(g47,g11)
    c: Coincident(g47,g21)
    c: Horizontal(g47)
FEATURE [Part::Extrusion] Extrude065
  Base = -> Sketch074
  Dir = (1,0,0)
  DirMode = 2
  FaceMakerClass = Part::FaceMakerBullseye
  LengthFwd = 23
  LengthRev = 0
  Placement = pos=(-19,0,0) rot=(0,0,1;0rad)
  Solid = true
  Symmetric = false
FEATURE [Part::Fillet] Fillet056  label="removeToCreateVentalationHoles003"
  Base = -> Extrude065
  Edges = <same value as first occurrence — deduplicated (x6 in doc)>
  Placement = pos=(7,0.02,0) rot=(0,0,1;0rad)
FEATURE [Part::Revolution] Revolve158  label="removeToCreateScrewAndThreadedInsertHole065"
  Angle = 360
  Axis = (0,1,0)
  Base = (0,0,0)
  FaceMakerClass = Part::FaceMakerBullseye
  Placement = pos=(12.5,0,62) rot=(0,0,1;0rad)
  Solid = false
  Source = -> Face146
  Symmetric = false
FEATURE [Part::Revolution] Revolve159  label="removeToCreateScrewAndThreadedInsertHole066"
  Angle = 360
  Axis = (0,1,0)
  Base = (0,0,0)
  FaceMakerClass = Part::FaceMakerBullseye
  Placement = pos=(89.5,0,68.5) rot=(0,0,1;0rad)
  Solid = false
  Source = -> Face143
  Symmetric = false
FEATURE [Part::Revolution] Revolve160  label="removeToCreateScrewAndThreadedInsertHole067"
  Angle = 360
  Axis = (0,1,0)
  Base = (0,0,0)
  FaceMakerClass = Part::FaceMakerBullseye
  Placement = pos=(89.5,0,3.5) rot=(0,0,1;0rad)
  Solid = false
  Source = -> Face142
  Symmetric = false
FEATURE [Part::Revolution] Revolve161  label="removeToCreateScrewAndThreadedInsertHole068"
  Angle = 360
  Axis = (0,1,0)
  Base = (0,0,0)
  FaceMakerClass = Part::FaceMakerBullseye
  Placement = pos=(109.5,4.7,3.5) rot=(0,0,1;0rad)
  Solid = false
  Source = -> Face145
  Symmetric = false
FEATURE [Part::Revolution] Revolve162  label="removeToCreateScrewAndThreadedInsertHole069"
  Angle = 360
  Axis = (0,1,0)
  Base = (0,0,0)
  FaceMakerClass = Part::FaceMakerBullseye
  Placement = pos=(109.5,4.7,68.5) rot=(0,0,1;0rad)
  Solid = false
  Source = -> Face144
  Symmetric = false
FEATURE [Part::MultiFuse] Fusion141  label="removeToCreateScrewAndThreadedInsertHole064"
  Shapes = -> [Revolve162,Revolve161,Revolve160,Revolve159,Revolve158,Revolve157]
FEATURE [Part::Cylinder] Cylinder062
  Angle = 360
  AttacherType = Attacher::AttachEngine3D
  Height = 20
  Placement = pos=(0,0,36.15) rot=(0,0,1;0rad)
  Radius = 14
FEATURE [Part::Cylinder] Cylinder063
  Angle = 360
  AttacherType = Attacher::AttachEngine3D
  Height = 10
  Placement = pos=(0,0,36.15) rot=(0,0,1;0rad)
  Radius = 4
FEATURE [Part::MultiFuse] Fusion139  label="removeToCreteHoleForPlugHousing052"
  Placement = pos=(70,19,36) rot=(0,1,0;1.5708rad)
  Shapes = -> [Cylinder062,Cylinder063]
FEATURE [Part::Cut] Cut060  label="bottom017"
  Base = -> Extrude064
  Tool = -> Fusion139
FEATURE [Part::Cut] Cut061  label="bottom019"
  Base = -> Cut060
  Tool = -> Fusion141
FEATURE [Part::MultiFuse] Fusion140  label="bottom018"
  Shapes = -> [Cut061,Cut058]
FEATURE [Part::Cut] Cut059  label="bottom020"
  Base = -> Fusion140
  Tool = -> Fillet056
FEATURE [Part::Box] Box036  label="Cube021"
  AttacherType = Attacher::AttachEngine3D
  Height = 80
  Length = 26
  Placement = pos=(0,-1,-5) rot=(0,0,1;0rad)
  Width = 11
FEATURE [Part::Cut] Cut062  label="removeFromBottom002"
  Base = -> Cut057
  Tool = -> Box036
FEATURE [Part::Cut] Cut063
  Base = -> Cut059
  Tool = -> Cut062
FEATURE [Part::Cut] Cut064  label="pcbStands"
  Base = -> Fusion095
  Tool = -> Fusion127
FEATURE [Sketcher::SketchObject] Sketch075  label="topSketch022"
  FullyConstrained = true
  sketch-geometry (6):
    g0: LineSegment StartX=19 StartY=38 StartZ=0 EndX=117 EndY=38 EndZ=0
    g1: ArcOfCircle CenterX=19 CenterY=19 CenterZ=0 NormalX=0 NormalY=0 NormalZ=1 AngleXU=0 Radius=19 StartAngle=1.5708 EndAngle=3.14159
    g2: LineSegment StartX=117 StartY=38 StartZ=0 EndX=117 EndY=19 EndZ=0
    g3: LineSegment StartX=98 StartY=1.0161e-12 StartZ=0 EndX=5.22862e-06 EndY=1.0161e-12 EndZ=0
    g4: LineSegment StartX=5.22862e-06 StartY=19 StartZ=0 EndX=5.22862e-06 EndY=1.0161e-12 EndZ=0
    g5: ArcOfCircle CenterX=98 CenterY=19 CenterZ=0 NormalX=0 NormalY=0 NormalZ=1 AngleXU=0 Radius=19 StartAngle=4.71239 EndAngle=6.28319
  constraints (16):
    c: Horizontal(g0)
    c: Distance(g0) = 98
    c: Coincident(g1,g0)
    c: Block(g1)
    c: Coincident(g2,g0)
    c: Vertical(g2)
    c: Distance(g2) = 19
    c: Horizontal(g3)
    c: Coincident(g4,g1)
    c: Vertical(g4)
    c: Coincident(g3,g4)
    c: Block(g3)
    c: Coincident(g5,g2)
    c: Coincident(g5,g3)
    c: Block(g0)
    c: Block(g5)
FEATURE [Part::Extrusion] Extrude067  label="sideB003"
  Base = -> Sketch075
  Dir = (0,0,1)
  DirMode = 2
  FaceMakerClass = Part::FaceMakerBullseye
  LengthFwd = 3
  LengthRev = 0
  Placement = pos=(0,0,71.7) rot=(0,0,1;0rad)
  Solid = true
  Symmetric = false
FEATURE [Sketcher::SketchObject] Sketch076  label="topSketch023"
  FullyConstrained = true
  sketch-geometry (6):
    g0: LineSegment StartX=19 StartY=38 StartZ=0 EndX=117 EndY=38 EndZ=0
    g1: ArcOfCircle CenterX=19 CenterY=19 CenterZ=0 NormalX=0 NormalY=0 NormalZ=1 AngleXU=0 Radius=19 StartAngle=1.5708 EndAngle=3.14159
    g2: LineSegment StartX=117 StartY=38 StartZ=0 EndX=117 EndY=19 EndZ=0
    g3: LineSegment StartX=98 StartY=1.0161e-12 StartZ=0 EndX=5.22862e-06 EndY=1.0161e-12 EndZ=0
    g4: LineSegment StartX=5.22862e-06 StartY=19 StartZ=0 EndX=5.22862e-06 EndY=1.0161e-12 EndZ=0
    g5: ArcOfCircle CenterX=98 CenterY=19 CenterZ=0 NormalX=0 NormalY=0 NormalZ=1 AngleXU=0 Radius=19 StartAngle=4.71239 EndAngle=6.28319
  constraints (16):
    c: Horizontal(g0)
    c: Distance(g0) = 98
    c: Coincident(g1,g0)
    c: Block(g1)
    c: Coincident(g2,g0)
    c: Vertical(g2)
    c: Distance(g2) = 19
    c: Horizontal(g3)
    c: Coincident(g4,g1)
    c: Vertical(g4)
    c: Coincident(g3,g4)
    c: Block(g3)
    c: Coincident(g5,g2)
    c: Coincident(g5,g3)
    c: Block(g0)
    c: Block(g5)
FEATURE [Part::Extrusion] Extrude066  label="sideA003"
  Base = -> Sketch076
  Dir = (0,0,1)
  DirMode = 2
  FaceMakerClass = Part::FaceMakerBullseye
  LengthFwd = 3
  LengthRev = 0
  Placement = pos=(0,0,-2.7) rot=(0,0,1;0rad)
  Solid = true
  Symmetric = false
FEATURE [Part::MultiFuse] Fusion142  label="removeFromBottom003"
  Placement = pos=(2,0,0) rot=(0,0,1;0rad)
  Shapes = -> [Extrude066,Extrude067]
FEATURE [Part::Cut] Cut065  label="screwRetainers002"
  Base = -> Fusion096
  Tool = -> Fusion142
